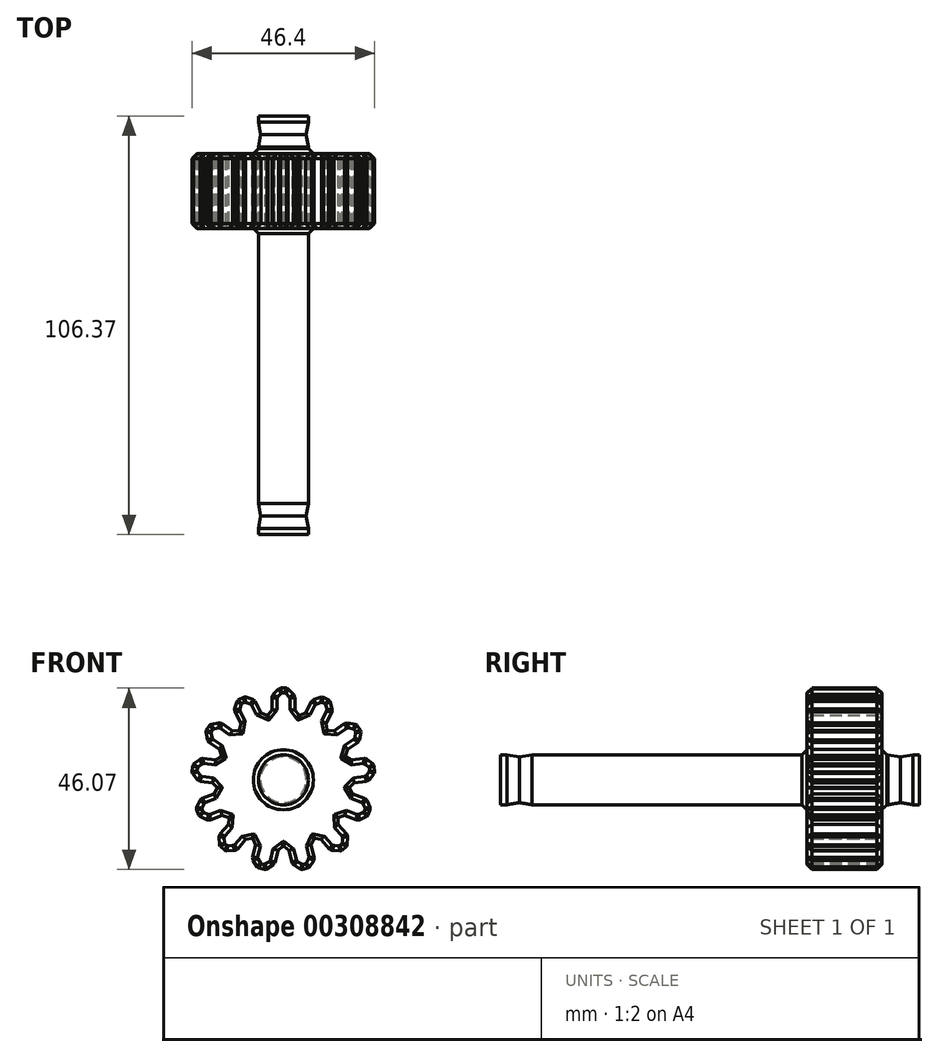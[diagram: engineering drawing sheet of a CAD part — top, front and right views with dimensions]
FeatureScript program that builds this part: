
annotation { "Feature Type Name" : "Feature", "Feature Type Description" : "" }
export const myFeature = defineFeature(function(context is Context, id is Id, definition is map)
    precondition{}
    {
        {
            var Q0;
            Q0=qCreatedBy(makeId("Front.planeOp"),FACE);
            var sketch = newSketch(context, id + "F0", { "sketchPlane" : qUnion([Q0])});
            skCircle(sketch, "E0", {"center": v(0, 0) * mm, "radius": 16.93 * mm});
            skCircle(sketch, "E1", {"center": v(0, 0) * mm, "radius": 6.35 * mm});
            skLineSegment(sketch, "E2.bottom", {"start": v(2.92, 23.28) * mm, "end": v(-2.92, 23.28) * mm});
            skLineSegment(sketch, "E2.top", {"start": v(2.92, 10.58) * mm, "end": v(-2.92, 10.58) * mm});
            skLineSegment(sketch, "E2.left", {"start": v(2.92, 23.28) * mm, "end": v(2.92, 10.58) * mm});
            skLineSegment(sketch, "E2.right", {"start": v(-2.92, 23.28) * mm, "end": v(-2.92, 10.58) * mm});
            skPoint(sketch, "E2.middle", {"position": v(0, 16.93) * mm});
            skLineSegment(sketch, "E3.1.0", {"start": v(7.5, 8.01) * mm, "end": v(2.33, 10.73) * mm});
            skLineSegment(sketch, "E3.1.1", {"start": v(13.4, 19.26) * mm, "end": v(7.5, 8.01) * mm});
            skLineSegment(sketch, "E3.1.2", {"start": v(13.4, 19.26) * mm, "end": v(8.23, 21.97) * mm});
            skLineSegment(sketch, "E3.1.3", {"start": v(8.23, 21.97) * mm, "end": v(2.33, 10.73) * mm});
            skLineSegment(sketch, "E3.2.0", {"start": v(10.37, 3.6) * mm, "end": v(7.05, 8.42) * mm});
            skLineSegment(sketch, "E3.2.1", {"start": v(20.82, 10.82) * mm, "end": v(10.37, 3.6) * mm});
            skLineSegment(sketch, "E3.2.2", {"start": v(20.82, 10.82) * mm, "end": v(17.5, 15.63) * mm});
            skLineSegment(sketch, "E3.2.3", {"start": v(17.5, 15.63) * mm, "end": v(7.05, 8.42) * mm});
            skLineSegment(sketch, "E3.3.0", {"start": v(10.86, -1.62) * mm, "end": v(10.15, 4.18) * mm});
            skLineSegment(sketch, "E3.3.1", {"start": v(23.47, -0.1) * mm, "end": v(10.86, -1.62) * mm});
            skLineSegment(sketch, "E3.3.2", {"start": v(23.47, -0.1) * mm, "end": v(22.76, 5.7) * mm});
            skLineSegment(sketch, "E3.3.3", {"start": v(22.76, 5.7) * mm, "end": v(10.15, 4.18) * mm});
            skLineSegment(sketch, "E3.4.0", {"start": v(8.86, -6.48) * mm, "end": v(10.93, -1.02) * mm});
            skLineSegment(sketch, "E3.4.1", {"start": v(20.73, -10.99) * mm, "end": v(8.86, -6.48) * mm});
            skLineSegment(sketch, "E3.4.2", {"start": v(20.73, -10.99) * mm, "end": v(22.8, -5.53) * mm});
            skLineSegment(sketch, "E3.4.3", {"start": v(22.8, -5.53) * mm, "end": v(10.93, -1.02) * mm});
            skLineSegment(sketch, "E3.5.0", {"start": v(4.83, -9.86) * mm, "end": v(9.2, -5.98) * mm});
            skLineSegment(sketch, "E3.5.1", {"start": v(13.25, -19.36) * mm, "end": v(4.83, -9.86) * mm});
            skLineSegment(sketch, "E3.5.2", {"start": v(13.25, -19.36) * mm, "end": v(17.63, -15.5) * mm});
            skLineSegment(sketch, "E3.5.3", {"start": v(17.63, -15.5) * mm, "end": v(9.2, -5.98) * mm});
            skLineSegment(sketch, "E3.6.0", {"start": v(-0.3, -10.97) * mm, "end": v(5.37, -9.58) * mm});
            skLineSegment(sketch, "E3.6.1", {"start": v(2.74, -23.3) * mm, "end": v(-0.3, -10.97) * mm});
            skLineSegment(sketch, "E3.6.2", {"start": v(2.74, -23.3) * mm, "end": v(8.4, -21.9) * mm});
            skLineSegment(sketch, "E3.6.3", {"start": v(8.4, -21.9) * mm, "end": v(5.37, -9.58) * mm});
            skLineSegment(sketch, "E3.7.0", {"start": v(-5.37, -9.58) * mm, "end": v(0.3, -10.97) * mm});
            skLineSegment(sketch, "E3.7.1", {"start": v(-8.4, -21.9) * mm, "end": v(-5.37, -9.58) * mm});
            skLineSegment(sketch, "E3.7.2", {"start": v(-8.4, -21.9) * mm, "end": v(-2.74, -23.3) * mm});
            skLineSegment(sketch, "E3.7.3", {"start": v(-2.74, -23.3) * mm, "end": v(0.3, -10.97) * mm});
            skLineSegment(sketch, "E3.8.0", {"start": v(-9.2, -5.98) * mm, "end": v(-4.83, -9.86) * mm});
            skLineSegment(sketch, "E3.8.1", {"start": v(-17.63, -15.5) * mm, "end": v(-9.2, -5.98) * mm});
            skLineSegment(sketch, "E3.8.2", {"start": v(-17.63, -15.5) * mm, "end": v(-13.25, -19.36) * mm});
            skLineSegment(sketch, "E3.8.3", {"start": v(-13.25, -19.36) * mm, "end": v(-4.83, -9.86) * mm});
            skLineSegment(sketch, "E3.9.0", {"start": v(-10.93, -1.02) * mm, "end": v(-8.86, -6.48) * mm});
            skLineSegment(sketch, "E3.9.1", {"start": v(-22.8, -5.53) * mm, "end": v(-10.93, -1.02) * mm});
            skLineSegment(sketch, "E3.9.2", {"start": v(-22.8, -5.53) * mm, "end": v(-20.73, -10.99) * mm});
            skLineSegment(sketch, "E3.9.3", {"start": v(-20.73, -10.99) * mm, "end": v(-8.86, -6.48) * mm});
            skLineSegment(sketch, "E3.10.0", {"start": v(-10.15, 4.18) * mm, "end": v(-10.86, -1.62) * mm});
            skLineSegment(sketch, "E3.10.1", {"start": v(-22.76, 5.7) * mm, "end": v(-10.15, 4.18) * mm});
            skLineSegment(sketch, "E3.10.2", {"start": v(-22.76, 5.7) * mm, "end": v(-23.47, -0.1) * mm});
            skLineSegment(sketch, "E3.10.3", {"start": v(-23.47, -0.1) * mm, "end": v(-10.86, -1.62) * mm});
            skLineSegment(sketch, "E3.11.0", {"start": v(-7.05, 8.42) * mm, "end": v(-10.37, 3.6) * mm});
            skLineSegment(sketch, "E3.11.1", {"start": v(-17.5, 15.63) * mm, "end": v(-7.05, 8.42) * mm});
            skLineSegment(sketch, "E3.11.2", {"start": v(-17.5, 15.63) * mm, "end": v(-20.82, 10.82) * mm});
            skLineSegment(sketch, "E3.11.3", {"start": v(-20.82, 10.82) * mm, "end": v(-10.37, 3.6) * mm});
            skLineSegment(sketch, "E3.12.0", {"start": v(-2.33, 10.73) * mm, "end": v(-7.5, 8.01) * mm});
            skLineSegment(sketch, "E3.12.1", {"start": v(-8.23, 21.97) * mm, "end": v(-2.33, 10.73) * mm});
            skLineSegment(sketch, "E3.12.2", {"start": v(-8.23, 21.97) * mm, "end": v(-13.4, 19.26) * mm});
            skLineSegment(sketch, "E3.12.3", {"start": v(-13.4, 19.26) * mm, "end": v(-7.5, 8.01) * mm});
            skLineSegment(sketch, "E3.anchor1", {"start": v(0, 0) * mm, "end": v(2.92, 10.58) * mm, "construction": true});
            skLineSegment(sketch, "E3.anchor2", {"start": v(0, 0) * mm, "end": v(-2.33, 10.73) * mm, "construction": true});
            skSolve(sketch);
        }
        {
            var Q0;
            {var subQ0=sQuery(id+"F0.wireOp",EDGE,"E2.left");var subQ1=sQuery(id+"F0.wireOp",EDGE,"E2.top");var subQ2=makeQuery(id+"F0.imprint","INTERSECT",VERTEX,{"derivedFrom":[subQ1,subQ0]});Q0=makeQuery(id+"F0.imprint","IMPRINT",FACE,{"disambiguationData":[TD([[makeQuery(id+"F0.imprint","IMPRINT",EDGE,{"disambiguationData":[TD([[subQ2,-1.0]])],"derivedFrom":subQ1}),-1.0]])]});}
            var Q1;
            {var subQ0=sQuery(id+"F0.wireOp",EDGE,"E2.right");var subQ1=sQuery(id+"F0.wireOp",EDGE,"E2.top");var subQ2=makeQuery(id+"F0.imprint","INTERSECT",VERTEX,{"derivedFrom":[subQ1,subQ0]});Q1=makeQuery(id+"F0.imprint","IMPRINT",FACE,{"disambiguationData":[TD([[makeQuery(id+"F0.imprint","IMPRINT",EDGE,{"disambiguationData":[TD([[subQ2,1.0]])],"derivedFrom":subQ1}),-1.0]])]});}
            var Q2;
            {var subQ0=sQuery(id+"F0.wireOp",EDGE,"E3.11.1");var subQ1=sQuery(id+"F0.wireOp",EDGE,"E3.11.0");var subQ2=makeQuery(id+"F0.imprint","INTERSECT",VERTEX,{"derivedFrom":[subQ1,subQ0]});Q2=makeQuery(id+"F0.imprint","IMPRINT",FACE,{"disambiguationData":[TD([[makeQuery(id+"F0.imprint","IMPRINT",EDGE,{"disambiguationData":[TD([[subQ2,-1.0]])],"derivedFrom":subQ1}),-1.0]])]});}
            var Q3;
            {var subQ0=sQuery(id+"F0.wireOp",EDGE,"E3.10.1");var subQ1=sQuery(id+"F0.wireOp",EDGE,"E3.10.0");var subQ2=makeQuery(id+"F0.imprint","INTERSECT",VERTEX,{"derivedFrom":[subQ1,subQ0]});Q3=makeQuery(id+"F0.imprint","IMPRINT",FACE,{"disambiguationData":[TD([[makeQuery(id+"F0.imprint","IMPRINT",EDGE,{"disambiguationData":[TD([[subQ2,-1.0]])],"derivedFrom":subQ1}),-1.0]])]});}
            var Q4;
            {var subQ0=sQuery(id+"F0.wireOp",EDGE,"E3.2.1");var subQ1=sQuery(id+"F0.wireOp",EDGE,"E0");var subQ2=makeQuery(id+"F0.imprint","INTERSECT",VERTEX,{"derivedFrom":[subQ1,subQ0]});Q4=makeQuery(id+"F0.imprint","IMPRINT",FACE,{"disambiguationData":[TD([[makeQuery(id+"F0.imprint","IMPRINT",EDGE,{"disambiguationData":[TD([[subQ2,1.0]])],"derivedFrom":subQ1}),1.0]])]});}
            var Q5;
            {var subQ11=sQuery(id+"F0.wireOp",EDGE,"E3.10.1");var subQ12=sQuery(id+"F0.wireOp",EDGE,"E0");var subQ13=makeQuery(id+"F0.imprint","INTERSECT",VERTEX,{"derivedFrom":[subQ12,subQ11]});Q5=makeQuery(id+"F0.imprint","IMPRINT",FACE,{"disambiguationData":[TD([[makeQuery(id+"F0.imprint","IMPRINT",EDGE,{"disambiguationData":[TD([[subQ13,-1.0]])],"derivedFrom":subQ12}),1.0]])]});}
            var Q6;
            {var subQ11=sQuery(id+"F0.wireOp",EDGE,"E3.5.1");var subQ12=sQuery(id+"F0.wireOp",EDGE,"E0");var subQ13=makeQuery(id+"F0.imprint","INTERSECT",VERTEX,{"derivedFrom":[subQ12,subQ11]});Q6=makeQuery(id+"F0.imprint","IMPRINT",FACE,{"disambiguationData":[TD([[makeQuery(id+"F0.imprint","IMPRINT",EDGE,{"disambiguationData":[TD([[subQ13,-1.0]])],"derivedFrom":subQ12}),1.0]])]});}
            var Q7;
            {var subQ5=sQuery(id+"F0.wireOp",EDGE,"E3.12.2");Q7=makeQuery(id+"F0.imprint","IMPRINT",FACE,{"disambiguationData":[TD([[makeQuery(id+"F0.imprint","IMPRINT",EDGE,{"derivedFrom":subQ5}),1.0]])]});}
            var Q8;
            {var subQ0=sQuery(id+"F0.wireOp",EDGE,"E3.4.3");var subQ1=sQuery(id+"F0.wireOp",EDGE,"E0");var subQ2=makeQuery(id+"F0.imprint","INTERSECT",VERTEX,{"derivedFrom":[subQ1,subQ0]});Q8=makeQuery(id+"F0.imprint","IMPRINT",FACE,{"disambiguationData":[TD([[makeQuery(id+"F0.imprint","IMPRINT",EDGE,{"disambiguationData":[TD([[subQ2,-1.0]])],"derivedFrom":subQ1}),1.0]])]});}
            var Q9;
            {var subQ0=sQuery(id+"F0.wireOp",EDGE,"E3.12.3");var subQ1=sQuery(id+"F0.wireOp",EDGE,"E0");var subQ2=makeQuery(id+"F0.imprint","INTERSECT",VERTEX,{"derivedFrom":[subQ1,subQ0]});Q9=makeQuery(id+"F0.imprint","IMPRINT",FACE,{"disambiguationData":[TD([[makeQuery(id+"F0.imprint","IMPRINT",EDGE,{"disambiguationData":[TD([[subQ2,-1.0]])],"derivedFrom":subQ1}),1.0]])]});}
            var Q10;
            {var subQ0=sQuery(id+"F0.wireOp",EDGE,"E3.6.3");var subQ1=sQuery(id+"F0.wireOp",EDGE,"E0");var subQ2=makeQuery(id+"F0.imprint","INTERSECT",VERTEX,{"derivedFrom":[subQ1,subQ0]});Q10=makeQuery(id+"F0.imprint","IMPRINT",FACE,{"disambiguationData":[TD([[makeQuery(id+"F0.imprint","IMPRINT",EDGE,{"disambiguationData":[TD([[subQ2,-1.0]])],"derivedFrom":subQ1}),1.0]])]});}
            var Q11;
            {var subQ5=sQuery(id+"F0.wireOp",EDGE,"E3.1.2");Q11=makeQuery(id+"F0.imprint","IMPRINT",FACE,{"disambiguationData":[TD([[makeQuery(id+"F0.imprint","IMPRINT",EDGE,{"derivedFrom":subQ5}),1.0]])]});}
            var Q12;
            {var subQ5=sQuery(id+"F0.wireOp",EDGE,"E3.9.2");Q12=makeQuery(id+"F0.imprint","IMPRINT",FACE,{"disambiguationData":[TD([[makeQuery(id+"F0.imprint","IMPRINT",EDGE,{"derivedFrom":subQ5}),1.0]])]});}
            var Q13;
            {var subQ5=sQuery(id+"F0.wireOp",EDGE,"E3.7.2");Q13=makeQuery(id+"F0.imprint","IMPRINT",FACE,{"disambiguationData":[TD([[makeQuery(id+"F0.imprint","IMPRINT",EDGE,{"derivedFrom":subQ5}),1.0]])]});}
            var Q14;
            {var subQ11=sQuery(id+"F0.wireOp",EDGE,"E3.7.1");var subQ12=sQuery(id+"F0.wireOp",EDGE,"E0");var subQ13=makeQuery(id+"F0.imprint","INTERSECT",VERTEX,{"derivedFrom":[subQ12,subQ11]});Q14=makeQuery(id+"F0.imprint","IMPRINT",FACE,{"disambiguationData":[TD([[makeQuery(id+"F0.imprint","IMPRINT",EDGE,{"disambiguationData":[TD([[subQ13,-1.0]])],"derivedFrom":subQ12}),1.0]])]});}
            var Q15;
            {var subQ5=sQuery(id+"F0.wireOp",EDGE,"E3.5.2");Q15=makeQuery(id+"F0.imprint","IMPRINT",FACE,{"disambiguationData":[TD([[makeQuery(id+"F0.imprint","IMPRINT",EDGE,{"derivedFrom":subQ5}),1.0]])]});}
            var Q16;
            {var subQ11=sQuery(id+"F0.wireOp",EDGE,"E3.6.1");var subQ12=sQuery(id+"F0.wireOp",EDGE,"E0");var subQ13=makeQuery(id+"F0.imprint","INTERSECT",VERTEX,{"derivedFrom":[subQ12,subQ11]});Q16=makeQuery(id+"F0.imprint","IMPRINT",FACE,{"disambiguationData":[TD([[makeQuery(id+"F0.imprint","IMPRINT",EDGE,{"disambiguationData":[TD([[subQ13,-1.0]])],"derivedFrom":subQ12}),1.0]])]});}
            var Q17;
            {var subQ5=sQuery(id+"F0.wireOp",EDGE,"E3.4.2");Q17=makeQuery(id+"F0.imprint","IMPRINT",FACE,{"disambiguationData":[TD([[makeQuery(id+"F0.imprint","IMPRINT",EDGE,{"derivedFrom":subQ5}),1.0]])]});}
            var Q18;
            {var subQ11=sQuery(id+"F0.wireOp",EDGE,"E3.11.1");var subQ12=sQuery(id+"F0.wireOp",EDGE,"E0");var subQ13=makeQuery(id+"F0.imprint","INTERSECT",VERTEX,{"derivedFrom":[subQ12,subQ11]});Q18=makeQuery(id+"F0.imprint","IMPRINT",FACE,{"disambiguationData":[TD([[makeQuery(id+"F0.imprint","IMPRINT",EDGE,{"disambiguationData":[TD([[subQ13,-1.0]])],"derivedFrom":subQ12}),1.0]])]});}
            var Q19;
            {var subQ0=sQuery(id+"F0.wireOp",EDGE,"E3.8.3");var subQ1=sQuery(id+"F0.wireOp",EDGE,"E0");var subQ2=makeQuery(id+"F0.imprint","INTERSECT",VERTEX,{"derivedFrom":[subQ1,subQ0]});Q19=makeQuery(id+"F0.imprint","IMPRINT",FACE,{"disambiguationData":[TD([[makeQuery(id+"F0.imprint","IMPRINT",EDGE,{"disambiguationData":[TD([[subQ2,-1.0]])],"derivedFrom":subQ1}),1.0]])]});}
            var Q20;
            {var subQ0=sQuery(id+"F0.wireOp",EDGE,"E3.1.3");var subQ1=sQuery(id+"F0.wireOp",EDGE,"E0");var subQ2=makeQuery(id+"F0.imprint","INTERSECT",VERTEX,{"derivedFrom":[subQ1,subQ0]});Q20=makeQuery(id+"F0.imprint","IMPRINT",FACE,{"disambiguationData":[TD([[makeQuery(id+"F0.imprint","IMPRINT",EDGE,{"disambiguationData":[TD([[subQ2,-1.0]])],"derivedFrom":subQ1}),1.0]])]});}
            var Q21;
            {var subQ5=sQuery(id+"F0.wireOp",EDGE,"E2.bottom");Q21=makeQuery(id+"F0.imprint","IMPRINT",FACE,{"disambiguationData":[TD([[makeQuery(id+"F0.imprint","IMPRINT",EDGE,{"derivedFrom":subQ5}),1.0]])]});}
            var Q22;
            {var subQ5=sQuery(id+"F0.wireOp",EDGE,"E3.3.2");Q22=makeQuery(id+"F0.imprint","IMPRINT",FACE,{"disambiguationData":[TD([[makeQuery(id+"F0.imprint","IMPRINT",EDGE,{"derivedFrom":subQ5}),1.0]])]});}
            var Q23;
            {var subQ0=sQuery(id+"F0.wireOp",EDGE,"E3.11.3");var subQ1=sQuery(id+"F0.wireOp",EDGE,"E0");var subQ2=makeQuery(id+"F0.imprint","INTERSECT",VERTEX,{"derivedFrom":[subQ1,subQ0]});Q23=makeQuery(id+"F0.imprint","IMPRINT",FACE,{"disambiguationData":[TD([[makeQuery(id+"F0.imprint","IMPRINT",EDGE,{"disambiguationData":[TD([[subQ2,-1.0]])],"derivedFrom":subQ1}),1.0]])]});}
            var Q24;
            {var subQ0=sQuery(id+"F0.wireOp",EDGE,"E3.7.3");var subQ1=sQuery(id+"F0.wireOp",EDGE,"E0");var subQ2=makeQuery(id+"F0.imprint","INTERSECT",VERTEX,{"derivedFrom":[subQ1,subQ0]});Q24=makeQuery(id+"F0.imprint","IMPRINT",FACE,{"disambiguationData":[TD([[makeQuery(id+"F0.imprint","IMPRINT",EDGE,{"disambiguationData":[TD([[subQ2,-1.0]])],"derivedFrom":subQ1}),1.0]])]});}
            var Q25;
            {var subQ5=sQuery(id+"F0.wireOp",EDGE,"E3.2.2");Q25=makeQuery(id+"F0.imprint","IMPRINT",FACE,{"disambiguationData":[TD([[makeQuery(id+"F0.imprint","IMPRINT",EDGE,{"derivedFrom":subQ5}),1.0]])]});}
            var Q26;
            {var subQ5=sQuery(id+"F0.wireOp",EDGE,"E3.6.2");Q26=makeQuery(id+"F0.imprint","IMPRINT",FACE,{"disambiguationData":[TD([[makeQuery(id+"F0.imprint","IMPRINT",EDGE,{"derivedFrom":subQ5}),1.0]])]});}
            var Q27;
            {var subQ5=sQuery(id+"F0.wireOp",EDGE,"E3.11.2");Q27=makeQuery(id+"F0.imprint","IMPRINT",FACE,{"disambiguationData":[TD([[makeQuery(id+"F0.imprint","IMPRINT",EDGE,{"derivedFrom":subQ5}),1.0]])]});}
            var Q28;
            {var subQ11=sQuery(id+"F0.wireOp",EDGE,"E3.8.1");var subQ12=sQuery(id+"F0.wireOp",EDGE,"E0");var subQ13=makeQuery(id+"F0.imprint","INTERSECT",VERTEX,{"derivedFrom":[subQ12,subQ11]});Q28=makeQuery(id+"F0.imprint","IMPRINT",FACE,{"disambiguationData":[TD([[makeQuery(id+"F0.imprint","IMPRINT",EDGE,{"disambiguationData":[TD([[subQ13,-1.0]])],"derivedFrom":subQ12}),1.0]])]});}
            var Q29;
            {var subQ5=sQuery(id+"F0.wireOp",EDGE,"E3.10.2");Q29=makeQuery(id+"F0.imprint","IMPRINT",FACE,{"disambiguationData":[TD([[makeQuery(id+"F0.imprint","IMPRINT",EDGE,{"derivedFrom":subQ5}),1.0]])]});}
            var Q30;
            {var subQ3=sQuery(id+"F0.wireOp",EDGE,"E3.12.1");var subQ7=sQuery(id+"F0.wireOp",EDGE,"E0");var subQ8=makeQuery(id+"F0.imprint","INTERSECT",VERTEX,{"derivedFrom":[subQ7,subQ3]});Q30=makeQuery(id+"F0.imprint","IMPRINT",FACE,{"disambiguationData":[TD([[makeQuery(id+"F0.imprint","IMPRINT",EDGE,{"disambiguationData":[TD([[subQ8,-1.0]])],"derivedFrom":subQ7}),1.0]])]});}
            var Q31;
            {var subQ7=sQuery(id+"F0.wireOp",EDGE,"E3.3.3");var subQ8=sQuery(id+"F0.wireOp",EDGE,"E0");var subQ9=makeQuery(id+"F0.imprint","INTERSECT",VERTEX,{"derivedFrom":[subQ8,subQ7]});Q31=makeQuery(id+"F0.imprint","IMPRINT",FACE,{"disambiguationData":[TD([[makeQuery(id+"F0.imprint","IMPRINT",EDGE,{"disambiguationData":[TD([[subQ9,1.0]])],"derivedFrom":subQ8}),1.0]])]});}
            var Q32;
            {var subQ0=sQuery(id+"F0.wireOp",EDGE,"E3.2.3");var subQ1=sQuery(id+"F0.wireOp",EDGE,"E0");var subQ2=makeQuery(id+"F0.imprint","INTERSECT",VERTEX,{"derivedFrom":[subQ1,subQ0]});Q32=makeQuery(id+"F0.imprint","IMPRINT",FACE,{"disambiguationData":[TD([[makeQuery(id+"F0.imprint","IMPRINT",EDGE,{"disambiguationData":[TD([[subQ2,-1.0]])],"derivedFrom":subQ1}),1.0]])]});}
            var Q33;
            {var subQ0=sQuery(id+"F0.wireOp",EDGE,"E3.5.3");var subQ1=sQuery(id+"F0.wireOp",EDGE,"E0");var subQ2=makeQuery(id+"F0.imprint","INTERSECT",VERTEX,{"derivedFrom":[subQ1,subQ0]});Q33=makeQuery(id+"F0.imprint","IMPRINT",FACE,{"disambiguationData":[TD([[makeQuery(id+"F0.imprint","IMPRINT",EDGE,{"disambiguationData":[TD([[subQ2,-1.0]])],"derivedFrom":subQ1}),1.0]])]});}
            var Q34;
            {var subQ0=sQuery(id+"F0.wireOp",EDGE,"E3.9.3");var subQ1=sQuery(id+"F0.wireOp",EDGE,"E0");var subQ2=makeQuery(id+"F0.imprint","INTERSECT",VERTEX,{"derivedFrom":[subQ1,subQ0]});Q34=makeQuery(id+"F0.imprint","IMPRINT",FACE,{"disambiguationData":[TD([[makeQuery(id+"F0.imprint","IMPRINT",EDGE,{"disambiguationData":[TD([[subQ2,-1.0]])],"derivedFrom":subQ1}),1.0]])]});}
            var Q35;
            {var subQ5=sQuery(id+"F0.wireOp",EDGE,"E3.8.2");Q35=makeQuery(id+"F0.imprint","IMPRINT",FACE,{"disambiguationData":[TD([[makeQuery(id+"F0.imprint","IMPRINT",EDGE,{"derivedFrom":subQ5}),1.0]])]});}
            var Q36;
            {var subQ0=sQuery(id+"F0.wireOp",EDGE,"E2.left");var subQ1=sQuery(id+"F0.wireOp",EDGE,"E0");var subQ2=makeQuery(id+"F0.imprint","INTERSECT",VERTEX,{"derivedFrom":[subQ1,subQ0]});Q36=makeQuery(id+"F0.imprint","IMPRINT",FACE,{"disambiguationData":[TD([[makeQuery(id+"F0.imprint","IMPRINT",EDGE,{"disambiguationData":[TD([[subQ2,-1.0]])],"derivedFrom":subQ1}),1.0]])]});}
            var Q37;
            {var subQ0=sQuery(id+"F0.wireOp",EDGE,"E2.right");var subQ1=sQuery(id+"F0.wireOp",EDGE,"E0");var subQ2=makeQuery(id+"F0.imprint","INTERSECT",VERTEX,{"derivedFrom":[subQ1,subQ0]});Q37=makeQuery(id+"F0.imprint","IMPRINT",FACE,{"disambiguationData":[TD([[makeQuery(id+"F0.imprint","IMPRINT",EDGE,{"disambiguationData":[TD([[subQ2,-1.0]])],"derivedFrom":subQ1}),1.0]])]});}
            var Q38;
            {var subQ0=sQuery(id+"F0.wireOp",EDGE,"E3.10.3");var subQ1=sQuery(id+"F0.wireOp",EDGE,"E0");var subQ2=makeQuery(id+"F0.imprint","INTERSECT",VERTEX,{"derivedFrom":[subQ1,subQ0]});Q38=makeQuery(id+"F0.imprint","IMPRINT",FACE,{"disambiguationData":[TD([[makeQuery(id+"F0.imprint","IMPRINT",EDGE,{"disambiguationData":[TD([[subQ2,-1.0]])],"derivedFrom":subQ1}),1.0]])]});}
            var Q39;
            Q39=makeQuery(id+"F0.imprint","IMPRINT",FACE,{"disambiguationData":[TD([[makeQuery(id+"F0.imprint","IMPRINT",EDGE,{"derivedFrom":sQuery(id+"F0.wireOp",EDGE,"E1")}),-1.0]])]});
            var Q40;
            {var subQ0=sQuery(id+"F0.wireOp",EDGE,"E3.9.1");var subQ1=sQuery(id+"F0.wireOp",EDGE,"E3.9.0");var subQ2=makeQuery(id+"F0.imprint","INTERSECT",VERTEX,{"derivedFrom":[subQ1,subQ0]});Q40=makeQuery(id+"F0.imprint","IMPRINT",FACE,{"disambiguationData":[TD([[makeQuery(id+"F0.imprint","IMPRINT",EDGE,{"disambiguationData":[TD([[subQ2,-1.0]])],"derivedFrom":subQ1}),-1.0]])]});}
            var Q41;
            {var subQ5=sQuery(id+"F0.wireOp",EDGE,"E3.9.1");var subQ6=sQuery(id+"F0.wireOp",EDGE,"E0");var subQ7=makeQuery(id+"F0.imprint","INTERSECT",VERTEX,{"derivedFrom":[subQ6,subQ5]});Q41=makeQuery(id+"F0.imprint","IMPRINT",FACE,{"disambiguationData":[TD([[makeQuery(id+"F0.imprint","IMPRINT",EDGE,{"disambiguationData":[TD([[subQ7,-1.0]])],"derivedFrom":subQ6}),1.0]])]});}
            var Q42;
            {var subQ0=sQuery(id+"F0.wireOp",EDGE,"E3.7.1");var subQ1=sQuery(id+"F0.wireOp",EDGE,"E3.7.0");var subQ2=makeQuery(id+"F0.imprint","INTERSECT",VERTEX,{"derivedFrom":[subQ1,subQ0]});Q42=makeQuery(id+"F0.imprint","IMPRINT",FACE,{"disambiguationData":[TD([[makeQuery(id+"F0.imprint","IMPRINT",EDGE,{"disambiguationData":[TD([[subQ2,-1.0]])],"derivedFrom":subQ1}),-1.0]])]});}
            var Q43;
            {var subQ0=sQuery(id+"F0.wireOp",EDGE,"E3.8.1");var subQ1=sQuery(id+"F0.wireOp",EDGE,"E3.8.0");var subQ2=makeQuery(id+"F0.imprint","INTERSECT",VERTEX,{"derivedFrom":[subQ1,subQ0]});Q43=makeQuery(id+"F0.imprint","IMPRINT",FACE,{"disambiguationData":[TD([[makeQuery(id+"F0.imprint","IMPRINT",EDGE,{"disambiguationData":[TD([[subQ2,-1.0]])],"derivedFrom":subQ1}),-1.0]])]});}
            var Q44;
            {var subQ0=sQuery(id+"F0.wireOp",EDGE,"E3.6.1");var subQ1=sQuery(id+"F0.wireOp",EDGE,"E3.6.0");var subQ2=makeQuery(id+"F0.imprint","INTERSECT",VERTEX,{"derivedFrom":[subQ1,subQ0]});Q44=makeQuery(id+"F0.imprint","IMPRINT",FACE,{"disambiguationData":[TD([[makeQuery(id+"F0.imprint","IMPRINT",EDGE,{"disambiguationData":[TD([[subQ2,-1.0]])],"derivedFrom":subQ1}),-1.0]])]});}
            var Q45;
            {var subQ0=sQuery(id+"F0.wireOp",EDGE,"E3.5.1");var subQ1=sQuery(id+"F0.wireOp",EDGE,"E3.5.0");var subQ2=makeQuery(id+"F0.imprint","INTERSECT",VERTEX,{"derivedFrom":[subQ1,subQ0]});Q45=makeQuery(id+"F0.imprint","IMPRINT",FACE,{"disambiguationData":[TD([[makeQuery(id+"F0.imprint","IMPRINT",EDGE,{"disambiguationData":[TD([[subQ2,-1.0]])],"derivedFrom":subQ1}),-1.0]])]});}
            var Q46;
            {var subQ11=sQuery(id+"F0.wireOp",EDGE,"E3.4.1");var subQ12=sQuery(id+"F0.wireOp",EDGE,"E0");var subQ13=makeQuery(id+"F0.imprint","INTERSECT",VERTEX,{"derivedFrom":[subQ12,subQ11]});Q46=makeQuery(id+"F0.imprint","IMPRINT",FACE,{"disambiguationData":[TD([[makeQuery(id+"F0.imprint","IMPRINT",EDGE,{"disambiguationData":[TD([[subQ13,-1.0]])],"derivedFrom":subQ12}),1.0]])]});}
            var Q47;
            {var subQ0=sQuery(id+"F0.wireOp",EDGE,"E3.3.1");var subQ1=sQuery(id+"F0.wireOp",EDGE,"E3.3.0");var subQ2=makeQuery(id+"F0.imprint","INTERSECT",VERTEX,{"derivedFrom":[subQ1,subQ0]});Q47=makeQuery(id+"F0.imprint","IMPRINT",FACE,{"disambiguationData":[TD([[makeQuery(id+"F0.imprint","IMPRINT",EDGE,{"disambiguationData":[TD([[subQ2,-1.0]])],"derivedFrom":subQ1}),-1.0]])]});}
            var Q48;
            {var subQ11=sQuery(id+"F0.wireOp",EDGE,"E3.2.1");var subQ12=sQuery(id+"F0.wireOp",EDGE,"E0");var subQ13=makeQuery(id+"F0.imprint","INTERSECT",VERTEX,{"derivedFrom":[subQ12,subQ11]});Q48=makeQuery(id+"F0.imprint","IMPRINT",FACE,{"disambiguationData":[TD([[makeQuery(id+"F0.imprint","IMPRINT",EDGE,{"disambiguationData":[TD([[subQ13,-1.0]])],"derivedFrom":subQ12}),1.0]])]});}
            var Q49;
            {var subQ0=sQuery(id+"F0.wireOp",EDGE,"E3.2.1");var subQ1=sQuery(id+"F0.wireOp",EDGE,"E3.2.0");var subQ2=makeQuery(id+"F0.imprint","INTERSECT",VERTEX,{"derivedFrom":[subQ1,subQ0]});Q49=makeQuery(id+"F0.imprint","IMPRINT",FACE,{"disambiguationData":[TD([[makeQuery(id+"F0.imprint","IMPRINT",EDGE,{"disambiguationData":[TD([[subQ2,-1.0]])],"derivedFrom":subQ1}),-1.0]])]});}
            var Q50;
            {var subQ11=sQuery(id+"F0.wireOp",EDGE,"E3.1.1");var subQ12=sQuery(id+"F0.wireOp",EDGE,"E0");var subQ13=makeQuery(id+"F0.imprint","INTERSECT",VERTEX,{"derivedFrom":[subQ12,subQ11]});Q50=makeQuery(id+"F0.imprint","IMPRINT",FACE,{"disambiguationData":[TD([[makeQuery(id+"F0.imprint","IMPRINT",EDGE,{"disambiguationData":[TD([[subQ13,-1.0]])],"derivedFrom":subQ12}),1.0]])]});}
            var Q51;
            {var subQ0=sQuery(id+"F0.wireOp",EDGE,"E3.1.1");var subQ1=sQuery(id+"F0.wireOp",EDGE,"E3.1.0");var subQ2=makeQuery(id+"F0.imprint","INTERSECT",VERTEX,{"derivedFrom":[subQ1,subQ0]});Q51=makeQuery(id+"F0.imprint","IMPRINT",FACE,{"disambiguationData":[TD([[makeQuery(id+"F0.imprint","IMPRINT",EDGE,{"disambiguationData":[TD([[subQ2,-1.0]])],"derivedFrom":subQ1}),-1.0]])]});}
            var Q52;
            {var subQ0=sQuery(id+"F0.wireOp",EDGE,"E3.4.1");var subQ1=sQuery(id+"F0.wireOp",EDGE,"E3.4.0");var subQ2=makeQuery(id+"F0.imprint","INTERSECT",VERTEX,{"derivedFrom":[subQ1,subQ0]});Q52=makeQuery(id+"F0.imprint","IMPRINT",FACE,{"disambiguationData":[TD([[makeQuery(id+"F0.imprint","IMPRINT",EDGE,{"disambiguationData":[TD([[subQ2,-1.0]])],"derivedFrom":subQ1}),-1.0]])]});}
            extrude(context, id + "F1", {"entities" : qUnion([Q0, Q1, Q2, Q3, Q4, Q5, Q6, Q7, Q8, Q9, Q10, Q11, Q12, Q13, Q14, Q15, Q16, Q17, Q18, Q19, Q20, Q21, Q22, Q23, Q24, Q25, Q26, Q27, Q28, Q29, Q30, Q31, Q32, Q33, Q34, Q35, Q36, Q37, Q38, Q39, Q40, Q41, Q42, Q43, Q44, Q45, Q46, Q47, Q48, Q49, Q50, Q51, Q52]), "depth" : 19.05 * mm});
        }
        {
            var Q0;
            Q0=makeQuery(id+"F0.imprint","IMPRINT",FACE,{"disambiguationData":[TD([[makeQuery(id+"F0.imprint","IMPRINT",EDGE,{"derivedFrom":sQuery(id+"F0.wireOp",EDGE,"E1")}),1.0]])]});
            extrude(context, id + "F2", {"entities" : qUnion([Q0]), "operationType" : NewBodyOperationType.ADD, "depth" : 88.9 * mm, "hasSecondDirection" : true, "secondDirectionOppositeDirection" : true, "secondDirectionDepth" : 1.59 * mm});
        }
        {
            var Q0;
            Q0=makeQuery(id+"F1.opExtrude","SWEPT_EDGE",EDGE,{"disambiguationData":[OSD([sQuery(id+"F0.wireOp",EDGE,"E3.1.1"),sQuery(id+"F0.wireOp",EDGE,"E3.1.2")])]});
            var Q1;
            Q1=makeQuery(id+"F1.opExtrude","SWEPT_EDGE",EDGE,{"disambiguationData":[OSD([sQuery(id+"F0.wireOp",EDGE,"E3.1.2"),sQuery(id+"F0.wireOp",EDGE,"E3.1.3")])]});
            var Q2;
            Q2=makeQuery(id+"F1.opExtrude","SWEPT_EDGE",EDGE,{"disambiguationData":[OSD([sQuery(id+"F0.wireOp",EDGE,"E2.bottom"),sQuery(id+"F0.wireOp",EDGE,"E2.left")])]});
            var Q3;
            Q3=makeQuery(id+"F1.opExtrude","SWEPT_EDGE",EDGE,{"disambiguationData":[OSD([sQuery(id+"F0.wireOp",EDGE,"E2.bottom"),sQuery(id+"F0.wireOp",EDGE,"E2.right")])]});
            var Q4;
            Q4=makeQuery(id+"F1.opExtrude","SWEPT_EDGE",EDGE,{"disambiguationData":[OSD([sQuery(id+"F0.wireOp",EDGE,"E3.2.2"),sQuery(id+"F0.wireOp",EDGE,"E3.2.3")])]});
            var Q5;
            Q5=makeQuery(id+"F1.opExtrude","SWEPT_EDGE",EDGE,{"disambiguationData":[OSD([sQuery(id+"F0.wireOp",EDGE,"E3.2.1"),sQuery(id+"F0.wireOp",EDGE,"E3.2.2")])]});
            var Q6;
            Q6=makeQuery(id+"F1.opExtrude","SWEPT_EDGE",EDGE,{"disambiguationData":[OSD([sQuery(id+"F0.wireOp",EDGE,"E3.3.2"),sQuery(id+"F0.wireOp",EDGE,"E3.3.3")])]});
            var Q7;
            Q7=makeQuery(id+"F1.opExtrude","SWEPT_EDGE",EDGE,{"disambiguationData":[OSD([sQuery(id+"F0.wireOp",EDGE,"E3.4.2"),sQuery(id+"F0.wireOp",EDGE,"E3.4.3")])]});
            var Q8;
            Q8=makeQuery(id+"F1.opExtrude","SWEPT_EDGE",EDGE,{"disambiguationData":[OSD([sQuery(id+"F0.wireOp",EDGE,"E3.3.1"),sQuery(id+"F0.wireOp",EDGE,"E3.3.2")])]});
            var Q9;
            Q9=makeQuery(id+"F1.opExtrude","SWEPT_EDGE",EDGE,{"disambiguationData":[OSD([sQuery(id+"F0.wireOp",EDGE,"E3.4.1"),sQuery(id+"F0.wireOp",EDGE,"E3.4.2")])]});
            var Q10;
            Q10=makeQuery(id+"F1.opExtrude","SWEPT_EDGE",EDGE,{"disambiguationData":[OSD([sQuery(id+"F0.wireOp",EDGE,"E3.5.2"),sQuery(id+"F0.wireOp",EDGE,"E3.5.3")])]});
            var Q11;
            Q11=makeQuery(id+"F1.opExtrude","SWEPT_EDGE",EDGE,{"disambiguationData":[OSD([sQuery(id+"F0.wireOp",EDGE,"E3.6.2"),sQuery(id+"F0.wireOp",EDGE,"E3.6.3")])]});
            var Q12;
            Q12=makeQuery(id+"F1.opExtrude","SWEPT_EDGE",EDGE,{"disambiguationData":[OSD([sQuery(id+"F0.wireOp",EDGE,"E3.5.1"),sQuery(id+"F0.wireOp",EDGE,"E3.5.2")])]});
            var Q13;
            Q13=makeQuery(id+"F1.opExtrude","SWEPT_EDGE",EDGE,{"disambiguationData":[OSD([sQuery(id+"F0.wireOp",EDGE,"E3.6.1"),sQuery(id+"F0.wireOp",EDGE,"E3.6.2")])]});
            var Q14;
            Q14=makeQuery(id+"F1.opExtrude","SWEPT_EDGE",EDGE,{"disambiguationData":[OSD([sQuery(id+"F0.wireOp",EDGE,"E3.7.2"),sQuery(id+"F0.wireOp",EDGE,"E3.7.3")])]});
            var Q15;
            Q15=makeQuery(id+"F1.opExtrude","SWEPT_EDGE",EDGE,{"disambiguationData":[OSD([sQuery(id+"F0.wireOp",EDGE,"E3.7.1"),sQuery(id+"F0.wireOp",EDGE,"E3.7.2")])]});
            var Q16;
            Q16=makeQuery(id+"F1.opExtrude","SWEPT_EDGE",EDGE,{"disambiguationData":[OSD([sQuery(id+"F0.wireOp",EDGE,"E3.8.2"),sQuery(id+"F0.wireOp",EDGE,"E3.8.3")])]});
            var Q17;
            Q17=makeQuery(id+"F1.opExtrude","SWEPT_EDGE",EDGE,{"disambiguationData":[OSD([sQuery(id+"F0.wireOp",EDGE,"E3.8.1"),sQuery(id+"F0.wireOp",EDGE,"E3.8.2")])]});
            var Q18;
            Q18=makeQuery(id+"F1.opExtrude","SWEPT_EDGE",EDGE,{"disambiguationData":[OSD([sQuery(id+"F0.wireOp",EDGE,"E3.9.1"),sQuery(id+"F0.wireOp",EDGE,"E3.9.2")])]});
            var Q19;
            Q19=makeQuery(id+"F1.opExtrude","SWEPT_EDGE",EDGE,{"disambiguationData":[OSD([sQuery(id+"F0.wireOp",EDGE,"E3.9.2"),sQuery(id+"F0.wireOp",EDGE,"E3.9.3")])]});
            var Q20;
            Q20=makeQuery(id+"F1.opExtrude","SWEPT_EDGE",EDGE,{"disambiguationData":[OSD([sQuery(id+"F0.wireOp",EDGE,"E3.12.2"),sQuery(id+"F0.wireOp",EDGE,"E3.12.3")])]});
            var Q21;
            Q21=makeQuery(id+"F1.opExtrude","SWEPT_EDGE",EDGE,{"disambiguationData":[OSD([sQuery(id+"F0.wireOp",EDGE,"E3.12.1"),sQuery(id+"F0.wireOp",EDGE,"E3.12.2")])]});
            var Q22;
            Q22=makeQuery(id+"F1.opExtrude","SWEPT_EDGE",EDGE,{"disambiguationData":[OSD([sQuery(id+"F0.wireOp",EDGE,"E3.11.1"),sQuery(id+"F0.wireOp",EDGE,"E3.11.2")])]});
            var Q23;
            Q23=makeQuery(id+"F1.opExtrude","SWEPT_EDGE",EDGE,{"disambiguationData":[OSD([sQuery(id+"F0.wireOp",EDGE,"E3.11.2"),sQuery(id+"F0.wireOp",EDGE,"E3.11.3")])]});
            var Q24;
            Q24=makeQuery(id+"F1.opExtrude","SWEPT_EDGE",EDGE,{"disambiguationData":[OSD([sQuery(id+"F0.wireOp",EDGE,"E3.10.1"),sQuery(id+"F0.wireOp",EDGE,"E3.10.2")])]});
            var Q25;
            Q25=makeQuery(id+"F1.opExtrude","SWEPT_EDGE",EDGE,{"disambiguationData":[OSD([sQuery(id+"F0.wireOp",EDGE,"E3.10.2"),sQuery(id+"F0.wireOp",EDGE,"E3.10.3")])]});
            chamfer(context, id + "F3", {"entities" : qUnion([Q0, Q1, Q2, Q3, Q4, Q5, Q6, Q7, Q8, Q9, Q10, Q11, Q12, Q13, Q14, Q15, Q16, Q17, Q18, Q19, Q20, Q21, Q22, Q23, Q24, Q25]), "width" : 1.9 * mm, "tangentPropagation" : true});
        }
        {
            var Q0;
            Q0=makeQuery(id+"F1.opExtrude","CAP_FACE",FACE,{"disambiguationData":[OSD([sQuery(id+"F0.wireOp",EDGE,"E0"),sQuery(id+"F0.wireOp",EDGE,"E1"),sQuery(id+"F0.wireOp",EDGE,"E2.bottom"),sQuery(id+"F0.wireOp",EDGE,"E2.left"),sQuery(id+"F0.wireOp",EDGE,"E2.right"),sQuery(id+"F0.wireOp",EDGE,"E3.1.1"),sQuery(id+"F0.wireOp",EDGE,"E3.1.2"),sQuery(id+"F0.wireOp",EDGE,"E3.1.3"),sQuery(id+"F0.wireOp",EDGE,"E3.2.1"),sQuery(id+"F0.wireOp",EDGE,"E3.2.2"),sQuery(id+"F0.wireOp",EDGE,"E3.2.3"),sQuery(id+"F0.wireOp",EDGE,"E3.3.1"),sQuery(id+"F0.wireOp",EDGE,"E3.3.2"),sQuery(id+"F0.wireOp",EDGE,"E3.3.3"),sQuery(id+"F0.wireOp",EDGE,"E3.4.1"),sQuery(id+"F0.wireOp",EDGE,"E3.4.2"),sQuery(id+"F0.wireOp",EDGE,"E3.4.3"),sQuery(id+"F0.wireOp",EDGE,"E3.5.1"),sQuery(id+"F0.wireOp",EDGE,"E3.5.2"),sQuery(id+"F0.wireOp",EDGE,"E3.5.3"),sQuery(id+"F0.wireOp",EDGE,"E3.6.1"),sQuery(id+"F0.wireOp",EDGE,"E3.6.2"),sQuery(id+"F0.wireOp",EDGE,"E3.6.3"),sQuery(id+"F0.wireOp",EDGE,"E3.7.1"),sQuery(id+"F0.wireOp",EDGE,"E3.7.2"),sQuery(id+"F0.wireOp",EDGE,"E3.7.3"),sQuery(id+"F0.wireOp",EDGE,"E3.8.1"),sQuery(id+"F0.wireOp",EDGE,"E3.8.2"),sQuery(id+"F0.wireOp",EDGE,"E3.8.3"),sQuery(id+"F0.wireOp",EDGE,"E3.9.1"),sQuery(id+"F0.wireOp",EDGE,"E3.9.2"),sQuery(id+"F0.wireOp",EDGE,"E3.9.3"),sQuery(id+"F0.wireOp",EDGE,"E3.10.1"),sQuery(id+"F0.wireOp",EDGE,"E3.10.2"),sQuery(id+"F0.wireOp",EDGE,"E3.10.3"),sQuery(id+"F0.wireOp",EDGE,"E3.11.1"),sQuery(id+"F0.wireOp",EDGE,"E3.11.2"),sQuery(id+"F0.wireOp",EDGE,"E3.11.3"),sQuery(id+"F0.wireOp",EDGE,"E3.12.1"),sQuery(id+"F0.wireOp",EDGE,"E3.12.2"),sQuery(id+"F0.wireOp",EDGE,"E3.12.3")])],"isStart":false});
            var Q1;
            Q1=makeQuery(id+"F1.opExtrude","CAP_FACE",FACE,{"disambiguationData":[OSD([sQuery(id+"F0.wireOp",EDGE,"E0"),sQuery(id+"F0.wireOp",EDGE,"E1"),sQuery(id+"F0.wireOp",EDGE,"E2.bottom"),sQuery(id+"F0.wireOp",EDGE,"E2.left"),sQuery(id+"F0.wireOp",EDGE,"E2.right"),sQuery(id+"F0.wireOp",EDGE,"E3.1.1"),sQuery(id+"F0.wireOp",EDGE,"E3.1.2"),sQuery(id+"F0.wireOp",EDGE,"E3.1.3"),sQuery(id+"F0.wireOp",EDGE,"E3.2.1"),sQuery(id+"F0.wireOp",EDGE,"E3.2.2"),sQuery(id+"F0.wireOp",EDGE,"E3.2.3"),sQuery(id+"F0.wireOp",EDGE,"E3.3.1"),sQuery(id+"F0.wireOp",EDGE,"E3.3.2"),sQuery(id+"F0.wireOp",EDGE,"E3.3.3"),sQuery(id+"F0.wireOp",EDGE,"E3.4.1"),sQuery(id+"F0.wireOp",EDGE,"E3.4.2"),sQuery(id+"F0.wireOp",EDGE,"E3.4.3"),sQuery(id+"F0.wireOp",EDGE,"E3.5.1"),sQuery(id+"F0.wireOp",EDGE,"E3.5.2"),sQuery(id+"F0.wireOp",EDGE,"E3.5.3"),sQuery(id+"F0.wireOp",EDGE,"E3.6.1"),sQuery(id+"F0.wireOp",EDGE,"E3.6.2"),sQuery(id+"F0.wireOp",EDGE,"E3.6.3"),sQuery(id+"F0.wireOp",EDGE,"E3.7.1"),sQuery(id+"F0.wireOp",EDGE,"E3.7.2"),sQuery(id+"F0.wireOp",EDGE,"E3.7.3"),sQuery(id+"F0.wireOp",EDGE,"E3.8.1"),sQuery(id+"F0.wireOp",EDGE,"E3.8.2"),sQuery(id+"F0.wireOp",EDGE,"E3.8.3"),sQuery(id+"F0.wireOp",EDGE,"E3.9.1"),sQuery(id+"F0.wireOp",EDGE,"E3.9.2"),sQuery(id+"F0.wireOp",EDGE,"E3.9.3"),sQuery(id+"F0.wireOp",EDGE,"E3.10.1"),sQuery(id+"F0.wireOp",EDGE,"E3.10.2"),sQuery(id+"F0.wireOp",EDGE,"E3.10.3"),sQuery(id+"F0.wireOp",EDGE,"E3.11.1"),sQuery(id+"F0.wireOp",EDGE,"E3.11.2"),sQuery(id+"F0.wireOp",EDGE,"E3.11.3"),sQuery(id+"F0.wireOp",EDGE,"E3.12.1"),sQuery(id+"F0.wireOp",EDGE,"E3.12.2"),sQuery(id+"F0.wireOp",EDGE,"E3.12.3")])],"isStart":true});
            var Q2;
            {var subQ0=sQuery(id+"F0.wireOp",EDGE,"E0");Q2=makeQuery(id+"F1.opExtrude","SWEPT_FACE",FACE,{"disambiguationData":[OSD([subQ0]),TDD([makeQuery(id+"F0.imprint","IMPRINT",EDGE,{"disambiguationData":[TD([[makeQuery(id+"F0.imprint","INTERSECT",VERTEX,{"derivedFrom":[subQ0,sQuery(id+"F0.wireOp",EDGE,"E3.12.3")]}),-1.0]])],"derivedFrom":subQ0})])]});}
            var Q3;
            {var subQ0=sQuery(id+"F0.wireOp",EDGE,"E0");Q3=makeQuery(id+"F1.opExtrude","SWEPT_FACE",FACE,{"disambiguationData":[OSD([subQ0]),TDD([makeQuery(id+"F0.imprint","IMPRINT",EDGE,{"disambiguationData":[TD([[makeQuery(id+"F0.imprint","INTERSECT",VERTEX,{"derivedFrom":[subQ0,sQuery(id+"F0.wireOp",EDGE,"E2.right")]}),-1.0]])],"derivedFrom":subQ0})])]});}
            var Q4;
            {var subQ0=sQuery(id+"F0.wireOp",EDGE,"E0");Q4=makeQuery(id+"F1.opExtrude","SWEPT_FACE",FACE,{"disambiguationData":[OSD([subQ0]),TDD([makeQuery(id+"F0.imprint","IMPRINT",EDGE,{"disambiguationData":[TD([[makeQuery(id+"F0.imprint","INTERSECT",VERTEX,{"derivedFrom":[subQ0,sQuery(id+"F0.wireOp",EDGE,"E3.11.3")]}),-1.0]])],"derivedFrom":subQ0})])]});}
            var Q5;
            {var subQ0=sQuery(id+"F0.wireOp",EDGE,"E0");Q5=makeQuery(id+"F1.opExtrude","SWEPT_FACE",FACE,{"disambiguationData":[OSD([subQ0]),TDD([makeQuery(id+"F0.imprint","IMPRINT",EDGE,{"disambiguationData":[TD([[makeQuery(id+"F0.imprint","INTERSECT",VERTEX,{"derivedFrom":[subQ0,sQuery(id+"F0.wireOp",EDGE,"E3.9.3")]}),-1.0]])],"derivedFrom":subQ0})])]});}
            var Q6;
            {var subQ0=sQuery(id+"F0.wireOp",EDGE,"E0");Q6=makeQuery(id+"F1.opExtrude","SWEPT_FACE",FACE,{"disambiguationData":[OSD([subQ0]),TDD([makeQuery(id+"F0.imprint","IMPRINT",EDGE,{"disambiguationData":[TD([[makeQuery(id+"F0.imprint","INTERSECT",VERTEX,{"derivedFrom":[subQ0,sQuery(id+"F0.wireOp",EDGE,"E3.8.3")]}),-1.0]])],"derivedFrom":subQ0})])]});}
            var Q7;
            {var subQ0=sQuery(id+"F0.wireOp",EDGE,"E0");Q7=makeQuery(id+"F1.opExtrude","SWEPT_FACE",FACE,{"disambiguationData":[OSD([subQ0]),TDD([makeQuery(id+"F0.imprint","IMPRINT",EDGE,{"disambiguationData":[TD([[makeQuery(id+"F0.imprint","INTERSECT",VERTEX,{"derivedFrom":[subQ0,sQuery(id+"F0.wireOp",EDGE,"E3.7.3")]}),-1.0]])],"derivedFrom":subQ0})])]});}
            var Q8;
            {var subQ0=sQuery(id+"F0.wireOp",EDGE,"E0");Q8=makeQuery(id+"F1.opExtrude","SWEPT_FACE",FACE,{"disambiguationData":[OSD([subQ0]),TDD([makeQuery(id+"F0.imprint","IMPRINT",EDGE,{"disambiguationData":[TD([[makeQuery(id+"F0.imprint","INTERSECT",VERTEX,{"derivedFrom":[subQ0,sQuery(id+"F0.wireOp",EDGE,"E3.6.3")]}),-1.0]])],"derivedFrom":subQ0})])]});}
            var Q9;
            {var subQ0=sQuery(id+"F0.wireOp",EDGE,"E0");Q9=makeQuery(id+"F1.opExtrude","SWEPT_FACE",FACE,{"disambiguationData":[OSD([subQ0]),TDD([makeQuery(id+"F0.imprint","IMPRINT",EDGE,{"disambiguationData":[TD([[makeQuery(id+"F0.imprint","INTERSECT",VERTEX,{"derivedFrom":[subQ0,sQuery(id+"F0.wireOp",EDGE,"E3.10.3")]}),-1.0]])],"derivedFrom":subQ0})])]});}
            var Q10;
            {var subQ0=sQuery(id+"F0.wireOp",EDGE,"E0");Q10=makeQuery(id+"F1.opExtrude","SWEPT_FACE",FACE,{"disambiguationData":[OSD([subQ0]),TDD([makeQuery(id+"F0.imprint","IMPRINT",EDGE,{"disambiguationData":[TD([[makeQuery(id+"F0.imprint","INTERSECT",VERTEX,{"derivedFrom":[subQ0,sQuery(id+"F0.wireOp",EDGE,"E3.5.3")]}),-1.0]])],"derivedFrom":subQ0})])]});}
            var Q11;
            {var subQ0=sQuery(id+"F0.wireOp",EDGE,"E0");Q11=makeQuery(id+"F1.opExtrude","SWEPT_FACE",FACE,{"disambiguationData":[OSD([subQ0]),TDD([makeQuery(id+"F0.imprint","IMPRINT",EDGE,{"disambiguationData":[TD([[makeQuery(id+"F0.imprint","INTERSECT",VERTEX,{"derivedFrom":[subQ0,sQuery(id+"F0.wireOp",EDGE,"E3.4.3")]}),-1.0]])],"derivedFrom":subQ0})])]});}
            var Q12;
            {var subQ0=sQuery(id+"F0.wireOp",EDGE,"E0");Q12=makeQuery(id+"F1.opExtrude","SWEPT_FACE",FACE,{"disambiguationData":[OSD([subQ0]),TDD([makeQuery(id+"F0.imprint","IMPRINT",EDGE,{"disambiguationData":[TD([[makeQuery(id+"F0.imprint","INTERSECT",VERTEX,{"derivedFrom":[subQ0,sQuery(id+"F0.wireOp",EDGE,"E3.2.1")]}),1.0]])],"derivedFrom":subQ0})])]});}
            var Q13;
            {var subQ0=sQuery(id+"F0.wireOp",EDGE,"E0");Q13=makeQuery(id+"F1.opExtrude","SWEPT_FACE",FACE,{"disambiguationData":[OSD([subQ0]),TDD([makeQuery(id+"F0.imprint","IMPRINT",EDGE,{"disambiguationData":[TD([[makeQuery(id+"F0.imprint","INTERSECT",VERTEX,{"derivedFrom":[subQ0,sQuery(id+"F0.wireOp",EDGE,"E3.2.3")]}),-1.0]])],"derivedFrom":subQ0})])]});}
            var Q14;
            {var subQ0=sQuery(id+"F0.wireOp",EDGE,"E0");Q14=makeQuery(id+"F1.opExtrude","SWEPT_FACE",FACE,{"disambiguationData":[OSD([subQ0]),TDD([makeQuery(id+"F0.imprint","IMPRINT",EDGE,{"disambiguationData":[TD([[makeQuery(id+"F0.imprint","INTERSECT",VERTEX,{"derivedFrom":[subQ0,sQuery(id+"F0.wireOp",EDGE,"E3.1.3")]}),-1.0]])],"derivedFrom":subQ0})])]});}
            chamfer(context, id + "F4", {"entities" : qUnion([Q0, Q1, Q2, Q3, Q4, Q5, Q6, Q7, Q8, Q9, Q10, Q11, Q12, Q13, Q14]), "width" : 1.27 * mm, "tangentPropagation" : true});
        }
        {
            var Q0;
            Q0=makeQuery(id+"F2.opExtrude","CAP_FACE",FACE,{"disambiguationData":[OSD([sQuery(id+"F0.wireOp",EDGE,"E1")])],"isStart":false});
            extrude(context, id + "F5", {"entities" : qUnion([Q0]), "operationType" : NewBodyOperationType.ADD, "depth" : 3.17 * mm, "hasDraft" : true, "draftAngle" : 10 * degree, "draftPullDirection" : true});
        }
        {
            var Q0;
            Q0=makeQuery(id+"F5.opExtrude","CAP_FACE",FACE,{"disambiguationData":[OSD([sQuery(id+"F0.wireOp",EDGE,"E1")])],"isStart":false});
            extrude(context, id + "F6", {"entities" : qUnion([Q0]), "operationType" : NewBodyOperationType.ADD, "depth" : 3.17 * mm, "hasDraft" : true, "draftAngle" : 10 * degree});
        }
        {
            var Q0;
            Q0=makeQuery(id+"F6.opExtrude","CAP_FACE",FACE,{"disambiguationData":[OSD([sQuery(id+"F0.wireOp",EDGE,"E1")])],"isStart":false});
            extrude(context, id + "F7", {"entities" : qUnion([Q0]), "operationType" : NewBodyOperationType.ADD, "depth" : 1.59 * mm});
        }
        {
            var Q0;
            Q0=makeQuery(id+"F2.opExtrude","CAP_FACE",FACE,{"disambiguationData":[OSD([sQuery(id+"F0.wireOp",EDGE,"E1")])],"isStart":true});
            extrude(context, id + "F8", {"entities" : qUnion([Q0]), "operationType" : NewBodyOperationType.ADD, "depth" : 3.17 * mm, "hasDraft" : true, "draftAngle" : 10 * degree, "draftPullDirection" : true});
        }
        {
            var Q0;
            Q0=makeQuery(id+"F8.opExtrude","CAP_FACE",FACE,{"disambiguationData":[OSD([sQuery(id+"F0.wireOp",EDGE,"E1")])],"isStart":false});
            extrude(context, id + "F9", {"entities" : qUnion([Q0]), "operationType" : NewBodyOperationType.ADD, "depth" : 3.17 * mm, "hasDraft" : true, "draftAngle" : 10 * degree});
        }
        {
            var Q0;
            Q0=makeQuery(id+"F9.opExtrude","CAP_FACE",FACE,{"disambiguationData":[OSD([sQuery(id+"F0.wireOp",EDGE,"E1")])],"isStart":false});
            extrude(context, id + "F10", {"entities" : qUnion([Q0]), "operationType" : NewBodyOperationType.ADD, "depth" : 1.59 * mm});
        }
        {
            var Q0;
            {var subQ0=sQuery(id+"F0.wireOp",EDGE,"E3.1.1");Q0=makeQuery(id+"F3.opChamfer","BLEND_EDGE",EDGE,{"blendedFrom":[makeQuery(id+"F1.opExtrude","SWEPT_EDGE",EDGE,{"disambiguationData":[OSD([subQ0,sQuery(id+"F0.wireOp",EDGE,"E3.1.2")])]}),makeQuery(id+"F1.opExtrude","SWEPT_FACE",FACE,{"disambiguationData":[OSD([subQ0])]})],"blendedInto":[makeQuery(id+"F1.opExtrude","SWEPT_FACE",FACE,{"disambiguationData":[OSD([subQ0])]})]});}
            var Q1;
            {var subQ0=sQuery(id+"F0.wireOp",EDGE,"E3.1.3");Q1=makeQuery(id+"F3.opChamfer","BLEND_EDGE",EDGE,{"blendedFrom":[makeQuery(id+"F1.opExtrude","SWEPT_EDGE",EDGE,{"disambiguationData":[OSD([sQuery(id+"F0.wireOp",EDGE,"E3.1.2"),subQ0])]}),makeQuery(id+"F1.opExtrude","SWEPT_FACE",FACE,{"disambiguationData":[OSD([subQ0])]})],"blendedInto":[makeQuery(id+"F1.opExtrude","SWEPT_FACE",FACE,{"disambiguationData":[OSD([subQ0])]})]});}
            var Q2;
            {var subQ0=sQuery(id+"F0.wireOp",EDGE,"E3.1.1");var subQ1=sQuery(id+"F0.wireOp",EDGE,"E3.1.2");Q2=makeQuery(id+"F4.opChamfer","BLEND_EDGE",EDGE,{"blendedFrom":[makeQuery(id+"F3.opChamfer","BLEND_EDGE",EDGE,{"blendedFrom":[makeQuery(id+"F1.opExtrude","SWEPT_EDGE",EDGE,{"disambiguationData":[OSD([subQ0,subQ1])]}),makeQuery(id+"F1.opExtrude","CAP_FACE",FACE,{"disambiguationData":[OSD([sQuery(id+"F0.wireOp",EDGE,"E0"),sQuery(id+"F0.wireOp",EDGE,"E1"),sQuery(id+"F0.wireOp",EDGE,"E2.bottom"),sQuery(id+"F0.wireOp",EDGE,"E2.left"),sQuery(id+"F0.wireOp",EDGE,"E2.right"),subQ0,subQ1,sQuery(id+"F0.wireOp",EDGE,"E3.1.3"),sQuery(id+"F0.wireOp",EDGE,"E3.2.1"),sQuery(id+"F0.wireOp",EDGE,"E3.2.2"),sQuery(id+"F0.wireOp",EDGE,"E3.2.3"),sQuery(id+"F0.wireOp",EDGE,"E3.3.1"),sQuery(id+"F0.wireOp",EDGE,"E3.3.2"),sQuery(id+"F0.wireOp",EDGE,"E3.3.3"),sQuery(id+"F0.wireOp",EDGE,"E3.4.1"),sQuery(id+"F0.wireOp",EDGE,"E3.4.2"),sQuery(id+"F0.wireOp",EDGE,"E3.4.3"),sQuery(id+"F0.wireOp",EDGE,"E3.5.1"),sQuery(id+"F0.wireOp",EDGE,"E3.5.2"),sQuery(id+"F0.wireOp",EDGE,"E3.5.3"),sQuery(id+"F0.wireOp",EDGE,"E3.6.1"),sQuery(id+"F0.wireOp",EDGE,"E3.6.2"),sQuery(id+"F0.wireOp",EDGE,"E3.6.3"),sQuery(id+"F0.wireOp",EDGE,"E3.7.1"),sQuery(id+"F0.wireOp",EDGE,"E3.7.2"),sQuery(id+"F0.wireOp",EDGE,"E3.7.3"),sQuery(id+"F0.wireOp",EDGE,"E3.8.1"),sQuery(id+"F0.wireOp",EDGE,"E3.8.2"),sQuery(id+"F0.wireOp",EDGE,"E3.8.3"),sQuery(id+"F0.wireOp",EDGE,"E3.9.1"),sQuery(id+"F0.wireOp",EDGE,"E3.9.2"),sQuery(id+"F0.wireOp",EDGE,"E3.9.3"),sQuery(id+"F0.wireOp",EDGE,"E3.10.1"),sQuery(id+"F0.wireOp",EDGE,"E3.10.2"),sQuery(id+"F0.wireOp",EDGE,"E3.10.3"),sQuery(id+"F0.wireOp",EDGE,"E3.11.1"),sQuery(id+"F0.wireOp",EDGE,"E3.11.2"),sQuery(id+"F0.wireOp",EDGE,"E3.11.3"),sQuery(id+"F0.wireOp",EDGE,"E3.12.1"),sQuery(id+"F0.wireOp",EDGE,"E3.12.2"),sQuery(id+"F0.wireOp",EDGE,"E3.12.3")])],"isStart":false})],"blendedInto":[makeQuery(id+"F1.opExtrude","CAP_FACE",FACE,{"disambiguationData":[OSD([sQuery(id+"F0.wireOp",EDGE,"E0"),sQuery(id+"F0.wireOp",EDGE,"E1"),sQuery(id+"F0.wireOp",EDGE,"E2.bottom"),sQuery(id+"F0.wireOp",EDGE,"E2.left"),sQuery(id+"F0.wireOp",EDGE,"E2.right"),subQ0,subQ1,sQuery(id+"F0.wireOp",EDGE,"E3.1.3"),sQuery(id+"F0.wireOp",EDGE,"E3.2.1"),sQuery(id+"F0.wireOp",EDGE,"E3.2.2"),sQuery(id+"F0.wireOp",EDGE,"E3.2.3"),sQuery(id+"F0.wireOp",EDGE,"E3.3.1"),sQuery(id+"F0.wireOp",EDGE,"E3.3.2"),sQuery(id+"F0.wireOp",EDGE,"E3.3.3"),sQuery(id+"F0.wireOp",EDGE,"E3.4.1"),sQuery(id+"F0.wireOp",EDGE,"E3.4.2"),sQuery(id+"F0.wireOp",EDGE,"E3.4.3"),sQuery(id+"F0.wireOp",EDGE,"E3.5.1"),sQuery(id+"F0.wireOp",EDGE,"E3.5.2"),sQuery(id+"F0.wireOp",EDGE,"E3.5.3"),sQuery(id+"F0.wireOp",EDGE,"E3.6.1"),sQuery(id+"F0.wireOp",EDGE,"E3.6.2"),sQuery(id+"F0.wireOp",EDGE,"E3.6.3"),sQuery(id+"F0.wireOp",EDGE,"E3.7.1"),sQuery(id+"F0.wireOp",EDGE,"E3.7.2"),sQuery(id+"F0.wireOp",EDGE,"E3.7.3"),sQuery(id+"F0.wireOp",EDGE,"E3.8.1"),sQuery(id+"F0.wireOp",EDGE,"E3.8.2"),sQuery(id+"F0.wireOp",EDGE,"E3.8.3"),sQuery(id+"F0.wireOp",EDGE,"E3.9.1"),sQuery(id+"F0.wireOp",EDGE,"E3.9.2"),sQuery(id+"F0.wireOp",EDGE,"E3.9.3"),sQuery(id+"F0.wireOp",EDGE,"E3.10.1"),sQuery(id+"F0.wireOp",EDGE,"E3.10.2"),sQuery(id+"F0.wireOp",EDGE,"E3.10.3"),sQuery(id+"F0.wireOp",EDGE,"E3.11.1"),sQuery(id+"F0.wireOp",EDGE,"E3.11.2"),sQuery(id+"F0.wireOp",EDGE,"E3.11.3"),sQuery(id+"F0.wireOp",EDGE,"E3.12.1"),sQuery(id+"F0.wireOp",EDGE,"E3.12.2"),sQuery(id+"F0.wireOp",EDGE,"E3.12.3")])],"isStart":false})]}),makeQuery(id+"F1.opExtrude","CAP_EDGE",EDGE,{"disambiguationData":[OSD([subQ0])],"isStart":false})],"blendedInto":[]});}
            var Q3;
            {var subQ0=sQuery(id+"F0.wireOp",EDGE,"E3.1.3");var subQ1=sQuery(id+"F0.wireOp",EDGE,"E3.1.2");Q3=makeQuery(id+"F4.opChamfer","BLEND_EDGE",EDGE,{"blendedFrom":[makeQuery(id+"F3.opChamfer","BLEND_EDGE",EDGE,{"blendedFrom":[makeQuery(id+"F1.opExtrude","SWEPT_EDGE",EDGE,{"disambiguationData":[OSD([subQ1,subQ0])]}),makeQuery(id+"F1.opExtrude","CAP_FACE",FACE,{"disambiguationData":[OSD([sQuery(id+"F0.wireOp",EDGE,"E0"),sQuery(id+"F0.wireOp",EDGE,"E1"),sQuery(id+"F0.wireOp",EDGE,"E2.bottom"),sQuery(id+"F0.wireOp",EDGE,"E2.left"),sQuery(id+"F0.wireOp",EDGE,"E2.right"),sQuery(id+"F0.wireOp",EDGE,"E3.1.1"),subQ1,subQ0,sQuery(id+"F0.wireOp",EDGE,"E3.2.1"),sQuery(id+"F0.wireOp",EDGE,"E3.2.2"),sQuery(id+"F0.wireOp",EDGE,"E3.2.3"),sQuery(id+"F0.wireOp",EDGE,"E3.3.1"),sQuery(id+"F0.wireOp",EDGE,"E3.3.2"),sQuery(id+"F0.wireOp",EDGE,"E3.3.3"),sQuery(id+"F0.wireOp",EDGE,"E3.4.1"),sQuery(id+"F0.wireOp",EDGE,"E3.4.2"),sQuery(id+"F0.wireOp",EDGE,"E3.4.3"),sQuery(id+"F0.wireOp",EDGE,"E3.5.1"),sQuery(id+"F0.wireOp",EDGE,"E3.5.2"),sQuery(id+"F0.wireOp",EDGE,"E3.5.3"),sQuery(id+"F0.wireOp",EDGE,"E3.6.1"),sQuery(id+"F0.wireOp",EDGE,"E3.6.2"),sQuery(id+"F0.wireOp",EDGE,"E3.6.3"),sQuery(id+"F0.wireOp",EDGE,"E3.7.1"),sQuery(id+"F0.wireOp",EDGE,"E3.7.2"),sQuery(id+"F0.wireOp",EDGE,"E3.7.3"),sQuery(id+"F0.wireOp",EDGE,"E3.8.1"),sQuery(id+"F0.wireOp",EDGE,"E3.8.2"),sQuery(id+"F0.wireOp",EDGE,"E3.8.3"),sQuery(id+"F0.wireOp",EDGE,"E3.9.1"),sQuery(id+"F0.wireOp",EDGE,"E3.9.2"),sQuery(id+"F0.wireOp",EDGE,"E3.9.3"),sQuery(id+"F0.wireOp",EDGE,"E3.10.1"),sQuery(id+"F0.wireOp",EDGE,"E3.10.2"),sQuery(id+"F0.wireOp",EDGE,"E3.10.3"),sQuery(id+"F0.wireOp",EDGE,"E3.11.1"),sQuery(id+"F0.wireOp",EDGE,"E3.11.2"),sQuery(id+"F0.wireOp",EDGE,"E3.11.3"),sQuery(id+"F0.wireOp",EDGE,"E3.12.1"),sQuery(id+"F0.wireOp",EDGE,"E3.12.2"),sQuery(id+"F0.wireOp",EDGE,"E3.12.3")])],"isStart":false})],"blendedInto":[makeQuery(id+"F1.opExtrude","CAP_FACE",FACE,{"disambiguationData":[OSD([sQuery(id+"F0.wireOp",EDGE,"E0"),sQuery(id+"F0.wireOp",EDGE,"E1"),sQuery(id+"F0.wireOp",EDGE,"E2.bottom"),sQuery(id+"F0.wireOp",EDGE,"E2.left"),sQuery(id+"F0.wireOp",EDGE,"E2.right"),sQuery(id+"F0.wireOp",EDGE,"E3.1.1"),subQ1,subQ0,sQuery(id+"F0.wireOp",EDGE,"E3.2.1"),sQuery(id+"F0.wireOp",EDGE,"E3.2.2"),sQuery(id+"F0.wireOp",EDGE,"E3.2.3"),sQuery(id+"F0.wireOp",EDGE,"E3.3.1"),sQuery(id+"F0.wireOp",EDGE,"E3.3.2"),sQuery(id+"F0.wireOp",EDGE,"E3.3.3"),sQuery(id+"F0.wireOp",EDGE,"E3.4.1"),sQuery(id+"F0.wireOp",EDGE,"E3.4.2"),sQuery(id+"F0.wireOp",EDGE,"E3.4.3"),sQuery(id+"F0.wireOp",EDGE,"E3.5.1"),sQuery(id+"F0.wireOp",EDGE,"E3.5.2"),sQuery(id+"F0.wireOp",EDGE,"E3.5.3"),sQuery(id+"F0.wireOp",EDGE,"E3.6.1"),sQuery(id+"F0.wireOp",EDGE,"E3.6.2"),sQuery(id+"F0.wireOp",EDGE,"E3.6.3"),sQuery(id+"F0.wireOp",EDGE,"E3.7.1"),sQuery(id+"F0.wireOp",EDGE,"E3.7.2"),sQuery(id+"F0.wireOp",EDGE,"E3.7.3"),sQuery(id+"F0.wireOp",EDGE,"E3.8.1"),sQuery(id+"F0.wireOp",EDGE,"E3.8.2"),sQuery(id+"F0.wireOp",EDGE,"E3.8.3"),sQuery(id+"F0.wireOp",EDGE,"E3.9.1"),sQuery(id+"F0.wireOp",EDGE,"E3.9.2"),sQuery(id+"F0.wireOp",EDGE,"E3.9.3"),sQuery(id+"F0.wireOp",EDGE,"E3.10.1"),sQuery(id+"F0.wireOp",EDGE,"E3.10.2"),sQuery(id+"F0.wireOp",EDGE,"E3.10.3"),sQuery(id+"F0.wireOp",EDGE,"E3.11.1"),sQuery(id+"F0.wireOp",EDGE,"E3.11.2"),sQuery(id+"F0.wireOp",EDGE,"E3.11.3"),sQuery(id+"F0.wireOp",EDGE,"E3.12.1"),sQuery(id+"F0.wireOp",EDGE,"E3.12.2"),sQuery(id+"F0.wireOp",EDGE,"E3.12.3")])],"isStart":false})]}),makeQuery(id+"F1.opExtrude","CAP_EDGE",EDGE,{"disambiguationData":[OSD([subQ0])],"isStart":false})],"blendedInto":[]});}
            var Q4;
            {var subQ0=sQuery(id+"F0.wireOp",EDGE,"E3.1.3");var subQ1=sQuery(id+"F0.wireOp",EDGE,"E3.1.2");Q4=makeQuery(id+"F4.opChamfer","BLEND_EDGE",EDGE,{"blendedFrom":[makeQuery(id+"F3.opChamfer","BLEND_EDGE",EDGE,{"blendedFrom":[makeQuery(id+"F1.opExtrude","SWEPT_EDGE",EDGE,{"disambiguationData":[OSD([subQ1,subQ0])]}),makeQuery(id+"F1.opExtrude","CAP_FACE",FACE,{"disambiguationData":[OSD([sQuery(id+"F0.wireOp",EDGE,"E0"),sQuery(id+"F0.wireOp",EDGE,"E1"),sQuery(id+"F0.wireOp",EDGE,"E2.bottom"),sQuery(id+"F0.wireOp",EDGE,"E2.left"),sQuery(id+"F0.wireOp",EDGE,"E2.right"),sQuery(id+"F0.wireOp",EDGE,"E3.1.1"),subQ1,subQ0,sQuery(id+"F0.wireOp",EDGE,"E3.2.1"),sQuery(id+"F0.wireOp",EDGE,"E3.2.2"),sQuery(id+"F0.wireOp",EDGE,"E3.2.3"),sQuery(id+"F0.wireOp",EDGE,"E3.3.1"),sQuery(id+"F0.wireOp",EDGE,"E3.3.2"),sQuery(id+"F0.wireOp",EDGE,"E3.3.3"),sQuery(id+"F0.wireOp",EDGE,"E3.4.1"),sQuery(id+"F0.wireOp",EDGE,"E3.4.2"),sQuery(id+"F0.wireOp",EDGE,"E3.4.3"),sQuery(id+"F0.wireOp",EDGE,"E3.5.1"),sQuery(id+"F0.wireOp",EDGE,"E3.5.2"),sQuery(id+"F0.wireOp",EDGE,"E3.5.3"),sQuery(id+"F0.wireOp",EDGE,"E3.6.1"),sQuery(id+"F0.wireOp",EDGE,"E3.6.2"),sQuery(id+"F0.wireOp",EDGE,"E3.6.3"),sQuery(id+"F0.wireOp",EDGE,"E3.7.1"),sQuery(id+"F0.wireOp",EDGE,"E3.7.2"),sQuery(id+"F0.wireOp",EDGE,"E3.7.3"),sQuery(id+"F0.wireOp",EDGE,"E3.8.1"),sQuery(id+"F0.wireOp",EDGE,"E3.8.2"),sQuery(id+"F0.wireOp",EDGE,"E3.8.3"),sQuery(id+"F0.wireOp",EDGE,"E3.9.1"),sQuery(id+"F0.wireOp",EDGE,"E3.9.2"),sQuery(id+"F0.wireOp",EDGE,"E3.9.3"),sQuery(id+"F0.wireOp",EDGE,"E3.10.1"),sQuery(id+"F0.wireOp",EDGE,"E3.10.2"),sQuery(id+"F0.wireOp",EDGE,"E3.10.3"),sQuery(id+"F0.wireOp",EDGE,"E3.11.1"),sQuery(id+"F0.wireOp",EDGE,"E3.11.2"),sQuery(id+"F0.wireOp",EDGE,"E3.11.3"),sQuery(id+"F0.wireOp",EDGE,"E3.12.1"),sQuery(id+"F0.wireOp",EDGE,"E3.12.2"),sQuery(id+"F0.wireOp",EDGE,"E3.12.3")])],"isStart":true})],"blendedInto":[makeQuery(id+"F1.opExtrude","CAP_FACE",FACE,{"disambiguationData":[OSD([sQuery(id+"F0.wireOp",EDGE,"E0"),sQuery(id+"F0.wireOp",EDGE,"E1"),sQuery(id+"F0.wireOp",EDGE,"E2.bottom"),sQuery(id+"F0.wireOp",EDGE,"E2.left"),sQuery(id+"F0.wireOp",EDGE,"E2.right"),sQuery(id+"F0.wireOp",EDGE,"E3.1.1"),subQ1,subQ0,sQuery(id+"F0.wireOp",EDGE,"E3.2.1"),sQuery(id+"F0.wireOp",EDGE,"E3.2.2"),sQuery(id+"F0.wireOp",EDGE,"E3.2.3"),sQuery(id+"F0.wireOp",EDGE,"E3.3.1"),sQuery(id+"F0.wireOp",EDGE,"E3.3.2"),sQuery(id+"F0.wireOp",EDGE,"E3.3.3"),sQuery(id+"F0.wireOp",EDGE,"E3.4.1"),sQuery(id+"F0.wireOp",EDGE,"E3.4.2"),sQuery(id+"F0.wireOp",EDGE,"E3.4.3"),sQuery(id+"F0.wireOp",EDGE,"E3.5.1"),sQuery(id+"F0.wireOp",EDGE,"E3.5.2"),sQuery(id+"F0.wireOp",EDGE,"E3.5.3"),sQuery(id+"F0.wireOp",EDGE,"E3.6.1"),sQuery(id+"F0.wireOp",EDGE,"E3.6.2"),sQuery(id+"F0.wireOp",EDGE,"E3.6.3"),sQuery(id+"F0.wireOp",EDGE,"E3.7.1"),sQuery(id+"F0.wireOp",EDGE,"E3.7.2"),sQuery(id+"F0.wireOp",EDGE,"E3.7.3"),sQuery(id+"F0.wireOp",EDGE,"E3.8.1"),sQuery(id+"F0.wireOp",EDGE,"E3.8.2"),sQuery(id+"F0.wireOp",EDGE,"E3.8.3"),sQuery(id+"F0.wireOp",EDGE,"E3.9.1"),sQuery(id+"F0.wireOp",EDGE,"E3.9.2"),sQuery(id+"F0.wireOp",EDGE,"E3.9.3"),sQuery(id+"F0.wireOp",EDGE,"E3.10.1"),sQuery(id+"F0.wireOp",EDGE,"E3.10.2"),sQuery(id+"F0.wireOp",EDGE,"E3.10.3"),sQuery(id+"F0.wireOp",EDGE,"E3.11.1"),sQuery(id+"F0.wireOp",EDGE,"E3.11.2"),sQuery(id+"F0.wireOp",EDGE,"E3.11.3"),sQuery(id+"F0.wireOp",EDGE,"E3.12.1"),sQuery(id+"F0.wireOp",EDGE,"E3.12.2"),sQuery(id+"F0.wireOp",EDGE,"E3.12.3")])],"isStart":true})]}),makeQuery(id+"F1.opExtrude","CAP_EDGE",EDGE,{"disambiguationData":[OSD([subQ0])],"isStart":true})],"blendedInto":[]});}
            var Q5;
            {var subQ0=sQuery(id+"F0.wireOp",EDGE,"E3.1.1");var subQ1=sQuery(id+"F0.wireOp",EDGE,"E3.1.2");Q5=makeQuery(id+"F4.opChamfer","BLEND_EDGE",EDGE,{"blendedFrom":[makeQuery(id+"F3.opChamfer","BLEND_EDGE",EDGE,{"blendedFrom":[makeQuery(id+"F1.opExtrude","SWEPT_EDGE",EDGE,{"disambiguationData":[OSD([subQ0,subQ1])]}),makeQuery(id+"F1.opExtrude","CAP_FACE",FACE,{"disambiguationData":[OSD([sQuery(id+"F0.wireOp",EDGE,"E0"),sQuery(id+"F0.wireOp",EDGE,"E1"),sQuery(id+"F0.wireOp",EDGE,"E2.bottom"),sQuery(id+"F0.wireOp",EDGE,"E2.left"),sQuery(id+"F0.wireOp",EDGE,"E2.right"),subQ0,subQ1,sQuery(id+"F0.wireOp",EDGE,"E3.1.3"),sQuery(id+"F0.wireOp",EDGE,"E3.2.1"),sQuery(id+"F0.wireOp",EDGE,"E3.2.2"),sQuery(id+"F0.wireOp",EDGE,"E3.2.3"),sQuery(id+"F0.wireOp",EDGE,"E3.3.1"),sQuery(id+"F0.wireOp",EDGE,"E3.3.2"),sQuery(id+"F0.wireOp",EDGE,"E3.3.3"),sQuery(id+"F0.wireOp",EDGE,"E3.4.1"),sQuery(id+"F0.wireOp",EDGE,"E3.4.2"),sQuery(id+"F0.wireOp",EDGE,"E3.4.3"),sQuery(id+"F0.wireOp",EDGE,"E3.5.1"),sQuery(id+"F0.wireOp",EDGE,"E3.5.2"),sQuery(id+"F0.wireOp",EDGE,"E3.5.3"),sQuery(id+"F0.wireOp",EDGE,"E3.6.1"),sQuery(id+"F0.wireOp",EDGE,"E3.6.2"),sQuery(id+"F0.wireOp",EDGE,"E3.6.3"),sQuery(id+"F0.wireOp",EDGE,"E3.7.1"),sQuery(id+"F0.wireOp",EDGE,"E3.7.2"),sQuery(id+"F0.wireOp",EDGE,"E3.7.3"),sQuery(id+"F0.wireOp",EDGE,"E3.8.1"),sQuery(id+"F0.wireOp",EDGE,"E3.8.2"),sQuery(id+"F0.wireOp",EDGE,"E3.8.3"),sQuery(id+"F0.wireOp",EDGE,"E3.9.1"),sQuery(id+"F0.wireOp",EDGE,"E3.9.2"),sQuery(id+"F0.wireOp",EDGE,"E3.9.3"),sQuery(id+"F0.wireOp",EDGE,"E3.10.1"),sQuery(id+"F0.wireOp",EDGE,"E3.10.2"),sQuery(id+"F0.wireOp",EDGE,"E3.10.3"),sQuery(id+"F0.wireOp",EDGE,"E3.11.1"),sQuery(id+"F0.wireOp",EDGE,"E3.11.2"),sQuery(id+"F0.wireOp",EDGE,"E3.11.3"),sQuery(id+"F0.wireOp",EDGE,"E3.12.1"),sQuery(id+"F0.wireOp",EDGE,"E3.12.2"),sQuery(id+"F0.wireOp",EDGE,"E3.12.3")])],"isStart":true})],"blendedInto":[makeQuery(id+"F1.opExtrude","CAP_FACE",FACE,{"disambiguationData":[OSD([sQuery(id+"F0.wireOp",EDGE,"E0"),sQuery(id+"F0.wireOp",EDGE,"E1"),sQuery(id+"F0.wireOp",EDGE,"E2.bottom"),sQuery(id+"F0.wireOp",EDGE,"E2.left"),sQuery(id+"F0.wireOp",EDGE,"E2.right"),subQ0,subQ1,sQuery(id+"F0.wireOp",EDGE,"E3.1.3"),sQuery(id+"F0.wireOp",EDGE,"E3.2.1"),sQuery(id+"F0.wireOp",EDGE,"E3.2.2"),sQuery(id+"F0.wireOp",EDGE,"E3.2.3"),sQuery(id+"F0.wireOp",EDGE,"E3.3.1"),sQuery(id+"F0.wireOp",EDGE,"E3.3.2"),sQuery(id+"F0.wireOp",EDGE,"E3.3.3"),sQuery(id+"F0.wireOp",EDGE,"E3.4.1"),sQuery(id+"F0.wireOp",EDGE,"E3.4.2"),sQuery(id+"F0.wireOp",EDGE,"E3.4.3"),sQuery(id+"F0.wireOp",EDGE,"E3.5.1"),sQuery(id+"F0.wireOp",EDGE,"E3.5.2"),sQuery(id+"F0.wireOp",EDGE,"E3.5.3"),sQuery(id+"F0.wireOp",EDGE,"E3.6.1"),sQuery(id+"F0.wireOp",EDGE,"E3.6.2"),sQuery(id+"F0.wireOp",EDGE,"E3.6.3"),sQuery(id+"F0.wireOp",EDGE,"E3.7.1"),sQuery(id+"F0.wireOp",EDGE,"E3.7.2"),sQuery(id+"F0.wireOp",EDGE,"E3.7.3"),sQuery(id+"F0.wireOp",EDGE,"E3.8.1"),sQuery(id+"F0.wireOp",EDGE,"E3.8.2"),sQuery(id+"F0.wireOp",EDGE,"E3.8.3"),sQuery(id+"F0.wireOp",EDGE,"E3.9.1"),sQuery(id+"F0.wireOp",EDGE,"E3.9.2"),sQuery(id+"F0.wireOp",EDGE,"E3.9.3"),sQuery(id+"F0.wireOp",EDGE,"E3.10.1"),sQuery(id+"F0.wireOp",EDGE,"E3.10.2"),sQuery(id+"F0.wireOp",EDGE,"E3.10.3"),sQuery(id+"F0.wireOp",EDGE,"E3.11.1"),sQuery(id+"F0.wireOp",EDGE,"E3.11.2"),sQuery(id+"F0.wireOp",EDGE,"E3.11.3"),sQuery(id+"F0.wireOp",EDGE,"E3.12.1"),sQuery(id+"F0.wireOp",EDGE,"E3.12.2"),sQuery(id+"F0.wireOp",EDGE,"E3.12.3")])],"isStart":true})]}),makeQuery(id+"F1.opExtrude","CAP_EDGE",EDGE,{"disambiguationData":[OSD([subQ0])],"isStart":true})],"blendedInto":[]});}
            var Q6;
            {var subQ0=sQuery(id+"F0.wireOp",EDGE,"E2.left");Q6=makeQuery(id+"F3.opChamfer","BLEND_EDGE",EDGE,{"blendedFrom":[makeQuery(id+"F1.opExtrude","SWEPT_EDGE",EDGE,{"disambiguationData":[OSD([sQuery(id+"F0.wireOp",EDGE,"E2.bottom"),subQ0])]}),makeQuery(id+"F1.opExtrude","SWEPT_FACE",FACE,{"disambiguationData":[OSD([subQ0])]})],"blendedInto":[makeQuery(id+"F1.opExtrude","SWEPT_FACE",FACE,{"disambiguationData":[OSD([subQ0])]})]});}
            var Q7;
            {var subQ0=sQuery(id+"F0.wireOp",EDGE,"E3.2.1");Q7=makeQuery(id+"F3.opChamfer","BLEND_EDGE",EDGE,{"blendedFrom":[makeQuery(id+"F1.opExtrude","SWEPT_EDGE",EDGE,{"disambiguationData":[OSD([subQ0,sQuery(id+"F0.wireOp",EDGE,"E3.2.2")])]}),makeQuery(id+"F1.opExtrude","SWEPT_FACE",FACE,{"disambiguationData":[OSD([subQ0])]})],"blendedInto":[makeQuery(id+"F1.opExtrude","SWEPT_FACE",FACE,{"disambiguationData":[OSD([subQ0])]})]});}
            var Q8;
            {var subQ0=sQuery(id+"F0.wireOp",EDGE,"E3.3.1");Q8=makeQuery(id+"F3.opChamfer","BLEND_EDGE",EDGE,{"blendedFrom":[makeQuery(id+"F1.opExtrude","SWEPT_EDGE",EDGE,{"disambiguationData":[OSD([subQ0,sQuery(id+"F0.wireOp",EDGE,"E3.3.2")])]}),makeQuery(id+"F1.opExtrude","SWEPT_FACE",FACE,{"disambiguationData":[OSD([subQ0])]})],"blendedInto":[makeQuery(id+"F1.opExtrude","SWEPT_FACE",FACE,{"disambiguationData":[OSD([subQ0])]})]});}
            var Q9;
            {var subQ0=sQuery(id+"F0.wireOp",EDGE,"E3.2.3");var subQ1=sQuery(id+"F0.wireOp",EDGE,"E3.2.2");Q9=makeQuery(id+"F4.opChamfer","BLEND_EDGE",EDGE,{"blendedFrom":[makeQuery(id+"F3.opChamfer","BLEND_EDGE",EDGE,{"blendedFrom":[makeQuery(id+"F1.opExtrude","SWEPT_EDGE",EDGE,{"disambiguationData":[OSD([subQ1,subQ0])]}),makeQuery(id+"F1.opExtrude","CAP_FACE",FACE,{"disambiguationData":[OSD([sQuery(id+"F0.wireOp",EDGE,"E0"),sQuery(id+"F0.wireOp",EDGE,"E1"),sQuery(id+"F0.wireOp",EDGE,"E2.bottom"),sQuery(id+"F0.wireOp",EDGE,"E2.left"),sQuery(id+"F0.wireOp",EDGE,"E2.right"),sQuery(id+"F0.wireOp",EDGE,"E3.1.1"),sQuery(id+"F0.wireOp",EDGE,"E3.1.2"),sQuery(id+"F0.wireOp",EDGE,"E3.1.3"),sQuery(id+"F0.wireOp",EDGE,"E3.2.1"),subQ1,subQ0,sQuery(id+"F0.wireOp",EDGE,"E3.3.1"),sQuery(id+"F0.wireOp",EDGE,"E3.3.2"),sQuery(id+"F0.wireOp",EDGE,"E3.3.3"),sQuery(id+"F0.wireOp",EDGE,"E3.4.1"),sQuery(id+"F0.wireOp",EDGE,"E3.4.2"),sQuery(id+"F0.wireOp",EDGE,"E3.4.3"),sQuery(id+"F0.wireOp",EDGE,"E3.5.1"),sQuery(id+"F0.wireOp",EDGE,"E3.5.2"),sQuery(id+"F0.wireOp",EDGE,"E3.5.3"),sQuery(id+"F0.wireOp",EDGE,"E3.6.1"),sQuery(id+"F0.wireOp",EDGE,"E3.6.2"),sQuery(id+"F0.wireOp",EDGE,"E3.6.3"),sQuery(id+"F0.wireOp",EDGE,"E3.7.1"),sQuery(id+"F0.wireOp",EDGE,"E3.7.2"),sQuery(id+"F0.wireOp",EDGE,"E3.7.3"),sQuery(id+"F0.wireOp",EDGE,"E3.8.1"),sQuery(id+"F0.wireOp",EDGE,"E3.8.2"),sQuery(id+"F0.wireOp",EDGE,"E3.8.3"),sQuery(id+"F0.wireOp",EDGE,"E3.9.1"),sQuery(id+"F0.wireOp",EDGE,"E3.9.2"),sQuery(id+"F0.wireOp",EDGE,"E3.9.3"),sQuery(id+"F0.wireOp",EDGE,"E3.10.1"),sQuery(id+"F0.wireOp",EDGE,"E3.10.2"),sQuery(id+"F0.wireOp",EDGE,"E3.10.3"),sQuery(id+"F0.wireOp",EDGE,"E3.11.1"),sQuery(id+"F0.wireOp",EDGE,"E3.11.2"),sQuery(id+"F0.wireOp",EDGE,"E3.11.3"),sQuery(id+"F0.wireOp",EDGE,"E3.12.1"),sQuery(id+"F0.wireOp",EDGE,"E3.12.2"),sQuery(id+"F0.wireOp",EDGE,"E3.12.3")])],"isStart":true})],"blendedInto":[makeQuery(id+"F1.opExtrude","CAP_FACE",FACE,{"disambiguationData":[OSD([sQuery(id+"F0.wireOp",EDGE,"E0"),sQuery(id+"F0.wireOp",EDGE,"E1"),sQuery(id+"F0.wireOp",EDGE,"E2.bottom"),sQuery(id+"F0.wireOp",EDGE,"E2.left"),sQuery(id+"F0.wireOp",EDGE,"E2.right"),sQuery(id+"F0.wireOp",EDGE,"E3.1.1"),sQuery(id+"F0.wireOp",EDGE,"E3.1.2"),sQuery(id+"F0.wireOp",EDGE,"E3.1.3"),sQuery(id+"F0.wireOp",EDGE,"E3.2.1"),subQ1,subQ0,sQuery(id+"F0.wireOp",EDGE,"E3.3.1"),sQuery(id+"F0.wireOp",EDGE,"E3.3.2"),sQuery(id+"F0.wireOp",EDGE,"E3.3.3"),sQuery(id+"F0.wireOp",EDGE,"E3.4.1"),sQuery(id+"F0.wireOp",EDGE,"E3.4.2"),sQuery(id+"F0.wireOp",EDGE,"E3.4.3"),sQuery(id+"F0.wireOp",EDGE,"E3.5.1"),sQuery(id+"F0.wireOp",EDGE,"E3.5.2"),sQuery(id+"F0.wireOp",EDGE,"E3.5.3"),sQuery(id+"F0.wireOp",EDGE,"E3.6.1"),sQuery(id+"F0.wireOp",EDGE,"E3.6.2"),sQuery(id+"F0.wireOp",EDGE,"E3.6.3"),sQuery(id+"F0.wireOp",EDGE,"E3.7.1"),sQuery(id+"F0.wireOp",EDGE,"E3.7.2"),sQuery(id+"F0.wireOp",EDGE,"E3.7.3"),sQuery(id+"F0.wireOp",EDGE,"E3.8.1"),sQuery(id+"F0.wireOp",EDGE,"E3.8.2"),sQuery(id+"F0.wireOp",EDGE,"E3.8.3"),sQuery(id+"F0.wireOp",EDGE,"E3.9.1"),sQuery(id+"F0.wireOp",EDGE,"E3.9.2"),sQuery(id+"F0.wireOp",EDGE,"E3.9.3"),sQuery(id+"F0.wireOp",EDGE,"E3.10.1"),sQuery(id+"F0.wireOp",EDGE,"E3.10.2"),sQuery(id+"F0.wireOp",EDGE,"E3.10.3"),sQuery(id+"F0.wireOp",EDGE,"E3.11.1"),sQuery(id+"F0.wireOp",EDGE,"E3.11.2"),sQuery(id+"F0.wireOp",EDGE,"E3.11.3"),sQuery(id+"F0.wireOp",EDGE,"E3.12.1"),sQuery(id+"F0.wireOp",EDGE,"E3.12.2"),sQuery(id+"F0.wireOp",EDGE,"E3.12.3")])],"isStart":true})]}),makeQuery(id+"F1.opExtrude","CAP_EDGE",EDGE,{"disambiguationData":[OSD([subQ0])],"isStart":true})],"blendedInto":[]});}
            var Q10;
            {var subQ0=sQuery(id+"F0.wireOp",EDGE,"E3.2.1");var subQ1=sQuery(id+"F0.wireOp",EDGE,"E3.2.2");Q10=makeQuery(id+"F4.opChamfer","BLEND_EDGE",EDGE,{"blendedFrom":[makeQuery(id+"F3.opChamfer","BLEND_EDGE",EDGE,{"blendedFrom":[makeQuery(id+"F1.opExtrude","SWEPT_EDGE",EDGE,{"disambiguationData":[OSD([subQ0,subQ1])]}),makeQuery(id+"F1.opExtrude","CAP_FACE",FACE,{"disambiguationData":[OSD([sQuery(id+"F0.wireOp",EDGE,"E0"),sQuery(id+"F0.wireOp",EDGE,"E1"),sQuery(id+"F0.wireOp",EDGE,"E2.bottom"),sQuery(id+"F0.wireOp",EDGE,"E2.left"),sQuery(id+"F0.wireOp",EDGE,"E2.right"),sQuery(id+"F0.wireOp",EDGE,"E3.1.1"),sQuery(id+"F0.wireOp",EDGE,"E3.1.2"),sQuery(id+"F0.wireOp",EDGE,"E3.1.3"),subQ0,subQ1,sQuery(id+"F0.wireOp",EDGE,"E3.2.3"),sQuery(id+"F0.wireOp",EDGE,"E3.3.1"),sQuery(id+"F0.wireOp",EDGE,"E3.3.2"),sQuery(id+"F0.wireOp",EDGE,"E3.3.3"),sQuery(id+"F0.wireOp",EDGE,"E3.4.1"),sQuery(id+"F0.wireOp",EDGE,"E3.4.2"),sQuery(id+"F0.wireOp",EDGE,"E3.4.3"),sQuery(id+"F0.wireOp",EDGE,"E3.5.1"),sQuery(id+"F0.wireOp",EDGE,"E3.5.2"),sQuery(id+"F0.wireOp",EDGE,"E3.5.3"),sQuery(id+"F0.wireOp",EDGE,"E3.6.1"),sQuery(id+"F0.wireOp",EDGE,"E3.6.2"),sQuery(id+"F0.wireOp",EDGE,"E3.6.3"),sQuery(id+"F0.wireOp",EDGE,"E3.7.1"),sQuery(id+"F0.wireOp",EDGE,"E3.7.2"),sQuery(id+"F0.wireOp",EDGE,"E3.7.3"),sQuery(id+"F0.wireOp",EDGE,"E3.8.1"),sQuery(id+"F0.wireOp",EDGE,"E3.8.2"),sQuery(id+"F0.wireOp",EDGE,"E3.8.3"),sQuery(id+"F0.wireOp",EDGE,"E3.9.1"),sQuery(id+"F0.wireOp",EDGE,"E3.9.2"),sQuery(id+"F0.wireOp",EDGE,"E3.9.3"),sQuery(id+"F0.wireOp",EDGE,"E3.10.1"),sQuery(id+"F0.wireOp",EDGE,"E3.10.2"),sQuery(id+"F0.wireOp",EDGE,"E3.10.3"),sQuery(id+"F0.wireOp",EDGE,"E3.11.1"),sQuery(id+"F0.wireOp",EDGE,"E3.11.2"),sQuery(id+"F0.wireOp",EDGE,"E3.11.3"),sQuery(id+"F0.wireOp",EDGE,"E3.12.1"),sQuery(id+"F0.wireOp",EDGE,"E3.12.2"),sQuery(id+"F0.wireOp",EDGE,"E3.12.3")])],"isStart":true})],"blendedInto":[makeQuery(id+"F1.opExtrude","CAP_FACE",FACE,{"disambiguationData":[OSD([sQuery(id+"F0.wireOp",EDGE,"E0"),sQuery(id+"F0.wireOp",EDGE,"E1"),sQuery(id+"F0.wireOp",EDGE,"E2.bottom"),sQuery(id+"F0.wireOp",EDGE,"E2.left"),sQuery(id+"F0.wireOp",EDGE,"E2.right"),sQuery(id+"F0.wireOp",EDGE,"E3.1.1"),sQuery(id+"F0.wireOp",EDGE,"E3.1.2"),sQuery(id+"F0.wireOp",EDGE,"E3.1.3"),subQ0,subQ1,sQuery(id+"F0.wireOp",EDGE,"E3.2.3"),sQuery(id+"F0.wireOp",EDGE,"E3.3.1"),sQuery(id+"F0.wireOp",EDGE,"E3.3.2"),sQuery(id+"F0.wireOp",EDGE,"E3.3.3"),sQuery(id+"F0.wireOp",EDGE,"E3.4.1"),sQuery(id+"F0.wireOp",EDGE,"E3.4.2"),sQuery(id+"F0.wireOp",EDGE,"E3.4.3"),sQuery(id+"F0.wireOp",EDGE,"E3.5.1"),sQuery(id+"F0.wireOp",EDGE,"E3.5.2"),sQuery(id+"F0.wireOp",EDGE,"E3.5.3"),sQuery(id+"F0.wireOp",EDGE,"E3.6.1"),sQuery(id+"F0.wireOp",EDGE,"E3.6.2"),sQuery(id+"F0.wireOp",EDGE,"E3.6.3"),sQuery(id+"F0.wireOp",EDGE,"E3.7.1"),sQuery(id+"F0.wireOp",EDGE,"E3.7.2"),sQuery(id+"F0.wireOp",EDGE,"E3.7.3"),sQuery(id+"F0.wireOp",EDGE,"E3.8.1"),sQuery(id+"F0.wireOp",EDGE,"E3.8.2"),sQuery(id+"F0.wireOp",EDGE,"E3.8.3"),sQuery(id+"F0.wireOp",EDGE,"E3.9.1"),sQuery(id+"F0.wireOp",EDGE,"E3.9.2"),sQuery(id+"F0.wireOp",EDGE,"E3.9.3"),sQuery(id+"F0.wireOp",EDGE,"E3.10.1"),sQuery(id+"F0.wireOp",EDGE,"E3.10.2"),sQuery(id+"F0.wireOp",EDGE,"E3.10.3"),sQuery(id+"F0.wireOp",EDGE,"E3.11.1"),sQuery(id+"F0.wireOp",EDGE,"E3.11.2"),sQuery(id+"F0.wireOp",EDGE,"E3.11.3"),sQuery(id+"F0.wireOp",EDGE,"E3.12.1"),sQuery(id+"F0.wireOp",EDGE,"E3.12.2"),sQuery(id+"F0.wireOp",EDGE,"E3.12.3")])],"isStart":true})]}),makeQuery(id+"F1.opExtrude","CAP_EDGE",EDGE,{"disambiguationData":[OSD([subQ0])],"isStart":true})],"blendedInto":[]});}
            var Q11;
            {var subQ0=sQuery(id+"F0.wireOp",EDGE,"E3.2.3");Q11=makeQuery(id+"F3.opChamfer","BLEND_EDGE",EDGE,{"blendedFrom":[makeQuery(id+"F1.opExtrude","SWEPT_EDGE",EDGE,{"disambiguationData":[OSD([sQuery(id+"F0.wireOp",EDGE,"E3.2.2"),subQ0])]}),makeQuery(id+"F1.opExtrude","SWEPT_FACE",FACE,{"disambiguationData":[OSD([subQ0])]})],"blendedInto":[makeQuery(id+"F1.opExtrude","SWEPT_FACE",FACE,{"disambiguationData":[OSD([subQ0])]})]});}
            var Q12;
            {var subQ0=sQuery(id+"F0.wireOp",EDGE,"E2.left");var subQ1=sQuery(id+"F0.wireOp",EDGE,"E2.bottom");Q12=makeQuery(id+"F4.opChamfer","BLEND_EDGE",EDGE,{"blendedFrom":[makeQuery(id+"F3.opChamfer","BLEND_EDGE",EDGE,{"blendedFrom":[makeQuery(id+"F1.opExtrude","SWEPT_EDGE",EDGE,{"disambiguationData":[OSD([subQ1,subQ0])]}),makeQuery(id+"F1.opExtrude","CAP_FACE",FACE,{"disambiguationData":[OSD([sQuery(id+"F0.wireOp",EDGE,"E0"),sQuery(id+"F0.wireOp",EDGE,"E1"),subQ1,subQ0,sQuery(id+"F0.wireOp",EDGE,"E2.right"),sQuery(id+"F0.wireOp",EDGE,"E3.1.1"),sQuery(id+"F0.wireOp",EDGE,"E3.1.2"),sQuery(id+"F0.wireOp",EDGE,"E3.1.3"),sQuery(id+"F0.wireOp",EDGE,"E3.2.1"),sQuery(id+"F0.wireOp",EDGE,"E3.2.2"),sQuery(id+"F0.wireOp",EDGE,"E3.2.3"),sQuery(id+"F0.wireOp",EDGE,"E3.3.1"),sQuery(id+"F0.wireOp",EDGE,"E3.3.2"),sQuery(id+"F0.wireOp",EDGE,"E3.3.3"),sQuery(id+"F0.wireOp",EDGE,"E3.4.1"),sQuery(id+"F0.wireOp",EDGE,"E3.4.2"),sQuery(id+"F0.wireOp",EDGE,"E3.4.3"),sQuery(id+"F0.wireOp",EDGE,"E3.5.1"),sQuery(id+"F0.wireOp",EDGE,"E3.5.2"),sQuery(id+"F0.wireOp",EDGE,"E3.5.3"),sQuery(id+"F0.wireOp",EDGE,"E3.6.1"),sQuery(id+"F0.wireOp",EDGE,"E3.6.2"),sQuery(id+"F0.wireOp",EDGE,"E3.6.3"),sQuery(id+"F0.wireOp",EDGE,"E3.7.1"),sQuery(id+"F0.wireOp",EDGE,"E3.7.2"),sQuery(id+"F0.wireOp",EDGE,"E3.7.3"),sQuery(id+"F0.wireOp",EDGE,"E3.8.1"),sQuery(id+"F0.wireOp",EDGE,"E3.8.2"),sQuery(id+"F0.wireOp",EDGE,"E3.8.3"),sQuery(id+"F0.wireOp",EDGE,"E3.9.1"),sQuery(id+"F0.wireOp",EDGE,"E3.9.2"),sQuery(id+"F0.wireOp",EDGE,"E3.9.3"),sQuery(id+"F0.wireOp",EDGE,"E3.10.1"),sQuery(id+"F0.wireOp",EDGE,"E3.10.2"),sQuery(id+"F0.wireOp",EDGE,"E3.10.3"),sQuery(id+"F0.wireOp",EDGE,"E3.11.1"),sQuery(id+"F0.wireOp",EDGE,"E3.11.2"),sQuery(id+"F0.wireOp",EDGE,"E3.11.3"),sQuery(id+"F0.wireOp",EDGE,"E3.12.1"),sQuery(id+"F0.wireOp",EDGE,"E3.12.2"),sQuery(id+"F0.wireOp",EDGE,"E3.12.3")])],"isStart":true})],"blendedInto":[makeQuery(id+"F1.opExtrude","CAP_FACE",FACE,{"disambiguationData":[OSD([sQuery(id+"F0.wireOp",EDGE,"E0"),sQuery(id+"F0.wireOp",EDGE,"E1"),subQ1,subQ0,sQuery(id+"F0.wireOp",EDGE,"E2.right"),sQuery(id+"F0.wireOp",EDGE,"E3.1.1"),sQuery(id+"F0.wireOp",EDGE,"E3.1.2"),sQuery(id+"F0.wireOp",EDGE,"E3.1.3"),sQuery(id+"F0.wireOp",EDGE,"E3.2.1"),sQuery(id+"F0.wireOp",EDGE,"E3.2.2"),sQuery(id+"F0.wireOp",EDGE,"E3.2.3"),sQuery(id+"F0.wireOp",EDGE,"E3.3.1"),sQuery(id+"F0.wireOp",EDGE,"E3.3.2"),sQuery(id+"F0.wireOp",EDGE,"E3.3.3"),sQuery(id+"F0.wireOp",EDGE,"E3.4.1"),sQuery(id+"F0.wireOp",EDGE,"E3.4.2"),sQuery(id+"F0.wireOp",EDGE,"E3.4.3"),sQuery(id+"F0.wireOp",EDGE,"E3.5.1"),sQuery(id+"F0.wireOp",EDGE,"E3.5.2"),sQuery(id+"F0.wireOp",EDGE,"E3.5.3"),sQuery(id+"F0.wireOp",EDGE,"E3.6.1"),sQuery(id+"F0.wireOp",EDGE,"E3.6.2"),sQuery(id+"F0.wireOp",EDGE,"E3.6.3"),sQuery(id+"F0.wireOp",EDGE,"E3.7.1"),sQuery(id+"F0.wireOp",EDGE,"E3.7.2"),sQuery(id+"F0.wireOp",EDGE,"E3.7.3"),sQuery(id+"F0.wireOp",EDGE,"E3.8.1"),sQuery(id+"F0.wireOp",EDGE,"E3.8.2"),sQuery(id+"F0.wireOp",EDGE,"E3.8.3"),sQuery(id+"F0.wireOp",EDGE,"E3.9.1"),sQuery(id+"F0.wireOp",EDGE,"E3.9.2"),sQuery(id+"F0.wireOp",EDGE,"E3.9.3"),sQuery(id+"F0.wireOp",EDGE,"E3.10.1"),sQuery(id+"F0.wireOp",EDGE,"E3.10.2"),sQuery(id+"F0.wireOp",EDGE,"E3.10.3"),sQuery(id+"F0.wireOp",EDGE,"E3.11.1"),sQuery(id+"F0.wireOp",EDGE,"E3.11.2"),sQuery(id+"F0.wireOp",EDGE,"E3.11.3"),sQuery(id+"F0.wireOp",EDGE,"E3.12.1"),sQuery(id+"F0.wireOp",EDGE,"E3.12.2"),sQuery(id+"F0.wireOp",EDGE,"E3.12.3")])],"isStart":true})]}),makeQuery(id+"F1.opExtrude","CAP_EDGE",EDGE,{"disambiguationData":[OSD([subQ0])],"isStart":true})],"blendedInto":[]});}
            var Q13;
            {var subQ0=sQuery(id+"F0.wireOp",EDGE,"E2.right");var subQ1=sQuery(id+"F0.wireOp",EDGE,"E2.bottom");Q13=makeQuery(id+"F4.opChamfer","BLEND_EDGE",EDGE,{"blendedFrom":[makeQuery(id+"F3.opChamfer","BLEND_EDGE",EDGE,{"blendedFrom":[makeQuery(id+"F1.opExtrude","SWEPT_EDGE",EDGE,{"disambiguationData":[OSD([subQ1,subQ0])]}),makeQuery(id+"F1.opExtrude","CAP_FACE",FACE,{"disambiguationData":[OSD([sQuery(id+"F0.wireOp",EDGE,"E0"),sQuery(id+"F0.wireOp",EDGE,"E1"),subQ1,sQuery(id+"F0.wireOp",EDGE,"E2.left"),subQ0,sQuery(id+"F0.wireOp",EDGE,"E3.1.1"),sQuery(id+"F0.wireOp",EDGE,"E3.1.2"),sQuery(id+"F0.wireOp",EDGE,"E3.1.3"),sQuery(id+"F0.wireOp",EDGE,"E3.2.1"),sQuery(id+"F0.wireOp",EDGE,"E3.2.2"),sQuery(id+"F0.wireOp",EDGE,"E3.2.3"),sQuery(id+"F0.wireOp",EDGE,"E3.3.1"),sQuery(id+"F0.wireOp",EDGE,"E3.3.2"),sQuery(id+"F0.wireOp",EDGE,"E3.3.3"),sQuery(id+"F0.wireOp",EDGE,"E3.4.1"),sQuery(id+"F0.wireOp",EDGE,"E3.4.2"),sQuery(id+"F0.wireOp",EDGE,"E3.4.3"),sQuery(id+"F0.wireOp",EDGE,"E3.5.1"),sQuery(id+"F0.wireOp",EDGE,"E3.5.2"),sQuery(id+"F0.wireOp",EDGE,"E3.5.3"),sQuery(id+"F0.wireOp",EDGE,"E3.6.1"),sQuery(id+"F0.wireOp",EDGE,"E3.6.2"),sQuery(id+"F0.wireOp",EDGE,"E3.6.3"),sQuery(id+"F0.wireOp",EDGE,"E3.7.1"),sQuery(id+"F0.wireOp",EDGE,"E3.7.2"),sQuery(id+"F0.wireOp",EDGE,"E3.7.3"),sQuery(id+"F0.wireOp",EDGE,"E3.8.1"),sQuery(id+"F0.wireOp",EDGE,"E3.8.2"),sQuery(id+"F0.wireOp",EDGE,"E3.8.3"),sQuery(id+"F0.wireOp",EDGE,"E3.9.1"),sQuery(id+"F0.wireOp",EDGE,"E3.9.2"),sQuery(id+"F0.wireOp",EDGE,"E3.9.3"),sQuery(id+"F0.wireOp",EDGE,"E3.10.1"),sQuery(id+"F0.wireOp",EDGE,"E3.10.2"),sQuery(id+"F0.wireOp",EDGE,"E3.10.3"),sQuery(id+"F0.wireOp",EDGE,"E3.11.1"),sQuery(id+"F0.wireOp",EDGE,"E3.11.2"),sQuery(id+"F0.wireOp",EDGE,"E3.11.3"),sQuery(id+"F0.wireOp",EDGE,"E3.12.1"),sQuery(id+"F0.wireOp",EDGE,"E3.12.2"),sQuery(id+"F0.wireOp",EDGE,"E3.12.3")])],"isStart":true})],"blendedInto":[makeQuery(id+"F1.opExtrude","CAP_FACE",FACE,{"disambiguationData":[OSD([sQuery(id+"F0.wireOp",EDGE,"E0"),sQuery(id+"F0.wireOp",EDGE,"E1"),subQ1,sQuery(id+"F0.wireOp",EDGE,"E2.left"),subQ0,sQuery(id+"F0.wireOp",EDGE,"E3.1.1"),sQuery(id+"F0.wireOp",EDGE,"E3.1.2"),sQuery(id+"F0.wireOp",EDGE,"E3.1.3"),sQuery(id+"F0.wireOp",EDGE,"E3.2.1"),sQuery(id+"F0.wireOp",EDGE,"E3.2.2"),sQuery(id+"F0.wireOp",EDGE,"E3.2.3"),sQuery(id+"F0.wireOp",EDGE,"E3.3.1"),sQuery(id+"F0.wireOp",EDGE,"E3.3.2"),sQuery(id+"F0.wireOp",EDGE,"E3.3.3"),sQuery(id+"F0.wireOp",EDGE,"E3.4.1"),sQuery(id+"F0.wireOp",EDGE,"E3.4.2"),sQuery(id+"F0.wireOp",EDGE,"E3.4.3"),sQuery(id+"F0.wireOp",EDGE,"E3.5.1"),sQuery(id+"F0.wireOp",EDGE,"E3.5.2"),sQuery(id+"F0.wireOp",EDGE,"E3.5.3"),sQuery(id+"F0.wireOp",EDGE,"E3.6.1"),sQuery(id+"F0.wireOp",EDGE,"E3.6.2"),sQuery(id+"F0.wireOp",EDGE,"E3.6.3"),sQuery(id+"F0.wireOp",EDGE,"E3.7.1"),sQuery(id+"F0.wireOp",EDGE,"E3.7.2"),sQuery(id+"F0.wireOp",EDGE,"E3.7.3"),sQuery(id+"F0.wireOp",EDGE,"E3.8.1"),sQuery(id+"F0.wireOp",EDGE,"E3.8.2"),sQuery(id+"F0.wireOp",EDGE,"E3.8.3"),sQuery(id+"F0.wireOp",EDGE,"E3.9.1"),sQuery(id+"F0.wireOp",EDGE,"E3.9.2"),sQuery(id+"F0.wireOp",EDGE,"E3.9.3"),sQuery(id+"F0.wireOp",EDGE,"E3.10.1"),sQuery(id+"F0.wireOp",EDGE,"E3.10.2"),sQuery(id+"F0.wireOp",EDGE,"E3.10.3"),sQuery(id+"F0.wireOp",EDGE,"E3.11.1"),sQuery(id+"F0.wireOp",EDGE,"E3.11.2"),sQuery(id+"F0.wireOp",EDGE,"E3.11.3"),sQuery(id+"F0.wireOp",EDGE,"E3.12.1"),sQuery(id+"F0.wireOp",EDGE,"E3.12.2"),sQuery(id+"F0.wireOp",EDGE,"E3.12.3")])],"isStart":true})]}),makeQuery(id+"F1.opExtrude","CAP_EDGE",EDGE,{"disambiguationData":[OSD([subQ0])],"isStart":true})],"blendedInto":[]});}
            var Q14;
            {var subQ0=sQuery(id+"F0.wireOp",EDGE,"E2.right");Q14=makeQuery(id+"F3.opChamfer","BLEND_EDGE",EDGE,{"blendedFrom":[makeQuery(id+"F1.opExtrude","SWEPT_EDGE",EDGE,{"disambiguationData":[OSD([sQuery(id+"F0.wireOp",EDGE,"E2.bottom"),subQ0])]}),makeQuery(id+"F1.opExtrude","SWEPT_FACE",FACE,{"disambiguationData":[OSD([subQ0])]})],"blendedInto":[makeQuery(id+"F1.opExtrude","SWEPT_FACE",FACE,{"disambiguationData":[OSD([subQ0])]})]});}
            var Q15;
            {var subQ0=sQuery(id+"F0.wireOp",EDGE,"E3.12.3");Q15=makeQuery(id+"F3.opChamfer","BLEND_EDGE",EDGE,{"blendedFrom":[makeQuery(id+"F1.opExtrude","SWEPT_EDGE",EDGE,{"disambiguationData":[OSD([sQuery(id+"F0.wireOp",EDGE,"E3.12.2"),subQ0])]}),makeQuery(id+"F1.opExtrude","SWEPT_FACE",FACE,{"disambiguationData":[OSD([subQ0])]})],"blendedInto":[makeQuery(id+"F1.opExtrude","SWEPT_FACE",FACE,{"disambiguationData":[OSD([subQ0])]})]});}
            var Q16;
            {var subQ0=sQuery(id+"F0.wireOp",EDGE,"E3.12.1");var subQ1=sQuery(id+"F0.wireOp",EDGE,"E3.12.2");Q16=makeQuery(id+"F4.opChamfer","BLEND_EDGE",EDGE,{"blendedFrom":[makeQuery(id+"F3.opChamfer","BLEND_EDGE",EDGE,{"blendedFrom":[makeQuery(id+"F1.opExtrude","SWEPT_EDGE",EDGE,{"disambiguationData":[OSD([subQ0,subQ1])]}),makeQuery(id+"F1.opExtrude","CAP_FACE",FACE,{"disambiguationData":[OSD([sQuery(id+"F0.wireOp",EDGE,"E0"),sQuery(id+"F0.wireOp",EDGE,"E1"),sQuery(id+"F0.wireOp",EDGE,"E2.bottom"),sQuery(id+"F0.wireOp",EDGE,"E2.left"),sQuery(id+"F0.wireOp",EDGE,"E2.right"),sQuery(id+"F0.wireOp",EDGE,"E3.1.1"),sQuery(id+"F0.wireOp",EDGE,"E3.1.2"),sQuery(id+"F0.wireOp",EDGE,"E3.1.3"),sQuery(id+"F0.wireOp",EDGE,"E3.2.1"),sQuery(id+"F0.wireOp",EDGE,"E3.2.2"),sQuery(id+"F0.wireOp",EDGE,"E3.2.3"),sQuery(id+"F0.wireOp",EDGE,"E3.3.1"),sQuery(id+"F0.wireOp",EDGE,"E3.3.2"),sQuery(id+"F0.wireOp",EDGE,"E3.3.3"),sQuery(id+"F0.wireOp",EDGE,"E3.4.1"),sQuery(id+"F0.wireOp",EDGE,"E3.4.2"),sQuery(id+"F0.wireOp",EDGE,"E3.4.3"),sQuery(id+"F0.wireOp",EDGE,"E3.5.1"),sQuery(id+"F0.wireOp",EDGE,"E3.5.2"),sQuery(id+"F0.wireOp",EDGE,"E3.5.3"),sQuery(id+"F0.wireOp",EDGE,"E3.6.1"),sQuery(id+"F0.wireOp",EDGE,"E3.6.2"),sQuery(id+"F0.wireOp",EDGE,"E3.6.3"),sQuery(id+"F0.wireOp",EDGE,"E3.7.1"),sQuery(id+"F0.wireOp",EDGE,"E3.7.2"),sQuery(id+"F0.wireOp",EDGE,"E3.7.3"),sQuery(id+"F0.wireOp",EDGE,"E3.8.1"),sQuery(id+"F0.wireOp",EDGE,"E3.8.2"),sQuery(id+"F0.wireOp",EDGE,"E3.8.3"),sQuery(id+"F0.wireOp",EDGE,"E3.9.1"),sQuery(id+"F0.wireOp",EDGE,"E3.9.2"),sQuery(id+"F0.wireOp",EDGE,"E3.9.3"),sQuery(id+"F0.wireOp",EDGE,"E3.10.1"),sQuery(id+"F0.wireOp",EDGE,"E3.10.2"),sQuery(id+"F0.wireOp",EDGE,"E3.10.3"),sQuery(id+"F0.wireOp",EDGE,"E3.11.1"),sQuery(id+"F0.wireOp",EDGE,"E3.11.2"),sQuery(id+"F0.wireOp",EDGE,"E3.11.3"),subQ0,subQ1,sQuery(id+"F0.wireOp",EDGE,"E3.12.3")])],"isStart":true})],"blendedInto":[makeQuery(id+"F1.opExtrude","CAP_FACE",FACE,{"disambiguationData":[OSD([sQuery(id+"F0.wireOp",EDGE,"E0"),sQuery(id+"F0.wireOp",EDGE,"E1"),sQuery(id+"F0.wireOp",EDGE,"E2.bottom"),sQuery(id+"F0.wireOp",EDGE,"E2.left"),sQuery(id+"F0.wireOp",EDGE,"E2.right"),sQuery(id+"F0.wireOp",EDGE,"E3.1.1"),sQuery(id+"F0.wireOp",EDGE,"E3.1.2"),sQuery(id+"F0.wireOp",EDGE,"E3.1.3"),sQuery(id+"F0.wireOp",EDGE,"E3.2.1"),sQuery(id+"F0.wireOp",EDGE,"E3.2.2"),sQuery(id+"F0.wireOp",EDGE,"E3.2.3"),sQuery(id+"F0.wireOp",EDGE,"E3.3.1"),sQuery(id+"F0.wireOp",EDGE,"E3.3.2"),sQuery(id+"F0.wireOp",EDGE,"E3.3.3"),sQuery(id+"F0.wireOp",EDGE,"E3.4.1"),sQuery(id+"F0.wireOp",EDGE,"E3.4.2"),sQuery(id+"F0.wireOp",EDGE,"E3.4.3"),sQuery(id+"F0.wireOp",EDGE,"E3.5.1"),sQuery(id+"F0.wireOp",EDGE,"E3.5.2"),sQuery(id+"F0.wireOp",EDGE,"E3.5.3"),sQuery(id+"F0.wireOp",EDGE,"E3.6.1"),sQuery(id+"F0.wireOp",EDGE,"E3.6.2"),sQuery(id+"F0.wireOp",EDGE,"E3.6.3"),sQuery(id+"F0.wireOp",EDGE,"E3.7.1"),sQuery(id+"F0.wireOp",EDGE,"E3.7.2"),sQuery(id+"F0.wireOp",EDGE,"E3.7.3"),sQuery(id+"F0.wireOp",EDGE,"E3.8.1"),sQuery(id+"F0.wireOp",EDGE,"E3.8.2"),sQuery(id+"F0.wireOp",EDGE,"E3.8.3"),sQuery(id+"F0.wireOp",EDGE,"E3.9.1"),sQuery(id+"F0.wireOp",EDGE,"E3.9.2"),sQuery(id+"F0.wireOp",EDGE,"E3.9.3"),sQuery(id+"F0.wireOp",EDGE,"E3.10.1"),sQuery(id+"F0.wireOp",EDGE,"E3.10.2"),sQuery(id+"F0.wireOp",EDGE,"E3.10.3"),sQuery(id+"F0.wireOp",EDGE,"E3.11.1"),sQuery(id+"F0.wireOp",EDGE,"E3.11.2"),sQuery(id+"F0.wireOp",EDGE,"E3.11.3"),subQ0,subQ1,sQuery(id+"F0.wireOp",EDGE,"E3.12.3")])],"isStart":true})]}),makeQuery(id+"F1.opExtrude","CAP_EDGE",EDGE,{"disambiguationData":[OSD([subQ0])],"isStart":true})],"blendedInto":[]});}
            var Q17;
            {var subQ0=sQuery(id+"F0.wireOp",EDGE,"E3.12.3");var subQ1=sQuery(id+"F0.wireOp",EDGE,"E3.12.2");Q17=makeQuery(id+"F4.opChamfer","BLEND_EDGE",EDGE,{"blendedFrom":[makeQuery(id+"F3.opChamfer","BLEND_EDGE",EDGE,{"blendedFrom":[makeQuery(id+"F1.opExtrude","SWEPT_EDGE",EDGE,{"disambiguationData":[OSD([subQ1,subQ0])]}),makeQuery(id+"F1.opExtrude","CAP_FACE",FACE,{"disambiguationData":[OSD([sQuery(id+"F0.wireOp",EDGE,"E0"),sQuery(id+"F0.wireOp",EDGE,"E1"),sQuery(id+"F0.wireOp",EDGE,"E2.bottom"),sQuery(id+"F0.wireOp",EDGE,"E2.left"),sQuery(id+"F0.wireOp",EDGE,"E2.right"),sQuery(id+"F0.wireOp",EDGE,"E3.1.1"),sQuery(id+"F0.wireOp",EDGE,"E3.1.2"),sQuery(id+"F0.wireOp",EDGE,"E3.1.3"),sQuery(id+"F0.wireOp",EDGE,"E3.2.1"),sQuery(id+"F0.wireOp",EDGE,"E3.2.2"),sQuery(id+"F0.wireOp",EDGE,"E3.2.3"),sQuery(id+"F0.wireOp",EDGE,"E3.3.1"),sQuery(id+"F0.wireOp",EDGE,"E3.3.2"),sQuery(id+"F0.wireOp",EDGE,"E3.3.3"),sQuery(id+"F0.wireOp",EDGE,"E3.4.1"),sQuery(id+"F0.wireOp",EDGE,"E3.4.2"),sQuery(id+"F0.wireOp",EDGE,"E3.4.3"),sQuery(id+"F0.wireOp",EDGE,"E3.5.1"),sQuery(id+"F0.wireOp",EDGE,"E3.5.2"),sQuery(id+"F0.wireOp",EDGE,"E3.5.3"),sQuery(id+"F0.wireOp",EDGE,"E3.6.1"),sQuery(id+"F0.wireOp",EDGE,"E3.6.2"),sQuery(id+"F0.wireOp",EDGE,"E3.6.3"),sQuery(id+"F0.wireOp",EDGE,"E3.7.1"),sQuery(id+"F0.wireOp",EDGE,"E3.7.2"),sQuery(id+"F0.wireOp",EDGE,"E3.7.3"),sQuery(id+"F0.wireOp",EDGE,"E3.8.1"),sQuery(id+"F0.wireOp",EDGE,"E3.8.2"),sQuery(id+"F0.wireOp",EDGE,"E3.8.3"),sQuery(id+"F0.wireOp",EDGE,"E3.9.1"),sQuery(id+"F0.wireOp",EDGE,"E3.9.2"),sQuery(id+"F0.wireOp",EDGE,"E3.9.3"),sQuery(id+"F0.wireOp",EDGE,"E3.10.1"),sQuery(id+"F0.wireOp",EDGE,"E3.10.2"),sQuery(id+"F0.wireOp",EDGE,"E3.10.3"),sQuery(id+"F0.wireOp",EDGE,"E3.11.1"),sQuery(id+"F0.wireOp",EDGE,"E3.11.2"),sQuery(id+"F0.wireOp",EDGE,"E3.11.3"),sQuery(id+"F0.wireOp",EDGE,"E3.12.1"),subQ1,subQ0])],"isStart":true})],"blendedInto":[makeQuery(id+"F1.opExtrude","CAP_FACE",FACE,{"disambiguationData":[OSD([sQuery(id+"F0.wireOp",EDGE,"E0"),sQuery(id+"F0.wireOp",EDGE,"E1"),sQuery(id+"F0.wireOp",EDGE,"E2.bottom"),sQuery(id+"F0.wireOp",EDGE,"E2.left"),sQuery(id+"F0.wireOp",EDGE,"E2.right"),sQuery(id+"F0.wireOp",EDGE,"E3.1.1"),sQuery(id+"F0.wireOp",EDGE,"E3.1.2"),sQuery(id+"F0.wireOp",EDGE,"E3.1.3"),sQuery(id+"F0.wireOp",EDGE,"E3.2.1"),sQuery(id+"F0.wireOp",EDGE,"E3.2.2"),sQuery(id+"F0.wireOp",EDGE,"E3.2.3"),sQuery(id+"F0.wireOp",EDGE,"E3.3.1"),sQuery(id+"F0.wireOp",EDGE,"E3.3.2"),sQuery(id+"F0.wireOp",EDGE,"E3.3.3"),sQuery(id+"F0.wireOp",EDGE,"E3.4.1"),sQuery(id+"F0.wireOp",EDGE,"E3.4.2"),sQuery(id+"F0.wireOp",EDGE,"E3.4.3"),sQuery(id+"F0.wireOp",EDGE,"E3.5.1"),sQuery(id+"F0.wireOp",EDGE,"E3.5.2"),sQuery(id+"F0.wireOp",EDGE,"E3.5.3"),sQuery(id+"F0.wireOp",EDGE,"E3.6.1"),sQuery(id+"F0.wireOp",EDGE,"E3.6.2"),sQuery(id+"F0.wireOp",EDGE,"E3.6.3"),sQuery(id+"F0.wireOp",EDGE,"E3.7.1"),sQuery(id+"F0.wireOp",EDGE,"E3.7.2"),sQuery(id+"F0.wireOp",EDGE,"E3.7.3"),sQuery(id+"F0.wireOp",EDGE,"E3.8.1"),sQuery(id+"F0.wireOp",EDGE,"E3.8.2"),sQuery(id+"F0.wireOp",EDGE,"E3.8.3"),sQuery(id+"F0.wireOp",EDGE,"E3.9.1"),sQuery(id+"F0.wireOp",EDGE,"E3.9.2"),sQuery(id+"F0.wireOp",EDGE,"E3.9.3"),sQuery(id+"F0.wireOp",EDGE,"E3.10.1"),sQuery(id+"F0.wireOp",EDGE,"E3.10.2"),sQuery(id+"F0.wireOp",EDGE,"E3.10.3"),sQuery(id+"F0.wireOp",EDGE,"E3.11.1"),sQuery(id+"F0.wireOp",EDGE,"E3.11.2"),sQuery(id+"F0.wireOp",EDGE,"E3.11.3"),sQuery(id+"F0.wireOp",EDGE,"E3.12.1"),subQ1,subQ0])],"isStart":true})]}),makeQuery(id+"F1.opExtrude","CAP_EDGE",EDGE,{"disambiguationData":[OSD([subQ0])],"isStart":true})],"blendedInto":[]});}
            var Q18;
            {var subQ0=sQuery(id+"F0.wireOp",EDGE,"E3.12.1");Q18=makeQuery(id+"F3.opChamfer","BLEND_EDGE",EDGE,{"blendedFrom":[makeQuery(id+"F1.opExtrude","SWEPT_EDGE",EDGE,{"disambiguationData":[OSD([subQ0,sQuery(id+"F0.wireOp",EDGE,"E3.12.2")])]}),makeQuery(id+"F1.opExtrude","SWEPT_FACE",FACE,{"disambiguationData":[OSD([subQ0])]})],"blendedInto":[makeQuery(id+"F1.opExtrude","SWEPT_FACE",FACE,{"disambiguationData":[OSD([subQ0])]})]});}
            var Q19;
            {var subQ0=sQuery(id+"F0.wireOp",EDGE,"E3.11.1");var subQ1=sQuery(id+"F0.wireOp",EDGE,"E3.11.2");Q19=makeQuery(id+"F4.opChamfer","BLEND_EDGE",EDGE,{"blendedFrom":[makeQuery(id+"F3.opChamfer","BLEND_EDGE",EDGE,{"blendedFrom":[makeQuery(id+"F1.opExtrude","SWEPT_EDGE",EDGE,{"disambiguationData":[OSD([subQ0,subQ1])]}),makeQuery(id+"F1.opExtrude","CAP_FACE",FACE,{"disambiguationData":[OSD([sQuery(id+"F0.wireOp",EDGE,"E0"),sQuery(id+"F0.wireOp",EDGE,"E1"),sQuery(id+"F0.wireOp",EDGE,"E2.bottom"),sQuery(id+"F0.wireOp",EDGE,"E2.left"),sQuery(id+"F0.wireOp",EDGE,"E2.right"),sQuery(id+"F0.wireOp",EDGE,"E3.1.1"),sQuery(id+"F0.wireOp",EDGE,"E3.1.2"),sQuery(id+"F0.wireOp",EDGE,"E3.1.3"),sQuery(id+"F0.wireOp",EDGE,"E3.2.1"),sQuery(id+"F0.wireOp",EDGE,"E3.2.2"),sQuery(id+"F0.wireOp",EDGE,"E3.2.3"),sQuery(id+"F0.wireOp",EDGE,"E3.3.1"),sQuery(id+"F0.wireOp",EDGE,"E3.3.2"),sQuery(id+"F0.wireOp",EDGE,"E3.3.3"),sQuery(id+"F0.wireOp",EDGE,"E3.4.1"),sQuery(id+"F0.wireOp",EDGE,"E3.4.2"),sQuery(id+"F0.wireOp",EDGE,"E3.4.3"),sQuery(id+"F0.wireOp",EDGE,"E3.5.1"),sQuery(id+"F0.wireOp",EDGE,"E3.5.2"),sQuery(id+"F0.wireOp",EDGE,"E3.5.3"),sQuery(id+"F0.wireOp",EDGE,"E3.6.1"),sQuery(id+"F0.wireOp",EDGE,"E3.6.2"),sQuery(id+"F0.wireOp",EDGE,"E3.6.3"),sQuery(id+"F0.wireOp",EDGE,"E3.7.1"),sQuery(id+"F0.wireOp",EDGE,"E3.7.2"),sQuery(id+"F0.wireOp",EDGE,"E3.7.3"),sQuery(id+"F0.wireOp",EDGE,"E3.8.1"),sQuery(id+"F0.wireOp",EDGE,"E3.8.2"),sQuery(id+"F0.wireOp",EDGE,"E3.8.3"),sQuery(id+"F0.wireOp",EDGE,"E3.9.1"),sQuery(id+"F0.wireOp",EDGE,"E3.9.2"),sQuery(id+"F0.wireOp",EDGE,"E3.9.3"),sQuery(id+"F0.wireOp",EDGE,"E3.10.1"),sQuery(id+"F0.wireOp",EDGE,"E3.10.2"),sQuery(id+"F0.wireOp",EDGE,"E3.10.3"),subQ0,subQ1,sQuery(id+"F0.wireOp",EDGE,"E3.11.3"),sQuery(id+"F0.wireOp",EDGE,"E3.12.1"),sQuery(id+"F0.wireOp",EDGE,"E3.12.2"),sQuery(id+"F0.wireOp",EDGE,"E3.12.3")])],"isStart":true})],"blendedInto":[makeQuery(id+"F1.opExtrude","CAP_FACE",FACE,{"disambiguationData":[OSD([sQuery(id+"F0.wireOp",EDGE,"E0"),sQuery(id+"F0.wireOp",EDGE,"E1"),sQuery(id+"F0.wireOp",EDGE,"E2.bottom"),sQuery(id+"F0.wireOp",EDGE,"E2.left"),sQuery(id+"F0.wireOp",EDGE,"E2.right"),sQuery(id+"F0.wireOp",EDGE,"E3.1.1"),sQuery(id+"F0.wireOp",EDGE,"E3.1.2"),sQuery(id+"F0.wireOp",EDGE,"E3.1.3"),sQuery(id+"F0.wireOp",EDGE,"E3.2.1"),sQuery(id+"F0.wireOp",EDGE,"E3.2.2"),sQuery(id+"F0.wireOp",EDGE,"E3.2.3"),sQuery(id+"F0.wireOp",EDGE,"E3.3.1"),sQuery(id+"F0.wireOp",EDGE,"E3.3.2"),sQuery(id+"F0.wireOp",EDGE,"E3.3.3"),sQuery(id+"F0.wireOp",EDGE,"E3.4.1"),sQuery(id+"F0.wireOp",EDGE,"E3.4.2"),sQuery(id+"F0.wireOp",EDGE,"E3.4.3"),sQuery(id+"F0.wireOp",EDGE,"E3.5.1"),sQuery(id+"F0.wireOp",EDGE,"E3.5.2"),sQuery(id+"F0.wireOp",EDGE,"E3.5.3"),sQuery(id+"F0.wireOp",EDGE,"E3.6.1"),sQuery(id+"F0.wireOp",EDGE,"E3.6.2"),sQuery(id+"F0.wireOp",EDGE,"E3.6.3"),sQuery(id+"F0.wireOp",EDGE,"E3.7.1"),sQuery(id+"F0.wireOp",EDGE,"E3.7.2"),sQuery(id+"F0.wireOp",EDGE,"E3.7.3"),sQuery(id+"F0.wireOp",EDGE,"E3.8.1"),sQuery(id+"F0.wireOp",EDGE,"E3.8.2"),sQuery(id+"F0.wireOp",EDGE,"E3.8.3"),sQuery(id+"F0.wireOp",EDGE,"E3.9.1"),sQuery(id+"F0.wireOp",EDGE,"E3.9.2"),sQuery(id+"F0.wireOp",EDGE,"E3.9.3"),sQuery(id+"F0.wireOp",EDGE,"E3.10.1"),sQuery(id+"F0.wireOp",EDGE,"E3.10.2"),sQuery(id+"F0.wireOp",EDGE,"E3.10.3"),subQ0,subQ1,sQuery(id+"F0.wireOp",EDGE,"E3.11.3"),sQuery(id+"F0.wireOp",EDGE,"E3.12.1"),sQuery(id+"F0.wireOp",EDGE,"E3.12.2"),sQuery(id+"F0.wireOp",EDGE,"E3.12.3")])],"isStart":true})]}),makeQuery(id+"F1.opExtrude","CAP_EDGE",EDGE,{"disambiguationData":[OSD([subQ0])],"isStart":true})],"blendedInto":[]});}
            var Q20;
            {var subQ0=sQuery(id+"F0.wireOp",EDGE,"E3.11.1");Q20=makeQuery(id+"F3.opChamfer","BLEND_EDGE",EDGE,{"blendedFrom":[makeQuery(id+"F1.opExtrude","SWEPT_EDGE",EDGE,{"disambiguationData":[OSD([subQ0,sQuery(id+"F0.wireOp",EDGE,"E3.11.2")])]}),makeQuery(id+"F1.opExtrude","SWEPT_FACE",FACE,{"disambiguationData":[OSD([subQ0])]})],"blendedInto":[makeQuery(id+"F1.opExtrude","SWEPT_FACE",FACE,{"disambiguationData":[OSD([subQ0])]})]});}
            var Q21;
            {var subQ0=sQuery(id+"F0.wireOp",EDGE,"E3.11.3");Q21=makeQuery(id+"F3.opChamfer","BLEND_EDGE",EDGE,{"blendedFrom":[makeQuery(id+"F1.opExtrude","SWEPT_EDGE",EDGE,{"disambiguationData":[OSD([sQuery(id+"F0.wireOp",EDGE,"E3.11.2"),subQ0])]}),makeQuery(id+"F1.opExtrude","SWEPT_FACE",FACE,{"disambiguationData":[OSD([subQ0])]})],"blendedInto":[makeQuery(id+"F1.opExtrude","SWEPT_FACE",FACE,{"disambiguationData":[OSD([subQ0])]})]});}
            var Q22;
            {var subQ0=sQuery(id+"F0.wireOp",EDGE,"E3.11.3");var subQ1=sQuery(id+"F0.wireOp",EDGE,"E3.11.2");Q22=makeQuery(id+"F4.opChamfer","BLEND_EDGE",EDGE,{"blendedFrom":[makeQuery(id+"F3.opChamfer","BLEND_EDGE",EDGE,{"blendedFrom":[makeQuery(id+"F1.opExtrude","SWEPT_EDGE",EDGE,{"disambiguationData":[OSD([subQ1,subQ0])]}),makeQuery(id+"F1.opExtrude","CAP_FACE",FACE,{"disambiguationData":[OSD([sQuery(id+"F0.wireOp",EDGE,"E0"),sQuery(id+"F0.wireOp",EDGE,"E1"),sQuery(id+"F0.wireOp",EDGE,"E2.bottom"),sQuery(id+"F0.wireOp",EDGE,"E2.left"),sQuery(id+"F0.wireOp",EDGE,"E2.right"),sQuery(id+"F0.wireOp",EDGE,"E3.1.1"),sQuery(id+"F0.wireOp",EDGE,"E3.1.2"),sQuery(id+"F0.wireOp",EDGE,"E3.1.3"),sQuery(id+"F0.wireOp",EDGE,"E3.2.1"),sQuery(id+"F0.wireOp",EDGE,"E3.2.2"),sQuery(id+"F0.wireOp",EDGE,"E3.2.3"),sQuery(id+"F0.wireOp",EDGE,"E3.3.1"),sQuery(id+"F0.wireOp",EDGE,"E3.3.2"),sQuery(id+"F0.wireOp",EDGE,"E3.3.3"),sQuery(id+"F0.wireOp",EDGE,"E3.4.1"),sQuery(id+"F0.wireOp",EDGE,"E3.4.2"),sQuery(id+"F0.wireOp",EDGE,"E3.4.3"),sQuery(id+"F0.wireOp",EDGE,"E3.5.1"),sQuery(id+"F0.wireOp",EDGE,"E3.5.2"),sQuery(id+"F0.wireOp",EDGE,"E3.5.3"),sQuery(id+"F0.wireOp",EDGE,"E3.6.1"),sQuery(id+"F0.wireOp",EDGE,"E3.6.2"),sQuery(id+"F0.wireOp",EDGE,"E3.6.3"),sQuery(id+"F0.wireOp",EDGE,"E3.7.1"),sQuery(id+"F0.wireOp",EDGE,"E3.7.2"),sQuery(id+"F0.wireOp",EDGE,"E3.7.3"),sQuery(id+"F0.wireOp",EDGE,"E3.8.1"),sQuery(id+"F0.wireOp",EDGE,"E3.8.2"),sQuery(id+"F0.wireOp",EDGE,"E3.8.3"),sQuery(id+"F0.wireOp",EDGE,"E3.9.1"),sQuery(id+"F0.wireOp",EDGE,"E3.9.2"),sQuery(id+"F0.wireOp",EDGE,"E3.9.3"),sQuery(id+"F0.wireOp",EDGE,"E3.10.1"),sQuery(id+"F0.wireOp",EDGE,"E3.10.2"),sQuery(id+"F0.wireOp",EDGE,"E3.10.3"),sQuery(id+"F0.wireOp",EDGE,"E3.11.1"),subQ1,subQ0,sQuery(id+"F0.wireOp",EDGE,"E3.12.1"),sQuery(id+"F0.wireOp",EDGE,"E3.12.2"),sQuery(id+"F0.wireOp",EDGE,"E3.12.3")])],"isStart":true})],"blendedInto":[makeQuery(id+"F1.opExtrude","CAP_FACE",FACE,{"disambiguationData":[OSD([sQuery(id+"F0.wireOp",EDGE,"E0"),sQuery(id+"F0.wireOp",EDGE,"E1"),sQuery(id+"F0.wireOp",EDGE,"E2.bottom"),sQuery(id+"F0.wireOp",EDGE,"E2.left"),sQuery(id+"F0.wireOp",EDGE,"E2.right"),sQuery(id+"F0.wireOp",EDGE,"E3.1.1"),sQuery(id+"F0.wireOp",EDGE,"E3.1.2"),sQuery(id+"F0.wireOp",EDGE,"E3.1.3"),sQuery(id+"F0.wireOp",EDGE,"E3.2.1"),sQuery(id+"F0.wireOp",EDGE,"E3.2.2"),sQuery(id+"F0.wireOp",EDGE,"E3.2.3"),sQuery(id+"F0.wireOp",EDGE,"E3.3.1"),sQuery(id+"F0.wireOp",EDGE,"E3.3.2"),sQuery(id+"F0.wireOp",EDGE,"E3.3.3"),sQuery(id+"F0.wireOp",EDGE,"E3.4.1"),sQuery(id+"F0.wireOp",EDGE,"E3.4.2"),sQuery(id+"F0.wireOp",EDGE,"E3.4.3"),sQuery(id+"F0.wireOp",EDGE,"E3.5.1"),sQuery(id+"F0.wireOp",EDGE,"E3.5.2"),sQuery(id+"F0.wireOp",EDGE,"E3.5.3"),sQuery(id+"F0.wireOp",EDGE,"E3.6.1"),sQuery(id+"F0.wireOp",EDGE,"E3.6.2"),sQuery(id+"F0.wireOp",EDGE,"E3.6.3"),sQuery(id+"F0.wireOp",EDGE,"E3.7.1"),sQuery(id+"F0.wireOp",EDGE,"E3.7.2"),sQuery(id+"F0.wireOp",EDGE,"E3.7.3"),sQuery(id+"F0.wireOp",EDGE,"E3.8.1"),sQuery(id+"F0.wireOp",EDGE,"E3.8.2"),sQuery(id+"F0.wireOp",EDGE,"E3.8.3"),sQuery(id+"F0.wireOp",EDGE,"E3.9.1"),sQuery(id+"F0.wireOp",EDGE,"E3.9.2"),sQuery(id+"F0.wireOp",EDGE,"E3.9.3"),sQuery(id+"F0.wireOp",EDGE,"E3.10.1"),sQuery(id+"F0.wireOp",EDGE,"E3.10.2"),sQuery(id+"F0.wireOp",EDGE,"E3.10.3"),sQuery(id+"F0.wireOp",EDGE,"E3.11.1"),subQ1,subQ0,sQuery(id+"F0.wireOp",EDGE,"E3.12.1"),sQuery(id+"F0.wireOp",EDGE,"E3.12.2"),sQuery(id+"F0.wireOp",EDGE,"E3.12.3")])],"isStart":true})]}),makeQuery(id+"F1.opExtrude","CAP_EDGE",EDGE,{"disambiguationData":[OSD([subQ0])],"isStart":true})],"blendedInto":[]});}
            var Q23;
            {var subQ0=sQuery(id+"F0.wireOp",EDGE,"E3.10.3");Q23=makeQuery(id+"F3.opChamfer","BLEND_EDGE",EDGE,{"blendedFrom":[makeQuery(id+"F1.opExtrude","SWEPT_EDGE",EDGE,{"disambiguationData":[OSD([sQuery(id+"F0.wireOp",EDGE,"E3.10.2"),subQ0])]}),makeQuery(id+"F1.opExtrude","SWEPT_FACE",FACE,{"disambiguationData":[OSD([subQ0])]})],"blendedInto":[makeQuery(id+"F1.opExtrude","SWEPT_FACE",FACE,{"disambiguationData":[OSD([subQ0])]})]});}
            var Q24;
            {var subQ0=sQuery(id+"F0.wireOp",EDGE,"E3.10.3");var subQ1=sQuery(id+"F0.wireOp",EDGE,"E3.10.2");Q24=makeQuery(id+"F4.opChamfer","BLEND_EDGE",EDGE,{"blendedFrom":[makeQuery(id+"F3.opChamfer","BLEND_EDGE",EDGE,{"blendedFrom":[makeQuery(id+"F1.opExtrude","SWEPT_EDGE",EDGE,{"disambiguationData":[OSD([subQ1,subQ0])]}),makeQuery(id+"F1.opExtrude","CAP_FACE",FACE,{"disambiguationData":[OSD([sQuery(id+"F0.wireOp",EDGE,"E0"),sQuery(id+"F0.wireOp",EDGE,"E1"),sQuery(id+"F0.wireOp",EDGE,"E2.bottom"),sQuery(id+"F0.wireOp",EDGE,"E2.left"),sQuery(id+"F0.wireOp",EDGE,"E2.right"),sQuery(id+"F0.wireOp",EDGE,"E3.1.1"),sQuery(id+"F0.wireOp",EDGE,"E3.1.2"),sQuery(id+"F0.wireOp",EDGE,"E3.1.3"),sQuery(id+"F0.wireOp",EDGE,"E3.2.1"),sQuery(id+"F0.wireOp",EDGE,"E3.2.2"),sQuery(id+"F0.wireOp",EDGE,"E3.2.3"),sQuery(id+"F0.wireOp",EDGE,"E3.3.1"),sQuery(id+"F0.wireOp",EDGE,"E3.3.2"),sQuery(id+"F0.wireOp",EDGE,"E3.3.3"),sQuery(id+"F0.wireOp",EDGE,"E3.4.1"),sQuery(id+"F0.wireOp",EDGE,"E3.4.2"),sQuery(id+"F0.wireOp",EDGE,"E3.4.3"),sQuery(id+"F0.wireOp",EDGE,"E3.5.1"),sQuery(id+"F0.wireOp",EDGE,"E3.5.2"),sQuery(id+"F0.wireOp",EDGE,"E3.5.3"),sQuery(id+"F0.wireOp",EDGE,"E3.6.1"),sQuery(id+"F0.wireOp",EDGE,"E3.6.2"),sQuery(id+"F0.wireOp",EDGE,"E3.6.3"),sQuery(id+"F0.wireOp",EDGE,"E3.7.1"),sQuery(id+"F0.wireOp",EDGE,"E3.7.2"),sQuery(id+"F0.wireOp",EDGE,"E3.7.3"),sQuery(id+"F0.wireOp",EDGE,"E3.8.1"),sQuery(id+"F0.wireOp",EDGE,"E3.8.2"),sQuery(id+"F0.wireOp",EDGE,"E3.8.3"),sQuery(id+"F0.wireOp",EDGE,"E3.9.1"),sQuery(id+"F0.wireOp",EDGE,"E3.9.2"),sQuery(id+"F0.wireOp",EDGE,"E3.9.3"),sQuery(id+"F0.wireOp",EDGE,"E3.10.1"),subQ1,subQ0,sQuery(id+"F0.wireOp",EDGE,"E3.11.1"),sQuery(id+"F0.wireOp",EDGE,"E3.11.2"),sQuery(id+"F0.wireOp",EDGE,"E3.11.3"),sQuery(id+"F0.wireOp",EDGE,"E3.12.1"),sQuery(id+"F0.wireOp",EDGE,"E3.12.2"),sQuery(id+"F0.wireOp",EDGE,"E3.12.3")])],"isStart":true})],"blendedInto":[makeQuery(id+"F1.opExtrude","CAP_FACE",FACE,{"disambiguationData":[OSD([sQuery(id+"F0.wireOp",EDGE,"E0"),sQuery(id+"F0.wireOp",EDGE,"E1"),sQuery(id+"F0.wireOp",EDGE,"E2.bottom"),sQuery(id+"F0.wireOp",EDGE,"E2.left"),sQuery(id+"F0.wireOp",EDGE,"E2.right"),sQuery(id+"F0.wireOp",EDGE,"E3.1.1"),sQuery(id+"F0.wireOp",EDGE,"E3.1.2"),sQuery(id+"F0.wireOp",EDGE,"E3.1.3"),sQuery(id+"F0.wireOp",EDGE,"E3.2.1"),sQuery(id+"F0.wireOp",EDGE,"E3.2.2"),sQuery(id+"F0.wireOp",EDGE,"E3.2.3"),sQuery(id+"F0.wireOp",EDGE,"E3.3.1"),sQuery(id+"F0.wireOp",EDGE,"E3.3.2"),sQuery(id+"F0.wireOp",EDGE,"E3.3.3"),sQuery(id+"F0.wireOp",EDGE,"E3.4.1"),sQuery(id+"F0.wireOp",EDGE,"E3.4.2"),sQuery(id+"F0.wireOp",EDGE,"E3.4.3"),sQuery(id+"F0.wireOp",EDGE,"E3.5.1"),sQuery(id+"F0.wireOp",EDGE,"E3.5.2"),sQuery(id+"F0.wireOp",EDGE,"E3.5.3"),sQuery(id+"F0.wireOp",EDGE,"E3.6.1"),sQuery(id+"F0.wireOp",EDGE,"E3.6.2"),sQuery(id+"F0.wireOp",EDGE,"E3.6.3"),sQuery(id+"F0.wireOp",EDGE,"E3.7.1"),sQuery(id+"F0.wireOp",EDGE,"E3.7.2"),sQuery(id+"F0.wireOp",EDGE,"E3.7.3"),sQuery(id+"F0.wireOp",EDGE,"E3.8.1"),sQuery(id+"F0.wireOp",EDGE,"E3.8.2"),sQuery(id+"F0.wireOp",EDGE,"E3.8.3"),sQuery(id+"F0.wireOp",EDGE,"E3.9.1"),sQuery(id+"F0.wireOp",EDGE,"E3.9.2"),sQuery(id+"F0.wireOp",EDGE,"E3.9.3"),sQuery(id+"F0.wireOp",EDGE,"E3.10.1"),subQ1,subQ0,sQuery(id+"F0.wireOp",EDGE,"E3.11.1"),sQuery(id+"F0.wireOp",EDGE,"E3.11.2"),sQuery(id+"F0.wireOp",EDGE,"E3.11.3"),sQuery(id+"F0.wireOp",EDGE,"E3.12.1"),sQuery(id+"F0.wireOp",EDGE,"E3.12.2"),sQuery(id+"F0.wireOp",EDGE,"E3.12.3")])],"isStart":true})]}),makeQuery(id+"F1.opExtrude","CAP_EDGE",EDGE,{"disambiguationData":[OSD([subQ0])],"isStart":true})],"blendedInto":[]});}
            var Q25;
            {var subQ0=sQuery(id+"F0.wireOp",EDGE,"E3.10.1");var subQ1=sQuery(id+"F0.wireOp",EDGE,"E3.10.2");Q25=makeQuery(id+"F4.opChamfer","BLEND_EDGE",EDGE,{"blendedFrom":[makeQuery(id+"F3.opChamfer","BLEND_EDGE",EDGE,{"blendedFrom":[makeQuery(id+"F1.opExtrude","SWEPT_EDGE",EDGE,{"disambiguationData":[OSD([subQ0,subQ1])]}),makeQuery(id+"F1.opExtrude","CAP_FACE",FACE,{"disambiguationData":[OSD([sQuery(id+"F0.wireOp",EDGE,"E0"),sQuery(id+"F0.wireOp",EDGE,"E1"),sQuery(id+"F0.wireOp",EDGE,"E2.bottom"),sQuery(id+"F0.wireOp",EDGE,"E2.left"),sQuery(id+"F0.wireOp",EDGE,"E2.right"),sQuery(id+"F0.wireOp",EDGE,"E3.1.1"),sQuery(id+"F0.wireOp",EDGE,"E3.1.2"),sQuery(id+"F0.wireOp",EDGE,"E3.1.3"),sQuery(id+"F0.wireOp",EDGE,"E3.2.1"),sQuery(id+"F0.wireOp",EDGE,"E3.2.2"),sQuery(id+"F0.wireOp",EDGE,"E3.2.3"),sQuery(id+"F0.wireOp",EDGE,"E3.3.1"),sQuery(id+"F0.wireOp",EDGE,"E3.3.2"),sQuery(id+"F0.wireOp",EDGE,"E3.3.3"),sQuery(id+"F0.wireOp",EDGE,"E3.4.1"),sQuery(id+"F0.wireOp",EDGE,"E3.4.2"),sQuery(id+"F0.wireOp",EDGE,"E3.4.3"),sQuery(id+"F0.wireOp",EDGE,"E3.5.1"),sQuery(id+"F0.wireOp",EDGE,"E3.5.2"),sQuery(id+"F0.wireOp",EDGE,"E3.5.3"),sQuery(id+"F0.wireOp",EDGE,"E3.6.1"),sQuery(id+"F0.wireOp",EDGE,"E3.6.2"),sQuery(id+"F0.wireOp",EDGE,"E3.6.3"),sQuery(id+"F0.wireOp",EDGE,"E3.7.1"),sQuery(id+"F0.wireOp",EDGE,"E3.7.2"),sQuery(id+"F0.wireOp",EDGE,"E3.7.3"),sQuery(id+"F0.wireOp",EDGE,"E3.8.1"),sQuery(id+"F0.wireOp",EDGE,"E3.8.2"),sQuery(id+"F0.wireOp",EDGE,"E3.8.3"),sQuery(id+"F0.wireOp",EDGE,"E3.9.1"),sQuery(id+"F0.wireOp",EDGE,"E3.9.2"),sQuery(id+"F0.wireOp",EDGE,"E3.9.3"),subQ0,subQ1,sQuery(id+"F0.wireOp",EDGE,"E3.10.3"),sQuery(id+"F0.wireOp",EDGE,"E3.11.1"),sQuery(id+"F0.wireOp",EDGE,"E3.11.2"),sQuery(id+"F0.wireOp",EDGE,"E3.11.3"),sQuery(id+"F0.wireOp",EDGE,"E3.12.1"),sQuery(id+"F0.wireOp",EDGE,"E3.12.2"),sQuery(id+"F0.wireOp",EDGE,"E3.12.3")])],"isStart":true})],"blendedInto":[makeQuery(id+"F1.opExtrude","CAP_FACE",FACE,{"disambiguationData":[OSD([sQuery(id+"F0.wireOp",EDGE,"E0"),sQuery(id+"F0.wireOp",EDGE,"E1"),sQuery(id+"F0.wireOp",EDGE,"E2.bottom"),sQuery(id+"F0.wireOp",EDGE,"E2.left"),sQuery(id+"F0.wireOp",EDGE,"E2.right"),sQuery(id+"F0.wireOp",EDGE,"E3.1.1"),sQuery(id+"F0.wireOp",EDGE,"E3.1.2"),sQuery(id+"F0.wireOp",EDGE,"E3.1.3"),sQuery(id+"F0.wireOp",EDGE,"E3.2.1"),sQuery(id+"F0.wireOp",EDGE,"E3.2.2"),sQuery(id+"F0.wireOp",EDGE,"E3.2.3"),sQuery(id+"F0.wireOp",EDGE,"E3.3.1"),sQuery(id+"F0.wireOp",EDGE,"E3.3.2"),sQuery(id+"F0.wireOp",EDGE,"E3.3.3"),sQuery(id+"F0.wireOp",EDGE,"E3.4.1"),sQuery(id+"F0.wireOp",EDGE,"E3.4.2"),sQuery(id+"F0.wireOp",EDGE,"E3.4.3"),sQuery(id+"F0.wireOp",EDGE,"E3.5.1"),sQuery(id+"F0.wireOp",EDGE,"E3.5.2"),sQuery(id+"F0.wireOp",EDGE,"E3.5.3"),sQuery(id+"F0.wireOp",EDGE,"E3.6.1"),sQuery(id+"F0.wireOp",EDGE,"E3.6.2"),sQuery(id+"F0.wireOp",EDGE,"E3.6.3"),sQuery(id+"F0.wireOp",EDGE,"E3.7.1"),sQuery(id+"F0.wireOp",EDGE,"E3.7.2"),sQuery(id+"F0.wireOp",EDGE,"E3.7.3"),sQuery(id+"F0.wireOp",EDGE,"E3.8.1"),sQuery(id+"F0.wireOp",EDGE,"E3.8.2"),sQuery(id+"F0.wireOp",EDGE,"E3.8.3"),sQuery(id+"F0.wireOp",EDGE,"E3.9.1"),sQuery(id+"F0.wireOp",EDGE,"E3.9.2"),sQuery(id+"F0.wireOp",EDGE,"E3.9.3"),subQ0,subQ1,sQuery(id+"F0.wireOp",EDGE,"E3.10.3"),sQuery(id+"F0.wireOp",EDGE,"E3.11.1"),sQuery(id+"F0.wireOp",EDGE,"E3.11.2"),sQuery(id+"F0.wireOp",EDGE,"E3.11.3"),sQuery(id+"F0.wireOp",EDGE,"E3.12.1"),sQuery(id+"F0.wireOp",EDGE,"E3.12.2"),sQuery(id+"F0.wireOp",EDGE,"E3.12.3")])],"isStart":true})]}),makeQuery(id+"F1.opExtrude","CAP_EDGE",EDGE,{"disambiguationData":[OSD([subQ0])],"isStart":true})],"blendedInto":[]});}
            var Q26;
            {var subQ0=sQuery(id+"F0.wireOp",EDGE,"E3.9.1");var subQ1=sQuery(id+"F0.wireOp",EDGE,"E3.9.2");Q26=makeQuery(id+"F4.opChamfer","BLEND_EDGE",EDGE,{"blendedFrom":[makeQuery(id+"F3.opChamfer","BLEND_EDGE",EDGE,{"blendedFrom":[makeQuery(id+"F1.opExtrude","SWEPT_EDGE",EDGE,{"disambiguationData":[OSD([subQ0,subQ1])]}),makeQuery(id+"F1.opExtrude","CAP_FACE",FACE,{"disambiguationData":[OSD([sQuery(id+"F0.wireOp",EDGE,"E0"),sQuery(id+"F0.wireOp",EDGE,"E1"),sQuery(id+"F0.wireOp",EDGE,"E2.bottom"),sQuery(id+"F0.wireOp",EDGE,"E2.left"),sQuery(id+"F0.wireOp",EDGE,"E2.right"),sQuery(id+"F0.wireOp",EDGE,"E3.1.1"),sQuery(id+"F0.wireOp",EDGE,"E3.1.2"),sQuery(id+"F0.wireOp",EDGE,"E3.1.3"),sQuery(id+"F0.wireOp",EDGE,"E3.2.1"),sQuery(id+"F0.wireOp",EDGE,"E3.2.2"),sQuery(id+"F0.wireOp",EDGE,"E3.2.3"),sQuery(id+"F0.wireOp",EDGE,"E3.3.1"),sQuery(id+"F0.wireOp",EDGE,"E3.3.2"),sQuery(id+"F0.wireOp",EDGE,"E3.3.3"),sQuery(id+"F0.wireOp",EDGE,"E3.4.1"),sQuery(id+"F0.wireOp",EDGE,"E3.4.2"),sQuery(id+"F0.wireOp",EDGE,"E3.4.3"),sQuery(id+"F0.wireOp",EDGE,"E3.5.1"),sQuery(id+"F0.wireOp",EDGE,"E3.5.2"),sQuery(id+"F0.wireOp",EDGE,"E3.5.3"),sQuery(id+"F0.wireOp",EDGE,"E3.6.1"),sQuery(id+"F0.wireOp",EDGE,"E3.6.2"),sQuery(id+"F0.wireOp",EDGE,"E3.6.3"),sQuery(id+"F0.wireOp",EDGE,"E3.7.1"),sQuery(id+"F0.wireOp",EDGE,"E3.7.2"),sQuery(id+"F0.wireOp",EDGE,"E3.7.3"),sQuery(id+"F0.wireOp",EDGE,"E3.8.1"),sQuery(id+"F0.wireOp",EDGE,"E3.8.2"),sQuery(id+"F0.wireOp",EDGE,"E3.8.3"),subQ0,subQ1,sQuery(id+"F0.wireOp",EDGE,"E3.9.3"),sQuery(id+"F0.wireOp",EDGE,"E3.10.1"),sQuery(id+"F0.wireOp",EDGE,"E3.10.2"),sQuery(id+"F0.wireOp",EDGE,"E3.10.3"),sQuery(id+"F0.wireOp",EDGE,"E3.11.1"),sQuery(id+"F0.wireOp",EDGE,"E3.11.2"),sQuery(id+"F0.wireOp",EDGE,"E3.11.3"),sQuery(id+"F0.wireOp",EDGE,"E3.12.1"),sQuery(id+"F0.wireOp",EDGE,"E3.12.2"),sQuery(id+"F0.wireOp",EDGE,"E3.12.3")])],"isStart":true})],"blendedInto":[makeQuery(id+"F1.opExtrude","CAP_FACE",FACE,{"disambiguationData":[OSD([sQuery(id+"F0.wireOp",EDGE,"E0"),sQuery(id+"F0.wireOp",EDGE,"E1"),sQuery(id+"F0.wireOp",EDGE,"E2.bottom"),sQuery(id+"F0.wireOp",EDGE,"E2.left"),sQuery(id+"F0.wireOp",EDGE,"E2.right"),sQuery(id+"F0.wireOp",EDGE,"E3.1.1"),sQuery(id+"F0.wireOp",EDGE,"E3.1.2"),sQuery(id+"F0.wireOp",EDGE,"E3.1.3"),sQuery(id+"F0.wireOp",EDGE,"E3.2.1"),sQuery(id+"F0.wireOp",EDGE,"E3.2.2"),sQuery(id+"F0.wireOp",EDGE,"E3.2.3"),sQuery(id+"F0.wireOp",EDGE,"E3.3.1"),sQuery(id+"F0.wireOp",EDGE,"E3.3.2"),sQuery(id+"F0.wireOp",EDGE,"E3.3.3"),sQuery(id+"F0.wireOp",EDGE,"E3.4.1"),sQuery(id+"F0.wireOp",EDGE,"E3.4.2"),sQuery(id+"F0.wireOp",EDGE,"E3.4.3"),sQuery(id+"F0.wireOp",EDGE,"E3.5.1"),sQuery(id+"F0.wireOp",EDGE,"E3.5.2"),sQuery(id+"F0.wireOp",EDGE,"E3.5.3"),sQuery(id+"F0.wireOp",EDGE,"E3.6.1"),sQuery(id+"F0.wireOp",EDGE,"E3.6.2"),sQuery(id+"F0.wireOp",EDGE,"E3.6.3"),sQuery(id+"F0.wireOp",EDGE,"E3.7.1"),sQuery(id+"F0.wireOp",EDGE,"E3.7.2"),sQuery(id+"F0.wireOp",EDGE,"E3.7.3"),sQuery(id+"F0.wireOp",EDGE,"E3.8.1"),sQuery(id+"F0.wireOp",EDGE,"E3.8.2"),sQuery(id+"F0.wireOp",EDGE,"E3.8.3"),subQ0,subQ1,sQuery(id+"F0.wireOp",EDGE,"E3.9.3"),sQuery(id+"F0.wireOp",EDGE,"E3.10.1"),sQuery(id+"F0.wireOp",EDGE,"E3.10.2"),sQuery(id+"F0.wireOp",EDGE,"E3.10.3"),sQuery(id+"F0.wireOp",EDGE,"E3.11.1"),sQuery(id+"F0.wireOp",EDGE,"E3.11.2"),sQuery(id+"F0.wireOp",EDGE,"E3.11.3"),sQuery(id+"F0.wireOp",EDGE,"E3.12.1"),sQuery(id+"F0.wireOp",EDGE,"E3.12.2"),sQuery(id+"F0.wireOp",EDGE,"E3.12.3")])],"isStart":true})]}),makeQuery(id+"F1.opExtrude","CAP_EDGE",EDGE,{"disambiguationData":[OSD([subQ0])],"isStart":true})],"blendedInto":[]});}
            var Q27;
            {var subQ0=sQuery(id+"F0.wireOp",EDGE,"E3.9.3");var subQ1=sQuery(id+"F0.wireOp",EDGE,"E3.9.2");Q27=makeQuery(id+"F4.opChamfer","BLEND_EDGE",EDGE,{"blendedFrom":[makeQuery(id+"F3.opChamfer","BLEND_EDGE",EDGE,{"blendedFrom":[makeQuery(id+"F1.opExtrude","SWEPT_EDGE",EDGE,{"disambiguationData":[OSD([subQ1,subQ0])]}),makeQuery(id+"F1.opExtrude","CAP_FACE",FACE,{"disambiguationData":[OSD([sQuery(id+"F0.wireOp",EDGE,"E0"),sQuery(id+"F0.wireOp",EDGE,"E1"),sQuery(id+"F0.wireOp",EDGE,"E2.bottom"),sQuery(id+"F0.wireOp",EDGE,"E2.left"),sQuery(id+"F0.wireOp",EDGE,"E2.right"),sQuery(id+"F0.wireOp",EDGE,"E3.1.1"),sQuery(id+"F0.wireOp",EDGE,"E3.1.2"),sQuery(id+"F0.wireOp",EDGE,"E3.1.3"),sQuery(id+"F0.wireOp",EDGE,"E3.2.1"),sQuery(id+"F0.wireOp",EDGE,"E3.2.2"),sQuery(id+"F0.wireOp",EDGE,"E3.2.3"),sQuery(id+"F0.wireOp",EDGE,"E3.3.1"),sQuery(id+"F0.wireOp",EDGE,"E3.3.2"),sQuery(id+"F0.wireOp",EDGE,"E3.3.3"),sQuery(id+"F0.wireOp",EDGE,"E3.4.1"),sQuery(id+"F0.wireOp",EDGE,"E3.4.2"),sQuery(id+"F0.wireOp",EDGE,"E3.4.3"),sQuery(id+"F0.wireOp",EDGE,"E3.5.1"),sQuery(id+"F0.wireOp",EDGE,"E3.5.2"),sQuery(id+"F0.wireOp",EDGE,"E3.5.3"),sQuery(id+"F0.wireOp",EDGE,"E3.6.1"),sQuery(id+"F0.wireOp",EDGE,"E3.6.2"),sQuery(id+"F0.wireOp",EDGE,"E3.6.3"),sQuery(id+"F0.wireOp",EDGE,"E3.7.1"),sQuery(id+"F0.wireOp",EDGE,"E3.7.2"),sQuery(id+"F0.wireOp",EDGE,"E3.7.3"),sQuery(id+"F0.wireOp",EDGE,"E3.8.1"),sQuery(id+"F0.wireOp",EDGE,"E3.8.2"),sQuery(id+"F0.wireOp",EDGE,"E3.8.3"),sQuery(id+"F0.wireOp",EDGE,"E3.9.1"),subQ1,subQ0,sQuery(id+"F0.wireOp",EDGE,"E3.10.1"),sQuery(id+"F0.wireOp",EDGE,"E3.10.2"),sQuery(id+"F0.wireOp",EDGE,"E3.10.3"),sQuery(id+"F0.wireOp",EDGE,"E3.11.1"),sQuery(id+"F0.wireOp",EDGE,"E3.11.2"),sQuery(id+"F0.wireOp",EDGE,"E3.11.3"),sQuery(id+"F0.wireOp",EDGE,"E3.12.1"),sQuery(id+"F0.wireOp",EDGE,"E3.12.2"),sQuery(id+"F0.wireOp",EDGE,"E3.12.3")])],"isStart":true})],"blendedInto":[makeQuery(id+"F1.opExtrude","CAP_FACE",FACE,{"disambiguationData":[OSD([sQuery(id+"F0.wireOp",EDGE,"E0"),sQuery(id+"F0.wireOp",EDGE,"E1"),sQuery(id+"F0.wireOp",EDGE,"E2.bottom"),sQuery(id+"F0.wireOp",EDGE,"E2.left"),sQuery(id+"F0.wireOp",EDGE,"E2.right"),sQuery(id+"F0.wireOp",EDGE,"E3.1.1"),sQuery(id+"F0.wireOp",EDGE,"E3.1.2"),sQuery(id+"F0.wireOp",EDGE,"E3.1.3"),sQuery(id+"F0.wireOp",EDGE,"E3.2.1"),sQuery(id+"F0.wireOp",EDGE,"E3.2.2"),sQuery(id+"F0.wireOp",EDGE,"E3.2.3"),sQuery(id+"F0.wireOp",EDGE,"E3.3.1"),sQuery(id+"F0.wireOp",EDGE,"E3.3.2"),sQuery(id+"F0.wireOp",EDGE,"E3.3.3"),sQuery(id+"F0.wireOp",EDGE,"E3.4.1"),sQuery(id+"F0.wireOp",EDGE,"E3.4.2"),sQuery(id+"F0.wireOp",EDGE,"E3.4.3"),sQuery(id+"F0.wireOp",EDGE,"E3.5.1"),sQuery(id+"F0.wireOp",EDGE,"E3.5.2"),sQuery(id+"F0.wireOp",EDGE,"E3.5.3"),sQuery(id+"F0.wireOp",EDGE,"E3.6.1"),sQuery(id+"F0.wireOp",EDGE,"E3.6.2"),sQuery(id+"F0.wireOp",EDGE,"E3.6.3"),sQuery(id+"F0.wireOp",EDGE,"E3.7.1"),sQuery(id+"F0.wireOp",EDGE,"E3.7.2"),sQuery(id+"F0.wireOp",EDGE,"E3.7.3"),sQuery(id+"F0.wireOp",EDGE,"E3.8.1"),sQuery(id+"F0.wireOp",EDGE,"E3.8.2"),sQuery(id+"F0.wireOp",EDGE,"E3.8.3"),sQuery(id+"F0.wireOp",EDGE,"E3.9.1"),subQ1,subQ0,sQuery(id+"F0.wireOp",EDGE,"E3.10.1"),sQuery(id+"F0.wireOp",EDGE,"E3.10.2"),sQuery(id+"F0.wireOp",EDGE,"E3.10.3"),sQuery(id+"F0.wireOp",EDGE,"E3.11.1"),sQuery(id+"F0.wireOp",EDGE,"E3.11.2"),sQuery(id+"F0.wireOp",EDGE,"E3.11.3"),sQuery(id+"F0.wireOp",EDGE,"E3.12.1"),sQuery(id+"F0.wireOp",EDGE,"E3.12.2"),sQuery(id+"F0.wireOp",EDGE,"E3.12.3")])],"isStart":true})]}),makeQuery(id+"F1.opExtrude","CAP_EDGE",EDGE,{"disambiguationData":[OSD([subQ0])],"isStart":true})],"blendedInto":[]});}
            var Q28;
            {var subQ0=sQuery(id+"F0.wireOp",EDGE,"E3.9.3");Q28=makeQuery(id+"F3.opChamfer","BLEND_EDGE",EDGE,{"blendedFrom":[makeQuery(id+"F1.opExtrude","SWEPT_EDGE",EDGE,{"disambiguationData":[OSD([sQuery(id+"F0.wireOp",EDGE,"E3.9.2"),subQ0])]}),makeQuery(id+"F1.opExtrude","SWEPT_FACE",FACE,{"disambiguationData":[OSD([subQ0])]})],"blendedInto":[makeQuery(id+"F1.opExtrude","SWEPT_FACE",FACE,{"disambiguationData":[OSD([subQ0])]})]});}
            var Q29;
            {var subQ0=sQuery(id+"F0.wireOp",EDGE,"E3.9.1");Q29=makeQuery(id+"F3.opChamfer","BLEND_EDGE",EDGE,{"blendedFrom":[makeQuery(id+"F1.opExtrude","SWEPT_EDGE",EDGE,{"disambiguationData":[OSD([subQ0,sQuery(id+"F0.wireOp",EDGE,"E3.9.2")])]}),makeQuery(id+"F1.opExtrude","SWEPT_FACE",FACE,{"disambiguationData":[OSD([subQ0])]})],"blendedInto":[makeQuery(id+"F1.opExtrude","SWEPT_FACE",FACE,{"disambiguationData":[OSD([subQ0])]})]});}
            var Q30;
            {var subQ0=sQuery(id+"F0.wireOp",EDGE,"E3.10.1");Q30=makeQuery(id+"F3.opChamfer","BLEND_EDGE",EDGE,{"blendedFrom":[makeQuery(id+"F1.opExtrude","SWEPT_EDGE",EDGE,{"disambiguationData":[OSD([subQ0,sQuery(id+"F0.wireOp",EDGE,"E3.10.2")])]}),makeQuery(id+"F1.opExtrude","SWEPT_FACE",FACE,{"disambiguationData":[OSD([subQ0])]})],"blendedInto":[makeQuery(id+"F1.opExtrude","SWEPT_FACE",FACE,{"disambiguationData":[OSD([subQ0])]})]});}
            var Q31;
            {var subQ0=sQuery(id+"F0.wireOp",EDGE,"E3.8.3");Q31=makeQuery(id+"F3.opChamfer","BLEND_EDGE",EDGE,{"blendedFrom":[makeQuery(id+"F1.opExtrude","SWEPT_EDGE",EDGE,{"disambiguationData":[OSD([sQuery(id+"F0.wireOp",EDGE,"E3.8.2"),subQ0])]}),makeQuery(id+"F1.opExtrude","SWEPT_FACE",FACE,{"disambiguationData":[OSD([subQ0])]})],"blendedInto":[makeQuery(id+"F1.opExtrude","SWEPT_FACE",FACE,{"disambiguationData":[OSD([subQ0])]})]});}
            var Q32;
            {var subQ0=sQuery(id+"F0.wireOp",EDGE,"E3.8.3");var subQ1=sQuery(id+"F0.wireOp",EDGE,"E3.8.2");Q32=makeQuery(id+"F4.opChamfer","BLEND_EDGE",EDGE,{"blendedFrom":[makeQuery(id+"F3.opChamfer","BLEND_EDGE",EDGE,{"blendedFrom":[makeQuery(id+"F1.opExtrude","SWEPT_EDGE",EDGE,{"disambiguationData":[OSD([subQ1,subQ0])]}),makeQuery(id+"F1.opExtrude","CAP_FACE",FACE,{"disambiguationData":[OSD([sQuery(id+"F0.wireOp",EDGE,"E0"),sQuery(id+"F0.wireOp",EDGE,"E1"),sQuery(id+"F0.wireOp",EDGE,"E2.bottom"),sQuery(id+"F0.wireOp",EDGE,"E2.left"),sQuery(id+"F0.wireOp",EDGE,"E2.right"),sQuery(id+"F0.wireOp",EDGE,"E3.1.1"),sQuery(id+"F0.wireOp",EDGE,"E3.1.2"),sQuery(id+"F0.wireOp",EDGE,"E3.1.3"),sQuery(id+"F0.wireOp",EDGE,"E3.2.1"),sQuery(id+"F0.wireOp",EDGE,"E3.2.2"),sQuery(id+"F0.wireOp",EDGE,"E3.2.3"),sQuery(id+"F0.wireOp",EDGE,"E3.3.1"),sQuery(id+"F0.wireOp",EDGE,"E3.3.2"),sQuery(id+"F0.wireOp",EDGE,"E3.3.3"),sQuery(id+"F0.wireOp",EDGE,"E3.4.1"),sQuery(id+"F0.wireOp",EDGE,"E3.4.2"),sQuery(id+"F0.wireOp",EDGE,"E3.4.3"),sQuery(id+"F0.wireOp",EDGE,"E3.5.1"),sQuery(id+"F0.wireOp",EDGE,"E3.5.2"),sQuery(id+"F0.wireOp",EDGE,"E3.5.3"),sQuery(id+"F0.wireOp",EDGE,"E3.6.1"),sQuery(id+"F0.wireOp",EDGE,"E3.6.2"),sQuery(id+"F0.wireOp",EDGE,"E3.6.3"),sQuery(id+"F0.wireOp",EDGE,"E3.7.1"),sQuery(id+"F0.wireOp",EDGE,"E3.7.2"),sQuery(id+"F0.wireOp",EDGE,"E3.7.3"),sQuery(id+"F0.wireOp",EDGE,"E3.8.1"),subQ1,subQ0,sQuery(id+"F0.wireOp",EDGE,"E3.9.1"),sQuery(id+"F0.wireOp",EDGE,"E3.9.2"),sQuery(id+"F0.wireOp",EDGE,"E3.9.3"),sQuery(id+"F0.wireOp",EDGE,"E3.10.1"),sQuery(id+"F0.wireOp",EDGE,"E3.10.2"),sQuery(id+"F0.wireOp",EDGE,"E3.10.3"),sQuery(id+"F0.wireOp",EDGE,"E3.11.1"),sQuery(id+"F0.wireOp",EDGE,"E3.11.2"),sQuery(id+"F0.wireOp",EDGE,"E3.11.3"),sQuery(id+"F0.wireOp",EDGE,"E3.12.1"),sQuery(id+"F0.wireOp",EDGE,"E3.12.2"),sQuery(id+"F0.wireOp",EDGE,"E3.12.3")])],"isStart":true})],"blendedInto":[makeQuery(id+"F1.opExtrude","CAP_FACE",FACE,{"disambiguationData":[OSD([sQuery(id+"F0.wireOp",EDGE,"E0"),sQuery(id+"F0.wireOp",EDGE,"E1"),sQuery(id+"F0.wireOp",EDGE,"E2.bottom"),sQuery(id+"F0.wireOp",EDGE,"E2.left"),sQuery(id+"F0.wireOp",EDGE,"E2.right"),sQuery(id+"F0.wireOp",EDGE,"E3.1.1"),sQuery(id+"F0.wireOp",EDGE,"E3.1.2"),sQuery(id+"F0.wireOp",EDGE,"E3.1.3"),sQuery(id+"F0.wireOp",EDGE,"E3.2.1"),sQuery(id+"F0.wireOp",EDGE,"E3.2.2"),sQuery(id+"F0.wireOp",EDGE,"E3.2.3"),sQuery(id+"F0.wireOp",EDGE,"E3.3.1"),sQuery(id+"F0.wireOp",EDGE,"E3.3.2"),sQuery(id+"F0.wireOp",EDGE,"E3.3.3"),sQuery(id+"F0.wireOp",EDGE,"E3.4.1"),sQuery(id+"F0.wireOp",EDGE,"E3.4.2"),sQuery(id+"F0.wireOp",EDGE,"E3.4.3"),sQuery(id+"F0.wireOp",EDGE,"E3.5.1"),sQuery(id+"F0.wireOp",EDGE,"E3.5.2"),sQuery(id+"F0.wireOp",EDGE,"E3.5.3"),sQuery(id+"F0.wireOp",EDGE,"E3.6.1"),sQuery(id+"F0.wireOp",EDGE,"E3.6.2"),sQuery(id+"F0.wireOp",EDGE,"E3.6.3"),sQuery(id+"F0.wireOp",EDGE,"E3.7.1"),sQuery(id+"F0.wireOp",EDGE,"E3.7.2"),sQuery(id+"F0.wireOp",EDGE,"E3.7.3"),sQuery(id+"F0.wireOp",EDGE,"E3.8.1"),subQ1,subQ0,sQuery(id+"F0.wireOp",EDGE,"E3.9.1"),sQuery(id+"F0.wireOp",EDGE,"E3.9.2"),sQuery(id+"F0.wireOp",EDGE,"E3.9.3"),sQuery(id+"F0.wireOp",EDGE,"E3.10.1"),sQuery(id+"F0.wireOp",EDGE,"E3.10.2"),sQuery(id+"F0.wireOp",EDGE,"E3.10.3"),sQuery(id+"F0.wireOp",EDGE,"E3.11.1"),sQuery(id+"F0.wireOp",EDGE,"E3.11.2"),sQuery(id+"F0.wireOp",EDGE,"E3.11.3"),sQuery(id+"F0.wireOp",EDGE,"E3.12.1"),sQuery(id+"F0.wireOp",EDGE,"E3.12.2"),sQuery(id+"F0.wireOp",EDGE,"E3.12.3")])],"isStart":true})]}),makeQuery(id+"F1.opExtrude","CAP_EDGE",EDGE,{"disambiguationData":[OSD([subQ0])],"isStart":true})],"blendedInto":[]});}
            var Q33;
            {var subQ0=sQuery(id+"F0.wireOp",EDGE,"E3.8.1");var subQ1=sQuery(id+"F0.wireOp",EDGE,"E3.8.2");Q33=makeQuery(id+"F4.opChamfer","BLEND_EDGE",EDGE,{"blendedFrom":[makeQuery(id+"F3.opChamfer","BLEND_EDGE",EDGE,{"blendedFrom":[makeQuery(id+"F1.opExtrude","SWEPT_EDGE",EDGE,{"disambiguationData":[OSD([subQ0,subQ1])]}),makeQuery(id+"F1.opExtrude","CAP_FACE",FACE,{"disambiguationData":[OSD([sQuery(id+"F0.wireOp",EDGE,"E0"),sQuery(id+"F0.wireOp",EDGE,"E1"),sQuery(id+"F0.wireOp",EDGE,"E2.bottom"),sQuery(id+"F0.wireOp",EDGE,"E2.left"),sQuery(id+"F0.wireOp",EDGE,"E2.right"),sQuery(id+"F0.wireOp",EDGE,"E3.1.1"),sQuery(id+"F0.wireOp",EDGE,"E3.1.2"),sQuery(id+"F0.wireOp",EDGE,"E3.1.3"),sQuery(id+"F0.wireOp",EDGE,"E3.2.1"),sQuery(id+"F0.wireOp",EDGE,"E3.2.2"),sQuery(id+"F0.wireOp",EDGE,"E3.2.3"),sQuery(id+"F0.wireOp",EDGE,"E3.3.1"),sQuery(id+"F0.wireOp",EDGE,"E3.3.2"),sQuery(id+"F0.wireOp",EDGE,"E3.3.3"),sQuery(id+"F0.wireOp",EDGE,"E3.4.1"),sQuery(id+"F0.wireOp",EDGE,"E3.4.2"),sQuery(id+"F0.wireOp",EDGE,"E3.4.3"),sQuery(id+"F0.wireOp",EDGE,"E3.5.1"),sQuery(id+"F0.wireOp",EDGE,"E3.5.2"),sQuery(id+"F0.wireOp",EDGE,"E3.5.3"),sQuery(id+"F0.wireOp",EDGE,"E3.6.1"),sQuery(id+"F0.wireOp",EDGE,"E3.6.2"),sQuery(id+"F0.wireOp",EDGE,"E3.6.3"),sQuery(id+"F0.wireOp",EDGE,"E3.7.1"),sQuery(id+"F0.wireOp",EDGE,"E3.7.2"),sQuery(id+"F0.wireOp",EDGE,"E3.7.3"),subQ0,subQ1,sQuery(id+"F0.wireOp",EDGE,"E3.8.3"),sQuery(id+"F0.wireOp",EDGE,"E3.9.1"),sQuery(id+"F0.wireOp",EDGE,"E3.9.2"),sQuery(id+"F0.wireOp",EDGE,"E3.9.3"),sQuery(id+"F0.wireOp",EDGE,"E3.10.1"),sQuery(id+"F0.wireOp",EDGE,"E3.10.2"),sQuery(id+"F0.wireOp",EDGE,"E3.10.3"),sQuery(id+"F0.wireOp",EDGE,"E3.11.1"),sQuery(id+"F0.wireOp",EDGE,"E3.11.2"),sQuery(id+"F0.wireOp",EDGE,"E3.11.3"),sQuery(id+"F0.wireOp",EDGE,"E3.12.1"),sQuery(id+"F0.wireOp",EDGE,"E3.12.2"),sQuery(id+"F0.wireOp",EDGE,"E3.12.3")])],"isStart":true})],"blendedInto":[makeQuery(id+"F1.opExtrude","CAP_FACE",FACE,{"disambiguationData":[OSD([sQuery(id+"F0.wireOp",EDGE,"E0"),sQuery(id+"F0.wireOp",EDGE,"E1"),sQuery(id+"F0.wireOp",EDGE,"E2.bottom"),sQuery(id+"F0.wireOp",EDGE,"E2.left"),sQuery(id+"F0.wireOp",EDGE,"E2.right"),sQuery(id+"F0.wireOp",EDGE,"E3.1.1"),sQuery(id+"F0.wireOp",EDGE,"E3.1.2"),sQuery(id+"F0.wireOp",EDGE,"E3.1.3"),sQuery(id+"F0.wireOp",EDGE,"E3.2.1"),sQuery(id+"F0.wireOp",EDGE,"E3.2.2"),sQuery(id+"F0.wireOp",EDGE,"E3.2.3"),sQuery(id+"F0.wireOp",EDGE,"E3.3.1"),sQuery(id+"F0.wireOp",EDGE,"E3.3.2"),sQuery(id+"F0.wireOp",EDGE,"E3.3.3"),sQuery(id+"F0.wireOp",EDGE,"E3.4.1"),sQuery(id+"F0.wireOp",EDGE,"E3.4.2"),sQuery(id+"F0.wireOp",EDGE,"E3.4.3"),sQuery(id+"F0.wireOp",EDGE,"E3.5.1"),sQuery(id+"F0.wireOp",EDGE,"E3.5.2"),sQuery(id+"F0.wireOp",EDGE,"E3.5.3"),sQuery(id+"F0.wireOp",EDGE,"E3.6.1"),sQuery(id+"F0.wireOp",EDGE,"E3.6.2"),sQuery(id+"F0.wireOp",EDGE,"E3.6.3"),sQuery(id+"F0.wireOp",EDGE,"E3.7.1"),sQuery(id+"F0.wireOp",EDGE,"E3.7.2"),sQuery(id+"F0.wireOp",EDGE,"E3.7.3"),subQ0,subQ1,sQuery(id+"F0.wireOp",EDGE,"E3.8.3"),sQuery(id+"F0.wireOp",EDGE,"E3.9.1"),sQuery(id+"F0.wireOp",EDGE,"E3.9.2"),sQuery(id+"F0.wireOp",EDGE,"E3.9.3"),sQuery(id+"F0.wireOp",EDGE,"E3.10.1"),sQuery(id+"F0.wireOp",EDGE,"E3.10.2"),sQuery(id+"F0.wireOp",EDGE,"E3.10.3"),sQuery(id+"F0.wireOp",EDGE,"E3.11.1"),sQuery(id+"F0.wireOp",EDGE,"E3.11.2"),sQuery(id+"F0.wireOp",EDGE,"E3.11.3"),sQuery(id+"F0.wireOp",EDGE,"E3.12.1"),sQuery(id+"F0.wireOp",EDGE,"E3.12.2"),sQuery(id+"F0.wireOp",EDGE,"E3.12.3")])],"isStart":true})]}),makeQuery(id+"F1.opExtrude","CAP_EDGE",EDGE,{"disambiguationData":[OSD([subQ0])],"isStart":true})],"blendedInto":[]});}
            var Q34;
            {var subQ0=sQuery(id+"F0.wireOp",EDGE,"E3.8.1");Q34=makeQuery(id+"F3.opChamfer","BLEND_EDGE",EDGE,{"blendedFrom":[makeQuery(id+"F1.opExtrude","SWEPT_EDGE",EDGE,{"disambiguationData":[OSD([subQ0,sQuery(id+"F0.wireOp",EDGE,"E3.8.2")])]}),makeQuery(id+"F1.opExtrude","SWEPT_FACE",FACE,{"disambiguationData":[OSD([subQ0])]})],"blendedInto":[makeQuery(id+"F1.opExtrude","SWEPT_FACE",FACE,{"disambiguationData":[OSD([subQ0])]})]});}
            var Q35;
            {var subQ0=sQuery(id+"F0.wireOp",EDGE,"E3.12.3");var subQ1=sQuery(id+"F0.wireOp",EDGE,"E3.12.2");Q35=makeQuery(id+"F4.opChamfer","BLEND_EDGE",EDGE,{"blendedFrom":[makeQuery(id+"F3.opChamfer","BLEND_EDGE",EDGE,{"blendedFrom":[makeQuery(id+"F1.opExtrude","SWEPT_EDGE",EDGE,{"disambiguationData":[OSD([subQ1,subQ0])]}),makeQuery(id+"F1.opExtrude","CAP_FACE",FACE,{"disambiguationData":[OSD([sQuery(id+"F0.wireOp",EDGE,"E0"),sQuery(id+"F0.wireOp",EDGE,"E1"),sQuery(id+"F0.wireOp",EDGE,"E2.bottom"),sQuery(id+"F0.wireOp",EDGE,"E2.left"),sQuery(id+"F0.wireOp",EDGE,"E2.right"),sQuery(id+"F0.wireOp",EDGE,"E3.1.1"),sQuery(id+"F0.wireOp",EDGE,"E3.1.2"),sQuery(id+"F0.wireOp",EDGE,"E3.1.3"),sQuery(id+"F0.wireOp",EDGE,"E3.2.1"),sQuery(id+"F0.wireOp",EDGE,"E3.2.2"),sQuery(id+"F0.wireOp",EDGE,"E3.2.3"),sQuery(id+"F0.wireOp",EDGE,"E3.3.1"),sQuery(id+"F0.wireOp",EDGE,"E3.3.2"),sQuery(id+"F0.wireOp",EDGE,"E3.3.3"),sQuery(id+"F0.wireOp",EDGE,"E3.4.1"),sQuery(id+"F0.wireOp",EDGE,"E3.4.2"),sQuery(id+"F0.wireOp",EDGE,"E3.4.3"),sQuery(id+"F0.wireOp",EDGE,"E3.5.1"),sQuery(id+"F0.wireOp",EDGE,"E3.5.2"),sQuery(id+"F0.wireOp",EDGE,"E3.5.3"),sQuery(id+"F0.wireOp",EDGE,"E3.6.1"),sQuery(id+"F0.wireOp",EDGE,"E3.6.2"),sQuery(id+"F0.wireOp",EDGE,"E3.6.3"),sQuery(id+"F0.wireOp",EDGE,"E3.7.1"),sQuery(id+"F0.wireOp",EDGE,"E3.7.2"),sQuery(id+"F0.wireOp",EDGE,"E3.7.3"),sQuery(id+"F0.wireOp",EDGE,"E3.8.1"),sQuery(id+"F0.wireOp",EDGE,"E3.8.2"),sQuery(id+"F0.wireOp",EDGE,"E3.8.3"),sQuery(id+"F0.wireOp",EDGE,"E3.9.1"),sQuery(id+"F0.wireOp",EDGE,"E3.9.2"),sQuery(id+"F0.wireOp",EDGE,"E3.9.3"),sQuery(id+"F0.wireOp",EDGE,"E3.10.1"),sQuery(id+"F0.wireOp",EDGE,"E3.10.2"),sQuery(id+"F0.wireOp",EDGE,"E3.10.3"),sQuery(id+"F0.wireOp",EDGE,"E3.11.1"),sQuery(id+"F0.wireOp",EDGE,"E3.11.2"),sQuery(id+"F0.wireOp",EDGE,"E3.11.3"),sQuery(id+"F0.wireOp",EDGE,"E3.12.1"),subQ1,subQ0])],"isStart":false})],"blendedInto":[makeQuery(id+"F1.opExtrude","CAP_FACE",FACE,{"disambiguationData":[OSD([sQuery(id+"F0.wireOp",EDGE,"E0"),sQuery(id+"F0.wireOp",EDGE,"E1"),sQuery(id+"F0.wireOp",EDGE,"E2.bottom"),sQuery(id+"F0.wireOp",EDGE,"E2.left"),sQuery(id+"F0.wireOp",EDGE,"E2.right"),sQuery(id+"F0.wireOp",EDGE,"E3.1.1"),sQuery(id+"F0.wireOp",EDGE,"E3.1.2"),sQuery(id+"F0.wireOp",EDGE,"E3.1.3"),sQuery(id+"F0.wireOp",EDGE,"E3.2.1"),sQuery(id+"F0.wireOp",EDGE,"E3.2.2"),sQuery(id+"F0.wireOp",EDGE,"E3.2.3"),sQuery(id+"F0.wireOp",EDGE,"E3.3.1"),sQuery(id+"F0.wireOp",EDGE,"E3.3.2"),sQuery(id+"F0.wireOp",EDGE,"E3.3.3"),sQuery(id+"F0.wireOp",EDGE,"E3.4.1"),sQuery(id+"F0.wireOp",EDGE,"E3.4.2"),sQuery(id+"F0.wireOp",EDGE,"E3.4.3"),sQuery(id+"F0.wireOp",EDGE,"E3.5.1"),sQuery(id+"F0.wireOp",EDGE,"E3.5.2"),sQuery(id+"F0.wireOp",EDGE,"E3.5.3"),sQuery(id+"F0.wireOp",EDGE,"E3.6.1"),sQuery(id+"F0.wireOp",EDGE,"E3.6.2"),sQuery(id+"F0.wireOp",EDGE,"E3.6.3"),sQuery(id+"F0.wireOp",EDGE,"E3.7.1"),sQuery(id+"F0.wireOp",EDGE,"E3.7.2"),sQuery(id+"F0.wireOp",EDGE,"E3.7.3"),sQuery(id+"F0.wireOp",EDGE,"E3.8.1"),sQuery(id+"F0.wireOp",EDGE,"E3.8.2"),sQuery(id+"F0.wireOp",EDGE,"E3.8.3"),sQuery(id+"F0.wireOp",EDGE,"E3.9.1"),sQuery(id+"F0.wireOp",EDGE,"E3.9.2"),sQuery(id+"F0.wireOp",EDGE,"E3.9.3"),sQuery(id+"F0.wireOp",EDGE,"E3.10.1"),sQuery(id+"F0.wireOp",EDGE,"E3.10.2"),sQuery(id+"F0.wireOp",EDGE,"E3.10.3"),sQuery(id+"F0.wireOp",EDGE,"E3.11.1"),sQuery(id+"F0.wireOp",EDGE,"E3.11.2"),sQuery(id+"F0.wireOp",EDGE,"E3.11.3"),sQuery(id+"F0.wireOp",EDGE,"E3.12.1"),subQ1,subQ0])],"isStart":false})]}),makeQuery(id+"F1.opExtrude","CAP_EDGE",EDGE,{"disambiguationData":[OSD([subQ0])],"isStart":false})],"blendedInto":[]});}
            var Q36;
            {var subQ0=sQuery(id+"F0.wireOp",EDGE,"E3.11.3");var subQ1=sQuery(id+"F0.wireOp",EDGE,"E3.11.2");Q36=makeQuery(id+"F4.opChamfer","BLEND_EDGE",EDGE,{"blendedFrom":[makeQuery(id+"F3.opChamfer","BLEND_EDGE",EDGE,{"blendedFrom":[makeQuery(id+"F1.opExtrude","SWEPT_EDGE",EDGE,{"disambiguationData":[OSD([subQ1,subQ0])]}),makeQuery(id+"F1.opExtrude","CAP_FACE",FACE,{"disambiguationData":[OSD([sQuery(id+"F0.wireOp",EDGE,"E0"),sQuery(id+"F0.wireOp",EDGE,"E1"),sQuery(id+"F0.wireOp",EDGE,"E2.bottom"),sQuery(id+"F0.wireOp",EDGE,"E2.left"),sQuery(id+"F0.wireOp",EDGE,"E2.right"),sQuery(id+"F0.wireOp",EDGE,"E3.1.1"),sQuery(id+"F0.wireOp",EDGE,"E3.1.2"),sQuery(id+"F0.wireOp",EDGE,"E3.1.3"),sQuery(id+"F0.wireOp",EDGE,"E3.2.1"),sQuery(id+"F0.wireOp",EDGE,"E3.2.2"),sQuery(id+"F0.wireOp",EDGE,"E3.2.3"),sQuery(id+"F0.wireOp",EDGE,"E3.3.1"),sQuery(id+"F0.wireOp",EDGE,"E3.3.2"),sQuery(id+"F0.wireOp",EDGE,"E3.3.3"),sQuery(id+"F0.wireOp",EDGE,"E3.4.1"),sQuery(id+"F0.wireOp",EDGE,"E3.4.2"),sQuery(id+"F0.wireOp",EDGE,"E3.4.3"),sQuery(id+"F0.wireOp",EDGE,"E3.5.1"),sQuery(id+"F0.wireOp",EDGE,"E3.5.2"),sQuery(id+"F0.wireOp",EDGE,"E3.5.3"),sQuery(id+"F0.wireOp",EDGE,"E3.6.1"),sQuery(id+"F0.wireOp",EDGE,"E3.6.2"),sQuery(id+"F0.wireOp",EDGE,"E3.6.3"),sQuery(id+"F0.wireOp",EDGE,"E3.7.1"),sQuery(id+"F0.wireOp",EDGE,"E3.7.2"),sQuery(id+"F0.wireOp",EDGE,"E3.7.3"),sQuery(id+"F0.wireOp",EDGE,"E3.8.1"),sQuery(id+"F0.wireOp",EDGE,"E3.8.2"),sQuery(id+"F0.wireOp",EDGE,"E3.8.3"),sQuery(id+"F0.wireOp",EDGE,"E3.9.1"),sQuery(id+"F0.wireOp",EDGE,"E3.9.2"),sQuery(id+"F0.wireOp",EDGE,"E3.9.3"),sQuery(id+"F0.wireOp",EDGE,"E3.10.1"),sQuery(id+"F0.wireOp",EDGE,"E3.10.2"),sQuery(id+"F0.wireOp",EDGE,"E3.10.3"),sQuery(id+"F0.wireOp",EDGE,"E3.11.1"),subQ1,subQ0,sQuery(id+"F0.wireOp",EDGE,"E3.12.1"),sQuery(id+"F0.wireOp",EDGE,"E3.12.2"),sQuery(id+"F0.wireOp",EDGE,"E3.12.3")])],"isStart":false})],"blendedInto":[makeQuery(id+"F1.opExtrude","CAP_FACE",FACE,{"disambiguationData":[OSD([sQuery(id+"F0.wireOp",EDGE,"E0"),sQuery(id+"F0.wireOp",EDGE,"E1"),sQuery(id+"F0.wireOp",EDGE,"E2.bottom"),sQuery(id+"F0.wireOp",EDGE,"E2.left"),sQuery(id+"F0.wireOp",EDGE,"E2.right"),sQuery(id+"F0.wireOp",EDGE,"E3.1.1"),sQuery(id+"F0.wireOp",EDGE,"E3.1.2"),sQuery(id+"F0.wireOp",EDGE,"E3.1.3"),sQuery(id+"F0.wireOp",EDGE,"E3.2.1"),sQuery(id+"F0.wireOp",EDGE,"E3.2.2"),sQuery(id+"F0.wireOp",EDGE,"E3.2.3"),sQuery(id+"F0.wireOp",EDGE,"E3.3.1"),sQuery(id+"F0.wireOp",EDGE,"E3.3.2"),sQuery(id+"F0.wireOp",EDGE,"E3.3.3"),sQuery(id+"F0.wireOp",EDGE,"E3.4.1"),sQuery(id+"F0.wireOp",EDGE,"E3.4.2"),sQuery(id+"F0.wireOp",EDGE,"E3.4.3"),sQuery(id+"F0.wireOp",EDGE,"E3.5.1"),sQuery(id+"F0.wireOp",EDGE,"E3.5.2"),sQuery(id+"F0.wireOp",EDGE,"E3.5.3"),sQuery(id+"F0.wireOp",EDGE,"E3.6.1"),sQuery(id+"F0.wireOp",EDGE,"E3.6.2"),sQuery(id+"F0.wireOp",EDGE,"E3.6.3"),sQuery(id+"F0.wireOp",EDGE,"E3.7.1"),sQuery(id+"F0.wireOp",EDGE,"E3.7.2"),sQuery(id+"F0.wireOp",EDGE,"E3.7.3"),sQuery(id+"F0.wireOp",EDGE,"E3.8.1"),sQuery(id+"F0.wireOp",EDGE,"E3.8.2"),sQuery(id+"F0.wireOp",EDGE,"E3.8.3"),sQuery(id+"F0.wireOp",EDGE,"E3.9.1"),sQuery(id+"F0.wireOp",EDGE,"E3.9.2"),sQuery(id+"F0.wireOp",EDGE,"E3.9.3"),sQuery(id+"F0.wireOp",EDGE,"E3.10.1"),sQuery(id+"F0.wireOp",EDGE,"E3.10.2"),sQuery(id+"F0.wireOp",EDGE,"E3.10.3"),sQuery(id+"F0.wireOp",EDGE,"E3.11.1"),subQ1,subQ0,sQuery(id+"F0.wireOp",EDGE,"E3.12.1"),sQuery(id+"F0.wireOp",EDGE,"E3.12.2"),sQuery(id+"F0.wireOp",EDGE,"E3.12.3")])],"isStart":false})]}),makeQuery(id+"F1.opExtrude","CAP_EDGE",EDGE,{"disambiguationData":[OSD([subQ0])],"isStart":false})],"blendedInto":[]});}
            var Q37;
            {var subQ0=sQuery(id+"F0.wireOp",EDGE,"E3.10.3");var subQ1=sQuery(id+"F0.wireOp",EDGE,"E3.10.2");Q37=makeQuery(id+"F4.opChamfer","BLEND_EDGE",EDGE,{"blendedFrom":[makeQuery(id+"F3.opChamfer","BLEND_EDGE",EDGE,{"blendedFrom":[makeQuery(id+"F1.opExtrude","SWEPT_EDGE",EDGE,{"disambiguationData":[OSD([subQ1,subQ0])]}),makeQuery(id+"F1.opExtrude","CAP_FACE",FACE,{"disambiguationData":[OSD([sQuery(id+"F0.wireOp",EDGE,"E0"),sQuery(id+"F0.wireOp",EDGE,"E1"),sQuery(id+"F0.wireOp",EDGE,"E2.bottom"),sQuery(id+"F0.wireOp",EDGE,"E2.left"),sQuery(id+"F0.wireOp",EDGE,"E2.right"),sQuery(id+"F0.wireOp",EDGE,"E3.1.1"),sQuery(id+"F0.wireOp",EDGE,"E3.1.2"),sQuery(id+"F0.wireOp",EDGE,"E3.1.3"),sQuery(id+"F0.wireOp",EDGE,"E3.2.1"),sQuery(id+"F0.wireOp",EDGE,"E3.2.2"),sQuery(id+"F0.wireOp",EDGE,"E3.2.3"),sQuery(id+"F0.wireOp",EDGE,"E3.3.1"),sQuery(id+"F0.wireOp",EDGE,"E3.3.2"),sQuery(id+"F0.wireOp",EDGE,"E3.3.3"),sQuery(id+"F0.wireOp",EDGE,"E3.4.1"),sQuery(id+"F0.wireOp",EDGE,"E3.4.2"),sQuery(id+"F0.wireOp",EDGE,"E3.4.3"),sQuery(id+"F0.wireOp",EDGE,"E3.5.1"),sQuery(id+"F0.wireOp",EDGE,"E3.5.2"),sQuery(id+"F0.wireOp",EDGE,"E3.5.3"),sQuery(id+"F0.wireOp",EDGE,"E3.6.1"),sQuery(id+"F0.wireOp",EDGE,"E3.6.2"),sQuery(id+"F0.wireOp",EDGE,"E3.6.3"),sQuery(id+"F0.wireOp",EDGE,"E3.7.1"),sQuery(id+"F0.wireOp",EDGE,"E3.7.2"),sQuery(id+"F0.wireOp",EDGE,"E3.7.3"),sQuery(id+"F0.wireOp",EDGE,"E3.8.1"),sQuery(id+"F0.wireOp",EDGE,"E3.8.2"),sQuery(id+"F0.wireOp",EDGE,"E3.8.3"),sQuery(id+"F0.wireOp",EDGE,"E3.9.1"),sQuery(id+"F0.wireOp",EDGE,"E3.9.2"),sQuery(id+"F0.wireOp",EDGE,"E3.9.3"),sQuery(id+"F0.wireOp",EDGE,"E3.10.1"),subQ1,subQ0,sQuery(id+"F0.wireOp",EDGE,"E3.11.1"),sQuery(id+"F0.wireOp",EDGE,"E3.11.2"),sQuery(id+"F0.wireOp",EDGE,"E3.11.3"),sQuery(id+"F0.wireOp",EDGE,"E3.12.1"),sQuery(id+"F0.wireOp",EDGE,"E3.12.2"),sQuery(id+"F0.wireOp",EDGE,"E3.12.3")])],"isStart":false})],"blendedInto":[makeQuery(id+"F1.opExtrude","CAP_FACE",FACE,{"disambiguationData":[OSD([sQuery(id+"F0.wireOp",EDGE,"E0"),sQuery(id+"F0.wireOp",EDGE,"E1"),sQuery(id+"F0.wireOp",EDGE,"E2.bottom"),sQuery(id+"F0.wireOp",EDGE,"E2.left"),sQuery(id+"F0.wireOp",EDGE,"E2.right"),sQuery(id+"F0.wireOp",EDGE,"E3.1.1"),sQuery(id+"F0.wireOp",EDGE,"E3.1.2"),sQuery(id+"F0.wireOp",EDGE,"E3.1.3"),sQuery(id+"F0.wireOp",EDGE,"E3.2.1"),sQuery(id+"F0.wireOp",EDGE,"E3.2.2"),sQuery(id+"F0.wireOp",EDGE,"E3.2.3"),sQuery(id+"F0.wireOp",EDGE,"E3.3.1"),sQuery(id+"F0.wireOp",EDGE,"E3.3.2"),sQuery(id+"F0.wireOp",EDGE,"E3.3.3"),sQuery(id+"F0.wireOp",EDGE,"E3.4.1"),sQuery(id+"F0.wireOp",EDGE,"E3.4.2"),sQuery(id+"F0.wireOp",EDGE,"E3.4.3"),sQuery(id+"F0.wireOp",EDGE,"E3.5.1"),sQuery(id+"F0.wireOp",EDGE,"E3.5.2"),sQuery(id+"F0.wireOp",EDGE,"E3.5.3"),sQuery(id+"F0.wireOp",EDGE,"E3.6.1"),sQuery(id+"F0.wireOp",EDGE,"E3.6.2"),sQuery(id+"F0.wireOp",EDGE,"E3.6.3"),sQuery(id+"F0.wireOp",EDGE,"E3.7.1"),sQuery(id+"F0.wireOp",EDGE,"E3.7.2"),sQuery(id+"F0.wireOp",EDGE,"E3.7.3"),sQuery(id+"F0.wireOp",EDGE,"E3.8.1"),sQuery(id+"F0.wireOp",EDGE,"E3.8.2"),sQuery(id+"F0.wireOp",EDGE,"E3.8.3"),sQuery(id+"F0.wireOp",EDGE,"E3.9.1"),sQuery(id+"F0.wireOp",EDGE,"E3.9.2"),sQuery(id+"F0.wireOp",EDGE,"E3.9.3"),sQuery(id+"F0.wireOp",EDGE,"E3.10.1"),subQ1,subQ0,sQuery(id+"F0.wireOp",EDGE,"E3.11.1"),sQuery(id+"F0.wireOp",EDGE,"E3.11.2"),sQuery(id+"F0.wireOp",EDGE,"E3.11.3"),sQuery(id+"F0.wireOp",EDGE,"E3.12.1"),sQuery(id+"F0.wireOp",EDGE,"E3.12.2"),sQuery(id+"F0.wireOp",EDGE,"E3.12.3")])],"isStart":false})]}),makeQuery(id+"F1.opExtrude","CAP_EDGE",EDGE,{"disambiguationData":[OSD([subQ0])],"isStart":false})],"blendedInto":[]});}
            var Q38;
            {var subQ0=sQuery(id+"F0.wireOp",EDGE,"E3.9.3");var subQ1=sQuery(id+"F0.wireOp",EDGE,"E3.9.2");Q38=makeQuery(id+"F4.opChamfer","BLEND_EDGE",EDGE,{"blendedFrom":[makeQuery(id+"F3.opChamfer","BLEND_EDGE",EDGE,{"blendedFrom":[makeQuery(id+"F1.opExtrude","SWEPT_EDGE",EDGE,{"disambiguationData":[OSD([subQ1,subQ0])]}),makeQuery(id+"F1.opExtrude","CAP_FACE",FACE,{"disambiguationData":[OSD([sQuery(id+"F0.wireOp",EDGE,"E0"),sQuery(id+"F0.wireOp",EDGE,"E1"),sQuery(id+"F0.wireOp",EDGE,"E2.bottom"),sQuery(id+"F0.wireOp",EDGE,"E2.left"),sQuery(id+"F0.wireOp",EDGE,"E2.right"),sQuery(id+"F0.wireOp",EDGE,"E3.1.1"),sQuery(id+"F0.wireOp",EDGE,"E3.1.2"),sQuery(id+"F0.wireOp",EDGE,"E3.1.3"),sQuery(id+"F0.wireOp",EDGE,"E3.2.1"),sQuery(id+"F0.wireOp",EDGE,"E3.2.2"),sQuery(id+"F0.wireOp",EDGE,"E3.2.3"),sQuery(id+"F0.wireOp",EDGE,"E3.3.1"),sQuery(id+"F0.wireOp",EDGE,"E3.3.2"),sQuery(id+"F0.wireOp",EDGE,"E3.3.3"),sQuery(id+"F0.wireOp",EDGE,"E3.4.1"),sQuery(id+"F0.wireOp",EDGE,"E3.4.2"),sQuery(id+"F0.wireOp",EDGE,"E3.4.3"),sQuery(id+"F0.wireOp",EDGE,"E3.5.1"),sQuery(id+"F0.wireOp",EDGE,"E3.5.2"),sQuery(id+"F0.wireOp",EDGE,"E3.5.3"),sQuery(id+"F0.wireOp",EDGE,"E3.6.1"),sQuery(id+"F0.wireOp",EDGE,"E3.6.2"),sQuery(id+"F0.wireOp",EDGE,"E3.6.3"),sQuery(id+"F0.wireOp",EDGE,"E3.7.1"),sQuery(id+"F0.wireOp",EDGE,"E3.7.2"),sQuery(id+"F0.wireOp",EDGE,"E3.7.3"),sQuery(id+"F0.wireOp",EDGE,"E3.8.1"),sQuery(id+"F0.wireOp",EDGE,"E3.8.2"),sQuery(id+"F0.wireOp",EDGE,"E3.8.3"),sQuery(id+"F0.wireOp",EDGE,"E3.9.1"),subQ1,subQ0,sQuery(id+"F0.wireOp",EDGE,"E3.10.1"),sQuery(id+"F0.wireOp",EDGE,"E3.10.2"),sQuery(id+"F0.wireOp",EDGE,"E3.10.3"),sQuery(id+"F0.wireOp",EDGE,"E3.11.1"),sQuery(id+"F0.wireOp",EDGE,"E3.11.2"),sQuery(id+"F0.wireOp",EDGE,"E3.11.3"),sQuery(id+"F0.wireOp",EDGE,"E3.12.1"),sQuery(id+"F0.wireOp",EDGE,"E3.12.2"),sQuery(id+"F0.wireOp",EDGE,"E3.12.3")])],"isStart":false})],"blendedInto":[makeQuery(id+"F1.opExtrude","CAP_FACE",FACE,{"disambiguationData":[OSD([sQuery(id+"F0.wireOp",EDGE,"E0"),sQuery(id+"F0.wireOp",EDGE,"E1"),sQuery(id+"F0.wireOp",EDGE,"E2.bottom"),sQuery(id+"F0.wireOp",EDGE,"E2.left"),sQuery(id+"F0.wireOp",EDGE,"E2.right"),sQuery(id+"F0.wireOp",EDGE,"E3.1.1"),sQuery(id+"F0.wireOp",EDGE,"E3.1.2"),sQuery(id+"F0.wireOp",EDGE,"E3.1.3"),sQuery(id+"F0.wireOp",EDGE,"E3.2.1"),sQuery(id+"F0.wireOp",EDGE,"E3.2.2"),sQuery(id+"F0.wireOp",EDGE,"E3.2.3"),sQuery(id+"F0.wireOp",EDGE,"E3.3.1"),sQuery(id+"F0.wireOp",EDGE,"E3.3.2"),sQuery(id+"F0.wireOp",EDGE,"E3.3.3"),sQuery(id+"F0.wireOp",EDGE,"E3.4.1"),sQuery(id+"F0.wireOp",EDGE,"E3.4.2"),sQuery(id+"F0.wireOp",EDGE,"E3.4.3"),sQuery(id+"F0.wireOp",EDGE,"E3.5.1"),sQuery(id+"F0.wireOp",EDGE,"E3.5.2"),sQuery(id+"F0.wireOp",EDGE,"E3.5.3"),sQuery(id+"F0.wireOp",EDGE,"E3.6.1"),sQuery(id+"F0.wireOp",EDGE,"E3.6.2"),sQuery(id+"F0.wireOp",EDGE,"E3.6.3"),sQuery(id+"F0.wireOp",EDGE,"E3.7.1"),sQuery(id+"F0.wireOp",EDGE,"E3.7.2"),sQuery(id+"F0.wireOp",EDGE,"E3.7.3"),sQuery(id+"F0.wireOp",EDGE,"E3.8.1"),sQuery(id+"F0.wireOp",EDGE,"E3.8.2"),sQuery(id+"F0.wireOp",EDGE,"E3.8.3"),sQuery(id+"F0.wireOp",EDGE,"E3.9.1"),subQ1,subQ0,sQuery(id+"F0.wireOp",EDGE,"E3.10.1"),sQuery(id+"F0.wireOp",EDGE,"E3.10.2"),sQuery(id+"F0.wireOp",EDGE,"E3.10.3"),sQuery(id+"F0.wireOp",EDGE,"E3.11.1"),sQuery(id+"F0.wireOp",EDGE,"E3.11.2"),sQuery(id+"F0.wireOp",EDGE,"E3.11.3"),sQuery(id+"F0.wireOp",EDGE,"E3.12.1"),sQuery(id+"F0.wireOp",EDGE,"E3.12.2"),sQuery(id+"F0.wireOp",EDGE,"E3.12.3")])],"isStart":false})]}),makeQuery(id+"F1.opExtrude","CAP_EDGE",EDGE,{"disambiguationData":[OSD([subQ0])],"isStart":false})],"blendedInto":[]});}
            var Q39;
            {var subQ0=sQuery(id+"F0.wireOp",EDGE,"E3.8.1");var subQ1=sQuery(id+"F0.wireOp",EDGE,"E3.8.2");Q39=makeQuery(id+"F4.opChamfer","BLEND_EDGE",EDGE,{"blendedFrom":[makeQuery(id+"F3.opChamfer","BLEND_EDGE",EDGE,{"blendedFrom":[makeQuery(id+"F1.opExtrude","SWEPT_EDGE",EDGE,{"disambiguationData":[OSD([subQ0,subQ1])]}),makeQuery(id+"F1.opExtrude","CAP_FACE",FACE,{"disambiguationData":[OSD([sQuery(id+"F0.wireOp",EDGE,"E0"),sQuery(id+"F0.wireOp",EDGE,"E1"),sQuery(id+"F0.wireOp",EDGE,"E2.bottom"),sQuery(id+"F0.wireOp",EDGE,"E2.left"),sQuery(id+"F0.wireOp",EDGE,"E2.right"),sQuery(id+"F0.wireOp",EDGE,"E3.1.1"),sQuery(id+"F0.wireOp",EDGE,"E3.1.2"),sQuery(id+"F0.wireOp",EDGE,"E3.1.3"),sQuery(id+"F0.wireOp",EDGE,"E3.2.1"),sQuery(id+"F0.wireOp",EDGE,"E3.2.2"),sQuery(id+"F0.wireOp",EDGE,"E3.2.3"),sQuery(id+"F0.wireOp",EDGE,"E3.3.1"),sQuery(id+"F0.wireOp",EDGE,"E3.3.2"),sQuery(id+"F0.wireOp",EDGE,"E3.3.3"),sQuery(id+"F0.wireOp",EDGE,"E3.4.1"),sQuery(id+"F0.wireOp",EDGE,"E3.4.2"),sQuery(id+"F0.wireOp",EDGE,"E3.4.3"),sQuery(id+"F0.wireOp",EDGE,"E3.5.1"),sQuery(id+"F0.wireOp",EDGE,"E3.5.2"),sQuery(id+"F0.wireOp",EDGE,"E3.5.3"),sQuery(id+"F0.wireOp",EDGE,"E3.6.1"),sQuery(id+"F0.wireOp",EDGE,"E3.6.2"),sQuery(id+"F0.wireOp",EDGE,"E3.6.3"),sQuery(id+"F0.wireOp",EDGE,"E3.7.1"),sQuery(id+"F0.wireOp",EDGE,"E3.7.2"),sQuery(id+"F0.wireOp",EDGE,"E3.7.3"),subQ0,subQ1,sQuery(id+"F0.wireOp",EDGE,"E3.8.3"),sQuery(id+"F0.wireOp",EDGE,"E3.9.1"),sQuery(id+"F0.wireOp",EDGE,"E3.9.2"),sQuery(id+"F0.wireOp",EDGE,"E3.9.3"),sQuery(id+"F0.wireOp",EDGE,"E3.10.1"),sQuery(id+"F0.wireOp",EDGE,"E3.10.2"),sQuery(id+"F0.wireOp",EDGE,"E3.10.3"),sQuery(id+"F0.wireOp",EDGE,"E3.11.1"),sQuery(id+"F0.wireOp",EDGE,"E3.11.2"),sQuery(id+"F0.wireOp",EDGE,"E3.11.3"),sQuery(id+"F0.wireOp",EDGE,"E3.12.1"),sQuery(id+"F0.wireOp",EDGE,"E3.12.2"),sQuery(id+"F0.wireOp",EDGE,"E3.12.3")])],"isStart":false})],"blendedInto":[makeQuery(id+"F1.opExtrude","CAP_FACE",FACE,{"disambiguationData":[OSD([sQuery(id+"F0.wireOp",EDGE,"E0"),sQuery(id+"F0.wireOp",EDGE,"E1"),sQuery(id+"F0.wireOp",EDGE,"E2.bottom"),sQuery(id+"F0.wireOp",EDGE,"E2.left"),sQuery(id+"F0.wireOp",EDGE,"E2.right"),sQuery(id+"F0.wireOp",EDGE,"E3.1.1"),sQuery(id+"F0.wireOp",EDGE,"E3.1.2"),sQuery(id+"F0.wireOp",EDGE,"E3.1.3"),sQuery(id+"F0.wireOp",EDGE,"E3.2.1"),sQuery(id+"F0.wireOp",EDGE,"E3.2.2"),sQuery(id+"F0.wireOp",EDGE,"E3.2.3"),sQuery(id+"F0.wireOp",EDGE,"E3.3.1"),sQuery(id+"F0.wireOp",EDGE,"E3.3.2"),sQuery(id+"F0.wireOp",EDGE,"E3.3.3"),sQuery(id+"F0.wireOp",EDGE,"E3.4.1"),sQuery(id+"F0.wireOp",EDGE,"E3.4.2"),sQuery(id+"F0.wireOp",EDGE,"E3.4.3"),sQuery(id+"F0.wireOp",EDGE,"E3.5.1"),sQuery(id+"F0.wireOp",EDGE,"E3.5.2"),sQuery(id+"F0.wireOp",EDGE,"E3.5.3"),sQuery(id+"F0.wireOp",EDGE,"E3.6.1"),sQuery(id+"F0.wireOp",EDGE,"E3.6.2"),sQuery(id+"F0.wireOp",EDGE,"E3.6.3"),sQuery(id+"F0.wireOp",EDGE,"E3.7.1"),sQuery(id+"F0.wireOp",EDGE,"E3.7.2"),sQuery(id+"F0.wireOp",EDGE,"E3.7.3"),subQ0,subQ1,sQuery(id+"F0.wireOp",EDGE,"E3.8.3"),sQuery(id+"F0.wireOp",EDGE,"E3.9.1"),sQuery(id+"F0.wireOp",EDGE,"E3.9.2"),sQuery(id+"F0.wireOp",EDGE,"E3.9.3"),sQuery(id+"F0.wireOp",EDGE,"E3.10.1"),sQuery(id+"F0.wireOp",EDGE,"E3.10.2"),sQuery(id+"F0.wireOp",EDGE,"E3.10.3"),sQuery(id+"F0.wireOp",EDGE,"E3.11.1"),sQuery(id+"F0.wireOp",EDGE,"E3.11.2"),sQuery(id+"F0.wireOp",EDGE,"E3.11.3"),sQuery(id+"F0.wireOp",EDGE,"E3.12.1"),sQuery(id+"F0.wireOp",EDGE,"E3.12.2"),sQuery(id+"F0.wireOp",EDGE,"E3.12.3")])],"isStart":false})]}),makeQuery(id+"F1.opExtrude","CAP_EDGE",EDGE,{"disambiguationData":[OSD([subQ0])],"isStart":false})],"blendedInto":[]});}
            var Q40;
            {var subQ0=sQuery(id+"F0.wireOp",EDGE,"E3.11.1");var subQ1=sQuery(id+"F0.wireOp",EDGE,"E3.11.2");Q40=makeQuery(id+"F4.opChamfer","BLEND_EDGE",EDGE,{"blendedFrom":[makeQuery(id+"F3.opChamfer","BLEND_EDGE",EDGE,{"blendedFrom":[makeQuery(id+"F1.opExtrude","SWEPT_EDGE",EDGE,{"disambiguationData":[OSD([subQ0,subQ1])]}),makeQuery(id+"F1.opExtrude","CAP_FACE",FACE,{"disambiguationData":[OSD([sQuery(id+"F0.wireOp",EDGE,"E0"),sQuery(id+"F0.wireOp",EDGE,"E1"),sQuery(id+"F0.wireOp",EDGE,"E2.bottom"),sQuery(id+"F0.wireOp",EDGE,"E2.left"),sQuery(id+"F0.wireOp",EDGE,"E2.right"),sQuery(id+"F0.wireOp",EDGE,"E3.1.1"),sQuery(id+"F0.wireOp",EDGE,"E3.1.2"),sQuery(id+"F0.wireOp",EDGE,"E3.1.3"),sQuery(id+"F0.wireOp",EDGE,"E3.2.1"),sQuery(id+"F0.wireOp",EDGE,"E3.2.2"),sQuery(id+"F0.wireOp",EDGE,"E3.2.3"),sQuery(id+"F0.wireOp",EDGE,"E3.3.1"),sQuery(id+"F0.wireOp",EDGE,"E3.3.2"),sQuery(id+"F0.wireOp",EDGE,"E3.3.3"),sQuery(id+"F0.wireOp",EDGE,"E3.4.1"),sQuery(id+"F0.wireOp",EDGE,"E3.4.2"),sQuery(id+"F0.wireOp",EDGE,"E3.4.3"),sQuery(id+"F0.wireOp",EDGE,"E3.5.1"),sQuery(id+"F0.wireOp",EDGE,"E3.5.2"),sQuery(id+"F0.wireOp",EDGE,"E3.5.3"),sQuery(id+"F0.wireOp",EDGE,"E3.6.1"),sQuery(id+"F0.wireOp",EDGE,"E3.6.2"),sQuery(id+"F0.wireOp",EDGE,"E3.6.3"),sQuery(id+"F0.wireOp",EDGE,"E3.7.1"),sQuery(id+"F0.wireOp",EDGE,"E3.7.2"),sQuery(id+"F0.wireOp",EDGE,"E3.7.3"),sQuery(id+"F0.wireOp",EDGE,"E3.8.1"),sQuery(id+"F0.wireOp",EDGE,"E3.8.2"),sQuery(id+"F0.wireOp",EDGE,"E3.8.3"),sQuery(id+"F0.wireOp",EDGE,"E3.9.1"),sQuery(id+"F0.wireOp",EDGE,"E3.9.2"),sQuery(id+"F0.wireOp",EDGE,"E3.9.3"),sQuery(id+"F0.wireOp",EDGE,"E3.10.1"),sQuery(id+"F0.wireOp",EDGE,"E3.10.2"),sQuery(id+"F0.wireOp",EDGE,"E3.10.3"),subQ0,subQ1,sQuery(id+"F0.wireOp",EDGE,"E3.11.3"),sQuery(id+"F0.wireOp",EDGE,"E3.12.1"),sQuery(id+"F0.wireOp",EDGE,"E3.12.2"),sQuery(id+"F0.wireOp",EDGE,"E3.12.3")])],"isStart":false})],"blendedInto":[makeQuery(id+"F1.opExtrude","CAP_FACE",FACE,{"disambiguationData":[OSD([sQuery(id+"F0.wireOp",EDGE,"E0"),sQuery(id+"F0.wireOp",EDGE,"E1"),sQuery(id+"F0.wireOp",EDGE,"E2.bottom"),sQuery(id+"F0.wireOp",EDGE,"E2.left"),sQuery(id+"F0.wireOp",EDGE,"E2.right"),sQuery(id+"F0.wireOp",EDGE,"E3.1.1"),sQuery(id+"F0.wireOp",EDGE,"E3.1.2"),sQuery(id+"F0.wireOp",EDGE,"E3.1.3"),sQuery(id+"F0.wireOp",EDGE,"E3.2.1"),sQuery(id+"F0.wireOp",EDGE,"E3.2.2"),sQuery(id+"F0.wireOp",EDGE,"E3.2.3"),sQuery(id+"F0.wireOp",EDGE,"E3.3.1"),sQuery(id+"F0.wireOp",EDGE,"E3.3.2"),sQuery(id+"F0.wireOp",EDGE,"E3.3.3"),sQuery(id+"F0.wireOp",EDGE,"E3.4.1"),sQuery(id+"F0.wireOp",EDGE,"E3.4.2"),sQuery(id+"F0.wireOp",EDGE,"E3.4.3"),sQuery(id+"F0.wireOp",EDGE,"E3.5.1"),sQuery(id+"F0.wireOp",EDGE,"E3.5.2"),sQuery(id+"F0.wireOp",EDGE,"E3.5.3"),sQuery(id+"F0.wireOp",EDGE,"E3.6.1"),sQuery(id+"F0.wireOp",EDGE,"E3.6.2"),sQuery(id+"F0.wireOp",EDGE,"E3.6.3"),sQuery(id+"F0.wireOp",EDGE,"E3.7.1"),sQuery(id+"F0.wireOp",EDGE,"E3.7.2"),sQuery(id+"F0.wireOp",EDGE,"E3.7.3"),sQuery(id+"F0.wireOp",EDGE,"E3.8.1"),sQuery(id+"F0.wireOp",EDGE,"E3.8.2"),sQuery(id+"F0.wireOp",EDGE,"E3.8.3"),sQuery(id+"F0.wireOp",EDGE,"E3.9.1"),sQuery(id+"F0.wireOp",EDGE,"E3.9.2"),sQuery(id+"F0.wireOp",EDGE,"E3.9.3"),sQuery(id+"F0.wireOp",EDGE,"E3.10.1"),sQuery(id+"F0.wireOp",EDGE,"E3.10.2"),sQuery(id+"F0.wireOp",EDGE,"E3.10.3"),subQ0,subQ1,sQuery(id+"F0.wireOp",EDGE,"E3.11.3"),sQuery(id+"F0.wireOp",EDGE,"E3.12.1"),sQuery(id+"F0.wireOp",EDGE,"E3.12.2"),sQuery(id+"F0.wireOp",EDGE,"E3.12.3")])],"isStart":false})]}),makeQuery(id+"F1.opExtrude","CAP_EDGE",EDGE,{"disambiguationData":[OSD([subQ0])],"isStart":false})],"blendedInto":[]});}
            var Q41;
            {var subQ0=sQuery(id+"F0.wireOp",EDGE,"E3.10.1");var subQ1=sQuery(id+"F0.wireOp",EDGE,"E3.10.2");Q41=makeQuery(id+"F4.opChamfer","BLEND_EDGE",EDGE,{"blendedFrom":[makeQuery(id+"F3.opChamfer","BLEND_EDGE",EDGE,{"blendedFrom":[makeQuery(id+"F1.opExtrude","SWEPT_EDGE",EDGE,{"disambiguationData":[OSD([subQ0,subQ1])]}),makeQuery(id+"F1.opExtrude","CAP_FACE",FACE,{"disambiguationData":[OSD([sQuery(id+"F0.wireOp",EDGE,"E0"),sQuery(id+"F0.wireOp",EDGE,"E1"),sQuery(id+"F0.wireOp",EDGE,"E2.bottom"),sQuery(id+"F0.wireOp",EDGE,"E2.left"),sQuery(id+"F0.wireOp",EDGE,"E2.right"),sQuery(id+"F0.wireOp",EDGE,"E3.1.1"),sQuery(id+"F0.wireOp",EDGE,"E3.1.2"),sQuery(id+"F0.wireOp",EDGE,"E3.1.3"),sQuery(id+"F0.wireOp",EDGE,"E3.2.1"),sQuery(id+"F0.wireOp",EDGE,"E3.2.2"),sQuery(id+"F0.wireOp",EDGE,"E3.2.3"),sQuery(id+"F0.wireOp",EDGE,"E3.3.1"),sQuery(id+"F0.wireOp",EDGE,"E3.3.2"),sQuery(id+"F0.wireOp",EDGE,"E3.3.3"),sQuery(id+"F0.wireOp",EDGE,"E3.4.1"),sQuery(id+"F0.wireOp",EDGE,"E3.4.2"),sQuery(id+"F0.wireOp",EDGE,"E3.4.3"),sQuery(id+"F0.wireOp",EDGE,"E3.5.1"),sQuery(id+"F0.wireOp",EDGE,"E3.5.2"),sQuery(id+"F0.wireOp",EDGE,"E3.5.3"),sQuery(id+"F0.wireOp",EDGE,"E3.6.1"),sQuery(id+"F0.wireOp",EDGE,"E3.6.2"),sQuery(id+"F0.wireOp",EDGE,"E3.6.3"),sQuery(id+"F0.wireOp",EDGE,"E3.7.1"),sQuery(id+"F0.wireOp",EDGE,"E3.7.2"),sQuery(id+"F0.wireOp",EDGE,"E3.7.3"),sQuery(id+"F0.wireOp",EDGE,"E3.8.1"),sQuery(id+"F0.wireOp",EDGE,"E3.8.2"),sQuery(id+"F0.wireOp",EDGE,"E3.8.3"),sQuery(id+"F0.wireOp",EDGE,"E3.9.1"),sQuery(id+"F0.wireOp",EDGE,"E3.9.2"),sQuery(id+"F0.wireOp",EDGE,"E3.9.3"),subQ0,subQ1,sQuery(id+"F0.wireOp",EDGE,"E3.10.3"),sQuery(id+"F0.wireOp",EDGE,"E3.11.1"),sQuery(id+"F0.wireOp",EDGE,"E3.11.2"),sQuery(id+"F0.wireOp",EDGE,"E3.11.3"),sQuery(id+"F0.wireOp",EDGE,"E3.12.1"),sQuery(id+"F0.wireOp",EDGE,"E3.12.2"),sQuery(id+"F0.wireOp",EDGE,"E3.12.3")])],"isStart":false})],"blendedInto":[makeQuery(id+"F1.opExtrude","CAP_FACE",FACE,{"disambiguationData":[OSD([sQuery(id+"F0.wireOp",EDGE,"E0"),sQuery(id+"F0.wireOp",EDGE,"E1"),sQuery(id+"F0.wireOp",EDGE,"E2.bottom"),sQuery(id+"F0.wireOp",EDGE,"E2.left"),sQuery(id+"F0.wireOp",EDGE,"E2.right"),sQuery(id+"F0.wireOp",EDGE,"E3.1.1"),sQuery(id+"F0.wireOp",EDGE,"E3.1.2"),sQuery(id+"F0.wireOp",EDGE,"E3.1.3"),sQuery(id+"F0.wireOp",EDGE,"E3.2.1"),sQuery(id+"F0.wireOp",EDGE,"E3.2.2"),sQuery(id+"F0.wireOp",EDGE,"E3.2.3"),sQuery(id+"F0.wireOp",EDGE,"E3.3.1"),sQuery(id+"F0.wireOp",EDGE,"E3.3.2"),sQuery(id+"F0.wireOp",EDGE,"E3.3.3"),sQuery(id+"F0.wireOp",EDGE,"E3.4.1"),sQuery(id+"F0.wireOp",EDGE,"E3.4.2"),sQuery(id+"F0.wireOp",EDGE,"E3.4.3"),sQuery(id+"F0.wireOp",EDGE,"E3.5.1"),sQuery(id+"F0.wireOp",EDGE,"E3.5.2"),sQuery(id+"F0.wireOp",EDGE,"E3.5.3"),sQuery(id+"F0.wireOp",EDGE,"E3.6.1"),sQuery(id+"F0.wireOp",EDGE,"E3.6.2"),sQuery(id+"F0.wireOp",EDGE,"E3.6.3"),sQuery(id+"F0.wireOp",EDGE,"E3.7.1"),sQuery(id+"F0.wireOp",EDGE,"E3.7.2"),sQuery(id+"F0.wireOp",EDGE,"E3.7.3"),sQuery(id+"F0.wireOp",EDGE,"E3.8.1"),sQuery(id+"F0.wireOp",EDGE,"E3.8.2"),sQuery(id+"F0.wireOp",EDGE,"E3.8.3"),sQuery(id+"F0.wireOp",EDGE,"E3.9.1"),sQuery(id+"F0.wireOp",EDGE,"E3.9.2"),sQuery(id+"F0.wireOp",EDGE,"E3.9.3"),subQ0,subQ1,sQuery(id+"F0.wireOp",EDGE,"E3.10.3"),sQuery(id+"F0.wireOp",EDGE,"E3.11.1"),sQuery(id+"F0.wireOp",EDGE,"E3.11.2"),sQuery(id+"F0.wireOp",EDGE,"E3.11.3"),sQuery(id+"F0.wireOp",EDGE,"E3.12.1"),sQuery(id+"F0.wireOp",EDGE,"E3.12.2"),sQuery(id+"F0.wireOp",EDGE,"E3.12.3")])],"isStart":false})]}),makeQuery(id+"F1.opExtrude","CAP_EDGE",EDGE,{"disambiguationData":[OSD([subQ0])],"isStart":false})],"blendedInto":[]});}
            var Q42;
            {var subQ0=sQuery(id+"F0.wireOp",EDGE,"E3.9.1");var subQ1=sQuery(id+"F0.wireOp",EDGE,"E3.9.2");Q42=makeQuery(id+"F4.opChamfer","BLEND_EDGE",EDGE,{"blendedFrom":[makeQuery(id+"F3.opChamfer","BLEND_EDGE",EDGE,{"blendedFrom":[makeQuery(id+"F1.opExtrude","SWEPT_EDGE",EDGE,{"disambiguationData":[OSD([subQ0,subQ1])]}),makeQuery(id+"F1.opExtrude","CAP_FACE",FACE,{"disambiguationData":[OSD([sQuery(id+"F0.wireOp",EDGE,"E0"),sQuery(id+"F0.wireOp",EDGE,"E1"),sQuery(id+"F0.wireOp",EDGE,"E2.bottom"),sQuery(id+"F0.wireOp",EDGE,"E2.left"),sQuery(id+"F0.wireOp",EDGE,"E2.right"),sQuery(id+"F0.wireOp",EDGE,"E3.1.1"),sQuery(id+"F0.wireOp",EDGE,"E3.1.2"),sQuery(id+"F0.wireOp",EDGE,"E3.1.3"),sQuery(id+"F0.wireOp",EDGE,"E3.2.1"),sQuery(id+"F0.wireOp",EDGE,"E3.2.2"),sQuery(id+"F0.wireOp",EDGE,"E3.2.3"),sQuery(id+"F0.wireOp",EDGE,"E3.3.1"),sQuery(id+"F0.wireOp",EDGE,"E3.3.2"),sQuery(id+"F0.wireOp",EDGE,"E3.3.3"),sQuery(id+"F0.wireOp",EDGE,"E3.4.1"),sQuery(id+"F0.wireOp",EDGE,"E3.4.2"),sQuery(id+"F0.wireOp",EDGE,"E3.4.3"),sQuery(id+"F0.wireOp",EDGE,"E3.5.1"),sQuery(id+"F0.wireOp",EDGE,"E3.5.2"),sQuery(id+"F0.wireOp",EDGE,"E3.5.3"),sQuery(id+"F0.wireOp",EDGE,"E3.6.1"),sQuery(id+"F0.wireOp",EDGE,"E3.6.2"),sQuery(id+"F0.wireOp",EDGE,"E3.6.3"),sQuery(id+"F0.wireOp",EDGE,"E3.7.1"),sQuery(id+"F0.wireOp",EDGE,"E3.7.2"),sQuery(id+"F0.wireOp",EDGE,"E3.7.3"),sQuery(id+"F0.wireOp",EDGE,"E3.8.1"),sQuery(id+"F0.wireOp",EDGE,"E3.8.2"),sQuery(id+"F0.wireOp",EDGE,"E3.8.3"),subQ0,subQ1,sQuery(id+"F0.wireOp",EDGE,"E3.9.3"),sQuery(id+"F0.wireOp",EDGE,"E3.10.1"),sQuery(id+"F0.wireOp",EDGE,"E3.10.2"),sQuery(id+"F0.wireOp",EDGE,"E3.10.3"),sQuery(id+"F0.wireOp",EDGE,"E3.11.1"),sQuery(id+"F0.wireOp",EDGE,"E3.11.2"),sQuery(id+"F0.wireOp",EDGE,"E3.11.3"),sQuery(id+"F0.wireOp",EDGE,"E3.12.1"),sQuery(id+"F0.wireOp",EDGE,"E3.12.2"),sQuery(id+"F0.wireOp",EDGE,"E3.12.3")])],"isStart":false})],"blendedInto":[makeQuery(id+"F1.opExtrude","CAP_FACE",FACE,{"disambiguationData":[OSD([sQuery(id+"F0.wireOp",EDGE,"E0"),sQuery(id+"F0.wireOp",EDGE,"E1"),sQuery(id+"F0.wireOp",EDGE,"E2.bottom"),sQuery(id+"F0.wireOp",EDGE,"E2.left"),sQuery(id+"F0.wireOp",EDGE,"E2.right"),sQuery(id+"F0.wireOp",EDGE,"E3.1.1"),sQuery(id+"F0.wireOp",EDGE,"E3.1.2"),sQuery(id+"F0.wireOp",EDGE,"E3.1.3"),sQuery(id+"F0.wireOp",EDGE,"E3.2.1"),sQuery(id+"F0.wireOp",EDGE,"E3.2.2"),sQuery(id+"F0.wireOp",EDGE,"E3.2.3"),sQuery(id+"F0.wireOp",EDGE,"E3.3.1"),sQuery(id+"F0.wireOp",EDGE,"E3.3.2"),sQuery(id+"F0.wireOp",EDGE,"E3.3.3"),sQuery(id+"F0.wireOp",EDGE,"E3.4.1"),sQuery(id+"F0.wireOp",EDGE,"E3.4.2"),sQuery(id+"F0.wireOp",EDGE,"E3.4.3"),sQuery(id+"F0.wireOp",EDGE,"E3.5.1"),sQuery(id+"F0.wireOp",EDGE,"E3.5.2"),sQuery(id+"F0.wireOp",EDGE,"E3.5.3"),sQuery(id+"F0.wireOp",EDGE,"E3.6.1"),sQuery(id+"F0.wireOp",EDGE,"E3.6.2"),sQuery(id+"F0.wireOp",EDGE,"E3.6.3"),sQuery(id+"F0.wireOp",EDGE,"E3.7.1"),sQuery(id+"F0.wireOp",EDGE,"E3.7.2"),sQuery(id+"F0.wireOp",EDGE,"E3.7.3"),sQuery(id+"F0.wireOp",EDGE,"E3.8.1"),sQuery(id+"F0.wireOp",EDGE,"E3.8.2"),sQuery(id+"F0.wireOp",EDGE,"E3.8.3"),subQ0,subQ1,sQuery(id+"F0.wireOp",EDGE,"E3.9.3"),sQuery(id+"F0.wireOp",EDGE,"E3.10.1"),sQuery(id+"F0.wireOp",EDGE,"E3.10.2"),sQuery(id+"F0.wireOp",EDGE,"E3.10.3"),sQuery(id+"F0.wireOp",EDGE,"E3.11.1"),sQuery(id+"F0.wireOp",EDGE,"E3.11.2"),sQuery(id+"F0.wireOp",EDGE,"E3.11.3"),sQuery(id+"F0.wireOp",EDGE,"E3.12.1"),sQuery(id+"F0.wireOp",EDGE,"E3.12.2"),sQuery(id+"F0.wireOp",EDGE,"E3.12.3")])],"isStart":false})]}),makeQuery(id+"F1.opExtrude","CAP_EDGE",EDGE,{"disambiguationData":[OSD([subQ0])],"isStart":false})],"blendedInto":[]});}
            var Q43;
            {var subQ0=sQuery(id+"F0.wireOp",EDGE,"E3.12.1");var subQ1=sQuery(id+"F0.wireOp",EDGE,"E3.12.2");Q43=makeQuery(id+"F4.opChamfer","BLEND_EDGE",EDGE,{"blendedFrom":[makeQuery(id+"F3.opChamfer","BLEND_EDGE",EDGE,{"blendedFrom":[makeQuery(id+"F1.opExtrude","SWEPT_EDGE",EDGE,{"disambiguationData":[OSD([subQ0,subQ1])]}),makeQuery(id+"F1.opExtrude","CAP_FACE",FACE,{"disambiguationData":[OSD([sQuery(id+"F0.wireOp",EDGE,"E0"),sQuery(id+"F0.wireOp",EDGE,"E1"),sQuery(id+"F0.wireOp",EDGE,"E2.bottom"),sQuery(id+"F0.wireOp",EDGE,"E2.left"),sQuery(id+"F0.wireOp",EDGE,"E2.right"),sQuery(id+"F0.wireOp",EDGE,"E3.1.1"),sQuery(id+"F0.wireOp",EDGE,"E3.1.2"),sQuery(id+"F0.wireOp",EDGE,"E3.1.3"),sQuery(id+"F0.wireOp",EDGE,"E3.2.1"),sQuery(id+"F0.wireOp",EDGE,"E3.2.2"),sQuery(id+"F0.wireOp",EDGE,"E3.2.3"),sQuery(id+"F0.wireOp",EDGE,"E3.3.1"),sQuery(id+"F0.wireOp",EDGE,"E3.3.2"),sQuery(id+"F0.wireOp",EDGE,"E3.3.3"),sQuery(id+"F0.wireOp",EDGE,"E3.4.1"),sQuery(id+"F0.wireOp",EDGE,"E3.4.2"),sQuery(id+"F0.wireOp",EDGE,"E3.4.3"),sQuery(id+"F0.wireOp",EDGE,"E3.5.1"),sQuery(id+"F0.wireOp",EDGE,"E3.5.2"),sQuery(id+"F0.wireOp",EDGE,"E3.5.3"),sQuery(id+"F0.wireOp",EDGE,"E3.6.1"),sQuery(id+"F0.wireOp",EDGE,"E3.6.2"),sQuery(id+"F0.wireOp",EDGE,"E3.6.3"),sQuery(id+"F0.wireOp",EDGE,"E3.7.1"),sQuery(id+"F0.wireOp",EDGE,"E3.7.2"),sQuery(id+"F0.wireOp",EDGE,"E3.7.3"),sQuery(id+"F0.wireOp",EDGE,"E3.8.1"),sQuery(id+"F0.wireOp",EDGE,"E3.8.2"),sQuery(id+"F0.wireOp",EDGE,"E3.8.3"),sQuery(id+"F0.wireOp",EDGE,"E3.9.1"),sQuery(id+"F0.wireOp",EDGE,"E3.9.2"),sQuery(id+"F0.wireOp",EDGE,"E3.9.3"),sQuery(id+"F0.wireOp",EDGE,"E3.10.1"),sQuery(id+"F0.wireOp",EDGE,"E3.10.2"),sQuery(id+"F0.wireOp",EDGE,"E3.10.3"),sQuery(id+"F0.wireOp",EDGE,"E3.11.1"),sQuery(id+"F0.wireOp",EDGE,"E3.11.2"),sQuery(id+"F0.wireOp",EDGE,"E3.11.3"),subQ0,subQ1,sQuery(id+"F0.wireOp",EDGE,"E3.12.3")])],"isStart":false})],"blendedInto":[makeQuery(id+"F1.opExtrude","CAP_FACE",FACE,{"disambiguationData":[OSD([sQuery(id+"F0.wireOp",EDGE,"E0"),sQuery(id+"F0.wireOp",EDGE,"E1"),sQuery(id+"F0.wireOp",EDGE,"E2.bottom"),sQuery(id+"F0.wireOp",EDGE,"E2.left"),sQuery(id+"F0.wireOp",EDGE,"E2.right"),sQuery(id+"F0.wireOp",EDGE,"E3.1.1"),sQuery(id+"F0.wireOp",EDGE,"E3.1.2"),sQuery(id+"F0.wireOp",EDGE,"E3.1.3"),sQuery(id+"F0.wireOp",EDGE,"E3.2.1"),sQuery(id+"F0.wireOp",EDGE,"E3.2.2"),sQuery(id+"F0.wireOp",EDGE,"E3.2.3"),sQuery(id+"F0.wireOp",EDGE,"E3.3.1"),sQuery(id+"F0.wireOp",EDGE,"E3.3.2"),sQuery(id+"F0.wireOp",EDGE,"E3.3.3"),sQuery(id+"F0.wireOp",EDGE,"E3.4.1"),sQuery(id+"F0.wireOp",EDGE,"E3.4.2"),sQuery(id+"F0.wireOp",EDGE,"E3.4.3"),sQuery(id+"F0.wireOp",EDGE,"E3.5.1"),sQuery(id+"F0.wireOp",EDGE,"E3.5.2"),sQuery(id+"F0.wireOp",EDGE,"E3.5.3"),sQuery(id+"F0.wireOp",EDGE,"E3.6.1"),sQuery(id+"F0.wireOp",EDGE,"E3.6.2"),sQuery(id+"F0.wireOp",EDGE,"E3.6.3"),sQuery(id+"F0.wireOp",EDGE,"E3.7.1"),sQuery(id+"F0.wireOp",EDGE,"E3.7.2"),sQuery(id+"F0.wireOp",EDGE,"E3.7.3"),sQuery(id+"F0.wireOp",EDGE,"E3.8.1"),sQuery(id+"F0.wireOp",EDGE,"E3.8.2"),sQuery(id+"F0.wireOp",EDGE,"E3.8.3"),sQuery(id+"F0.wireOp",EDGE,"E3.9.1"),sQuery(id+"F0.wireOp",EDGE,"E3.9.2"),sQuery(id+"F0.wireOp",EDGE,"E3.9.3"),sQuery(id+"F0.wireOp",EDGE,"E3.10.1"),sQuery(id+"F0.wireOp",EDGE,"E3.10.2"),sQuery(id+"F0.wireOp",EDGE,"E3.10.3"),sQuery(id+"F0.wireOp",EDGE,"E3.11.1"),sQuery(id+"F0.wireOp",EDGE,"E3.11.2"),sQuery(id+"F0.wireOp",EDGE,"E3.11.3"),subQ0,subQ1,sQuery(id+"F0.wireOp",EDGE,"E3.12.3")])],"isStart":false})]}),makeQuery(id+"F1.opExtrude","CAP_EDGE",EDGE,{"disambiguationData":[OSD([subQ0])],"isStart":false})],"blendedInto":[]});}
            var Q44;
            {var subQ0=sQuery(id+"F0.wireOp",EDGE,"E2.left");var subQ1=sQuery(id+"F0.wireOp",EDGE,"E2.bottom");Q44=makeQuery(id+"F4.opChamfer","BLEND_EDGE",EDGE,{"blendedFrom":[makeQuery(id+"F3.opChamfer","BLEND_EDGE",EDGE,{"blendedFrom":[makeQuery(id+"F1.opExtrude","SWEPT_EDGE",EDGE,{"disambiguationData":[OSD([subQ1,subQ0])]}),makeQuery(id+"F1.opExtrude","CAP_FACE",FACE,{"disambiguationData":[OSD([sQuery(id+"F0.wireOp",EDGE,"E0"),sQuery(id+"F0.wireOp",EDGE,"E1"),subQ1,subQ0,sQuery(id+"F0.wireOp",EDGE,"E2.right"),sQuery(id+"F0.wireOp",EDGE,"E3.1.1"),sQuery(id+"F0.wireOp",EDGE,"E3.1.2"),sQuery(id+"F0.wireOp",EDGE,"E3.1.3"),sQuery(id+"F0.wireOp",EDGE,"E3.2.1"),sQuery(id+"F0.wireOp",EDGE,"E3.2.2"),sQuery(id+"F0.wireOp",EDGE,"E3.2.3"),sQuery(id+"F0.wireOp",EDGE,"E3.3.1"),sQuery(id+"F0.wireOp",EDGE,"E3.3.2"),sQuery(id+"F0.wireOp",EDGE,"E3.3.3"),sQuery(id+"F0.wireOp",EDGE,"E3.4.1"),sQuery(id+"F0.wireOp",EDGE,"E3.4.2"),sQuery(id+"F0.wireOp",EDGE,"E3.4.3"),sQuery(id+"F0.wireOp",EDGE,"E3.5.1"),sQuery(id+"F0.wireOp",EDGE,"E3.5.2"),sQuery(id+"F0.wireOp",EDGE,"E3.5.3"),sQuery(id+"F0.wireOp",EDGE,"E3.6.1"),sQuery(id+"F0.wireOp",EDGE,"E3.6.2"),sQuery(id+"F0.wireOp",EDGE,"E3.6.3"),sQuery(id+"F0.wireOp",EDGE,"E3.7.1"),sQuery(id+"F0.wireOp",EDGE,"E3.7.2"),sQuery(id+"F0.wireOp",EDGE,"E3.7.3"),sQuery(id+"F0.wireOp",EDGE,"E3.8.1"),sQuery(id+"F0.wireOp",EDGE,"E3.8.2"),sQuery(id+"F0.wireOp",EDGE,"E3.8.3"),sQuery(id+"F0.wireOp",EDGE,"E3.9.1"),sQuery(id+"F0.wireOp",EDGE,"E3.9.2"),sQuery(id+"F0.wireOp",EDGE,"E3.9.3"),sQuery(id+"F0.wireOp",EDGE,"E3.10.1"),sQuery(id+"F0.wireOp",EDGE,"E3.10.2"),sQuery(id+"F0.wireOp",EDGE,"E3.10.3"),sQuery(id+"F0.wireOp",EDGE,"E3.11.1"),sQuery(id+"F0.wireOp",EDGE,"E3.11.2"),sQuery(id+"F0.wireOp",EDGE,"E3.11.3"),sQuery(id+"F0.wireOp",EDGE,"E3.12.1"),sQuery(id+"F0.wireOp",EDGE,"E3.12.2"),sQuery(id+"F0.wireOp",EDGE,"E3.12.3")])],"isStart":false})],"blendedInto":[makeQuery(id+"F1.opExtrude","CAP_FACE",FACE,{"disambiguationData":[OSD([sQuery(id+"F0.wireOp",EDGE,"E0"),sQuery(id+"F0.wireOp",EDGE,"E1"),subQ1,subQ0,sQuery(id+"F0.wireOp",EDGE,"E2.right"),sQuery(id+"F0.wireOp",EDGE,"E3.1.1"),sQuery(id+"F0.wireOp",EDGE,"E3.1.2"),sQuery(id+"F0.wireOp",EDGE,"E3.1.3"),sQuery(id+"F0.wireOp",EDGE,"E3.2.1"),sQuery(id+"F0.wireOp",EDGE,"E3.2.2"),sQuery(id+"F0.wireOp",EDGE,"E3.2.3"),sQuery(id+"F0.wireOp",EDGE,"E3.3.1"),sQuery(id+"F0.wireOp",EDGE,"E3.3.2"),sQuery(id+"F0.wireOp",EDGE,"E3.3.3"),sQuery(id+"F0.wireOp",EDGE,"E3.4.1"),sQuery(id+"F0.wireOp",EDGE,"E3.4.2"),sQuery(id+"F0.wireOp",EDGE,"E3.4.3"),sQuery(id+"F0.wireOp",EDGE,"E3.5.1"),sQuery(id+"F0.wireOp",EDGE,"E3.5.2"),sQuery(id+"F0.wireOp",EDGE,"E3.5.3"),sQuery(id+"F0.wireOp",EDGE,"E3.6.1"),sQuery(id+"F0.wireOp",EDGE,"E3.6.2"),sQuery(id+"F0.wireOp",EDGE,"E3.6.3"),sQuery(id+"F0.wireOp",EDGE,"E3.7.1"),sQuery(id+"F0.wireOp",EDGE,"E3.7.2"),sQuery(id+"F0.wireOp",EDGE,"E3.7.3"),sQuery(id+"F0.wireOp",EDGE,"E3.8.1"),sQuery(id+"F0.wireOp",EDGE,"E3.8.2"),sQuery(id+"F0.wireOp",EDGE,"E3.8.3"),sQuery(id+"F0.wireOp",EDGE,"E3.9.1"),sQuery(id+"F0.wireOp",EDGE,"E3.9.2"),sQuery(id+"F0.wireOp",EDGE,"E3.9.3"),sQuery(id+"F0.wireOp",EDGE,"E3.10.1"),sQuery(id+"F0.wireOp",EDGE,"E3.10.2"),sQuery(id+"F0.wireOp",EDGE,"E3.10.3"),sQuery(id+"F0.wireOp",EDGE,"E3.11.1"),sQuery(id+"F0.wireOp",EDGE,"E3.11.2"),sQuery(id+"F0.wireOp",EDGE,"E3.11.3"),sQuery(id+"F0.wireOp",EDGE,"E3.12.1"),sQuery(id+"F0.wireOp",EDGE,"E3.12.2"),sQuery(id+"F0.wireOp",EDGE,"E3.12.3")])],"isStart":false})]}),makeQuery(id+"F1.opExtrude","CAP_EDGE",EDGE,{"disambiguationData":[OSD([subQ0])],"isStart":false})],"blendedInto":[]});}
            var Q45;
            {var subQ0=sQuery(id+"F0.wireOp",EDGE,"E2.right");var subQ1=sQuery(id+"F0.wireOp",EDGE,"E2.bottom");Q45=makeQuery(id+"F4.opChamfer","BLEND_EDGE",EDGE,{"blendedFrom":[makeQuery(id+"F3.opChamfer","BLEND_EDGE",EDGE,{"blendedFrom":[makeQuery(id+"F1.opExtrude","SWEPT_EDGE",EDGE,{"disambiguationData":[OSD([subQ1,subQ0])]}),makeQuery(id+"F1.opExtrude","CAP_FACE",FACE,{"disambiguationData":[OSD([sQuery(id+"F0.wireOp",EDGE,"E0"),sQuery(id+"F0.wireOp",EDGE,"E1"),subQ1,sQuery(id+"F0.wireOp",EDGE,"E2.left"),subQ0,sQuery(id+"F0.wireOp",EDGE,"E3.1.1"),sQuery(id+"F0.wireOp",EDGE,"E3.1.2"),sQuery(id+"F0.wireOp",EDGE,"E3.1.3"),sQuery(id+"F0.wireOp",EDGE,"E3.2.1"),sQuery(id+"F0.wireOp",EDGE,"E3.2.2"),sQuery(id+"F0.wireOp",EDGE,"E3.2.3"),sQuery(id+"F0.wireOp",EDGE,"E3.3.1"),sQuery(id+"F0.wireOp",EDGE,"E3.3.2"),sQuery(id+"F0.wireOp",EDGE,"E3.3.3"),sQuery(id+"F0.wireOp",EDGE,"E3.4.1"),sQuery(id+"F0.wireOp",EDGE,"E3.4.2"),sQuery(id+"F0.wireOp",EDGE,"E3.4.3"),sQuery(id+"F0.wireOp",EDGE,"E3.5.1"),sQuery(id+"F0.wireOp",EDGE,"E3.5.2"),sQuery(id+"F0.wireOp",EDGE,"E3.5.3"),sQuery(id+"F0.wireOp",EDGE,"E3.6.1"),sQuery(id+"F0.wireOp",EDGE,"E3.6.2"),sQuery(id+"F0.wireOp",EDGE,"E3.6.3"),sQuery(id+"F0.wireOp",EDGE,"E3.7.1"),sQuery(id+"F0.wireOp",EDGE,"E3.7.2"),sQuery(id+"F0.wireOp",EDGE,"E3.7.3"),sQuery(id+"F0.wireOp",EDGE,"E3.8.1"),sQuery(id+"F0.wireOp",EDGE,"E3.8.2"),sQuery(id+"F0.wireOp",EDGE,"E3.8.3"),sQuery(id+"F0.wireOp",EDGE,"E3.9.1"),sQuery(id+"F0.wireOp",EDGE,"E3.9.2"),sQuery(id+"F0.wireOp",EDGE,"E3.9.3"),sQuery(id+"F0.wireOp",EDGE,"E3.10.1"),sQuery(id+"F0.wireOp",EDGE,"E3.10.2"),sQuery(id+"F0.wireOp",EDGE,"E3.10.3"),sQuery(id+"F0.wireOp",EDGE,"E3.11.1"),sQuery(id+"F0.wireOp",EDGE,"E3.11.2"),sQuery(id+"F0.wireOp",EDGE,"E3.11.3"),sQuery(id+"F0.wireOp",EDGE,"E3.12.1"),sQuery(id+"F0.wireOp",EDGE,"E3.12.2"),sQuery(id+"F0.wireOp",EDGE,"E3.12.3")])],"isStart":false})],"blendedInto":[makeQuery(id+"F1.opExtrude","CAP_FACE",FACE,{"disambiguationData":[OSD([sQuery(id+"F0.wireOp",EDGE,"E0"),sQuery(id+"F0.wireOp",EDGE,"E1"),subQ1,sQuery(id+"F0.wireOp",EDGE,"E2.left"),subQ0,sQuery(id+"F0.wireOp",EDGE,"E3.1.1"),sQuery(id+"F0.wireOp",EDGE,"E3.1.2"),sQuery(id+"F0.wireOp",EDGE,"E3.1.3"),sQuery(id+"F0.wireOp",EDGE,"E3.2.1"),sQuery(id+"F0.wireOp",EDGE,"E3.2.2"),sQuery(id+"F0.wireOp",EDGE,"E3.2.3"),sQuery(id+"F0.wireOp",EDGE,"E3.3.1"),sQuery(id+"F0.wireOp",EDGE,"E3.3.2"),sQuery(id+"F0.wireOp",EDGE,"E3.3.3"),sQuery(id+"F0.wireOp",EDGE,"E3.4.1"),sQuery(id+"F0.wireOp",EDGE,"E3.4.2"),sQuery(id+"F0.wireOp",EDGE,"E3.4.3"),sQuery(id+"F0.wireOp",EDGE,"E3.5.1"),sQuery(id+"F0.wireOp",EDGE,"E3.5.2"),sQuery(id+"F0.wireOp",EDGE,"E3.5.3"),sQuery(id+"F0.wireOp",EDGE,"E3.6.1"),sQuery(id+"F0.wireOp",EDGE,"E3.6.2"),sQuery(id+"F0.wireOp",EDGE,"E3.6.3"),sQuery(id+"F0.wireOp",EDGE,"E3.7.1"),sQuery(id+"F0.wireOp",EDGE,"E3.7.2"),sQuery(id+"F0.wireOp",EDGE,"E3.7.3"),sQuery(id+"F0.wireOp",EDGE,"E3.8.1"),sQuery(id+"F0.wireOp",EDGE,"E3.8.2"),sQuery(id+"F0.wireOp",EDGE,"E3.8.3"),sQuery(id+"F0.wireOp",EDGE,"E3.9.1"),sQuery(id+"F0.wireOp",EDGE,"E3.9.2"),sQuery(id+"F0.wireOp",EDGE,"E3.9.3"),sQuery(id+"F0.wireOp",EDGE,"E3.10.1"),sQuery(id+"F0.wireOp",EDGE,"E3.10.2"),sQuery(id+"F0.wireOp",EDGE,"E3.10.3"),sQuery(id+"F0.wireOp",EDGE,"E3.11.1"),sQuery(id+"F0.wireOp",EDGE,"E3.11.2"),sQuery(id+"F0.wireOp",EDGE,"E3.11.3"),sQuery(id+"F0.wireOp",EDGE,"E3.12.1"),sQuery(id+"F0.wireOp",EDGE,"E3.12.2"),sQuery(id+"F0.wireOp",EDGE,"E3.12.3")])],"isStart":false})]}),makeQuery(id+"F1.opExtrude","CAP_EDGE",EDGE,{"disambiguationData":[OSD([subQ0])],"isStart":false})],"blendedInto":[]});}
            var Q46;
            {var subQ0=sQuery(id+"F0.wireOp",EDGE,"E3.2.3");var subQ1=sQuery(id+"F0.wireOp",EDGE,"E3.2.2");Q46=makeQuery(id+"F4.opChamfer","BLEND_EDGE",EDGE,{"blendedFrom":[makeQuery(id+"F3.opChamfer","BLEND_EDGE",EDGE,{"blendedFrom":[makeQuery(id+"F1.opExtrude","SWEPT_EDGE",EDGE,{"disambiguationData":[OSD([subQ1,subQ0])]}),makeQuery(id+"F1.opExtrude","CAP_FACE",FACE,{"disambiguationData":[OSD([sQuery(id+"F0.wireOp",EDGE,"E0"),sQuery(id+"F0.wireOp",EDGE,"E1"),sQuery(id+"F0.wireOp",EDGE,"E2.bottom"),sQuery(id+"F0.wireOp",EDGE,"E2.left"),sQuery(id+"F0.wireOp",EDGE,"E2.right"),sQuery(id+"F0.wireOp",EDGE,"E3.1.1"),sQuery(id+"F0.wireOp",EDGE,"E3.1.2"),sQuery(id+"F0.wireOp",EDGE,"E3.1.3"),sQuery(id+"F0.wireOp",EDGE,"E3.2.1"),subQ1,subQ0,sQuery(id+"F0.wireOp",EDGE,"E3.3.1"),sQuery(id+"F0.wireOp",EDGE,"E3.3.2"),sQuery(id+"F0.wireOp",EDGE,"E3.3.3"),sQuery(id+"F0.wireOp",EDGE,"E3.4.1"),sQuery(id+"F0.wireOp",EDGE,"E3.4.2"),sQuery(id+"F0.wireOp",EDGE,"E3.4.3"),sQuery(id+"F0.wireOp",EDGE,"E3.5.1"),sQuery(id+"F0.wireOp",EDGE,"E3.5.2"),sQuery(id+"F0.wireOp",EDGE,"E3.5.3"),sQuery(id+"F0.wireOp",EDGE,"E3.6.1"),sQuery(id+"F0.wireOp",EDGE,"E3.6.2"),sQuery(id+"F0.wireOp",EDGE,"E3.6.3"),sQuery(id+"F0.wireOp",EDGE,"E3.7.1"),sQuery(id+"F0.wireOp",EDGE,"E3.7.2"),sQuery(id+"F0.wireOp",EDGE,"E3.7.3"),sQuery(id+"F0.wireOp",EDGE,"E3.8.1"),sQuery(id+"F0.wireOp",EDGE,"E3.8.2"),sQuery(id+"F0.wireOp",EDGE,"E3.8.3"),sQuery(id+"F0.wireOp",EDGE,"E3.9.1"),sQuery(id+"F0.wireOp",EDGE,"E3.9.2"),sQuery(id+"F0.wireOp",EDGE,"E3.9.3"),sQuery(id+"F0.wireOp",EDGE,"E3.10.1"),sQuery(id+"F0.wireOp",EDGE,"E3.10.2"),sQuery(id+"F0.wireOp",EDGE,"E3.10.3"),sQuery(id+"F0.wireOp",EDGE,"E3.11.1"),sQuery(id+"F0.wireOp",EDGE,"E3.11.2"),sQuery(id+"F0.wireOp",EDGE,"E3.11.3"),sQuery(id+"F0.wireOp",EDGE,"E3.12.1"),sQuery(id+"F0.wireOp",EDGE,"E3.12.2"),sQuery(id+"F0.wireOp",EDGE,"E3.12.3")])],"isStart":false})],"blendedInto":[makeQuery(id+"F1.opExtrude","CAP_FACE",FACE,{"disambiguationData":[OSD([sQuery(id+"F0.wireOp",EDGE,"E0"),sQuery(id+"F0.wireOp",EDGE,"E1"),sQuery(id+"F0.wireOp",EDGE,"E2.bottom"),sQuery(id+"F0.wireOp",EDGE,"E2.left"),sQuery(id+"F0.wireOp",EDGE,"E2.right"),sQuery(id+"F0.wireOp",EDGE,"E3.1.1"),sQuery(id+"F0.wireOp",EDGE,"E3.1.2"),sQuery(id+"F0.wireOp",EDGE,"E3.1.3"),sQuery(id+"F0.wireOp",EDGE,"E3.2.1"),subQ1,subQ0,sQuery(id+"F0.wireOp",EDGE,"E3.3.1"),sQuery(id+"F0.wireOp",EDGE,"E3.3.2"),sQuery(id+"F0.wireOp",EDGE,"E3.3.3"),sQuery(id+"F0.wireOp",EDGE,"E3.4.1"),sQuery(id+"F0.wireOp",EDGE,"E3.4.2"),sQuery(id+"F0.wireOp",EDGE,"E3.4.3"),sQuery(id+"F0.wireOp",EDGE,"E3.5.1"),sQuery(id+"F0.wireOp",EDGE,"E3.5.2"),sQuery(id+"F0.wireOp",EDGE,"E3.5.3"),sQuery(id+"F0.wireOp",EDGE,"E3.6.1"),sQuery(id+"F0.wireOp",EDGE,"E3.6.2"),sQuery(id+"F0.wireOp",EDGE,"E3.6.3"),sQuery(id+"F0.wireOp",EDGE,"E3.7.1"),sQuery(id+"F0.wireOp",EDGE,"E3.7.2"),sQuery(id+"F0.wireOp",EDGE,"E3.7.3"),sQuery(id+"F0.wireOp",EDGE,"E3.8.1"),sQuery(id+"F0.wireOp",EDGE,"E3.8.2"),sQuery(id+"F0.wireOp",EDGE,"E3.8.3"),sQuery(id+"F0.wireOp",EDGE,"E3.9.1"),sQuery(id+"F0.wireOp",EDGE,"E3.9.2"),sQuery(id+"F0.wireOp",EDGE,"E3.9.3"),sQuery(id+"F0.wireOp",EDGE,"E3.10.1"),sQuery(id+"F0.wireOp",EDGE,"E3.10.2"),sQuery(id+"F0.wireOp",EDGE,"E3.10.3"),sQuery(id+"F0.wireOp",EDGE,"E3.11.1"),sQuery(id+"F0.wireOp",EDGE,"E3.11.2"),sQuery(id+"F0.wireOp",EDGE,"E3.11.3"),sQuery(id+"F0.wireOp",EDGE,"E3.12.1"),sQuery(id+"F0.wireOp",EDGE,"E3.12.2"),sQuery(id+"F0.wireOp",EDGE,"E3.12.3")])],"isStart":false})]}),makeQuery(id+"F1.opExtrude","CAP_EDGE",EDGE,{"disambiguationData":[OSD([subQ0])],"isStart":false})],"blendedInto":[]});}
            var Q47;
            {var subQ0=sQuery(id+"F0.wireOp",EDGE,"E3.2.1");var subQ1=sQuery(id+"F0.wireOp",EDGE,"E3.2.2");Q47=makeQuery(id+"F4.opChamfer","BLEND_EDGE",EDGE,{"blendedFrom":[makeQuery(id+"F3.opChamfer","BLEND_EDGE",EDGE,{"blendedFrom":[makeQuery(id+"F1.opExtrude","SWEPT_EDGE",EDGE,{"disambiguationData":[OSD([subQ0,subQ1])]}),makeQuery(id+"F1.opExtrude","CAP_FACE",FACE,{"disambiguationData":[OSD([sQuery(id+"F0.wireOp",EDGE,"E0"),sQuery(id+"F0.wireOp",EDGE,"E1"),sQuery(id+"F0.wireOp",EDGE,"E2.bottom"),sQuery(id+"F0.wireOp",EDGE,"E2.left"),sQuery(id+"F0.wireOp",EDGE,"E2.right"),sQuery(id+"F0.wireOp",EDGE,"E3.1.1"),sQuery(id+"F0.wireOp",EDGE,"E3.1.2"),sQuery(id+"F0.wireOp",EDGE,"E3.1.3"),subQ0,subQ1,sQuery(id+"F0.wireOp",EDGE,"E3.2.3"),sQuery(id+"F0.wireOp",EDGE,"E3.3.1"),sQuery(id+"F0.wireOp",EDGE,"E3.3.2"),sQuery(id+"F0.wireOp",EDGE,"E3.3.3"),sQuery(id+"F0.wireOp",EDGE,"E3.4.1"),sQuery(id+"F0.wireOp",EDGE,"E3.4.2"),sQuery(id+"F0.wireOp",EDGE,"E3.4.3"),sQuery(id+"F0.wireOp",EDGE,"E3.5.1"),sQuery(id+"F0.wireOp",EDGE,"E3.5.2"),sQuery(id+"F0.wireOp",EDGE,"E3.5.3"),sQuery(id+"F0.wireOp",EDGE,"E3.6.1"),sQuery(id+"F0.wireOp",EDGE,"E3.6.2"),sQuery(id+"F0.wireOp",EDGE,"E3.6.3"),sQuery(id+"F0.wireOp",EDGE,"E3.7.1"),sQuery(id+"F0.wireOp",EDGE,"E3.7.2"),sQuery(id+"F0.wireOp",EDGE,"E3.7.3"),sQuery(id+"F0.wireOp",EDGE,"E3.8.1"),sQuery(id+"F0.wireOp",EDGE,"E3.8.2"),sQuery(id+"F0.wireOp",EDGE,"E3.8.3"),sQuery(id+"F0.wireOp",EDGE,"E3.9.1"),sQuery(id+"F0.wireOp",EDGE,"E3.9.2"),sQuery(id+"F0.wireOp",EDGE,"E3.9.3"),sQuery(id+"F0.wireOp",EDGE,"E3.10.1"),sQuery(id+"F0.wireOp",EDGE,"E3.10.2"),sQuery(id+"F0.wireOp",EDGE,"E3.10.3"),sQuery(id+"F0.wireOp",EDGE,"E3.11.1"),sQuery(id+"F0.wireOp",EDGE,"E3.11.2"),sQuery(id+"F0.wireOp",EDGE,"E3.11.3"),sQuery(id+"F0.wireOp",EDGE,"E3.12.1"),sQuery(id+"F0.wireOp",EDGE,"E3.12.2"),sQuery(id+"F0.wireOp",EDGE,"E3.12.3")])],"isStart":false})],"blendedInto":[makeQuery(id+"F1.opExtrude","CAP_FACE",FACE,{"disambiguationData":[OSD([sQuery(id+"F0.wireOp",EDGE,"E0"),sQuery(id+"F0.wireOp",EDGE,"E1"),sQuery(id+"F0.wireOp",EDGE,"E2.bottom"),sQuery(id+"F0.wireOp",EDGE,"E2.left"),sQuery(id+"F0.wireOp",EDGE,"E2.right"),sQuery(id+"F0.wireOp",EDGE,"E3.1.1"),sQuery(id+"F0.wireOp",EDGE,"E3.1.2"),sQuery(id+"F0.wireOp",EDGE,"E3.1.3"),subQ0,subQ1,sQuery(id+"F0.wireOp",EDGE,"E3.2.3"),sQuery(id+"F0.wireOp",EDGE,"E3.3.1"),sQuery(id+"F0.wireOp",EDGE,"E3.3.2"),sQuery(id+"F0.wireOp",EDGE,"E3.3.3"),sQuery(id+"F0.wireOp",EDGE,"E3.4.1"),sQuery(id+"F0.wireOp",EDGE,"E3.4.2"),sQuery(id+"F0.wireOp",EDGE,"E3.4.3"),sQuery(id+"F0.wireOp",EDGE,"E3.5.1"),sQuery(id+"F0.wireOp",EDGE,"E3.5.2"),sQuery(id+"F0.wireOp",EDGE,"E3.5.3"),sQuery(id+"F0.wireOp",EDGE,"E3.6.1"),sQuery(id+"F0.wireOp",EDGE,"E3.6.2"),sQuery(id+"F0.wireOp",EDGE,"E3.6.3"),sQuery(id+"F0.wireOp",EDGE,"E3.7.1"),sQuery(id+"F0.wireOp",EDGE,"E3.7.2"),sQuery(id+"F0.wireOp",EDGE,"E3.7.3"),sQuery(id+"F0.wireOp",EDGE,"E3.8.1"),sQuery(id+"F0.wireOp",EDGE,"E3.8.2"),sQuery(id+"F0.wireOp",EDGE,"E3.8.3"),sQuery(id+"F0.wireOp",EDGE,"E3.9.1"),sQuery(id+"F0.wireOp",EDGE,"E3.9.2"),sQuery(id+"F0.wireOp",EDGE,"E3.9.3"),sQuery(id+"F0.wireOp",EDGE,"E3.10.1"),sQuery(id+"F0.wireOp",EDGE,"E3.10.2"),sQuery(id+"F0.wireOp",EDGE,"E3.10.3"),sQuery(id+"F0.wireOp",EDGE,"E3.11.1"),sQuery(id+"F0.wireOp",EDGE,"E3.11.2"),sQuery(id+"F0.wireOp",EDGE,"E3.11.3"),sQuery(id+"F0.wireOp",EDGE,"E3.12.1"),sQuery(id+"F0.wireOp",EDGE,"E3.12.2"),sQuery(id+"F0.wireOp",EDGE,"E3.12.3")])],"isStart":false})]}),makeQuery(id+"F1.opExtrude","CAP_EDGE",EDGE,{"disambiguationData":[OSD([subQ0])],"isStart":false})],"blendedInto":[]});}
            var Q48;
            {var subQ0=sQuery(id+"F0.wireOp",EDGE,"E3.3.3");var subQ1=sQuery(id+"F0.wireOp",EDGE,"E3.3.2");Q48=makeQuery(id+"F4.opChamfer","BLEND_EDGE",EDGE,{"blendedFrom":[makeQuery(id+"F3.opChamfer","BLEND_EDGE",EDGE,{"blendedFrom":[makeQuery(id+"F1.opExtrude","SWEPT_EDGE",EDGE,{"disambiguationData":[OSD([subQ1,subQ0])]}),makeQuery(id+"F1.opExtrude","CAP_FACE",FACE,{"disambiguationData":[OSD([sQuery(id+"F0.wireOp",EDGE,"E0"),sQuery(id+"F0.wireOp",EDGE,"E1"),sQuery(id+"F0.wireOp",EDGE,"E2.bottom"),sQuery(id+"F0.wireOp",EDGE,"E2.left"),sQuery(id+"F0.wireOp",EDGE,"E2.right"),sQuery(id+"F0.wireOp",EDGE,"E3.1.1"),sQuery(id+"F0.wireOp",EDGE,"E3.1.2"),sQuery(id+"F0.wireOp",EDGE,"E3.1.3"),sQuery(id+"F0.wireOp",EDGE,"E3.2.1"),sQuery(id+"F0.wireOp",EDGE,"E3.2.2"),sQuery(id+"F0.wireOp",EDGE,"E3.2.3"),sQuery(id+"F0.wireOp",EDGE,"E3.3.1"),subQ1,subQ0,sQuery(id+"F0.wireOp",EDGE,"E3.4.1"),sQuery(id+"F0.wireOp",EDGE,"E3.4.2"),sQuery(id+"F0.wireOp",EDGE,"E3.4.3"),sQuery(id+"F0.wireOp",EDGE,"E3.5.1"),sQuery(id+"F0.wireOp",EDGE,"E3.5.2"),sQuery(id+"F0.wireOp",EDGE,"E3.5.3"),sQuery(id+"F0.wireOp",EDGE,"E3.6.1"),sQuery(id+"F0.wireOp",EDGE,"E3.6.2"),sQuery(id+"F0.wireOp",EDGE,"E3.6.3"),sQuery(id+"F0.wireOp",EDGE,"E3.7.1"),sQuery(id+"F0.wireOp",EDGE,"E3.7.2"),sQuery(id+"F0.wireOp",EDGE,"E3.7.3"),sQuery(id+"F0.wireOp",EDGE,"E3.8.1"),sQuery(id+"F0.wireOp",EDGE,"E3.8.2"),sQuery(id+"F0.wireOp",EDGE,"E3.8.3"),sQuery(id+"F0.wireOp",EDGE,"E3.9.1"),sQuery(id+"F0.wireOp",EDGE,"E3.9.2"),sQuery(id+"F0.wireOp",EDGE,"E3.9.3"),sQuery(id+"F0.wireOp",EDGE,"E3.10.1"),sQuery(id+"F0.wireOp",EDGE,"E3.10.2"),sQuery(id+"F0.wireOp",EDGE,"E3.10.3"),sQuery(id+"F0.wireOp",EDGE,"E3.11.1"),sQuery(id+"F0.wireOp",EDGE,"E3.11.2"),sQuery(id+"F0.wireOp",EDGE,"E3.11.3"),sQuery(id+"F0.wireOp",EDGE,"E3.12.1"),sQuery(id+"F0.wireOp",EDGE,"E3.12.2"),sQuery(id+"F0.wireOp",EDGE,"E3.12.3")])],"isStart":false})],"blendedInto":[makeQuery(id+"F1.opExtrude","CAP_FACE",FACE,{"disambiguationData":[OSD([sQuery(id+"F0.wireOp",EDGE,"E0"),sQuery(id+"F0.wireOp",EDGE,"E1"),sQuery(id+"F0.wireOp",EDGE,"E2.bottom"),sQuery(id+"F0.wireOp",EDGE,"E2.left"),sQuery(id+"F0.wireOp",EDGE,"E2.right"),sQuery(id+"F0.wireOp",EDGE,"E3.1.1"),sQuery(id+"F0.wireOp",EDGE,"E3.1.2"),sQuery(id+"F0.wireOp",EDGE,"E3.1.3"),sQuery(id+"F0.wireOp",EDGE,"E3.2.1"),sQuery(id+"F0.wireOp",EDGE,"E3.2.2"),sQuery(id+"F0.wireOp",EDGE,"E3.2.3"),sQuery(id+"F0.wireOp",EDGE,"E3.3.1"),subQ1,subQ0,sQuery(id+"F0.wireOp",EDGE,"E3.4.1"),sQuery(id+"F0.wireOp",EDGE,"E3.4.2"),sQuery(id+"F0.wireOp",EDGE,"E3.4.3"),sQuery(id+"F0.wireOp",EDGE,"E3.5.1"),sQuery(id+"F0.wireOp",EDGE,"E3.5.2"),sQuery(id+"F0.wireOp",EDGE,"E3.5.3"),sQuery(id+"F0.wireOp",EDGE,"E3.6.1"),sQuery(id+"F0.wireOp",EDGE,"E3.6.2"),sQuery(id+"F0.wireOp",EDGE,"E3.6.3"),sQuery(id+"F0.wireOp",EDGE,"E3.7.1"),sQuery(id+"F0.wireOp",EDGE,"E3.7.2"),sQuery(id+"F0.wireOp",EDGE,"E3.7.3"),sQuery(id+"F0.wireOp",EDGE,"E3.8.1"),sQuery(id+"F0.wireOp",EDGE,"E3.8.2"),sQuery(id+"F0.wireOp",EDGE,"E3.8.3"),sQuery(id+"F0.wireOp",EDGE,"E3.9.1"),sQuery(id+"F0.wireOp",EDGE,"E3.9.2"),sQuery(id+"F0.wireOp",EDGE,"E3.9.3"),sQuery(id+"F0.wireOp",EDGE,"E3.10.1"),sQuery(id+"F0.wireOp",EDGE,"E3.10.2"),sQuery(id+"F0.wireOp",EDGE,"E3.10.3"),sQuery(id+"F0.wireOp",EDGE,"E3.11.1"),sQuery(id+"F0.wireOp",EDGE,"E3.11.2"),sQuery(id+"F0.wireOp",EDGE,"E3.11.3"),sQuery(id+"F0.wireOp",EDGE,"E3.12.1"),sQuery(id+"F0.wireOp",EDGE,"E3.12.2"),sQuery(id+"F0.wireOp",EDGE,"E3.12.3")])],"isStart":false})]}),makeQuery(id+"F1.opExtrude","CAP_EDGE",EDGE,{"disambiguationData":[OSD([subQ0])],"isStart":false})],"blendedInto":[]});}
            var Q49;
            {var subQ0=sQuery(id+"F0.wireOp",EDGE,"E3.3.3");Q49=makeQuery(id+"F3.opChamfer","BLEND_EDGE",EDGE,{"blendedFrom":[makeQuery(id+"F1.opExtrude","SWEPT_EDGE",EDGE,{"disambiguationData":[OSD([sQuery(id+"F0.wireOp",EDGE,"E3.3.2"),subQ0])]}),makeQuery(id+"F1.opExtrude","SWEPT_FACE",FACE,{"disambiguationData":[OSD([subQ0])]})],"blendedInto":[makeQuery(id+"F1.opExtrude","SWEPT_FACE",FACE,{"disambiguationData":[OSD([subQ0])]})]});}
            var Q50;
            {var subQ0=sQuery(id+"F0.wireOp",EDGE,"E3.3.1");var subQ1=sQuery(id+"F0.wireOp",EDGE,"E3.3.2");Q50=makeQuery(id+"F4.opChamfer","BLEND_EDGE",EDGE,{"blendedFrom":[makeQuery(id+"F3.opChamfer","BLEND_EDGE",EDGE,{"blendedFrom":[makeQuery(id+"F1.opExtrude","SWEPT_EDGE",EDGE,{"disambiguationData":[OSD([subQ0,subQ1])]}),makeQuery(id+"F1.opExtrude","CAP_FACE",FACE,{"disambiguationData":[OSD([sQuery(id+"F0.wireOp",EDGE,"E0"),sQuery(id+"F0.wireOp",EDGE,"E1"),sQuery(id+"F0.wireOp",EDGE,"E2.bottom"),sQuery(id+"F0.wireOp",EDGE,"E2.left"),sQuery(id+"F0.wireOp",EDGE,"E2.right"),sQuery(id+"F0.wireOp",EDGE,"E3.1.1"),sQuery(id+"F0.wireOp",EDGE,"E3.1.2"),sQuery(id+"F0.wireOp",EDGE,"E3.1.3"),sQuery(id+"F0.wireOp",EDGE,"E3.2.1"),sQuery(id+"F0.wireOp",EDGE,"E3.2.2"),sQuery(id+"F0.wireOp",EDGE,"E3.2.3"),subQ0,subQ1,sQuery(id+"F0.wireOp",EDGE,"E3.3.3"),sQuery(id+"F0.wireOp",EDGE,"E3.4.1"),sQuery(id+"F0.wireOp",EDGE,"E3.4.2"),sQuery(id+"F0.wireOp",EDGE,"E3.4.3"),sQuery(id+"F0.wireOp",EDGE,"E3.5.1"),sQuery(id+"F0.wireOp",EDGE,"E3.5.2"),sQuery(id+"F0.wireOp",EDGE,"E3.5.3"),sQuery(id+"F0.wireOp",EDGE,"E3.6.1"),sQuery(id+"F0.wireOp",EDGE,"E3.6.2"),sQuery(id+"F0.wireOp",EDGE,"E3.6.3"),sQuery(id+"F0.wireOp",EDGE,"E3.7.1"),sQuery(id+"F0.wireOp",EDGE,"E3.7.2"),sQuery(id+"F0.wireOp",EDGE,"E3.7.3"),sQuery(id+"F0.wireOp",EDGE,"E3.8.1"),sQuery(id+"F0.wireOp",EDGE,"E3.8.2"),sQuery(id+"F0.wireOp",EDGE,"E3.8.3"),sQuery(id+"F0.wireOp",EDGE,"E3.9.1"),sQuery(id+"F0.wireOp",EDGE,"E3.9.2"),sQuery(id+"F0.wireOp",EDGE,"E3.9.3"),sQuery(id+"F0.wireOp",EDGE,"E3.10.1"),sQuery(id+"F0.wireOp",EDGE,"E3.10.2"),sQuery(id+"F0.wireOp",EDGE,"E3.10.3"),sQuery(id+"F0.wireOp",EDGE,"E3.11.1"),sQuery(id+"F0.wireOp",EDGE,"E3.11.2"),sQuery(id+"F0.wireOp",EDGE,"E3.11.3"),sQuery(id+"F0.wireOp",EDGE,"E3.12.1"),sQuery(id+"F0.wireOp",EDGE,"E3.12.2"),sQuery(id+"F0.wireOp",EDGE,"E3.12.3")])],"isStart":false})],"blendedInto":[makeQuery(id+"F1.opExtrude","CAP_FACE",FACE,{"disambiguationData":[OSD([sQuery(id+"F0.wireOp",EDGE,"E0"),sQuery(id+"F0.wireOp",EDGE,"E1"),sQuery(id+"F0.wireOp",EDGE,"E2.bottom"),sQuery(id+"F0.wireOp",EDGE,"E2.left"),sQuery(id+"F0.wireOp",EDGE,"E2.right"),sQuery(id+"F0.wireOp",EDGE,"E3.1.1"),sQuery(id+"F0.wireOp",EDGE,"E3.1.2"),sQuery(id+"F0.wireOp",EDGE,"E3.1.3"),sQuery(id+"F0.wireOp",EDGE,"E3.2.1"),sQuery(id+"F0.wireOp",EDGE,"E3.2.2"),sQuery(id+"F0.wireOp",EDGE,"E3.2.3"),subQ0,subQ1,sQuery(id+"F0.wireOp",EDGE,"E3.3.3"),sQuery(id+"F0.wireOp",EDGE,"E3.4.1"),sQuery(id+"F0.wireOp",EDGE,"E3.4.2"),sQuery(id+"F0.wireOp",EDGE,"E3.4.3"),sQuery(id+"F0.wireOp",EDGE,"E3.5.1"),sQuery(id+"F0.wireOp",EDGE,"E3.5.2"),sQuery(id+"F0.wireOp",EDGE,"E3.5.3"),sQuery(id+"F0.wireOp",EDGE,"E3.6.1"),sQuery(id+"F0.wireOp",EDGE,"E3.6.2"),sQuery(id+"F0.wireOp",EDGE,"E3.6.3"),sQuery(id+"F0.wireOp",EDGE,"E3.7.1"),sQuery(id+"F0.wireOp",EDGE,"E3.7.2"),sQuery(id+"F0.wireOp",EDGE,"E3.7.3"),sQuery(id+"F0.wireOp",EDGE,"E3.8.1"),sQuery(id+"F0.wireOp",EDGE,"E3.8.2"),sQuery(id+"F0.wireOp",EDGE,"E3.8.3"),sQuery(id+"F0.wireOp",EDGE,"E3.9.1"),sQuery(id+"F0.wireOp",EDGE,"E3.9.2"),sQuery(id+"F0.wireOp",EDGE,"E3.9.3"),sQuery(id+"F0.wireOp",EDGE,"E3.10.1"),sQuery(id+"F0.wireOp",EDGE,"E3.10.2"),sQuery(id+"F0.wireOp",EDGE,"E3.10.3"),sQuery(id+"F0.wireOp",EDGE,"E3.11.1"),sQuery(id+"F0.wireOp",EDGE,"E3.11.2"),sQuery(id+"F0.wireOp",EDGE,"E3.11.3"),sQuery(id+"F0.wireOp",EDGE,"E3.12.1"),sQuery(id+"F0.wireOp",EDGE,"E3.12.2"),sQuery(id+"F0.wireOp",EDGE,"E3.12.3")])],"isStart":false})]}),makeQuery(id+"F1.opExtrude","CAP_EDGE",EDGE,{"disambiguationData":[OSD([subQ0])],"isStart":false})],"blendedInto":[]});}
            var Q51;
            {var subQ0=sQuery(id+"F0.wireOp",EDGE,"E3.8.3");var subQ1=sQuery(id+"F0.wireOp",EDGE,"E3.8.2");Q51=makeQuery(id+"F4.opChamfer","BLEND_EDGE",EDGE,{"blendedFrom":[makeQuery(id+"F3.opChamfer","BLEND_EDGE",EDGE,{"blendedFrom":[makeQuery(id+"F1.opExtrude","SWEPT_EDGE",EDGE,{"disambiguationData":[OSD([subQ1,subQ0])]}),makeQuery(id+"F1.opExtrude","CAP_FACE",FACE,{"disambiguationData":[OSD([sQuery(id+"F0.wireOp",EDGE,"E0"),sQuery(id+"F0.wireOp",EDGE,"E1"),sQuery(id+"F0.wireOp",EDGE,"E2.bottom"),sQuery(id+"F0.wireOp",EDGE,"E2.left"),sQuery(id+"F0.wireOp",EDGE,"E2.right"),sQuery(id+"F0.wireOp",EDGE,"E3.1.1"),sQuery(id+"F0.wireOp",EDGE,"E3.1.2"),sQuery(id+"F0.wireOp",EDGE,"E3.1.3"),sQuery(id+"F0.wireOp",EDGE,"E3.2.1"),sQuery(id+"F0.wireOp",EDGE,"E3.2.2"),sQuery(id+"F0.wireOp",EDGE,"E3.2.3"),sQuery(id+"F0.wireOp",EDGE,"E3.3.1"),sQuery(id+"F0.wireOp",EDGE,"E3.3.2"),sQuery(id+"F0.wireOp",EDGE,"E3.3.3"),sQuery(id+"F0.wireOp",EDGE,"E3.4.1"),sQuery(id+"F0.wireOp",EDGE,"E3.4.2"),sQuery(id+"F0.wireOp",EDGE,"E3.4.3"),sQuery(id+"F0.wireOp",EDGE,"E3.5.1"),sQuery(id+"F0.wireOp",EDGE,"E3.5.2"),sQuery(id+"F0.wireOp",EDGE,"E3.5.3"),sQuery(id+"F0.wireOp",EDGE,"E3.6.1"),sQuery(id+"F0.wireOp",EDGE,"E3.6.2"),sQuery(id+"F0.wireOp",EDGE,"E3.6.3"),sQuery(id+"F0.wireOp",EDGE,"E3.7.1"),sQuery(id+"F0.wireOp",EDGE,"E3.7.2"),sQuery(id+"F0.wireOp",EDGE,"E3.7.3"),sQuery(id+"F0.wireOp",EDGE,"E3.8.1"),subQ1,subQ0,sQuery(id+"F0.wireOp",EDGE,"E3.9.1"),sQuery(id+"F0.wireOp",EDGE,"E3.9.2"),sQuery(id+"F0.wireOp",EDGE,"E3.9.3"),sQuery(id+"F0.wireOp",EDGE,"E3.10.1"),sQuery(id+"F0.wireOp",EDGE,"E3.10.2"),sQuery(id+"F0.wireOp",EDGE,"E3.10.3"),sQuery(id+"F0.wireOp",EDGE,"E3.11.1"),sQuery(id+"F0.wireOp",EDGE,"E3.11.2"),sQuery(id+"F0.wireOp",EDGE,"E3.11.3"),sQuery(id+"F0.wireOp",EDGE,"E3.12.1"),sQuery(id+"F0.wireOp",EDGE,"E3.12.2"),sQuery(id+"F0.wireOp",EDGE,"E3.12.3")])],"isStart":false})],"blendedInto":[makeQuery(id+"F1.opExtrude","CAP_FACE",FACE,{"disambiguationData":[OSD([sQuery(id+"F0.wireOp",EDGE,"E0"),sQuery(id+"F0.wireOp",EDGE,"E1"),sQuery(id+"F0.wireOp",EDGE,"E2.bottom"),sQuery(id+"F0.wireOp",EDGE,"E2.left"),sQuery(id+"F0.wireOp",EDGE,"E2.right"),sQuery(id+"F0.wireOp",EDGE,"E3.1.1"),sQuery(id+"F0.wireOp",EDGE,"E3.1.2"),sQuery(id+"F0.wireOp",EDGE,"E3.1.3"),sQuery(id+"F0.wireOp",EDGE,"E3.2.1"),sQuery(id+"F0.wireOp",EDGE,"E3.2.2"),sQuery(id+"F0.wireOp",EDGE,"E3.2.3"),sQuery(id+"F0.wireOp",EDGE,"E3.3.1"),sQuery(id+"F0.wireOp",EDGE,"E3.3.2"),sQuery(id+"F0.wireOp",EDGE,"E3.3.3"),sQuery(id+"F0.wireOp",EDGE,"E3.4.1"),sQuery(id+"F0.wireOp",EDGE,"E3.4.2"),sQuery(id+"F0.wireOp",EDGE,"E3.4.3"),sQuery(id+"F0.wireOp",EDGE,"E3.5.1"),sQuery(id+"F0.wireOp",EDGE,"E3.5.2"),sQuery(id+"F0.wireOp",EDGE,"E3.5.3"),sQuery(id+"F0.wireOp",EDGE,"E3.6.1"),sQuery(id+"F0.wireOp",EDGE,"E3.6.2"),sQuery(id+"F0.wireOp",EDGE,"E3.6.3"),sQuery(id+"F0.wireOp",EDGE,"E3.7.1"),sQuery(id+"F0.wireOp",EDGE,"E3.7.2"),sQuery(id+"F0.wireOp",EDGE,"E3.7.3"),sQuery(id+"F0.wireOp",EDGE,"E3.8.1"),subQ1,subQ0,sQuery(id+"F0.wireOp",EDGE,"E3.9.1"),sQuery(id+"F0.wireOp",EDGE,"E3.9.2"),sQuery(id+"F0.wireOp",EDGE,"E3.9.3"),sQuery(id+"F0.wireOp",EDGE,"E3.10.1"),sQuery(id+"F0.wireOp",EDGE,"E3.10.2"),sQuery(id+"F0.wireOp",EDGE,"E3.10.3"),sQuery(id+"F0.wireOp",EDGE,"E3.11.1"),sQuery(id+"F0.wireOp",EDGE,"E3.11.2"),sQuery(id+"F0.wireOp",EDGE,"E3.11.3"),sQuery(id+"F0.wireOp",EDGE,"E3.12.1"),sQuery(id+"F0.wireOp",EDGE,"E3.12.2"),sQuery(id+"F0.wireOp",EDGE,"E3.12.3")])],"isStart":false})]}),makeQuery(id+"F1.opExtrude","CAP_EDGE",EDGE,{"disambiguationData":[OSD([subQ0])],"isStart":false})],"blendedInto":[]});}
            var Q52;
            {var subQ0=sQuery(id+"F0.wireOp",EDGE,"E3.7.3");var subQ1=sQuery(id+"F0.wireOp",EDGE,"E3.7.2");Q52=makeQuery(id+"F4.opChamfer","BLEND_EDGE",EDGE,{"blendedFrom":[makeQuery(id+"F3.opChamfer","BLEND_EDGE",EDGE,{"blendedFrom":[makeQuery(id+"F1.opExtrude","SWEPT_EDGE",EDGE,{"disambiguationData":[OSD([subQ1,subQ0])]}),makeQuery(id+"F1.opExtrude","CAP_FACE",FACE,{"disambiguationData":[OSD([sQuery(id+"F0.wireOp",EDGE,"E0"),sQuery(id+"F0.wireOp",EDGE,"E1"),sQuery(id+"F0.wireOp",EDGE,"E2.bottom"),sQuery(id+"F0.wireOp",EDGE,"E2.left"),sQuery(id+"F0.wireOp",EDGE,"E2.right"),sQuery(id+"F0.wireOp",EDGE,"E3.1.1"),sQuery(id+"F0.wireOp",EDGE,"E3.1.2"),sQuery(id+"F0.wireOp",EDGE,"E3.1.3"),sQuery(id+"F0.wireOp",EDGE,"E3.2.1"),sQuery(id+"F0.wireOp",EDGE,"E3.2.2"),sQuery(id+"F0.wireOp",EDGE,"E3.2.3"),sQuery(id+"F0.wireOp",EDGE,"E3.3.1"),sQuery(id+"F0.wireOp",EDGE,"E3.3.2"),sQuery(id+"F0.wireOp",EDGE,"E3.3.3"),sQuery(id+"F0.wireOp",EDGE,"E3.4.1"),sQuery(id+"F0.wireOp",EDGE,"E3.4.2"),sQuery(id+"F0.wireOp",EDGE,"E3.4.3"),sQuery(id+"F0.wireOp",EDGE,"E3.5.1"),sQuery(id+"F0.wireOp",EDGE,"E3.5.2"),sQuery(id+"F0.wireOp",EDGE,"E3.5.3"),sQuery(id+"F0.wireOp",EDGE,"E3.6.1"),sQuery(id+"F0.wireOp",EDGE,"E3.6.2"),sQuery(id+"F0.wireOp",EDGE,"E3.6.3"),sQuery(id+"F0.wireOp",EDGE,"E3.7.1"),subQ1,subQ0,sQuery(id+"F0.wireOp",EDGE,"E3.8.1"),sQuery(id+"F0.wireOp",EDGE,"E3.8.2"),sQuery(id+"F0.wireOp",EDGE,"E3.8.3"),sQuery(id+"F0.wireOp",EDGE,"E3.9.1"),sQuery(id+"F0.wireOp",EDGE,"E3.9.2"),sQuery(id+"F0.wireOp",EDGE,"E3.9.3"),sQuery(id+"F0.wireOp",EDGE,"E3.10.1"),sQuery(id+"F0.wireOp",EDGE,"E3.10.2"),sQuery(id+"F0.wireOp",EDGE,"E3.10.3"),sQuery(id+"F0.wireOp",EDGE,"E3.11.1"),sQuery(id+"F0.wireOp",EDGE,"E3.11.2"),sQuery(id+"F0.wireOp",EDGE,"E3.11.3"),sQuery(id+"F0.wireOp",EDGE,"E3.12.1"),sQuery(id+"F0.wireOp",EDGE,"E3.12.2"),sQuery(id+"F0.wireOp",EDGE,"E3.12.3")])],"isStart":false})],"blendedInto":[makeQuery(id+"F1.opExtrude","CAP_FACE",FACE,{"disambiguationData":[OSD([sQuery(id+"F0.wireOp",EDGE,"E0"),sQuery(id+"F0.wireOp",EDGE,"E1"),sQuery(id+"F0.wireOp",EDGE,"E2.bottom"),sQuery(id+"F0.wireOp",EDGE,"E2.left"),sQuery(id+"F0.wireOp",EDGE,"E2.right"),sQuery(id+"F0.wireOp",EDGE,"E3.1.1"),sQuery(id+"F0.wireOp",EDGE,"E3.1.2"),sQuery(id+"F0.wireOp",EDGE,"E3.1.3"),sQuery(id+"F0.wireOp",EDGE,"E3.2.1"),sQuery(id+"F0.wireOp",EDGE,"E3.2.2"),sQuery(id+"F0.wireOp",EDGE,"E3.2.3"),sQuery(id+"F0.wireOp",EDGE,"E3.3.1"),sQuery(id+"F0.wireOp",EDGE,"E3.3.2"),sQuery(id+"F0.wireOp",EDGE,"E3.3.3"),sQuery(id+"F0.wireOp",EDGE,"E3.4.1"),sQuery(id+"F0.wireOp",EDGE,"E3.4.2"),sQuery(id+"F0.wireOp",EDGE,"E3.4.3"),sQuery(id+"F0.wireOp",EDGE,"E3.5.1"),sQuery(id+"F0.wireOp",EDGE,"E3.5.2"),sQuery(id+"F0.wireOp",EDGE,"E3.5.3"),sQuery(id+"F0.wireOp",EDGE,"E3.6.1"),sQuery(id+"F0.wireOp",EDGE,"E3.6.2"),sQuery(id+"F0.wireOp",EDGE,"E3.6.3"),sQuery(id+"F0.wireOp",EDGE,"E3.7.1"),subQ1,subQ0,sQuery(id+"F0.wireOp",EDGE,"E3.8.1"),sQuery(id+"F0.wireOp",EDGE,"E3.8.2"),sQuery(id+"F0.wireOp",EDGE,"E3.8.3"),sQuery(id+"F0.wireOp",EDGE,"E3.9.1"),sQuery(id+"F0.wireOp",EDGE,"E3.9.2"),sQuery(id+"F0.wireOp",EDGE,"E3.9.3"),sQuery(id+"F0.wireOp",EDGE,"E3.10.1"),sQuery(id+"F0.wireOp",EDGE,"E3.10.2"),sQuery(id+"F0.wireOp",EDGE,"E3.10.3"),sQuery(id+"F0.wireOp",EDGE,"E3.11.1"),sQuery(id+"F0.wireOp",EDGE,"E3.11.2"),sQuery(id+"F0.wireOp",EDGE,"E3.11.3"),sQuery(id+"F0.wireOp",EDGE,"E3.12.1"),sQuery(id+"F0.wireOp",EDGE,"E3.12.2"),sQuery(id+"F0.wireOp",EDGE,"E3.12.3")])],"isStart":false})]}),makeQuery(id+"F1.opExtrude","CAP_EDGE",EDGE,{"disambiguationData":[OSD([subQ0])],"isStart":false})],"blendedInto":[]});}
            var Q53;
            {var subQ0=sQuery(id+"F0.wireOp",EDGE,"E3.7.1");var subQ1=sQuery(id+"F0.wireOp",EDGE,"E3.7.2");Q53=makeQuery(id+"F4.opChamfer","BLEND_EDGE",EDGE,{"blendedFrom":[makeQuery(id+"F3.opChamfer","BLEND_EDGE",EDGE,{"blendedFrom":[makeQuery(id+"F1.opExtrude","SWEPT_EDGE",EDGE,{"disambiguationData":[OSD([subQ0,subQ1])]}),makeQuery(id+"F1.opExtrude","CAP_FACE",FACE,{"disambiguationData":[OSD([sQuery(id+"F0.wireOp",EDGE,"E0"),sQuery(id+"F0.wireOp",EDGE,"E1"),sQuery(id+"F0.wireOp",EDGE,"E2.bottom"),sQuery(id+"F0.wireOp",EDGE,"E2.left"),sQuery(id+"F0.wireOp",EDGE,"E2.right"),sQuery(id+"F0.wireOp",EDGE,"E3.1.1"),sQuery(id+"F0.wireOp",EDGE,"E3.1.2"),sQuery(id+"F0.wireOp",EDGE,"E3.1.3"),sQuery(id+"F0.wireOp",EDGE,"E3.2.1"),sQuery(id+"F0.wireOp",EDGE,"E3.2.2"),sQuery(id+"F0.wireOp",EDGE,"E3.2.3"),sQuery(id+"F0.wireOp",EDGE,"E3.3.1"),sQuery(id+"F0.wireOp",EDGE,"E3.3.2"),sQuery(id+"F0.wireOp",EDGE,"E3.3.3"),sQuery(id+"F0.wireOp",EDGE,"E3.4.1"),sQuery(id+"F0.wireOp",EDGE,"E3.4.2"),sQuery(id+"F0.wireOp",EDGE,"E3.4.3"),sQuery(id+"F0.wireOp",EDGE,"E3.5.1"),sQuery(id+"F0.wireOp",EDGE,"E3.5.2"),sQuery(id+"F0.wireOp",EDGE,"E3.5.3"),sQuery(id+"F0.wireOp",EDGE,"E3.6.1"),sQuery(id+"F0.wireOp",EDGE,"E3.6.2"),sQuery(id+"F0.wireOp",EDGE,"E3.6.3"),subQ0,subQ1,sQuery(id+"F0.wireOp",EDGE,"E3.7.3"),sQuery(id+"F0.wireOp",EDGE,"E3.8.1"),sQuery(id+"F0.wireOp",EDGE,"E3.8.2"),sQuery(id+"F0.wireOp",EDGE,"E3.8.3"),sQuery(id+"F0.wireOp",EDGE,"E3.9.1"),sQuery(id+"F0.wireOp",EDGE,"E3.9.2"),sQuery(id+"F0.wireOp",EDGE,"E3.9.3"),sQuery(id+"F0.wireOp",EDGE,"E3.10.1"),sQuery(id+"F0.wireOp",EDGE,"E3.10.2"),sQuery(id+"F0.wireOp",EDGE,"E3.10.3"),sQuery(id+"F0.wireOp",EDGE,"E3.11.1"),sQuery(id+"F0.wireOp",EDGE,"E3.11.2"),sQuery(id+"F0.wireOp",EDGE,"E3.11.3"),sQuery(id+"F0.wireOp",EDGE,"E3.12.1"),sQuery(id+"F0.wireOp",EDGE,"E3.12.2"),sQuery(id+"F0.wireOp",EDGE,"E3.12.3")])],"isStart":false})],"blendedInto":[makeQuery(id+"F1.opExtrude","CAP_FACE",FACE,{"disambiguationData":[OSD([sQuery(id+"F0.wireOp",EDGE,"E0"),sQuery(id+"F0.wireOp",EDGE,"E1"),sQuery(id+"F0.wireOp",EDGE,"E2.bottom"),sQuery(id+"F0.wireOp",EDGE,"E2.left"),sQuery(id+"F0.wireOp",EDGE,"E2.right"),sQuery(id+"F0.wireOp",EDGE,"E3.1.1"),sQuery(id+"F0.wireOp",EDGE,"E3.1.2"),sQuery(id+"F0.wireOp",EDGE,"E3.1.3"),sQuery(id+"F0.wireOp",EDGE,"E3.2.1"),sQuery(id+"F0.wireOp",EDGE,"E3.2.2"),sQuery(id+"F0.wireOp",EDGE,"E3.2.3"),sQuery(id+"F0.wireOp",EDGE,"E3.3.1"),sQuery(id+"F0.wireOp",EDGE,"E3.3.2"),sQuery(id+"F0.wireOp",EDGE,"E3.3.3"),sQuery(id+"F0.wireOp",EDGE,"E3.4.1"),sQuery(id+"F0.wireOp",EDGE,"E3.4.2"),sQuery(id+"F0.wireOp",EDGE,"E3.4.3"),sQuery(id+"F0.wireOp",EDGE,"E3.5.1"),sQuery(id+"F0.wireOp",EDGE,"E3.5.2"),sQuery(id+"F0.wireOp",EDGE,"E3.5.3"),sQuery(id+"F0.wireOp",EDGE,"E3.6.1"),sQuery(id+"F0.wireOp",EDGE,"E3.6.2"),sQuery(id+"F0.wireOp",EDGE,"E3.6.3"),subQ0,subQ1,sQuery(id+"F0.wireOp",EDGE,"E3.7.3"),sQuery(id+"F0.wireOp",EDGE,"E3.8.1"),sQuery(id+"F0.wireOp",EDGE,"E3.8.2"),sQuery(id+"F0.wireOp",EDGE,"E3.8.3"),sQuery(id+"F0.wireOp",EDGE,"E3.9.1"),sQuery(id+"F0.wireOp",EDGE,"E3.9.2"),sQuery(id+"F0.wireOp",EDGE,"E3.9.3"),sQuery(id+"F0.wireOp",EDGE,"E3.10.1"),sQuery(id+"F0.wireOp",EDGE,"E3.10.2"),sQuery(id+"F0.wireOp",EDGE,"E3.10.3"),sQuery(id+"F0.wireOp",EDGE,"E3.11.1"),sQuery(id+"F0.wireOp",EDGE,"E3.11.2"),sQuery(id+"F0.wireOp",EDGE,"E3.11.3"),sQuery(id+"F0.wireOp",EDGE,"E3.12.1"),sQuery(id+"F0.wireOp",EDGE,"E3.12.2"),sQuery(id+"F0.wireOp",EDGE,"E3.12.3")])],"isStart":false})]}),makeQuery(id+"F1.opExtrude","CAP_EDGE",EDGE,{"disambiguationData":[OSD([subQ0])],"isStart":false})],"blendedInto":[]});}
            var Q54;
            {var subQ0=sQuery(id+"F0.wireOp",EDGE,"E3.7.1");Q54=makeQuery(id+"F3.opChamfer","BLEND_EDGE",EDGE,{"blendedFrom":[makeQuery(id+"F1.opExtrude","SWEPT_EDGE",EDGE,{"disambiguationData":[OSD([subQ0,sQuery(id+"F0.wireOp",EDGE,"E3.7.2")])]}),makeQuery(id+"F1.opExtrude","SWEPT_FACE",FACE,{"disambiguationData":[OSD([subQ0])]})],"blendedInto":[makeQuery(id+"F1.opExtrude","SWEPT_FACE",FACE,{"disambiguationData":[OSD([subQ0])]})]});}
            var Q55;
            {var subQ0=sQuery(id+"F0.wireOp",EDGE,"E3.7.3");Q55=makeQuery(id+"F3.opChamfer","BLEND_EDGE",EDGE,{"blendedFrom":[makeQuery(id+"F1.opExtrude","SWEPT_EDGE",EDGE,{"disambiguationData":[OSD([sQuery(id+"F0.wireOp",EDGE,"E3.7.2"),subQ0])]}),makeQuery(id+"F1.opExtrude","SWEPT_FACE",FACE,{"disambiguationData":[OSD([subQ0])]})],"blendedInto":[makeQuery(id+"F1.opExtrude","SWEPT_FACE",FACE,{"disambiguationData":[OSD([subQ0])]})]});}
            var Q56;
            {var subQ0=sQuery(id+"F0.wireOp",EDGE,"E3.7.3");var subQ1=sQuery(id+"F0.wireOp",EDGE,"E3.7.2");Q56=makeQuery(id+"F4.opChamfer","BLEND_EDGE",EDGE,{"blendedFrom":[makeQuery(id+"F3.opChamfer","BLEND_EDGE",EDGE,{"blendedFrom":[makeQuery(id+"F1.opExtrude","SWEPT_EDGE",EDGE,{"disambiguationData":[OSD([subQ1,subQ0])]}),makeQuery(id+"F1.opExtrude","CAP_FACE",FACE,{"disambiguationData":[OSD([sQuery(id+"F0.wireOp",EDGE,"E0"),sQuery(id+"F0.wireOp",EDGE,"E1"),sQuery(id+"F0.wireOp",EDGE,"E2.bottom"),sQuery(id+"F0.wireOp",EDGE,"E2.left"),sQuery(id+"F0.wireOp",EDGE,"E2.right"),sQuery(id+"F0.wireOp",EDGE,"E3.1.1"),sQuery(id+"F0.wireOp",EDGE,"E3.1.2"),sQuery(id+"F0.wireOp",EDGE,"E3.1.3"),sQuery(id+"F0.wireOp",EDGE,"E3.2.1"),sQuery(id+"F0.wireOp",EDGE,"E3.2.2"),sQuery(id+"F0.wireOp",EDGE,"E3.2.3"),sQuery(id+"F0.wireOp",EDGE,"E3.3.1"),sQuery(id+"F0.wireOp",EDGE,"E3.3.2"),sQuery(id+"F0.wireOp",EDGE,"E3.3.3"),sQuery(id+"F0.wireOp",EDGE,"E3.4.1"),sQuery(id+"F0.wireOp",EDGE,"E3.4.2"),sQuery(id+"F0.wireOp",EDGE,"E3.4.3"),sQuery(id+"F0.wireOp",EDGE,"E3.5.1"),sQuery(id+"F0.wireOp",EDGE,"E3.5.2"),sQuery(id+"F0.wireOp",EDGE,"E3.5.3"),sQuery(id+"F0.wireOp",EDGE,"E3.6.1"),sQuery(id+"F0.wireOp",EDGE,"E3.6.2"),sQuery(id+"F0.wireOp",EDGE,"E3.6.3"),sQuery(id+"F0.wireOp",EDGE,"E3.7.1"),subQ1,subQ0,sQuery(id+"F0.wireOp",EDGE,"E3.8.1"),sQuery(id+"F0.wireOp",EDGE,"E3.8.2"),sQuery(id+"F0.wireOp",EDGE,"E3.8.3"),sQuery(id+"F0.wireOp",EDGE,"E3.9.1"),sQuery(id+"F0.wireOp",EDGE,"E3.9.2"),sQuery(id+"F0.wireOp",EDGE,"E3.9.3"),sQuery(id+"F0.wireOp",EDGE,"E3.10.1"),sQuery(id+"F0.wireOp",EDGE,"E3.10.2"),sQuery(id+"F0.wireOp",EDGE,"E3.10.3"),sQuery(id+"F0.wireOp",EDGE,"E3.11.1"),sQuery(id+"F0.wireOp",EDGE,"E3.11.2"),sQuery(id+"F0.wireOp",EDGE,"E3.11.3"),sQuery(id+"F0.wireOp",EDGE,"E3.12.1"),sQuery(id+"F0.wireOp",EDGE,"E3.12.2"),sQuery(id+"F0.wireOp",EDGE,"E3.12.3")])],"isStart":true})],"blendedInto":[makeQuery(id+"F1.opExtrude","CAP_FACE",FACE,{"disambiguationData":[OSD([sQuery(id+"F0.wireOp",EDGE,"E0"),sQuery(id+"F0.wireOp",EDGE,"E1"),sQuery(id+"F0.wireOp",EDGE,"E2.bottom"),sQuery(id+"F0.wireOp",EDGE,"E2.left"),sQuery(id+"F0.wireOp",EDGE,"E2.right"),sQuery(id+"F0.wireOp",EDGE,"E3.1.1"),sQuery(id+"F0.wireOp",EDGE,"E3.1.2"),sQuery(id+"F0.wireOp",EDGE,"E3.1.3"),sQuery(id+"F0.wireOp",EDGE,"E3.2.1"),sQuery(id+"F0.wireOp",EDGE,"E3.2.2"),sQuery(id+"F0.wireOp",EDGE,"E3.2.3"),sQuery(id+"F0.wireOp",EDGE,"E3.3.1"),sQuery(id+"F0.wireOp",EDGE,"E3.3.2"),sQuery(id+"F0.wireOp",EDGE,"E3.3.3"),sQuery(id+"F0.wireOp",EDGE,"E3.4.1"),sQuery(id+"F0.wireOp",EDGE,"E3.4.2"),sQuery(id+"F0.wireOp",EDGE,"E3.4.3"),sQuery(id+"F0.wireOp",EDGE,"E3.5.1"),sQuery(id+"F0.wireOp",EDGE,"E3.5.2"),sQuery(id+"F0.wireOp",EDGE,"E3.5.3"),sQuery(id+"F0.wireOp",EDGE,"E3.6.1"),sQuery(id+"F0.wireOp",EDGE,"E3.6.2"),sQuery(id+"F0.wireOp",EDGE,"E3.6.3"),sQuery(id+"F0.wireOp",EDGE,"E3.7.1"),subQ1,subQ0,sQuery(id+"F0.wireOp",EDGE,"E3.8.1"),sQuery(id+"F0.wireOp",EDGE,"E3.8.2"),sQuery(id+"F0.wireOp",EDGE,"E3.8.3"),sQuery(id+"F0.wireOp",EDGE,"E3.9.1"),sQuery(id+"F0.wireOp",EDGE,"E3.9.2"),sQuery(id+"F0.wireOp",EDGE,"E3.9.3"),sQuery(id+"F0.wireOp",EDGE,"E3.10.1"),sQuery(id+"F0.wireOp",EDGE,"E3.10.2"),sQuery(id+"F0.wireOp",EDGE,"E3.10.3"),sQuery(id+"F0.wireOp",EDGE,"E3.11.1"),sQuery(id+"F0.wireOp",EDGE,"E3.11.2"),sQuery(id+"F0.wireOp",EDGE,"E3.11.3"),sQuery(id+"F0.wireOp",EDGE,"E3.12.1"),sQuery(id+"F0.wireOp",EDGE,"E3.12.2"),sQuery(id+"F0.wireOp",EDGE,"E3.12.3")])],"isStart":true})]}),makeQuery(id+"F1.opExtrude","CAP_EDGE",EDGE,{"disambiguationData":[OSD([subQ0])],"isStart":true})],"blendedInto":[]});}
            var Q57;
            {var subQ0=sQuery(id+"F0.wireOp",EDGE,"E3.7.1");var subQ1=sQuery(id+"F0.wireOp",EDGE,"E3.7.2");Q57=makeQuery(id+"F4.opChamfer","BLEND_EDGE",EDGE,{"blendedFrom":[makeQuery(id+"F3.opChamfer","BLEND_EDGE",EDGE,{"blendedFrom":[makeQuery(id+"F1.opExtrude","SWEPT_EDGE",EDGE,{"disambiguationData":[OSD([subQ0,subQ1])]}),makeQuery(id+"F1.opExtrude","CAP_FACE",FACE,{"disambiguationData":[OSD([sQuery(id+"F0.wireOp",EDGE,"E0"),sQuery(id+"F0.wireOp",EDGE,"E1"),sQuery(id+"F0.wireOp",EDGE,"E2.bottom"),sQuery(id+"F0.wireOp",EDGE,"E2.left"),sQuery(id+"F0.wireOp",EDGE,"E2.right"),sQuery(id+"F0.wireOp",EDGE,"E3.1.1"),sQuery(id+"F0.wireOp",EDGE,"E3.1.2"),sQuery(id+"F0.wireOp",EDGE,"E3.1.3"),sQuery(id+"F0.wireOp",EDGE,"E3.2.1"),sQuery(id+"F0.wireOp",EDGE,"E3.2.2"),sQuery(id+"F0.wireOp",EDGE,"E3.2.3"),sQuery(id+"F0.wireOp",EDGE,"E3.3.1"),sQuery(id+"F0.wireOp",EDGE,"E3.3.2"),sQuery(id+"F0.wireOp",EDGE,"E3.3.3"),sQuery(id+"F0.wireOp",EDGE,"E3.4.1"),sQuery(id+"F0.wireOp",EDGE,"E3.4.2"),sQuery(id+"F0.wireOp",EDGE,"E3.4.3"),sQuery(id+"F0.wireOp",EDGE,"E3.5.1"),sQuery(id+"F0.wireOp",EDGE,"E3.5.2"),sQuery(id+"F0.wireOp",EDGE,"E3.5.3"),sQuery(id+"F0.wireOp",EDGE,"E3.6.1"),sQuery(id+"F0.wireOp",EDGE,"E3.6.2"),sQuery(id+"F0.wireOp",EDGE,"E3.6.3"),subQ0,subQ1,sQuery(id+"F0.wireOp",EDGE,"E3.7.3"),sQuery(id+"F0.wireOp",EDGE,"E3.8.1"),sQuery(id+"F0.wireOp",EDGE,"E3.8.2"),sQuery(id+"F0.wireOp",EDGE,"E3.8.3"),sQuery(id+"F0.wireOp",EDGE,"E3.9.1"),sQuery(id+"F0.wireOp",EDGE,"E3.9.2"),sQuery(id+"F0.wireOp",EDGE,"E3.9.3"),sQuery(id+"F0.wireOp",EDGE,"E3.10.1"),sQuery(id+"F0.wireOp",EDGE,"E3.10.2"),sQuery(id+"F0.wireOp",EDGE,"E3.10.3"),sQuery(id+"F0.wireOp",EDGE,"E3.11.1"),sQuery(id+"F0.wireOp",EDGE,"E3.11.2"),sQuery(id+"F0.wireOp",EDGE,"E3.11.3"),sQuery(id+"F0.wireOp",EDGE,"E3.12.1"),sQuery(id+"F0.wireOp",EDGE,"E3.12.2"),sQuery(id+"F0.wireOp",EDGE,"E3.12.3")])],"isStart":true})],"blendedInto":[makeQuery(id+"F1.opExtrude","CAP_FACE",FACE,{"disambiguationData":[OSD([sQuery(id+"F0.wireOp",EDGE,"E0"),sQuery(id+"F0.wireOp",EDGE,"E1"),sQuery(id+"F0.wireOp",EDGE,"E2.bottom"),sQuery(id+"F0.wireOp",EDGE,"E2.left"),sQuery(id+"F0.wireOp",EDGE,"E2.right"),sQuery(id+"F0.wireOp",EDGE,"E3.1.1"),sQuery(id+"F0.wireOp",EDGE,"E3.1.2"),sQuery(id+"F0.wireOp",EDGE,"E3.1.3"),sQuery(id+"F0.wireOp",EDGE,"E3.2.1"),sQuery(id+"F0.wireOp",EDGE,"E3.2.2"),sQuery(id+"F0.wireOp",EDGE,"E3.2.3"),sQuery(id+"F0.wireOp",EDGE,"E3.3.1"),sQuery(id+"F0.wireOp",EDGE,"E3.3.2"),sQuery(id+"F0.wireOp",EDGE,"E3.3.3"),sQuery(id+"F0.wireOp",EDGE,"E3.4.1"),sQuery(id+"F0.wireOp",EDGE,"E3.4.2"),sQuery(id+"F0.wireOp",EDGE,"E3.4.3"),sQuery(id+"F0.wireOp",EDGE,"E3.5.1"),sQuery(id+"F0.wireOp",EDGE,"E3.5.2"),sQuery(id+"F0.wireOp",EDGE,"E3.5.3"),sQuery(id+"F0.wireOp",EDGE,"E3.6.1"),sQuery(id+"F0.wireOp",EDGE,"E3.6.2"),sQuery(id+"F0.wireOp",EDGE,"E3.6.3"),subQ0,subQ1,sQuery(id+"F0.wireOp",EDGE,"E3.7.3"),sQuery(id+"F0.wireOp",EDGE,"E3.8.1"),sQuery(id+"F0.wireOp",EDGE,"E3.8.2"),sQuery(id+"F0.wireOp",EDGE,"E3.8.3"),sQuery(id+"F0.wireOp",EDGE,"E3.9.1"),sQuery(id+"F0.wireOp",EDGE,"E3.9.2"),sQuery(id+"F0.wireOp",EDGE,"E3.9.3"),sQuery(id+"F0.wireOp",EDGE,"E3.10.1"),sQuery(id+"F0.wireOp",EDGE,"E3.10.2"),sQuery(id+"F0.wireOp",EDGE,"E3.10.3"),sQuery(id+"F0.wireOp",EDGE,"E3.11.1"),sQuery(id+"F0.wireOp",EDGE,"E3.11.2"),sQuery(id+"F0.wireOp",EDGE,"E3.11.3"),sQuery(id+"F0.wireOp",EDGE,"E3.12.1"),sQuery(id+"F0.wireOp",EDGE,"E3.12.2"),sQuery(id+"F0.wireOp",EDGE,"E3.12.3")])],"isStart":true})]}),makeQuery(id+"F1.opExtrude","CAP_EDGE",EDGE,{"disambiguationData":[OSD([subQ0])],"isStart":true})],"blendedInto":[]});}
            var Q58;
            {var subQ0=sQuery(id+"F0.wireOp",EDGE,"E3.6.1");var subQ1=sQuery(id+"F0.wireOp",EDGE,"E3.6.2");Q58=makeQuery(id+"F4.opChamfer","BLEND_EDGE",EDGE,{"blendedFrom":[makeQuery(id+"F3.opChamfer","BLEND_EDGE",EDGE,{"blendedFrom":[makeQuery(id+"F1.opExtrude","SWEPT_EDGE",EDGE,{"disambiguationData":[OSD([subQ0,subQ1])]}),makeQuery(id+"F1.opExtrude","CAP_FACE",FACE,{"disambiguationData":[OSD([sQuery(id+"F0.wireOp",EDGE,"E0"),sQuery(id+"F0.wireOp",EDGE,"E1"),sQuery(id+"F0.wireOp",EDGE,"E2.bottom"),sQuery(id+"F0.wireOp",EDGE,"E2.left"),sQuery(id+"F0.wireOp",EDGE,"E2.right"),sQuery(id+"F0.wireOp",EDGE,"E3.1.1"),sQuery(id+"F0.wireOp",EDGE,"E3.1.2"),sQuery(id+"F0.wireOp",EDGE,"E3.1.3"),sQuery(id+"F0.wireOp",EDGE,"E3.2.1"),sQuery(id+"F0.wireOp",EDGE,"E3.2.2"),sQuery(id+"F0.wireOp",EDGE,"E3.2.3"),sQuery(id+"F0.wireOp",EDGE,"E3.3.1"),sQuery(id+"F0.wireOp",EDGE,"E3.3.2"),sQuery(id+"F0.wireOp",EDGE,"E3.3.3"),sQuery(id+"F0.wireOp",EDGE,"E3.4.1"),sQuery(id+"F0.wireOp",EDGE,"E3.4.2"),sQuery(id+"F0.wireOp",EDGE,"E3.4.3"),sQuery(id+"F0.wireOp",EDGE,"E3.5.1"),sQuery(id+"F0.wireOp",EDGE,"E3.5.2"),sQuery(id+"F0.wireOp",EDGE,"E3.5.3"),subQ0,subQ1,sQuery(id+"F0.wireOp",EDGE,"E3.6.3"),sQuery(id+"F0.wireOp",EDGE,"E3.7.1"),sQuery(id+"F0.wireOp",EDGE,"E3.7.2"),sQuery(id+"F0.wireOp",EDGE,"E3.7.3"),sQuery(id+"F0.wireOp",EDGE,"E3.8.1"),sQuery(id+"F0.wireOp",EDGE,"E3.8.2"),sQuery(id+"F0.wireOp",EDGE,"E3.8.3"),sQuery(id+"F0.wireOp",EDGE,"E3.9.1"),sQuery(id+"F0.wireOp",EDGE,"E3.9.2"),sQuery(id+"F0.wireOp",EDGE,"E3.9.3"),sQuery(id+"F0.wireOp",EDGE,"E3.10.1"),sQuery(id+"F0.wireOp",EDGE,"E3.10.2"),sQuery(id+"F0.wireOp",EDGE,"E3.10.3"),sQuery(id+"F0.wireOp",EDGE,"E3.11.1"),sQuery(id+"F0.wireOp",EDGE,"E3.11.2"),sQuery(id+"F0.wireOp",EDGE,"E3.11.3"),sQuery(id+"F0.wireOp",EDGE,"E3.12.1"),sQuery(id+"F0.wireOp",EDGE,"E3.12.2"),sQuery(id+"F0.wireOp",EDGE,"E3.12.3")])],"isStart":false})],"blendedInto":[makeQuery(id+"F1.opExtrude","CAP_FACE",FACE,{"disambiguationData":[OSD([sQuery(id+"F0.wireOp",EDGE,"E0"),sQuery(id+"F0.wireOp",EDGE,"E1"),sQuery(id+"F0.wireOp",EDGE,"E2.bottom"),sQuery(id+"F0.wireOp",EDGE,"E2.left"),sQuery(id+"F0.wireOp",EDGE,"E2.right"),sQuery(id+"F0.wireOp",EDGE,"E3.1.1"),sQuery(id+"F0.wireOp",EDGE,"E3.1.2"),sQuery(id+"F0.wireOp",EDGE,"E3.1.3"),sQuery(id+"F0.wireOp",EDGE,"E3.2.1"),sQuery(id+"F0.wireOp",EDGE,"E3.2.2"),sQuery(id+"F0.wireOp",EDGE,"E3.2.3"),sQuery(id+"F0.wireOp",EDGE,"E3.3.1"),sQuery(id+"F0.wireOp",EDGE,"E3.3.2"),sQuery(id+"F0.wireOp",EDGE,"E3.3.3"),sQuery(id+"F0.wireOp",EDGE,"E3.4.1"),sQuery(id+"F0.wireOp",EDGE,"E3.4.2"),sQuery(id+"F0.wireOp",EDGE,"E3.4.3"),sQuery(id+"F0.wireOp",EDGE,"E3.5.1"),sQuery(id+"F0.wireOp",EDGE,"E3.5.2"),sQuery(id+"F0.wireOp",EDGE,"E3.5.3"),subQ0,subQ1,sQuery(id+"F0.wireOp",EDGE,"E3.6.3"),sQuery(id+"F0.wireOp",EDGE,"E3.7.1"),sQuery(id+"F0.wireOp",EDGE,"E3.7.2"),sQuery(id+"F0.wireOp",EDGE,"E3.7.3"),sQuery(id+"F0.wireOp",EDGE,"E3.8.1"),sQuery(id+"F0.wireOp",EDGE,"E3.8.2"),sQuery(id+"F0.wireOp",EDGE,"E3.8.3"),sQuery(id+"F0.wireOp",EDGE,"E3.9.1"),sQuery(id+"F0.wireOp",EDGE,"E3.9.2"),sQuery(id+"F0.wireOp",EDGE,"E3.9.3"),sQuery(id+"F0.wireOp",EDGE,"E3.10.1"),sQuery(id+"F0.wireOp",EDGE,"E3.10.2"),sQuery(id+"F0.wireOp",EDGE,"E3.10.3"),sQuery(id+"F0.wireOp",EDGE,"E3.11.1"),sQuery(id+"F0.wireOp",EDGE,"E3.11.2"),sQuery(id+"F0.wireOp",EDGE,"E3.11.3"),sQuery(id+"F0.wireOp",EDGE,"E3.12.1"),sQuery(id+"F0.wireOp",EDGE,"E3.12.2"),sQuery(id+"F0.wireOp",EDGE,"E3.12.3")])],"isStart":false})]}),makeQuery(id+"F1.opExtrude","CAP_EDGE",EDGE,{"disambiguationData":[OSD([subQ0])],"isStart":false})],"blendedInto":[]});}
            var Q59;
            {var subQ0=sQuery(id+"F0.wireOp",EDGE,"E3.6.3");Q59=makeQuery(id+"F3.opChamfer","BLEND_EDGE",EDGE,{"blendedFrom":[makeQuery(id+"F1.opExtrude","SWEPT_EDGE",EDGE,{"disambiguationData":[OSD([sQuery(id+"F0.wireOp",EDGE,"E3.6.2"),subQ0])]}),makeQuery(id+"F1.opExtrude","SWEPT_FACE",FACE,{"disambiguationData":[OSD([subQ0])]})],"blendedInto":[makeQuery(id+"F1.opExtrude","SWEPT_FACE",FACE,{"disambiguationData":[OSD([subQ0])]})]});}
            var Q60;
            {var subQ0=sQuery(id+"F0.wireOp",EDGE,"E3.6.1");Q60=makeQuery(id+"F3.opChamfer","BLEND_EDGE",EDGE,{"blendedFrom":[makeQuery(id+"F1.opExtrude","SWEPT_EDGE",EDGE,{"disambiguationData":[OSD([subQ0,sQuery(id+"F0.wireOp",EDGE,"E3.6.2")])]}),makeQuery(id+"F1.opExtrude","SWEPT_FACE",FACE,{"disambiguationData":[OSD([subQ0])]})],"blendedInto":[makeQuery(id+"F1.opExtrude","SWEPT_FACE",FACE,{"disambiguationData":[OSD([subQ0])]})]});}
            var Q61;
            {var subQ0=sQuery(id+"F0.wireOp",EDGE,"E3.6.1");var subQ1=sQuery(id+"F0.wireOp",EDGE,"E3.6.2");Q61=makeQuery(id+"F4.opChamfer","BLEND_EDGE",EDGE,{"blendedFrom":[makeQuery(id+"F3.opChamfer","BLEND_EDGE",EDGE,{"blendedFrom":[makeQuery(id+"F1.opExtrude","SWEPT_EDGE",EDGE,{"disambiguationData":[OSD([subQ0,subQ1])]}),makeQuery(id+"F1.opExtrude","CAP_FACE",FACE,{"disambiguationData":[OSD([sQuery(id+"F0.wireOp",EDGE,"E0"),sQuery(id+"F0.wireOp",EDGE,"E1"),sQuery(id+"F0.wireOp",EDGE,"E2.bottom"),sQuery(id+"F0.wireOp",EDGE,"E2.left"),sQuery(id+"F0.wireOp",EDGE,"E2.right"),sQuery(id+"F0.wireOp",EDGE,"E3.1.1"),sQuery(id+"F0.wireOp",EDGE,"E3.1.2"),sQuery(id+"F0.wireOp",EDGE,"E3.1.3"),sQuery(id+"F0.wireOp",EDGE,"E3.2.1"),sQuery(id+"F0.wireOp",EDGE,"E3.2.2"),sQuery(id+"F0.wireOp",EDGE,"E3.2.3"),sQuery(id+"F0.wireOp",EDGE,"E3.3.1"),sQuery(id+"F0.wireOp",EDGE,"E3.3.2"),sQuery(id+"F0.wireOp",EDGE,"E3.3.3"),sQuery(id+"F0.wireOp",EDGE,"E3.4.1"),sQuery(id+"F0.wireOp",EDGE,"E3.4.2"),sQuery(id+"F0.wireOp",EDGE,"E3.4.3"),sQuery(id+"F0.wireOp",EDGE,"E3.5.1"),sQuery(id+"F0.wireOp",EDGE,"E3.5.2"),sQuery(id+"F0.wireOp",EDGE,"E3.5.3"),subQ0,subQ1,sQuery(id+"F0.wireOp",EDGE,"E3.6.3"),sQuery(id+"F0.wireOp",EDGE,"E3.7.1"),sQuery(id+"F0.wireOp",EDGE,"E3.7.2"),sQuery(id+"F0.wireOp",EDGE,"E3.7.3"),sQuery(id+"F0.wireOp",EDGE,"E3.8.1"),sQuery(id+"F0.wireOp",EDGE,"E3.8.2"),sQuery(id+"F0.wireOp",EDGE,"E3.8.3"),sQuery(id+"F0.wireOp",EDGE,"E3.9.1"),sQuery(id+"F0.wireOp",EDGE,"E3.9.2"),sQuery(id+"F0.wireOp",EDGE,"E3.9.3"),sQuery(id+"F0.wireOp",EDGE,"E3.10.1"),sQuery(id+"F0.wireOp",EDGE,"E3.10.2"),sQuery(id+"F0.wireOp",EDGE,"E3.10.3"),sQuery(id+"F0.wireOp",EDGE,"E3.11.1"),sQuery(id+"F0.wireOp",EDGE,"E3.11.2"),sQuery(id+"F0.wireOp",EDGE,"E3.11.3"),sQuery(id+"F0.wireOp",EDGE,"E3.12.1"),sQuery(id+"F0.wireOp",EDGE,"E3.12.2"),sQuery(id+"F0.wireOp",EDGE,"E3.12.3")])],"isStart":true})],"blendedInto":[makeQuery(id+"F1.opExtrude","CAP_FACE",FACE,{"disambiguationData":[OSD([sQuery(id+"F0.wireOp",EDGE,"E0"),sQuery(id+"F0.wireOp",EDGE,"E1"),sQuery(id+"F0.wireOp",EDGE,"E2.bottom"),sQuery(id+"F0.wireOp",EDGE,"E2.left"),sQuery(id+"F0.wireOp",EDGE,"E2.right"),sQuery(id+"F0.wireOp",EDGE,"E3.1.1"),sQuery(id+"F0.wireOp",EDGE,"E3.1.2"),sQuery(id+"F0.wireOp",EDGE,"E3.1.3"),sQuery(id+"F0.wireOp",EDGE,"E3.2.1"),sQuery(id+"F0.wireOp",EDGE,"E3.2.2"),sQuery(id+"F0.wireOp",EDGE,"E3.2.3"),sQuery(id+"F0.wireOp",EDGE,"E3.3.1"),sQuery(id+"F0.wireOp",EDGE,"E3.3.2"),sQuery(id+"F0.wireOp",EDGE,"E3.3.3"),sQuery(id+"F0.wireOp",EDGE,"E3.4.1"),sQuery(id+"F0.wireOp",EDGE,"E3.4.2"),sQuery(id+"F0.wireOp",EDGE,"E3.4.3"),sQuery(id+"F0.wireOp",EDGE,"E3.5.1"),sQuery(id+"F0.wireOp",EDGE,"E3.5.2"),sQuery(id+"F0.wireOp",EDGE,"E3.5.3"),subQ0,subQ1,sQuery(id+"F0.wireOp",EDGE,"E3.6.3"),sQuery(id+"F0.wireOp",EDGE,"E3.7.1"),sQuery(id+"F0.wireOp",EDGE,"E3.7.2"),sQuery(id+"F0.wireOp",EDGE,"E3.7.3"),sQuery(id+"F0.wireOp",EDGE,"E3.8.1"),sQuery(id+"F0.wireOp",EDGE,"E3.8.2"),sQuery(id+"F0.wireOp",EDGE,"E3.8.3"),sQuery(id+"F0.wireOp",EDGE,"E3.9.1"),sQuery(id+"F0.wireOp",EDGE,"E3.9.2"),sQuery(id+"F0.wireOp",EDGE,"E3.9.3"),sQuery(id+"F0.wireOp",EDGE,"E3.10.1"),sQuery(id+"F0.wireOp",EDGE,"E3.10.2"),sQuery(id+"F0.wireOp",EDGE,"E3.10.3"),sQuery(id+"F0.wireOp",EDGE,"E3.11.1"),sQuery(id+"F0.wireOp",EDGE,"E3.11.2"),sQuery(id+"F0.wireOp",EDGE,"E3.11.3"),sQuery(id+"F0.wireOp",EDGE,"E3.12.1"),sQuery(id+"F0.wireOp",EDGE,"E3.12.2"),sQuery(id+"F0.wireOp",EDGE,"E3.12.3")])],"isStart":true})]}),makeQuery(id+"F1.opExtrude","CAP_EDGE",EDGE,{"disambiguationData":[OSD([subQ0])],"isStart":true})],"blendedInto":[]});}
            var Q62;
            {var subQ0=sQuery(id+"F0.wireOp",EDGE,"E3.6.3");var subQ1=sQuery(id+"F0.wireOp",EDGE,"E3.6.2");Q62=makeQuery(id+"F4.opChamfer","BLEND_EDGE",EDGE,{"blendedFrom":[makeQuery(id+"F3.opChamfer","BLEND_EDGE",EDGE,{"blendedFrom":[makeQuery(id+"F1.opExtrude","SWEPT_EDGE",EDGE,{"disambiguationData":[OSD([subQ1,subQ0])]}),makeQuery(id+"F1.opExtrude","CAP_FACE",FACE,{"disambiguationData":[OSD([sQuery(id+"F0.wireOp",EDGE,"E0"),sQuery(id+"F0.wireOp",EDGE,"E1"),sQuery(id+"F0.wireOp",EDGE,"E2.bottom"),sQuery(id+"F0.wireOp",EDGE,"E2.left"),sQuery(id+"F0.wireOp",EDGE,"E2.right"),sQuery(id+"F0.wireOp",EDGE,"E3.1.1"),sQuery(id+"F0.wireOp",EDGE,"E3.1.2"),sQuery(id+"F0.wireOp",EDGE,"E3.1.3"),sQuery(id+"F0.wireOp",EDGE,"E3.2.1"),sQuery(id+"F0.wireOp",EDGE,"E3.2.2"),sQuery(id+"F0.wireOp",EDGE,"E3.2.3"),sQuery(id+"F0.wireOp",EDGE,"E3.3.1"),sQuery(id+"F0.wireOp",EDGE,"E3.3.2"),sQuery(id+"F0.wireOp",EDGE,"E3.3.3"),sQuery(id+"F0.wireOp",EDGE,"E3.4.1"),sQuery(id+"F0.wireOp",EDGE,"E3.4.2"),sQuery(id+"F0.wireOp",EDGE,"E3.4.3"),sQuery(id+"F0.wireOp",EDGE,"E3.5.1"),sQuery(id+"F0.wireOp",EDGE,"E3.5.2"),sQuery(id+"F0.wireOp",EDGE,"E3.5.3"),sQuery(id+"F0.wireOp",EDGE,"E3.6.1"),subQ1,subQ0,sQuery(id+"F0.wireOp",EDGE,"E3.7.1"),sQuery(id+"F0.wireOp",EDGE,"E3.7.2"),sQuery(id+"F0.wireOp",EDGE,"E3.7.3"),sQuery(id+"F0.wireOp",EDGE,"E3.8.1"),sQuery(id+"F0.wireOp",EDGE,"E3.8.2"),sQuery(id+"F0.wireOp",EDGE,"E3.8.3"),sQuery(id+"F0.wireOp",EDGE,"E3.9.1"),sQuery(id+"F0.wireOp",EDGE,"E3.9.2"),sQuery(id+"F0.wireOp",EDGE,"E3.9.3"),sQuery(id+"F0.wireOp",EDGE,"E3.10.1"),sQuery(id+"F0.wireOp",EDGE,"E3.10.2"),sQuery(id+"F0.wireOp",EDGE,"E3.10.3"),sQuery(id+"F0.wireOp",EDGE,"E3.11.1"),sQuery(id+"F0.wireOp",EDGE,"E3.11.2"),sQuery(id+"F0.wireOp",EDGE,"E3.11.3"),sQuery(id+"F0.wireOp",EDGE,"E3.12.1"),sQuery(id+"F0.wireOp",EDGE,"E3.12.2"),sQuery(id+"F0.wireOp",EDGE,"E3.12.3")])],"isStart":true})],"blendedInto":[makeQuery(id+"F1.opExtrude","CAP_FACE",FACE,{"disambiguationData":[OSD([sQuery(id+"F0.wireOp",EDGE,"E0"),sQuery(id+"F0.wireOp",EDGE,"E1"),sQuery(id+"F0.wireOp",EDGE,"E2.bottom"),sQuery(id+"F0.wireOp",EDGE,"E2.left"),sQuery(id+"F0.wireOp",EDGE,"E2.right"),sQuery(id+"F0.wireOp",EDGE,"E3.1.1"),sQuery(id+"F0.wireOp",EDGE,"E3.1.2"),sQuery(id+"F0.wireOp",EDGE,"E3.1.3"),sQuery(id+"F0.wireOp",EDGE,"E3.2.1"),sQuery(id+"F0.wireOp",EDGE,"E3.2.2"),sQuery(id+"F0.wireOp",EDGE,"E3.2.3"),sQuery(id+"F0.wireOp",EDGE,"E3.3.1"),sQuery(id+"F0.wireOp",EDGE,"E3.3.2"),sQuery(id+"F0.wireOp",EDGE,"E3.3.3"),sQuery(id+"F0.wireOp",EDGE,"E3.4.1"),sQuery(id+"F0.wireOp",EDGE,"E3.4.2"),sQuery(id+"F0.wireOp",EDGE,"E3.4.3"),sQuery(id+"F0.wireOp",EDGE,"E3.5.1"),sQuery(id+"F0.wireOp",EDGE,"E3.5.2"),sQuery(id+"F0.wireOp",EDGE,"E3.5.3"),sQuery(id+"F0.wireOp",EDGE,"E3.6.1"),subQ1,subQ0,sQuery(id+"F0.wireOp",EDGE,"E3.7.1"),sQuery(id+"F0.wireOp",EDGE,"E3.7.2"),sQuery(id+"F0.wireOp",EDGE,"E3.7.3"),sQuery(id+"F0.wireOp",EDGE,"E3.8.1"),sQuery(id+"F0.wireOp",EDGE,"E3.8.2"),sQuery(id+"F0.wireOp",EDGE,"E3.8.3"),sQuery(id+"F0.wireOp",EDGE,"E3.9.1"),sQuery(id+"F0.wireOp",EDGE,"E3.9.2"),sQuery(id+"F0.wireOp",EDGE,"E3.9.3"),sQuery(id+"F0.wireOp",EDGE,"E3.10.1"),sQuery(id+"F0.wireOp",EDGE,"E3.10.2"),sQuery(id+"F0.wireOp",EDGE,"E3.10.3"),sQuery(id+"F0.wireOp",EDGE,"E3.11.1"),sQuery(id+"F0.wireOp",EDGE,"E3.11.2"),sQuery(id+"F0.wireOp",EDGE,"E3.11.3"),sQuery(id+"F0.wireOp",EDGE,"E3.12.1"),sQuery(id+"F0.wireOp",EDGE,"E3.12.2"),sQuery(id+"F0.wireOp",EDGE,"E3.12.3")])],"isStart":true})]}),makeQuery(id+"F1.opExtrude","CAP_EDGE",EDGE,{"disambiguationData":[OSD([subQ0])],"isStart":true})],"blendedInto":[]});}
            var Q63;
            {var subQ0=sQuery(id+"F0.wireOp",EDGE,"E3.3.1");var subQ1=sQuery(id+"F0.wireOp",EDGE,"E3.3.2");Q63=makeQuery(id+"F4.opChamfer","BLEND_EDGE",EDGE,{"blendedFrom":[makeQuery(id+"F3.opChamfer","BLEND_EDGE",EDGE,{"blendedFrom":[makeQuery(id+"F1.opExtrude","SWEPT_EDGE",EDGE,{"disambiguationData":[OSD([subQ0,subQ1])]}),makeQuery(id+"F1.opExtrude","CAP_FACE",FACE,{"disambiguationData":[OSD([sQuery(id+"F0.wireOp",EDGE,"E0"),sQuery(id+"F0.wireOp",EDGE,"E1"),sQuery(id+"F0.wireOp",EDGE,"E2.bottom"),sQuery(id+"F0.wireOp",EDGE,"E2.left"),sQuery(id+"F0.wireOp",EDGE,"E2.right"),sQuery(id+"F0.wireOp",EDGE,"E3.1.1"),sQuery(id+"F0.wireOp",EDGE,"E3.1.2"),sQuery(id+"F0.wireOp",EDGE,"E3.1.3"),sQuery(id+"F0.wireOp",EDGE,"E3.2.1"),sQuery(id+"F0.wireOp",EDGE,"E3.2.2"),sQuery(id+"F0.wireOp",EDGE,"E3.2.3"),subQ0,subQ1,sQuery(id+"F0.wireOp",EDGE,"E3.3.3"),sQuery(id+"F0.wireOp",EDGE,"E3.4.1"),sQuery(id+"F0.wireOp",EDGE,"E3.4.2"),sQuery(id+"F0.wireOp",EDGE,"E3.4.3"),sQuery(id+"F0.wireOp",EDGE,"E3.5.1"),sQuery(id+"F0.wireOp",EDGE,"E3.5.2"),sQuery(id+"F0.wireOp",EDGE,"E3.5.3"),sQuery(id+"F0.wireOp",EDGE,"E3.6.1"),sQuery(id+"F0.wireOp",EDGE,"E3.6.2"),sQuery(id+"F0.wireOp",EDGE,"E3.6.3"),sQuery(id+"F0.wireOp",EDGE,"E3.7.1"),sQuery(id+"F0.wireOp",EDGE,"E3.7.2"),sQuery(id+"F0.wireOp",EDGE,"E3.7.3"),sQuery(id+"F0.wireOp",EDGE,"E3.8.1"),sQuery(id+"F0.wireOp",EDGE,"E3.8.2"),sQuery(id+"F0.wireOp",EDGE,"E3.8.3"),sQuery(id+"F0.wireOp",EDGE,"E3.9.1"),sQuery(id+"F0.wireOp",EDGE,"E3.9.2"),sQuery(id+"F0.wireOp",EDGE,"E3.9.3"),sQuery(id+"F0.wireOp",EDGE,"E3.10.1"),sQuery(id+"F0.wireOp",EDGE,"E3.10.2"),sQuery(id+"F0.wireOp",EDGE,"E3.10.3"),sQuery(id+"F0.wireOp",EDGE,"E3.11.1"),sQuery(id+"F0.wireOp",EDGE,"E3.11.2"),sQuery(id+"F0.wireOp",EDGE,"E3.11.3"),sQuery(id+"F0.wireOp",EDGE,"E3.12.1"),sQuery(id+"F0.wireOp",EDGE,"E3.12.2"),sQuery(id+"F0.wireOp",EDGE,"E3.12.3")])],"isStart":true})],"blendedInto":[makeQuery(id+"F1.opExtrude","CAP_FACE",FACE,{"disambiguationData":[OSD([sQuery(id+"F0.wireOp",EDGE,"E0"),sQuery(id+"F0.wireOp",EDGE,"E1"),sQuery(id+"F0.wireOp",EDGE,"E2.bottom"),sQuery(id+"F0.wireOp",EDGE,"E2.left"),sQuery(id+"F0.wireOp",EDGE,"E2.right"),sQuery(id+"F0.wireOp",EDGE,"E3.1.1"),sQuery(id+"F0.wireOp",EDGE,"E3.1.2"),sQuery(id+"F0.wireOp",EDGE,"E3.1.3"),sQuery(id+"F0.wireOp",EDGE,"E3.2.1"),sQuery(id+"F0.wireOp",EDGE,"E3.2.2"),sQuery(id+"F0.wireOp",EDGE,"E3.2.3"),subQ0,subQ1,sQuery(id+"F0.wireOp",EDGE,"E3.3.3"),sQuery(id+"F0.wireOp",EDGE,"E3.4.1"),sQuery(id+"F0.wireOp",EDGE,"E3.4.2"),sQuery(id+"F0.wireOp",EDGE,"E3.4.3"),sQuery(id+"F0.wireOp",EDGE,"E3.5.1"),sQuery(id+"F0.wireOp",EDGE,"E3.5.2"),sQuery(id+"F0.wireOp",EDGE,"E3.5.3"),sQuery(id+"F0.wireOp",EDGE,"E3.6.1"),sQuery(id+"F0.wireOp",EDGE,"E3.6.2"),sQuery(id+"F0.wireOp",EDGE,"E3.6.3"),sQuery(id+"F0.wireOp",EDGE,"E3.7.1"),sQuery(id+"F0.wireOp",EDGE,"E3.7.2"),sQuery(id+"F0.wireOp",EDGE,"E3.7.3"),sQuery(id+"F0.wireOp",EDGE,"E3.8.1"),sQuery(id+"F0.wireOp",EDGE,"E3.8.2"),sQuery(id+"F0.wireOp",EDGE,"E3.8.3"),sQuery(id+"F0.wireOp",EDGE,"E3.9.1"),sQuery(id+"F0.wireOp",EDGE,"E3.9.2"),sQuery(id+"F0.wireOp",EDGE,"E3.9.3"),sQuery(id+"F0.wireOp",EDGE,"E3.10.1"),sQuery(id+"F0.wireOp",EDGE,"E3.10.2"),sQuery(id+"F0.wireOp",EDGE,"E3.10.3"),sQuery(id+"F0.wireOp",EDGE,"E3.11.1"),sQuery(id+"F0.wireOp",EDGE,"E3.11.2"),sQuery(id+"F0.wireOp",EDGE,"E3.11.3"),sQuery(id+"F0.wireOp",EDGE,"E3.12.1"),sQuery(id+"F0.wireOp",EDGE,"E3.12.2"),sQuery(id+"F0.wireOp",EDGE,"E3.12.3")])],"isStart":true})]}),makeQuery(id+"F1.opExtrude","CAP_EDGE",EDGE,{"disambiguationData":[OSD([subQ0])],"isStart":true})],"blendedInto":[]});}
            var Q64;
            {var subQ0=sQuery(id+"F0.wireOp",EDGE,"E3.3.3");var subQ1=sQuery(id+"F0.wireOp",EDGE,"E3.3.2");Q64=makeQuery(id+"F4.opChamfer","BLEND_EDGE",EDGE,{"blendedFrom":[makeQuery(id+"F3.opChamfer","BLEND_EDGE",EDGE,{"blendedFrom":[makeQuery(id+"F1.opExtrude","SWEPT_EDGE",EDGE,{"disambiguationData":[OSD([subQ1,subQ0])]}),makeQuery(id+"F1.opExtrude","CAP_FACE",FACE,{"disambiguationData":[OSD([sQuery(id+"F0.wireOp",EDGE,"E0"),sQuery(id+"F0.wireOp",EDGE,"E1"),sQuery(id+"F0.wireOp",EDGE,"E2.bottom"),sQuery(id+"F0.wireOp",EDGE,"E2.left"),sQuery(id+"F0.wireOp",EDGE,"E2.right"),sQuery(id+"F0.wireOp",EDGE,"E3.1.1"),sQuery(id+"F0.wireOp",EDGE,"E3.1.2"),sQuery(id+"F0.wireOp",EDGE,"E3.1.3"),sQuery(id+"F0.wireOp",EDGE,"E3.2.1"),sQuery(id+"F0.wireOp",EDGE,"E3.2.2"),sQuery(id+"F0.wireOp",EDGE,"E3.2.3"),sQuery(id+"F0.wireOp",EDGE,"E3.3.1"),subQ1,subQ0,sQuery(id+"F0.wireOp",EDGE,"E3.4.1"),sQuery(id+"F0.wireOp",EDGE,"E3.4.2"),sQuery(id+"F0.wireOp",EDGE,"E3.4.3"),sQuery(id+"F0.wireOp",EDGE,"E3.5.1"),sQuery(id+"F0.wireOp",EDGE,"E3.5.2"),sQuery(id+"F0.wireOp",EDGE,"E3.5.3"),sQuery(id+"F0.wireOp",EDGE,"E3.6.1"),sQuery(id+"F0.wireOp",EDGE,"E3.6.2"),sQuery(id+"F0.wireOp",EDGE,"E3.6.3"),sQuery(id+"F0.wireOp",EDGE,"E3.7.1"),sQuery(id+"F0.wireOp",EDGE,"E3.7.2"),sQuery(id+"F0.wireOp",EDGE,"E3.7.3"),sQuery(id+"F0.wireOp",EDGE,"E3.8.1"),sQuery(id+"F0.wireOp",EDGE,"E3.8.2"),sQuery(id+"F0.wireOp",EDGE,"E3.8.3"),sQuery(id+"F0.wireOp",EDGE,"E3.9.1"),sQuery(id+"F0.wireOp",EDGE,"E3.9.2"),sQuery(id+"F0.wireOp",EDGE,"E3.9.3"),sQuery(id+"F0.wireOp",EDGE,"E3.10.1"),sQuery(id+"F0.wireOp",EDGE,"E3.10.2"),sQuery(id+"F0.wireOp",EDGE,"E3.10.3"),sQuery(id+"F0.wireOp",EDGE,"E3.11.1"),sQuery(id+"F0.wireOp",EDGE,"E3.11.2"),sQuery(id+"F0.wireOp",EDGE,"E3.11.3"),sQuery(id+"F0.wireOp",EDGE,"E3.12.1"),sQuery(id+"F0.wireOp",EDGE,"E3.12.2"),sQuery(id+"F0.wireOp",EDGE,"E3.12.3")])],"isStart":true})],"blendedInto":[makeQuery(id+"F1.opExtrude","CAP_FACE",FACE,{"disambiguationData":[OSD([sQuery(id+"F0.wireOp",EDGE,"E0"),sQuery(id+"F0.wireOp",EDGE,"E1"),sQuery(id+"F0.wireOp",EDGE,"E2.bottom"),sQuery(id+"F0.wireOp",EDGE,"E2.left"),sQuery(id+"F0.wireOp",EDGE,"E2.right"),sQuery(id+"F0.wireOp",EDGE,"E3.1.1"),sQuery(id+"F0.wireOp",EDGE,"E3.1.2"),sQuery(id+"F0.wireOp",EDGE,"E3.1.3"),sQuery(id+"F0.wireOp",EDGE,"E3.2.1"),sQuery(id+"F0.wireOp",EDGE,"E3.2.2"),sQuery(id+"F0.wireOp",EDGE,"E3.2.3"),sQuery(id+"F0.wireOp",EDGE,"E3.3.1"),subQ1,subQ0,sQuery(id+"F0.wireOp",EDGE,"E3.4.1"),sQuery(id+"F0.wireOp",EDGE,"E3.4.2"),sQuery(id+"F0.wireOp",EDGE,"E3.4.3"),sQuery(id+"F0.wireOp",EDGE,"E3.5.1"),sQuery(id+"F0.wireOp",EDGE,"E3.5.2"),sQuery(id+"F0.wireOp",EDGE,"E3.5.3"),sQuery(id+"F0.wireOp",EDGE,"E3.6.1"),sQuery(id+"F0.wireOp",EDGE,"E3.6.2"),sQuery(id+"F0.wireOp",EDGE,"E3.6.3"),sQuery(id+"F0.wireOp",EDGE,"E3.7.1"),sQuery(id+"F0.wireOp",EDGE,"E3.7.2"),sQuery(id+"F0.wireOp",EDGE,"E3.7.3"),sQuery(id+"F0.wireOp",EDGE,"E3.8.1"),sQuery(id+"F0.wireOp",EDGE,"E3.8.2"),sQuery(id+"F0.wireOp",EDGE,"E3.8.3"),sQuery(id+"F0.wireOp",EDGE,"E3.9.1"),sQuery(id+"F0.wireOp",EDGE,"E3.9.2"),sQuery(id+"F0.wireOp",EDGE,"E3.9.3"),sQuery(id+"F0.wireOp",EDGE,"E3.10.1"),sQuery(id+"F0.wireOp",EDGE,"E3.10.2"),sQuery(id+"F0.wireOp",EDGE,"E3.10.3"),sQuery(id+"F0.wireOp",EDGE,"E3.11.1"),sQuery(id+"F0.wireOp",EDGE,"E3.11.2"),sQuery(id+"F0.wireOp",EDGE,"E3.11.3"),sQuery(id+"F0.wireOp",EDGE,"E3.12.1"),sQuery(id+"F0.wireOp",EDGE,"E3.12.2"),sQuery(id+"F0.wireOp",EDGE,"E3.12.3")])],"isStart":true})]}),makeQuery(id+"F1.opExtrude","CAP_EDGE",EDGE,{"disambiguationData":[OSD([subQ0])],"isStart":true})],"blendedInto":[]});}
            var Q65;
            {var subQ0=sQuery(id+"F0.wireOp",EDGE,"E3.4.3");Q65=makeQuery(id+"F3.opChamfer","BLEND_EDGE",EDGE,{"blendedFrom":[makeQuery(id+"F1.opExtrude","SWEPT_EDGE",EDGE,{"disambiguationData":[OSD([sQuery(id+"F0.wireOp",EDGE,"E3.4.2"),subQ0])]}),makeQuery(id+"F1.opExtrude","SWEPT_FACE",FACE,{"disambiguationData":[OSD([subQ0])]})],"blendedInto":[makeQuery(id+"F1.opExtrude","SWEPT_FACE",FACE,{"disambiguationData":[OSD([subQ0])]})]});}
            var Q66;
            {var subQ0=sQuery(id+"F0.wireOp",EDGE,"E3.5.3");Q66=makeQuery(id+"F3.opChamfer","BLEND_EDGE",EDGE,{"blendedFrom":[makeQuery(id+"F1.opExtrude","SWEPT_EDGE",EDGE,{"disambiguationData":[OSD([sQuery(id+"F0.wireOp",EDGE,"E3.5.2"),subQ0])]}),makeQuery(id+"F1.opExtrude","SWEPT_FACE",FACE,{"disambiguationData":[OSD([subQ0])]})],"blendedInto":[makeQuery(id+"F1.opExtrude","SWEPT_FACE",FACE,{"disambiguationData":[OSD([subQ0])]})]});}
            var Q67;
            {var subQ0=sQuery(id+"F0.wireOp",EDGE,"E3.4.1");var subQ1=sQuery(id+"F0.wireOp",EDGE,"E3.4.2");Q67=makeQuery(id+"F4.opChamfer","BLEND_EDGE",EDGE,{"blendedFrom":[makeQuery(id+"F3.opChamfer","BLEND_EDGE",EDGE,{"blendedFrom":[makeQuery(id+"F1.opExtrude","SWEPT_EDGE",EDGE,{"disambiguationData":[OSD([subQ0,subQ1])]}),makeQuery(id+"F1.opExtrude","CAP_FACE",FACE,{"disambiguationData":[OSD([sQuery(id+"F0.wireOp",EDGE,"E0"),sQuery(id+"F0.wireOp",EDGE,"E1"),sQuery(id+"F0.wireOp",EDGE,"E2.bottom"),sQuery(id+"F0.wireOp",EDGE,"E2.left"),sQuery(id+"F0.wireOp",EDGE,"E2.right"),sQuery(id+"F0.wireOp",EDGE,"E3.1.1"),sQuery(id+"F0.wireOp",EDGE,"E3.1.2"),sQuery(id+"F0.wireOp",EDGE,"E3.1.3"),sQuery(id+"F0.wireOp",EDGE,"E3.2.1"),sQuery(id+"F0.wireOp",EDGE,"E3.2.2"),sQuery(id+"F0.wireOp",EDGE,"E3.2.3"),sQuery(id+"F0.wireOp",EDGE,"E3.3.1"),sQuery(id+"F0.wireOp",EDGE,"E3.3.2"),sQuery(id+"F0.wireOp",EDGE,"E3.3.3"),subQ0,subQ1,sQuery(id+"F0.wireOp",EDGE,"E3.4.3"),sQuery(id+"F0.wireOp",EDGE,"E3.5.1"),sQuery(id+"F0.wireOp",EDGE,"E3.5.2"),sQuery(id+"F0.wireOp",EDGE,"E3.5.3"),sQuery(id+"F0.wireOp",EDGE,"E3.6.1"),sQuery(id+"F0.wireOp",EDGE,"E3.6.2"),sQuery(id+"F0.wireOp",EDGE,"E3.6.3"),sQuery(id+"F0.wireOp",EDGE,"E3.7.1"),sQuery(id+"F0.wireOp",EDGE,"E3.7.2"),sQuery(id+"F0.wireOp",EDGE,"E3.7.3"),sQuery(id+"F0.wireOp",EDGE,"E3.8.1"),sQuery(id+"F0.wireOp",EDGE,"E3.8.2"),sQuery(id+"F0.wireOp",EDGE,"E3.8.3"),sQuery(id+"F0.wireOp",EDGE,"E3.9.1"),sQuery(id+"F0.wireOp",EDGE,"E3.9.2"),sQuery(id+"F0.wireOp",EDGE,"E3.9.3"),sQuery(id+"F0.wireOp",EDGE,"E3.10.1"),sQuery(id+"F0.wireOp",EDGE,"E3.10.2"),sQuery(id+"F0.wireOp",EDGE,"E3.10.3"),sQuery(id+"F0.wireOp",EDGE,"E3.11.1"),sQuery(id+"F0.wireOp",EDGE,"E3.11.2"),sQuery(id+"F0.wireOp",EDGE,"E3.11.3"),sQuery(id+"F0.wireOp",EDGE,"E3.12.1"),sQuery(id+"F0.wireOp",EDGE,"E3.12.2"),sQuery(id+"F0.wireOp",EDGE,"E3.12.3")])],"isStart":true})],"blendedInto":[makeQuery(id+"F1.opExtrude","CAP_FACE",FACE,{"disambiguationData":[OSD([sQuery(id+"F0.wireOp",EDGE,"E0"),sQuery(id+"F0.wireOp",EDGE,"E1"),sQuery(id+"F0.wireOp",EDGE,"E2.bottom"),sQuery(id+"F0.wireOp",EDGE,"E2.left"),sQuery(id+"F0.wireOp",EDGE,"E2.right"),sQuery(id+"F0.wireOp",EDGE,"E3.1.1"),sQuery(id+"F0.wireOp",EDGE,"E3.1.2"),sQuery(id+"F0.wireOp",EDGE,"E3.1.3"),sQuery(id+"F0.wireOp",EDGE,"E3.2.1"),sQuery(id+"F0.wireOp",EDGE,"E3.2.2"),sQuery(id+"F0.wireOp",EDGE,"E3.2.3"),sQuery(id+"F0.wireOp",EDGE,"E3.3.1"),sQuery(id+"F0.wireOp",EDGE,"E3.3.2"),sQuery(id+"F0.wireOp",EDGE,"E3.3.3"),subQ0,subQ1,sQuery(id+"F0.wireOp",EDGE,"E3.4.3"),sQuery(id+"F0.wireOp",EDGE,"E3.5.1"),sQuery(id+"F0.wireOp",EDGE,"E3.5.2"),sQuery(id+"F0.wireOp",EDGE,"E3.5.3"),sQuery(id+"F0.wireOp",EDGE,"E3.6.1"),sQuery(id+"F0.wireOp",EDGE,"E3.6.2"),sQuery(id+"F0.wireOp",EDGE,"E3.6.3"),sQuery(id+"F0.wireOp",EDGE,"E3.7.1"),sQuery(id+"F0.wireOp",EDGE,"E3.7.2"),sQuery(id+"F0.wireOp",EDGE,"E3.7.3"),sQuery(id+"F0.wireOp",EDGE,"E3.8.1"),sQuery(id+"F0.wireOp",EDGE,"E3.8.2"),sQuery(id+"F0.wireOp",EDGE,"E3.8.3"),sQuery(id+"F0.wireOp",EDGE,"E3.9.1"),sQuery(id+"F0.wireOp",EDGE,"E3.9.2"),sQuery(id+"F0.wireOp",EDGE,"E3.9.3"),sQuery(id+"F0.wireOp",EDGE,"E3.10.1"),sQuery(id+"F0.wireOp",EDGE,"E3.10.2"),sQuery(id+"F0.wireOp",EDGE,"E3.10.3"),sQuery(id+"F0.wireOp",EDGE,"E3.11.1"),sQuery(id+"F0.wireOp",EDGE,"E3.11.2"),sQuery(id+"F0.wireOp",EDGE,"E3.11.3"),sQuery(id+"F0.wireOp",EDGE,"E3.12.1"),sQuery(id+"F0.wireOp",EDGE,"E3.12.2"),sQuery(id+"F0.wireOp",EDGE,"E3.12.3")])],"isStart":true})]}),makeQuery(id+"F1.opExtrude","CAP_EDGE",EDGE,{"disambiguationData":[OSD([subQ0])],"isStart":true})],"blendedInto":[]});}
            var Q68;
            {var subQ0=sQuery(id+"F0.wireOp",EDGE,"E3.4.3");var subQ1=sQuery(id+"F0.wireOp",EDGE,"E3.4.2");Q68=makeQuery(id+"F4.opChamfer","BLEND_EDGE",EDGE,{"blendedFrom":[makeQuery(id+"F3.opChamfer","BLEND_EDGE",EDGE,{"blendedFrom":[makeQuery(id+"F1.opExtrude","SWEPT_EDGE",EDGE,{"disambiguationData":[OSD([subQ1,subQ0])]}),makeQuery(id+"F1.opExtrude","CAP_FACE",FACE,{"disambiguationData":[OSD([sQuery(id+"F0.wireOp",EDGE,"E0"),sQuery(id+"F0.wireOp",EDGE,"E1"),sQuery(id+"F0.wireOp",EDGE,"E2.bottom"),sQuery(id+"F0.wireOp",EDGE,"E2.left"),sQuery(id+"F0.wireOp",EDGE,"E2.right"),sQuery(id+"F0.wireOp",EDGE,"E3.1.1"),sQuery(id+"F0.wireOp",EDGE,"E3.1.2"),sQuery(id+"F0.wireOp",EDGE,"E3.1.3"),sQuery(id+"F0.wireOp",EDGE,"E3.2.1"),sQuery(id+"F0.wireOp",EDGE,"E3.2.2"),sQuery(id+"F0.wireOp",EDGE,"E3.2.3"),sQuery(id+"F0.wireOp",EDGE,"E3.3.1"),sQuery(id+"F0.wireOp",EDGE,"E3.3.2"),sQuery(id+"F0.wireOp",EDGE,"E3.3.3"),sQuery(id+"F0.wireOp",EDGE,"E3.4.1"),subQ1,subQ0,sQuery(id+"F0.wireOp",EDGE,"E3.5.1"),sQuery(id+"F0.wireOp",EDGE,"E3.5.2"),sQuery(id+"F0.wireOp",EDGE,"E3.5.3"),sQuery(id+"F0.wireOp",EDGE,"E3.6.1"),sQuery(id+"F0.wireOp",EDGE,"E3.6.2"),sQuery(id+"F0.wireOp",EDGE,"E3.6.3"),sQuery(id+"F0.wireOp",EDGE,"E3.7.1"),sQuery(id+"F0.wireOp",EDGE,"E3.7.2"),sQuery(id+"F0.wireOp",EDGE,"E3.7.3"),sQuery(id+"F0.wireOp",EDGE,"E3.8.1"),sQuery(id+"F0.wireOp",EDGE,"E3.8.2"),sQuery(id+"F0.wireOp",EDGE,"E3.8.3"),sQuery(id+"F0.wireOp",EDGE,"E3.9.1"),sQuery(id+"F0.wireOp",EDGE,"E3.9.2"),sQuery(id+"F0.wireOp",EDGE,"E3.9.3"),sQuery(id+"F0.wireOp",EDGE,"E3.10.1"),sQuery(id+"F0.wireOp",EDGE,"E3.10.2"),sQuery(id+"F0.wireOp",EDGE,"E3.10.3"),sQuery(id+"F0.wireOp",EDGE,"E3.11.1"),sQuery(id+"F0.wireOp",EDGE,"E3.11.2"),sQuery(id+"F0.wireOp",EDGE,"E3.11.3"),sQuery(id+"F0.wireOp",EDGE,"E3.12.1"),sQuery(id+"F0.wireOp",EDGE,"E3.12.2"),sQuery(id+"F0.wireOp",EDGE,"E3.12.3")])],"isStart":true})],"blendedInto":[makeQuery(id+"F1.opExtrude","CAP_FACE",FACE,{"disambiguationData":[OSD([sQuery(id+"F0.wireOp",EDGE,"E0"),sQuery(id+"F0.wireOp",EDGE,"E1"),sQuery(id+"F0.wireOp",EDGE,"E2.bottom"),sQuery(id+"F0.wireOp",EDGE,"E2.left"),sQuery(id+"F0.wireOp",EDGE,"E2.right"),sQuery(id+"F0.wireOp",EDGE,"E3.1.1"),sQuery(id+"F0.wireOp",EDGE,"E3.1.2"),sQuery(id+"F0.wireOp",EDGE,"E3.1.3"),sQuery(id+"F0.wireOp",EDGE,"E3.2.1"),sQuery(id+"F0.wireOp",EDGE,"E3.2.2"),sQuery(id+"F0.wireOp",EDGE,"E3.2.3"),sQuery(id+"F0.wireOp",EDGE,"E3.3.1"),sQuery(id+"F0.wireOp",EDGE,"E3.3.2"),sQuery(id+"F0.wireOp",EDGE,"E3.3.3"),sQuery(id+"F0.wireOp",EDGE,"E3.4.1"),subQ1,subQ0,sQuery(id+"F0.wireOp",EDGE,"E3.5.1"),sQuery(id+"F0.wireOp",EDGE,"E3.5.2"),sQuery(id+"F0.wireOp",EDGE,"E3.5.3"),sQuery(id+"F0.wireOp",EDGE,"E3.6.1"),sQuery(id+"F0.wireOp",EDGE,"E3.6.2"),sQuery(id+"F0.wireOp",EDGE,"E3.6.3"),sQuery(id+"F0.wireOp",EDGE,"E3.7.1"),sQuery(id+"F0.wireOp",EDGE,"E3.7.2"),sQuery(id+"F0.wireOp",EDGE,"E3.7.3"),sQuery(id+"F0.wireOp",EDGE,"E3.8.1"),sQuery(id+"F0.wireOp",EDGE,"E3.8.2"),sQuery(id+"F0.wireOp",EDGE,"E3.8.3"),sQuery(id+"F0.wireOp",EDGE,"E3.9.1"),sQuery(id+"F0.wireOp",EDGE,"E3.9.2"),sQuery(id+"F0.wireOp",EDGE,"E3.9.3"),sQuery(id+"F0.wireOp",EDGE,"E3.10.1"),sQuery(id+"F0.wireOp",EDGE,"E3.10.2"),sQuery(id+"F0.wireOp",EDGE,"E3.10.3"),sQuery(id+"F0.wireOp",EDGE,"E3.11.1"),sQuery(id+"F0.wireOp",EDGE,"E3.11.2"),sQuery(id+"F0.wireOp",EDGE,"E3.11.3"),sQuery(id+"F0.wireOp",EDGE,"E3.12.1"),sQuery(id+"F0.wireOp",EDGE,"E3.12.2"),sQuery(id+"F0.wireOp",EDGE,"E3.12.3")])],"isStart":true})]}),makeQuery(id+"F1.opExtrude","CAP_EDGE",EDGE,{"disambiguationData":[OSD([subQ0])],"isStart":true})],"blendedInto":[]});}
            var Q69;
            {var subQ0=sQuery(id+"F0.wireOp",EDGE,"E3.4.1");Q69=makeQuery(id+"F3.opChamfer","BLEND_EDGE",EDGE,{"blendedFrom":[makeQuery(id+"F1.opExtrude","SWEPT_EDGE",EDGE,{"disambiguationData":[OSD([subQ0,sQuery(id+"F0.wireOp",EDGE,"E3.4.2")])]}),makeQuery(id+"F1.opExtrude","SWEPT_FACE",FACE,{"disambiguationData":[OSD([subQ0])]})],"blendedInto":[makeQuery(id+"F1.opExtrude","SWEPT_FACE",FACE,{"disambiguationData":[OSD([subQ0])]})]});}
            var Q70;
            {var subQ0=sQuery(id+"F0.wireOp",EDGE,"E3.5.1");var subQ1=sQuery(id+"F0.wireOp",EDGE,"E3.5.2");Q70=makeQuery(id+"F4.opChamfer","BLEND_EDGE",EDGE,{"blendedFrom":[makeQuery(id+"F3.opChamfer","BLEND_EDGE",EDGE,{"blendedFrom":[makeQuery(id+"F1.opExtrude","SWEPT_EDGE",EDGE,{"disambiguationData":[OSD([subQ0,subQ1])]}),makeQuery(id+"F1.opExtrude","CAP_FACE",FACE,{"disambiguationData":[OSD([sQuery(id+"F0.wireOp",EDGE,"E0"),sQuery(id+"F0.wireOp",EDGE,"E1"),sQuery(id+"F0.wireOp",EDGE,"E2.bottom"),sQuery(id+"F0.wireOp",EDGE,"E2.left"),sQuery(id+"F0.wireOp",EDGE,"E2.right"),sQuery(id+"F0.wireOp",EDGE,"E3.1.1"),sQuery(id+"F0.wireOp",EDGE,"E3.1.2"),sQuery(id+"F0.wireOp",EDGE,"E3.1.3"),sQuery(id+"F0.wireOp",EDGE,"E3.2.1"),sQuery(id+"F0.wireOp",EDGE,"E3.2.2"),sQuery(id+"F0.wireOp",EDGE,"E3.2.3"),sQuery(id+"F0.wireOp",EDGE,"E3.3.1"),sQuery(id+"F0.wireOp",EDGE,"E3.3.2"),sQuery(id+"F0.wireOp",EDGE,"E3.3.3"),sQuery(id+"F0.wireOp",EDGE,"E3.4.1"),sQuery(id+"F0.wireOp",EDGE,"E3.4.2"),sQuery(id+"F0.wireOp",EDGE,"E3.4.3"),subQ0,subQ1,sQuery(id+"F0.wireOp",EDGE,"E3.5.3"),sQuery(id+"F0.wireOp",EDGE,"E3.6.1"),sQuery(id+"F0.wireOp",EDGE,"E3.6.2"),sQuery(id+"F0.wireOp",EDGE,"E3.6.3"),sQuery(id+"F0.wireOp",EDGE,"E3.7.1"),sQuery(id+"F0.wireOp",EDGE,"E3.7.2"),sQuery(id+"F0.wireOp",EDGE,"E3.7.3"),sQuery(id+"F0.wireOp",EDGE,"E3.8.1"),sQuery(id+"F0.wireOp",EDGE,"E3.8.2"),sQuery(id+"F0.wireOp",EDGE,"E3.8.3"),sQuery(id+"F0.wireOp",EDGE,"E3.9.1"),sQuery(id+"F0.wireOp",EDGE,"E3.9.2"),sQuery(id+"F0.wireOp",EDGE,"E3.9.3"),sQuery(id+"F0.wireOp",EDGE,"E3.10.1"),sQuery(id+"F0.wireOp",EDGE,"E3.10.2"),sQuery(id+"F0.wireOp",EDGE,"E3.10.3"),sQuery(id+"F0.wireOp",EDGE,"E3.11.1"),sQuery(id+"F0.wireOp",EDGE,"E3.11.2"),sQuery(id+"F0.wireOp",EDGE,"E3.11.3"),sQuery(id+"F0.wireOp",EDGE,"E3.12.1"),sQuery(id+"F0.wireOp",EDGE,"E3.12.2"),sQuery(id+"F0.wireOp",EDGE,"E3.12.3")])],"isStart":true})],"blendedInto":[makeQuery(id+"F1.opExtrude","CAP_FACE",FACE,{"disambiguationData":[OSD([sQuery(id+"F0.wireOp",EDGE,"E0"),sQuery(id+"F0.wireOp",EDGE,"E1"),sQuery(id+"F0.wireOp",EDGE,"E2.bottom"),sQuery(id+"F0.wireOp",EDGE,"E2.left"),sQuery(id+"F0.wireOp",EDGE,"E2.right"),sQuery(id+"F0.wireOp",EDGE,"E3.1.1"),sQuery(id+"F0.wireOp",EDGE,"E3.1.2"),sQuery(id+"F0.wireOp",EDGE,"E3.1.3"),sQuery(id+"F0.wireOp",EDGE,"E3.2.1"),sQuery(id+"F0.wireOp",EDGE,"E3.2.2"),sQuery(id+"F0.wireOp",EDGE,"E3.2.3"),sQuery(id+"F0.wireOp",EDGE,"E3.3.1"),sQuery(id+"F0.wireOp",EDGE,"E3.3.2"),sQuery(id+"F0.wireOp",EDGE,"E3.3.3"),sQuery(id+"F0.wireOp",EDGE,"E3.4.1"),sQuery(id+"F0.wireOp",EDGE,"E3.4.2"),sQuery(id+"F0.wireOp",EDGE,"E3.4.3"),subQ0,subQ1,sQuery(id+"F0.wireOp",EDGE,"E3.5.3"),sQuery(id+"F0.wireOp",EDGE,"E3.6.1"),sQuery(id+"F0.wireOp",EDGE,"E3.6.2"),sQuery(id+"F0.wireOp",EDGE,"E3.6.3"),sQuery(id+"F0.wireOp",EDGE,"E3.7.1"),sQuery(id+"F0.wireOp",EDGE,"E3.7.2"),sQuery(id+"F0.wireOp",EDGE,"E3.7.3"),sQuery(id+"F0.wireOp",EDGE,"E3.8.1"),sQuery(id+"F0.wireOp",EDGE,"E3.8.2"),sQuery(id+"F0.wireOp",EDGE,"E3.8.3"),sQuery(id+"F0.wireOp",EDGE,"E3.9.1"),sQuery(id+"F0.wireOp",EDGE,"E3.9.2"),sQuery(id+"F0.wireOp",EDGE,"E3.9.3"),sQuery(id+"F0.wireOp",EDGE,"E3.10.1"),sQuery(id+"F0.wireOp",EDGE,"E3.10.2"),sQuery(id+"F0.wireOp",EDGE,"E3.10.3"),sQuery(id+"F0.wireOp",EDGE,"E3.11.1"),sQuery(id+"F0.wireOp",EDGE,"E3.11.2"),sQuery(id+"F0.wireOp",EDGE,"E3.11.3"),sQuery(id+"F0.wireOp",EDGE,"E3.12.1"),sQuery(id+"F0.wireOp",EDGE,"E3.12.2"),sQuery(id+"F0.wireOp",EDGE,"E3.12.3")])],"isStart":true})]}),makeQuery(id+"F1.opExtrude","CAP_EDGE",EDGE,{"disambiguationData":[OSD([subQ0])],"isStart":true})],"blendedInto":[]});}
            var Q71;
            {var subQ0=sQuery(id+"F0.wireOp",EDGE,"E3.5.3");var subQ1=sQuery(id+"F0.wireOp",EDGE,"E3.5.2");Q71=makeQuery(id+"F4.opChamfer","BLEND_EDGE",EDGE,{"blendedFrom":[makeQuery(id+"F3.opChamfer","BLEND_EDGE",EDGE,{"blendedFrom":[makeQuery(id+"F1.opExtrude","SWEPT_EDGE",EDGE,{"disambiguationData":[OSD([subQ1,subQ0])]}),makeQuery(id+"F1.opExtrude","CAP_FACE",FACE,{"disambiguationData":[OSD([sQuery(id+"F0.wireOp",EDGE,"E0"),sQuery(id+"F0.wireOp",EDGE,"E1"),sQuery(id+"F0.wireOp",EDGE,"E2.bottom"),sQuery(id+"F0.wireOp",EDGE,"E2.left"),sQuery(id+"F0.wireOp",EDGE,"E2.right"),sQuery(id+"F0.wireOp",EDGE,"E3.1.1"),sQuery(id+"F0.wireOp",EDGE,"E3.1.2"),sQuery(id+"F0.wireOp",EDGE,"E3.1.3"),sQuery(id+"F0.wireOp",EDGE,"E3.2.1"),sQuery(id+"F0.wireOp",EDGE,"E3.2.2"),sQuery(id+"F0.wireOp",EDGE,"E3.2.3"),sQuery(id+"F0.wireOp",EDGE,"E3.3.1"),sQuery(id+"F0.wireOp",EDGE,"E3.3.2"),sQuery(id+"F0.wireOp",EDGE,"E3.3.3"),sQuery(id+"F0.wireOp",EDGE,"E3.4.1"),sQuery(id+"F0.wireOp",EDGE,"E3.4.2"),sQuery(id+"F0.wireOp",EDGE,"E3.4.3"),sQuery(id+"F0.wireOp",EDGE,"E3.5.1"),subQ1,subQ0,sQuery(id+"F0.wireOp",EDGE,"E3.6.1"),sQuery(id+"F0.wireOp",EDGE,"E3.6.2"),sQuery(id+"F0.wireOp",EDGE,"E3.6.3"),sQuery(id+"F0.wireOp",EDGE,"E3.7.1"),sQuery(id+"F0.wireOp",EDGE,"E3.7.2"),sQuery(id+"F0.wireOp",EDGE,"E3.7.3"),sQuery(id+"F0.wireOp",EDGE,"E3.8.1"),sQuery(id+"F0.wireOp",EDGE,"E3.8.2"),sQuery(id+"F0.wireOp",EDGE,"E3.8.3"),sQuery(id+"F0.wireOp",EDGE,"E3.9.1"),sQuery(id+"F0.wireOp",EDGE,"E3.9.2"),sQuery(id+"F0.wireOp",EDGE,"E3.9.3"),sQuery(id+"F0.wireOp",EDGE,"E3.10.1"),sQuery(id+"F0.wireOp",EDGE,"E3.10.2"),sQuery(id+"F0.wireOp",EDGE,"E3.10.3"),sQuery(id+"F0.wireOp",EDGE,"E3.11.1"),sQuery(id+"F0.wireOp",EDGE,"E3.11.2"),sQuery(id+"F0.wireOp",EDGE,"E3.11.3"),sQuery(id+"F0.wireOp",EDGE,"E3.12.1"),sQuery(id+"F0.wireOp",EDGE,"E3.12.2"),sQuery(id+"F0.wireOp",EDGE,"E3.12.3")])],"isStart":true})],"blendedInto":[makeQuery(id+"F1.opExtrude","CAP_FACE",FACE,{"disambiguationData":[OSD([sQuery(id+"F0.wireOp",EDGE,"E0"),sQuery(id+"F0.wireOp",EDGE,"E1"),sQuery(id+"F0.wireOp",EDGE,"E2.bottom"),sQuery(id+"F0.wireOp",EDGE,"E2.left"),sQuery(id+"F0.wireOp",EDGE,"E2.right"),sQuery(id+"F0.wireOp",EDGE,"E3.1.1"),sQuery(id+"F0.wireOp",EDGE,"E3.1.2"),sQuery(id+"F0.wireOp",EDGE,"E3.1.3"),sQuery(id+"F0.wireOp",EDGE,"E3.2.1"),sQuery(id+"F0.wireOp",EDGE,"E3.2.2"),sQuery(id+"F0.wireOp",EDGE,"E3.2.3"),sQuery(id+"F0.wireOp",EDGE,"E3.3.1"),sQuery(id+"F0.wireOp",EDGE,"E3.3.2"),sQuery(id+"F0.wireOp",EDGE,"E3.3.3"),sQuery(id+"F0.wireOp",EDGE,"E3.4.1"),sQuery(id+"F0.wireOp",EDGE,"E3.4.2"),sQuery(id+"F0.wireOp",EDGE,"E3.4.3"),sQuery(id+"F0.wireOp",EDGE,"E3.5.1"),subQ1,subQ0,sQuery(id+"F0.wireOp",EDGE,"E3.6.1"),sQuery(id+"F0.wireOp",EDGE,"E3.6.2"),sQuery(id+"F0.wireOp",EDGE,"E3.6.3"),sQuery(id+"F0.wireOp",EDGE,"E3.7.1"),sQuery(id+"F0.wireOp",EDGE,"E3.7.2"),sQuery(id+"F0.wireOp",EDGE,"E3.7.3"),sQuery(id+"F0.wireOp",EDGE,"E3.8.1"),sQuery(id+"F0.wireOp",EDGE,"E3.8.2"),sQuery(id+"F0.wireOp",EDGE,"E3.8.3"),sQuery(id+"F0.wireOp",EDGE,"E3.9.1"),sQuery(id+"F0.wireOp",EDGE,"E3.9.2"),sQuery(id+"F0.wireOp",EDGE,"E3.9.3"),sQuery(id+"F0.wireOp",EDGE,"E3.10.1"),sQuery(id+"F0.wireOp",EDGE,"E3.10.2"),sQuery(id+"F0.wireOp",EDGE,"E3.10.3"),sQuery(id+"F0.wireOp",EDGE,"E3.11.1"),sQuery(id+"F0.wireOp",EDGE,"E3.11.2"),sQuery(id+"F0.wireOp",EDGE,"E3.11.3"),sQuery(id+"F0.wireOp",EDGE,"E3.12.1"),sQuery(id+"F0.wireOp",EDGE,"E3.12.2"),sQuery(id+"F0.wireOp",EDGE,"E3.12.3")])],"isStart":true})]}),makeQuery(id+"F1.opExtrude","CAP_EDGE",EDGE,{"disambiguationData":[OSD([subQ0])],"isStart":true})],"blendedInto":[]});}
            var Q72;
            {var subQ0=sQuery(id+"F0.wireOp",EDGE,"E3.5.1");Q72=makeQuery(id+"F3.opChamfer","BLEND_EDGE",EDGE,{"blendedFrom":[makeQuery(id+"F1.opExtrude","SWEPT_EDGE",EDGE,{"disambiguationData":[OSD([subQ0,sQuery(id+"F0.wireOp",EDGE,"E3.5.2")])]}),makeQuery(id+"F1.opExtrude","SWEPT_FACE",FACE,{"disambiguationData":[OSD([subQ0])]})],"blendedInto":[makeQuery(id+"F1.opExtrude","SWEPT_FACE",FACE,{"disambiguationData":[OSD([subQ0])]})]});}
            var Q73;
            {var subQ0=sQuery(id+"F0.wireOp",EDGE,"E3.5.1");var subQ1=sQuery(id+"F0.wireOp",EDGE,"E3.5.2");Q73=makeQuery(id+"F4.opChamfer","BLEND_EDGE",EDGE,{"blendedFrom":[makeQuery(id+"F3.opChamfer","BLEND_EDGE",EDGE,{"blendedFrom":[makeQuery(id+"F1.opExtrude","SWEPT_EDGE",EDGE,{"disambiguationData":[OSD([subQ0,subQ1])]}),makeQuery(id+"F1.opExtrude","CAP_FACE",FACE,{"disambiguationData":[OSD([sQuery(id+"F0.wireOp",EDGE,"E0"),sQuery(id+"F0.wireOp",EDGE,"E1"),sQuery(id+"F0.wireOp",EDGE,"E2.bottom"),sQuery(id+"F0.wireOp",EDGE,"E2.left"),sQuery(id+"F0.wireOp",EDGE,"E2.right"),sQuery(id+"F0.wireOp",EDGE,"E3.1.1"),sQuery(id+"F0.wireOp",EDGE,"E3.1.2"),sQuery(id+"F0.wireOp",EDGE,"E3.1.3"),sQuery(id+"F0.wireOp",EDGE,"E3.2.1"),sQuery(id+"F0.wireOp",EDGE,"E3.2.2"),sQuery(id+"F0.wireOp",EDGE,"E3.2.3"),sQuery(id+"F0.wireOp",EDGE,"E3.3.1"),sQuery(id+"F0.wireOp",EDGE,"E3.3.2"),sQuery(id+"F0.wireOp",EDGE,"E3.3.3"),sQuery(id+"F0.wireOp",EDGE,"E3.4.1"),sQuery(id+"F0.wireOp",EDGE,"E3.4.2"),sQuery(id+"F0.wireOp",EDGE,"E3.4.3"),subQ0,subQ1,sQuery(id+"F0.wireOp",EDGE,"E3.5.3"),sQuery(id+"F0.wireOp",EDGE,"E3.6.1"),sQuery(id+"F0.wireOp",EDGE,"E3.6.2"),sQuery(id+"F0.wireOp",EDGE,"E3.6.3"),sQuery(id+"F0.wireOp",EDGE,"E3.7.1"),sQuery(id+"F0.wireOp",EDGE,"E3.7.2"),sQuery(id+"F0.wireOp",EDGE,"E3.7.3"),sQuery(id+"F0.wireOp",EDGE,"E3.8.1"),sQuery(id+"F0.wireOp",EDGE,"E3.8.2"),sQuery(id+"F0.wireOp",EDGE,"E3.8.3"),sQuery(id+"F0.wireOp",EDGE,"E3.9.1"),sQuery(id+"F0.wireOp",EDGE,"E3.9.2"),sQuery(id+"F0.wireOp",EDGE,"E3.9.3"),sQuery(id+"F0.wireOp",EDGE,"E3.10.1"),sQuery(id+"F0.wireOp",EDGE,"E3.10.2"),sQuery(id+"F0.wireOp",EDGE,"E3.10.3"),sQuery(id+"F0.wireOp",EDGE,"E3.11.1"),sQuery(id+"F0.wireOp",EDGE,"E3.11.2"),sQuery(id+"F0.wireOp",EDGE,"E3.11.3"),sQuery(id+"F0.wireOp",EDGE,"E3.12.1"),sQuery(id+"F0.wireOp",EDGE,"E3.12.2"),sQuery(id+"F0.wireOp",EDGE,"E3.12.3")])],"isStart":false})],"blendedInto":[makeQuery(id+"F1.opExtrude","CAP_FACE",FACE,{"disambiguationData":[OSD([sQuery(id+"F0.wireOp",EDGE,"E0"),sQuery(id+"F0.wireOp",EDGE,"E1"),sQuery(id+"F0.wireOp",EDGE,"E2.bottom"),sQuery(id+"F0.wireOp",EDGE,"E2.left"),sQuery(id+"F0.wireOp",EDGE,"E2.right"),sQuery(id+"F0.wireOp",EDGE,"E3.1.1"),sQuery(id+"F0.wireOp",EDGE,"E3.1.2"),sQuery(id+"F0.wireOp",EDGE,"E3.1.3"),sQuery(id+"F0.wireOp",EDGE,"E3.2.1"),sQuery(id+"F0.wireOp",EDGE,"E3.2.2"),sQuery(id+"F0.wireOp",EDGE,"E3.2.3"),sQuery(id+"F0.wireOp",EDGE,"E3.3.1"),sQuery(id+"F0.wireOp",EDGE,"E3.3.2"),sQuery(id+"F0.wireOp",EDGE,"E3.3.3"),sQuery(id+"F0.wireOp",EDGE,"E3.4.1"),sQuery(id+"F0.wireOp",EDGE,"E3.4.2"),sQuery(id+"F0.wireOp",EDGE,"E3.4.3"),subQ0,subQ1,sQuery(id+"F0.wireOp",EDGE,"E3.5.3"),sQuery(id+"F0.wireOp",EDGE,"E3.6.1"),sQuery(id+"F0.wireOp",EDGE,"E3.6.2"),sQuery(id+"F0.wireOp",EDGE,"E3.6.3"),sQuery(id+"F0.wireOp",EDGE,"E3.7.1"),sQuery(id+"F0.wireOp",EDGE,"E3.7.2"),sQuery(id+"F0.wireOp",EDGE,"E3.7.3"),sQuery(id+"F0.wireOp",EDGE,"E3.8.1"),sQuery(id+"F0.wireOp",EDGE,"E3.8.2"),sQuery(id+"F0.wireOp",EDGE,"E3.8.3"),sQuery(id+"F0.wireOp",EDGE,"E3.9.1"),sQuery(id+"F0.wireOp",EDGE,"E3.9.2"),sQuery(id+"F0.wireOp",EDGE,"E3.9.3"),sQuery(id+"F0.wireOp",EDGE,"E3.10.1"),sQuery(id+"F0.wireOp",EDGE,"E3.10.2"),sQuery(id+"F0.wireOp",EDGE,"E3.10.3"),sQuery(id+"F0.wireOp",EDGE,"E3.11.1"),sQuery(id+"F0.wireOp",EDGE,"E3.11.2"),sQuery(id+"F0.wireOp",EDGE,"E3.11.3"),sQuery(id+"F0.wireOp",EDGE,"E3.12.1"),sQuery(id+"F0.wireOp",EDGE,"E3.12.2"),sQuery(id+"F0.wireOp",EDGE,"E3.12.3")])],"isStart":false})]}),makeQuery(id+"F1.opExtrude","CAP_EDGE",EDGE,{"disambiguationData":[OSD([subQ0])],"isStart":false})],"blendedInto":[]});}
            var Q74;
            {var subQ0=sQuery(id+"F0.wireOp",EDGE,"E3.5.3");var subQ1=sQuery(id+"F0.wireOp",EDGE,"E3.5.2");Q74=makeQuery(id+"F4.opChamfer","BLEND_EDGE",EDGE,{"blendedFrom":[makeQuery(id+"F3.opChamfer","BLEND_EDGE",EDGE,{"blendedFrom":[makeQuery(id+"F1.opExtrude","SWEPT_EDGE",EDGE,{"disambiguationData":[OSD([subQ1,subQ0])]}),makeQuery(id+"F1.opExtrude","CAP_FACE",FACE,{"disambiguationData":[OSD([sQuery(id+"F0.wireOp",EDGE,"E0"),sQuery(id+"F0.wireOp",EDGE,"E1"),sQuery(id+"F0.wireOp",EDGE,"E2.bottom"),sQuery(id+"F0.wireOp",EDGE,"E2.left"),sQuery(id+"F0.wireOp",EDGE,"E2.right"),sQuery(id+"F0.wireOp",EDGE,"E3.1.1"),sQuery(id+"F0.wireOp",EDGE,"E3.1.2"),sQuery(id+"F0.wireOp",EDGE,"E3.1.3"),sQuery(id+"F0.wireOp",EDGE,"E3.2.1"),sQuery(id+"F0.wireOp",EDGE,"E3.2.2"),sQuery(id+"F0.wireOp",EDGE,"E3.2.3"),sQuery(id+"F0.wireOp",EDGE,"E3.3.1"),sQuery(id+"F0.wireOp",EDGE,"E3.3.2"),sQuery(id+"F0.wireOp",EDGE,"E3.3.3"),sQuery(id+"F0.wireOp",EDGE,"E3.4.1"),sQuery(id+"F0.wireOp",EDGE,"E3.4.2"),sQuery(id+"F0.wireOp",EDGE,"E3.4.3"),sQuery(id+"F0.wireOp",EDGE,"E3.5.1"),subQ1,subQ0,sQuery(id+"F0.wireOp",EDGE,"E3.6.1"),sQuery(id+"F0.wireOp",EDGE,"E3.6.2"),sQuery(id+"F0.wireOp",EDGE,"E3.6.3"),sQuery(id+"F0.wireOp",EDGE,"E3.7.1"),sQuery(id+"F0.wireOp",EDGE,"E3.7.2"),sQuery(id+"F0.wireOp",EDGE,"E3.7.3"),sQuery(id+"F0.wireOp",EDGE,"E3.8.1"),sQuery(id+"F0.wireOp",EDGE,"E3.8.2"),sQuery(id+"F0.wireOp",EDGE,"E3.8.3"),sQuery(id+"F0.wireOp",EDGE,"E3.9.1"),sQuery(id+"F0.wireOp",EDGE,"E3.9.2"),sQuery(id+"F0.wireOp",EDGE,"E3.9.3"),sQuery(id+"F0.wireOp",EDGE,"E3.10.1"),sQuery(id+"F0.wireOp",EDGE,"E3.10.2"),sQuery(id+"F0.wireOp",EDGE,"E3.10.3"),sQuery(id+"F0.wireOp",EDGE,"E3.11.1"),sQuery(id+"F0.wireOp",EDGE,"E3.11.2"),sQuery(id+"F0.wireOp",EDGE,"E3.11.3"),sQuery(id+"F0.wireOp",EDGE,"E3.12.1"),sQuery(id+"F0.wireOp",EDGE,"E3.12.2"),sQuery(id+"F0.wireOp",EDGE,"E3.12.3")])],"isStart":false})],"blendedInto":[makeQuery(id+"F1.opExtrude","CAP_FACE",FACE,{"disambiguationData":[OSD([sQuery(id+"F0.wireOp",EDGE,"E0"),sQuery(id+"F0.wireOp",EDGE,"E1"),sQuery(id+"F0.wireOp",EDGE,"E2.bottom"),sQuery(id+"F0.wireOp",EDGE,"E2.left"),sQuery(id+"F0.wireOp",EDGE,"E2.right"),sQuery(id+"F0.wireOp",EDGE,"E3.1.1"),sQuery(id+"F0.wireOp",EDGE,"E3.1.2"),sQuery(id+"F0.wireOp",EDGE,"E3.1.3"),sQuery(id+"F0.wireOp",EDGE,"E3.2.1"),sQuery(id+"F0.wireOp",EDGE,"E3.2.2"),sQuery(id+"F0.wireOp",EDGE,"E3.2.3"),sQuery(id+"F0.wireOp",EDGE,"E3.3.1"),sQuery(id+"F0.wireOp",EDGE,"E3.3.2"),sQuery(id+"F0.wireOp",EDGE,"E3.3.3"),sQuery(id+"F0.wireOp",EDGE,"E3.4.1"),sQuery(id+"F0.wireOp",EDGE,"E3.4.2"),sQuery(id+"F0.wireOp",EDGE,"E3.4.3"),sQuery(id+"F0.wireOp",EDGE,"E3.5.1"),subQ1,subQ0,sQuery(id+"F0.wireOp",EDGE,"E3.6.1"),sQuery(id+"F0.wireOp",EDGE,"E3.6.2"),sQuery(id+"F0.wireOp",EDGE,"E3.6.3"),sQuery(id+"F0.wireOp",EDGE,"E3.7.1"),sQuery(id+"F0.wireOp",EDGE,"E3.7.2"),sQuery(id+"F0.wireOp",EDGE,"E3.7.3"),sQuery(id+"F0.wireOp",EDGE,"E3.8.1"),sQuery(id+"F0.wireOp",EDGE,"E3.8.2"),sQuery(id+"F0.wireOp",EDGE,"E3.8.3"),sQuery(id+"F0.wireOp",EDGE,"E3.9.1"),sQuery(id+"F0.wireOp",EDGE,"E3.9.2"),sQuery(id+"F0.wireOp",EDGE,"E3.9.3"),sQuery(id+"F0.wireOp",EDGE,"E3.10.1"),sQuery(id+"F0.wireOp",EDGE,"E3.10.2"),sQuery(id+"F0.wireOp",EDGE,"E3.10.3"),sQuery(id+"F0.wireOp",EDGE,"E3.11.1"),sQuery(id+"F0.wireOp",EDGE,"E3.11.2"),sQuery(id+"F0.wireOp",EDGE,"E3.11.3"),sQuery(id+"F0.wireOp",EDGE,"E3.12.1"),sQuery(id+"F0.wireOp",EDGE,"E3.12.2"),sQuery(id+"F0.wireOp",EDGE,"E3.12.3")])],"isStart":false})]}),makeQuery(id+"F1.opExtrude","CAP_EDGE",EDGE,{"disambiguationData":[OSD([subQ0])],"isStart":false})],"blendedInto":[]});}
            var Q75;
            {var subQ0=sQuery(id+"F0.wireOp",EDGE,"E3.4.1");var subQ1=sQuery(id+"F0.wireOp",EDGE,"E3.4.2");Q75=makeQuery(id+"F4.opChamfer","BLEND_EDGE",EDGE,{"blendedFrom":[makeQuery(id+"F3.opChamfer","BLEND_EDGE",EDGE,{"blendedFrom":[makeQuery(id+"F1.opExtrude","SWEPT_EDGE",EDGE,{"disambiguationData":[OSD([subQ0,subQ1])]}),makeQuery(id+"F1.opExtrude","CAP_FACE",FACE,{"disambiguationData":[OSD([sQuery(id+"F0.wireOp",EDGE,"E0"),sQuery(id+"F0.wireOp",EDGE,"E1"),sQuery(id+"F0.wireOp",EDGE,"E2.bottom"),sQuery(id+"F0.wireOp",EDGE,"E2.left"),sQuery(id+"F0.wireOp",EDGE,"E2.right"),sQuery(id+"F0.wireOp",EDGE,"E3.1.1"),sQuery(id+"F0.wireOp",EDGE,"E3.1.2"),sQuery(id+"F0.wireOp",EDGE,"E3.1.3"),sQuery(id+"F0.wireOp",EDGE,"E3.2.1"),sQuery(id+"F0.wireOp",EDGE,"E3.2.2"),sQuery(id+"F0.wireOp",EDGE,"E3.2.3"),sQuery(id+"F0.wireOp",EDGE,"E3.3.1"),sQuery(id+"F0.wireOp",EDGE,"E3.3.2"),sQuery(id+"F0.wireOp",EDGE,"E3.3.3"),subQ0,subQ1,sQuery(id+"F0.wireOp",EDGE,"E3.4.3"),sQuery(id+"F0.wireOp",EDGE,"E3.5.1"),sQuery(id+"F0.wireOp",EDGE,"E3.5.2"),sQuery(id+"F0.wireOp",EDGE,"E3.5.3"),sQuery(id+"F0.wireOp",EDGE,"E3.6.1"),sQuery(id+"F0.wireOp",EDGE,"E3.6.2"),sQuery(id+"F0.wireOp",EDGE,"E3.6.3"),sQuery(id+"F0.wireOp",EDGE,"E3.7.1"),sQuery(id+"F0.wireOp",EDGE,"E3.7.2"),sQuery(id+"F0.wireOp",EDGE,"E3.7.3"),sQuery(id+"F0.wireOp",EDGE,"E3.8.1"),sQuery(id+"F0.wireOp",EDGE,"E3.8.2"),sQuery(id+"F0.wireOp",EDGE,"E3.8.3"),sQuery(id+"F0.wireOp",EDGE,"E3.9.1"),sQuery(id+"F0.wireOp",EDGE,"E3.9.2"),sQuery(id+"F0.wireOp",EDGE,"E3.9.3"),sQuery(id+"F0.wireOp",EDGE,"E3.10.1"),sQuery(id+"F0.wireOp",EDGE,"E3.10.2"),sQuery(id+"F0.wireOp",EDGE,"E3.10.3"),sQuery(id+"F0.wireOp",EDGE,"E3.11.1"),sQuery(id+"F0.wireOp",EDGE,"E3.11.2"),sQuery(id+"F0.wireOp",EDGE,"E3.11.3"),sQuery(id+"F0.wireOp",EDGE,"E3.12.1"),sQuery(id+"F0.wireOp",EDGE,"E3.12.2"),sQuery(id+"F0.wireOp",EDGE,"E3.12.3")])],"isStart":false})],"blendedInto":[makeQuery(id+"F1.opExtrude","CAP_FACE",FACE,{"disambiguationData":[OSD([sQuery(id+"F0.wireOp",EDGE,"E0"),sQuery(id+"F0.wireOp",EDGE,"E1"),sQuery(id+"F0.wireOp",EDGE,"E2.bottom"),sQuery(id+"F0.wireOp",EDGE,"E2.left"),sQuery(id+"F0.wireOp",EDGE,"E2.right"),sQuery(id+"F0.wireOp",EDGE,"E3.1.1"),sQuery(id+"F0.wireOp",EDGE,"E3.1.2"),sQuery(id+"F0.wireOp",EDGE,"E3.1.3"),sQuery(id+"F0.wireOp",EDGE,"E3.2.1"),sQuery(id+"F0.wireOp",EDGE,"E3.2.2"),sQuery(id+"F0.wireOp",EDGE,"E3.2.3"),sQuery(id+"F0.wireOp",EDGE,"E3.3.1"),sQuery(id+"F0.wireOp",EDGE,"E3.3.2"),sQuery(id+"F0.wireOp",EDGE,"E3.3.3"),subQ0,subQ1,sQuery(id+"F0.wireOp",EDGE,"E3.4.3"),sQuery(id+"F0.wireOp",EDGE,"E3.5.1"),sQuery(id+"F0.wireOp",EDGE,"E3.5.2"),sQuery(id+"F0.wireOp",EDGE,"E3.5.3"),sQuery(id+"F0.wireOp",EDGE,"E3.6.1"),sQuery(id+"F0.wireOp",EDGE,"E3.6.2"),sQuery(id+"F0.wireOp",EDGE,"E3.6.3"),sQuery(id+"F0.wireOp",EDGE,"E3.7.1"),sQuery(id+"F0.wireOp",EDGE,"E3.7.2"),sQuery(id+"F0.wireOp",EDGE,"E3.7.3"),sQuery(id+"F0.wireOp",EDGE,"E3.8.1"),sQuery(id+"F0.wireOp",EDGE,"E3.8.2"),sQuery(id+"F0.wireOp",EDGE,"E3.8.3"),sQuery(id+"F0.wireOp",EDGE,"E3.9.1"),sQuery(id+"F0.wireOp",EDGE,"E3.9.2"),sQuery(id+"F0.wireOp",EDGE,"E3.9.3"),sQuery(id+"F0.wireOp",EDGE,"E3.10.1"),sQuery(id+"F0.wireOp",EDGE,"E3.10.2"),sQuery(id+"F0.wireOp",EDGE,"E3.10.3"),sQuery(id+"F0.wireOp",EDGE,"E3.11.1"),sQuery(id+"F0.wireOp",EDGE,"E3.11.2"),sQuery(id+"F0.wireOp",EDGE,"E3.11.3"),sQuery(id+"F0.wireOp",EDGE,"E3.12.1"),sQuery(id+"F0.wireOp",EDGE,"E3.12.2"),sQuery(id+"F0.wireOp",EDGE,"E3.12.3")])],"isStart":false})]}),makeQuery(id+"F1.opExtrude","CAP_EDGE",EDGE,{"disambiguationData":[OSD([subQ0])],"isStart":false})],"blendedInto":[]});}
            var Q76;
            {var subQ0=sQuery(id+"F0.wireOp",EDGE,"E3.6.3");var subQ1=sQuery(id+"F0.wireOp",EDGE,"E3.6.2");Q76=makeQuery(id+"F4.opChamfer","BLEND_EDGE",EDGE,{"blendedFrom":[makeQuery(id+"F3.opChamfer","BLEND_EDGE",EDGE,{"blendedFrom":[makeQuery(id+"F1.opExtrude","SWEPT_EDGE",EDGE,{"disambiguationData":[OSD([subQ1,subQ0])]}),makeQuery(id+"F1.opExtrude","CAP_FACE",FACE,{"disambiguationData":[OSD([sQuery(id+"F0.wireOp",EDGE,"E0"),sQuery(id+"F0.wireOp",EDGE,"E1"),sQuery(id+"F0.wireOp",EDGE,"E2.bottom"),sQuery(id+"F0.wireOp",EDGE,"E2.left"),sQuery(id+"F0.wireOp",EDGE,"E2.right"),sQuery(id+"F0.wireOp",EDGE,"E3.1.1"),sQuery(id+"F0.wireOp",EDGE,"E3.1.2"),sQuery(id+"F0.wireOp",EDGE,"E3.1.3"),sQuery(id+"F0.wireOp",EDGE,"E3.2.1"),sQuery(id+"F0.wireOp",EDGE,"E3.2.2"),sQuery(id+"F0.wireOp",EDGE,"E3.2.3"),sQuery(id+"F0.wireOp",EDGE,"E3.3.1"),sQuery(id+"F0.wireOp",EDGE,"E3.3.2"),sQuery(id+"F0.wireOp",EDGE,"E3.3.3"),sQuery(id+"F0.wireOp",EDGE,"E3.4.1"),sQuery(id+"F0.wireOp",EDGE,"E3.4.2"),sQuery(id+"F0.wireOp",EDGE,"E3.4.3"),sQuery(id+"F0.wireOp",EDGE,"E3.5.1"),sQuery(id+"F0.wireOp",EDGE,"E3.5.2"),sQuery(id+"F0.wireOp",EDGE,"E3.5.3"),sQuery(id+"F0.wireOp",EDGE,"E3.6.1"),subQ1,subQ0,sQuery(id+"F0.wireOp",EDGE,"E3.7.1"),sQuery(id+"F0.wireOp",EDGE,"E3.7.2"),sQuery(id+"F0.wireOp",EDGE,"E3.7.3"),sQuery(id+"F0.wireOp",EDGE,"E3.8.1"),sQuery(id+"F0.wireOp",EDGE,"E3.8.2"),sQuery(id+"F0.wireOp",EDGE,"E3.8.3"),sQuery(id+"F0.wireOp",EDGE,"E3.9.1"),sQuery(id+"F0.wireOp",EDGE,"E3.9.2"),sQuery(id+"F0.wireOp",EDGE,"E3.9.3"),sQuery(id+"F0.wireOp",EDGE,"E3.10.1"),sQuery(id+"F0.wireOp",EDGE,"E3.10.2"),sQuery(id+"F0.wireOp",EDGE,"E3.10.3"),sQuery(id+"F0.wireOp",EDGE,"E3.11.1"),sQuery(id+"F0.wireOp",EDGE,"E3.11.2"),sQuery(id+"F0.wireOp",EDGE,"E3.11.3"),sQuery(id+"F0.wireOp",EDGE,"E3.12.1"),sQuery(id+"F0.wireOp",EDGE,"E3.12.2"),sQuery(id+"F0.wireOp",EDGE,"E3.12.3")])],"isStart":false})],"blendedInto":[makeQuery(id+"F1.opExtrude","CAP_FACE",FACE,{"disambiguationData":[OSD([sQuery(id+"F0.wireOp",EDGE,"E0"),sQuery(id+"F0.wireOp",EDGE,"E1"),sQuery(id+"F0.wireOp",EDGE,"E2.bottom"),sQuery(id+"F0.wireOp",EDGE,"E2.left"),sQuery(id+"F0.wireOp",EDGE,"E2.right"),sQuery(id+"F0.wireOp",EDGE,"E3.1.1"),sQuery(id+"F0.wireOp",EDGE,"E3.1.2"),sQuery(id+"F0.wireOp",EDGE,"E3.1.3"),sQuery(id+"F0.wireOp",EDGE,"E3.2.1"),sQuery(id+"F0.wireOp",EDGE,"E3.2.2"),sQuery(id+"F0.wireOp",EDGE,"E3.2.3"),sQuery(id+"F0.wireOp",EDGE,"E3.3.1"),sQuery(id+"F0.wireOp",EDGE,"E3.3.2"),sQuery(id+"F0.wireOp",EDGE,"E3.3.3"),sQuery(id+"F0.wireOp",EDGE,"E3.4.1"),sQuery(id+"F0.wireOp",EDGE,"E3.4.2"),sQuery(id+"F0.wireOp",EDGE,"E3.4.3"),sQuery(id+"F0.wireOp",EDGE,"E3.5.1"),sQuery(id+"F0.wireOp",EDGE,"E3.5.2"),sQuery(id+"F0.wireOp",EDGE,"E3.5.3"),sQuery(id+"F0.wireOp",EDGE,"E3.6.1"),subQ1,subQ0,sQuery(id+"F0.wireOp",EDGE,"E3.7.1"),sQuery(id+"F0.wireOp",EDGE,"E3.7.2"),sQuery(id+"F0.wireOp",EDGE,"E3.7.3"),sQuery(id+"F0.wireOp",EDGE,"E3.8.1"),sQuery(id+"F0.wireOp",EDGE,"E3.8.2"),sQuery(id+"F0.wireOp",EDGE,"E3.8.3"),sQuery(id+"F0.wireOp",EDGE,"E3.9.1"),sQuery(id+"F0.wireOp",EDGE,"E3.9.2"),sQuery(id+"F0.wireOp",EDGE,"E3.9.3"),sQuery(id+"F0.wireOp",EDGE,"E3.10.1"),sQuery(id+"F0.wireOp",EDGE,"E3.10.2"),sQuery(id+"F0.wireOp",EDGE,"E3.10.3"),sQuery(id+"F0.wireOp",EDGE,"E3.11.1"),sQuery(id+"F0.wireOp",EDGE,"E3.11.2"),sQuery(id+"F0.wireOp",EDGE,"E3.11.3"),sQuery(id+"F0.wireOp",EDGE,"E3.12.1"),sQuery(id+"F0.wireOp",EDGE,"E3.12.2"),sQuery(id+"F0.wireOp",EDGE,"E3.12.3")])],"isStart":false})]}),makeQuery(id+"F1.opExtrude","CAP_EDGE",EDGE,{"disambiguationData":[OSD([subQ0])],"isStart":false})],"blendedInto":[]});}
            var Q77;
            {var subQ0=sQuery(id+"F0.wireOp",EDGE,"E3.4.3");var subQ1=sQuery(id+"F0.wireOp",EDGE,"E3.4.2");Q77=makeQuery(id+"F4.opChamfer","BLEND_EDGE",EDGE,{"blendedFrom":[makeQuery(id+"F3.opChamfer","BLEND_EDGE",EDGE,{"blendedFrom":[makeQuery(id+"F1.opExtrude","SWEPT_EDGE",EDGE,{"disambiguationData":[OSD([subQ1,subQ0])]}),makeQuery(id+"F1.opExtrude","CAP_FACE",FACE,{"disambiguationData":[OSD([sQuery(id+"F0.wireOp",EDGE,"E0"),sQuery(id+"F0.wireOp",EDGE,"E1"),sQuery(id+"F0.wireOp",EDGE,"E2.bottom"),sQuery(id+"F0.wireOp",EDGE,"E2.left"),sQuery(id+"F0.wireOp",EDGE,"E2.right"),sQuery(id+"F0.wireOp",EDGE,"E3.1.1"),sQuery(id+"F0.wireOp",EDGE,"E3.1.2"),sQuery(id+"F0.wireOp",EDGE,"E3.1.3"),sQuery(id+"F0.wireOp",EDGE,"E3.2.1"),sQuery(id+"F0.wireOp",EDGE,"E3.2.2"),sQuery(id+"F0.wireOp",EDGE,"E3.2.3"),sQuery(id+"F0.wireOp",EDGE,"E3.3.1"),sQuery(id+"F0.wireOp",EDGE,"E3.3.2"),sQuery(id+"F0.wireOp",EDGE,"E3.3.3"),sQuery(id+"F0.wireOp",EDGE,"E3.4.1"),subQ1,subQ0,sQuery(id+"F0.wireOp",EDGE,"E3.5.1"),sQuery(id+"F0.wireOp",EDGE,"E3.5.2"),sQuery(id+"F0.wireOp",EDGE,"E3.5.3"),sQuery(id+"F0.wireOp",EDGE,"E3.6.1"),sQuery(id+"F0.wireOp",EDGE,"E3.6.2"),sQuery(id+"F0.wireOp",EDGE,"E3.6.3"),sQuery(id+"F0.wireOp",EDGE,"E3.7.1"),sQuery(id+"F0.wireOp",EDGE,"E3.7.2"),sQuery(id+"F0.wireOp",EDGE,"E3.7.3"),sQuery(id+"F0.wireOp",EDGE,"E3.8.1"),sQuery(id+"F0.wireOp",EDGE,"E3.8.2"),sQuery(id+"F0.wireOp",EDGE,"E3.8.3"),sQuery(id+"F0.wireOp",EDGE,"E3.9.1"),sQuery(id+"F0.wireOp",EDGE,"E3.9.2"),sQuery(id+"F0.wireOp",EDGE,"E3.9.3"),sQuery(id+"F0.wireOp",EDGE,"E3.10.1"),sQuery(id+"F0.wireOp",EDGE,"E3.10.2"),sQuery(id+"F0.wireOp",EDGE,"E3.10.3"),sQuery(id+"F0.wireOp",EDGE,"E3.11.1"),sQuery(id+"F0.wireOp",EDGE,"E3.11.2"),sQuery(id+"F0.wireOp",EDGE,"E3.11.3"),sQuery(id+"F0.wireOp",EDGE,"E3.12.1"),sQuery(id+"F0.wireOp",EDGE,"E3.12.2"),sQuery(id+"F0.wireOp",EDGE,"E3.12.3")])],"isStart":false})],"blendedInto":[makeQuery(id+"F1.opExtrude","CAP_FACE",FACE,{"disambiguationData":[OSD([sQuery(id+"F0.wireOp",EDGE,"E0"),sQuery(id+"F0.wireOp",EDGE,"E1"),sQuery(id+"F0.wireOp",EDGE,"E2.bottom"),sQuery(id+"F0.wireOp",EDGE,"E2.left"),sQuery(id+"F0.wireOp",EDGE,"E2.right"),sQuery(id+"F0.wireOp",EDGE,"E3.1.1"),sQuery(id+"F0.wireOp",EDGE,"E3.1.2"),sQuery(id+"F0.wireOp",EDGE,"E3.1.3"),sQuery(id+"F0.wireOp",EDGE,"E3.2.1"),sQuery(id+"F0.wireOp",EDGE,"E3.2.2"),sQuery(id+"F0.wireOp",EDGE,"E3.2.3"),sQuery(id+"F0.wireOp",EDGE,"E3.3.1"),sQuery(id+"F0.wireOp",EDGE,"E3.3.2"),sQuery(id+"F0.wireOp",EDGE,"E3.3.3"),sQuery(id+"F0.wireOp",EDGE,"E3.4.1"),subQ1,subQ0,sQuery(id+"F0.wireOp",EDGE,"E3.5.1"),sQuery(id+"F0.wireOp",EDGE,"E3.5.2"),sQuery(id+"F0.wireOp",EDGE,"E3.5.3"),sQuery(id+"F0.wireOp",EDGE,"E3.6.1"),sQuery(id+"F0.wireOp",EDGE,"E3.6.2"),sQuery(id+"F0.wireOp",EDGE,"E3.6.3"),sQuery(id+"F0.wireOp",EDGE,"E3.7.1"),sQuery(id+"F0.wireOp",EDGE,"E3.7.2"),sQuery(id+"F0.wireOp",EDGE,"E3.7.3"),sQuery(id+"F0.wireOp",EDGE,"E3.8.1"),sQuery(id+"F0.wireOp",EDGE,"E3.8.2"),sQuery(id+"F0.wireOp",EDGE,"E3.8.3"),sQuery(id+"F0.wireOp",EDGE,"E3.9.1"),sQuery(id+"F0.wireOp",EDGE,"E3.9.2"),sQuery(id+"F0.wireOp",EDGE,"E3.9.3"),sQuery(id+"F0.wireOp",EDGE,"E3.10.1"),sQuery(id+"F0.wireOp",EDGE,"E3.10.2"),sQuery(id+"F0.wireOp",EDGE,"E3.10.3"),sQuery(id+"F0.wireOp",EDGE,"E3.11.1"),sQuery(id+"F0.wireOp",EDGE,"E3.11.2"),sQuery(id+"F0.wireOp",EDGE,"E3.11.3"),sQuery(id+"F0.wireOp",EDGE,"E3.12.1"),sQuery(id+"F0.wireOp",EDGE,"E3.12.2"),sQuery(id+"F0.wireOp",EDGE,"E3.12.3")])],"isStart":false})]}),makeQuery(id+"F1.opExtrude","CAP_EDGE",EDGE,{"disambiguationData":[OSD([subQ0])],"isStart":false})],"blendedInto":[]});}
            chamfer(context, id + "F11", {"entities" : qUnion([Q0, Q1, Q2, Q3, Q4, Q5, Q6, Q7, Q8, Q9, Q10, Q11, Q12, Q13, Q14, Q15, Q16, Q17, Q18, Q19, Q20, Q21, Q22, Q23, Q24, Q25, Q26, Q27, Q28, Q29, Q30, Q31, Q32, Q33, Q34, Q35, Q36, Q37, Q38, Q39, Q40, Q41, Q42, Q43, Q44, Q45, Q46, Q47, Q48, Q49, Q50, Q51, Q52, Q53, Q54, Q55, Q56, Q57, Q58, Q59, Q60, Q61, Q62, Q63, Q64, Q65, Q66, Q67, Q68, Q69, Q70, Q71, Q72, Q73, Q74, Q75, Q76, Q77]), "width" : 1.02 * mm, "tangentPropagation" : true});
        }
        {
            var Q0;
            {var subQ0=sQuery(id+"F0.wireOp",EDGE,"E3.1.2");var subQ1=sQuery(id+"F0.wireOp",EDGE,"E3.1.3");Q0=makeQuery(id+"F4.opChamfer","BLEND_EDGE",EDGE,{"blendedFrom":[makeQuery(id+"F3.opChamfer","BLEND_EDGE",EDGE,{"blendedFrom":[makeQuery(id+"F1.opExtrude","SWEPT_EDGE",EDGE,{"disambiguationData":[OSD([subQ0,subQ1])]}),makeQuery(id+"F1.opExtrude","CAP_FACE",FACE,{"disambiguationData":[OSD([sQuery(id+"F0.wireOp",EDGE,"E0"),sQuery(id+"F0.wireOp",EDGE,"E1"),sQuery(id+"F0.wireOp",EDGE,"E2.bottom"),sQuery(id+"F0.wireOp",EDGE,"E2.left"),sQuery(id+"F0.wireOp",EDGE,"E2.right"),sQuery(id+"F0.wireOp",EDGE,"E3.1.1"),subQ0,subQ1,sQuery(id+"F0.wireOp",EDGE,"E3.2.1"),sQuery(id+"F0.wireOp",EDGE,"E3.2.2"),sQuery(id+"F0.wireOp",EDGE,"E3.2.3"),sQuery(id+"F0.wireOp",EDGE,"E3.3.1"),sQuery(id+"F0.wireOp",EDGE,"E3.3.2"),sQuery(id+"F0.wireOp",EDGE,"E3.3.3"),sQuery(id+"F0.wireOp",EDGE,"E3.4.1"),sQuery(id+"F0.wireOp",EDGE,"E3.4.2"),sQuery(id+"F0.wireOp",EDGE,"E3.4.3"),sQuery(id+"F0.wireOp",EDGE,"E3.5.1"),sQuery(id+"F0.wireOp",EDGE,"E3.5.2"),sQuery(id+"F0.wireOp",EDGE,"E3.5.3"),sQuery(id+"F0.wireOp",EDGE,"E3.6.1"),sQuery(id+"F0.wireOp",EDGE,"E3.6.2"),sQuery(id+"F0.wireOp",EDGE,"E3.6.3"),sQuery(id+"F0.wireOp",EDGE,"E3.7.1"),sQuery(id+"F0.wireOp",EDGE,"E3.7.2"),sQuery(id+"F0.wireOp",EDGE,"E3.7.3"),sQuery(id+"F0.wireOp",EDGE,"E3.8.1"),sQuery(id+"F0.wireOp",EDGE,"E3.8.2"),sQuery(id+"F0.wireOp",EDGE,"E3.8.3"),sQuery(id+"F0.wireOp",EDGE,"E3.9.1"),sQuery(id+"F0.wireOp",EDGE,"E3.9.2"),sQuery(id+"F0.wireOp",EDGE,"E3.9.3"),sQuery(id+"F0.wireOp",EDGE,"E3.10.1"),sQuery(id+"F0.wireOp",EDGE,"E3.10.2"),sQuery(id+"F0.wireOp",EDGE,"E3.10.3"),sQuery(id+"F0.wireOp",EDGE,"E3.11.1"),sQuery(id+"F0.wireOp",EDGE,"E3.11.2"),sQuery(id+"F0.wireOp",EDGE,"E3.11.3"),sQuery(id+"F0.wireOp",EDGE,"E3.12.1"),sQuery(id+"F0.wireOp",EDGE,"E3.12.2"),sQuery(id+"F0.wireOp",EDGE,"E3.12.3")])],"isStart":false})],"blendedInto":[makeQuery(id+"F1.opExtrude","CAP_FACE",FACE,{"disambiguationData":[OSD([sQuery(id+"F0.wireOp",EDGE,"E0"),sQuery(id+"F0.wireOp",EDGE,"E1"),sQuery(id+"F0.wireOp",EDGE,"E2.bottom"),sQuery(id+"F0.wireOp",EDGE,"E2.left"),sQuery(id+"F0.wireOp",EDGE,"E2.right"),sQuery(id+"F0.wireOp",EDGE,"E3.1.1"),subQ0,subQ1,sQuery(id+"F0.wireOp",EDGE,"E3.2.1"),sQuery(id+"F0.wireOp",EDGE,"E3.2.2"),sQuery(id+"F0.wireOp",EDGE,"E3.2.3"),sQuery(id+"F0.wireOp",EDGE,"E3.3.1"),sQuery(id+"F0.wireOp",EDGE,"E3.3.2"),sQuery(id+"F0.wireOp",EDGE,"E3.3.3"),sQuery(id+"F0.wireOp",EDGE,"E3.4.1"),sQuery(id+"F0.wireOp",EDGE,"E3.4.2"),sQuery(id+"F0.wireOp",EDGE,"E3.4.3"),sQuery(id+"F0.wireOp",EDGE,"E3.5.1"),sQuery(id+"F0.wireOp",EDGE,"E3.5.2"),sQuery(id+"F0.wireOp",EDGE,"E3.5.3"),sQuery(id+"F0.wireOp",EDGE,"E3.6.1"),sQuery(id+"F0.wireOp",EDGE,"E3.6.2"),sQuery(id+"F0.wireOp",EDGE,"E3.6.3"),sQuery(id+"F0.wireOp",EDGE,"E3.7.1"),sQuery(id+"F0.wireOp",EDGE,"E3.7.2"),sQuery(id+"F0.wireOp",EDGE,"E3.7.3"),sQuery(id+"F0.wireOp",EDGE,"E3.8.1"),sQuery(id+"F0.wireOp",EDGE,"E3.8.2"),sQuery(id+"F0.wireOp",EDGE,"E3.8.3"),sQuery(id+"F0.wireOp",EDGE,"E3.9.1"),sQuery(id+"F0.wireOp",EDGE,"E3.9.2"),sQuery(id+"F0.wireOp",EDGE,"E3.9.3"),sQuery(id+"F0.wireOp",EDGE,"E3.10.1"),sQuery(id+"F0.wireOp",EDGE,"E3.10.2"),sQuery(id+"F0.wireOp",EDGE,"E3.10.3"),sQuery(id+"F0.wireOp",EDGE,"E3.11.1"),sQuery(id+"F0.wireOp",EDGE,"E3.11.2"),sQuery(id+"F0.wireOp",EDGE,"E3.11.3"),sQuery(id+"F0.wireOp",EDGE,"E3.12.1"),sQuery(id+"F0.wireOp",EDGE,"E3.12.2"),sQuery(id+"F0.wireOp",EDGE,"E3.12.3")])],"isStart":false})]}),makeQuery(id+"F1.opExtrude","CAP_EDGE",EDGE,{"disambiguationData":[OSD([subQ0])],"isStart":false})],"blendedInto":[]});}
            var Q1;
            {var subQ0=sQuery(id+"F0.wireOp",EDGE,"E3.1.2");var subQ1=sQuery(id+"F0.wireOp",EDGE,"E3.1.1");Q1=makeQuery(id+"F4.opChamfer","BLEND_EDGE",EDGE,{"blendedFrom":[makeQuery(id+"F3.opChamfer","BLEND_EDGE",EDGE,{"blendedFrom":[makeQuery(id+"F1.opExtrude","SWEPT_EDGE",EDGE,{"disambiguationData":[OSD([subQ1,subQ0])]}),makeQuery(id+"F1.opExtrude","CAP_FACE",FACE,{"disambiguationData":[OSD([sQuery(id+"F0.wireOp",EDGE,"E0"),sQuery(id+"F0.wireOp",EDGE,"E1"),sQuery(id+"F0.wireOp",EDGE,"E2.bottom"),sQuery(id+"F0.wireOp",EDGE,"E2.left"),sQuery(id+"F0.wireOp",EDGE,"E2.right"),subQ1,subQ0,sQuery(id+"F0.wireOp",EDGE,"E3.1.3"),sQuery(id+"F0.wireOp",EDGE,"E3.2.1"),sQuery(id+"F0.wireOp",EDGE,"E3.2.2"),sQuery(id+"F0.wireOp",EDGE,"E3.2.3"),sQuery(id+"F0.wireOp",EDGE,"E3.3.1"),sQuery(id+"F0.wireOp",EDGE,"E3.3.2"),sQuery(id+"F0.wireOp",EDGE,"E3.3.3"),sQuery(id+"F0.wireOp",EDGE,"E3.4.1"),sQuery(id+"F0.wireOp",EDGE,"E3.4.2"),sQuery(id+"F0.wireOp",EDGE,"E3.4.3"),sQuery(id+"F0.wireOp",EDGE,"E3.5.1"),sQuery(id+"F0.wireOp",EDGE,"E3.5.2"),sQuery(id+"F0.wireOp",EDGE,"E3.5.3"),sQuery(id+"F0.wireOp",EDGE,"E3.6.1"),sQuery(id+"F0.wireOp",EDGE,"E3.6.2"),sQuery(id+"F0.wireOp",EDGE,"E3.6.3"),sQuery(id+"F0.wireOp",EDGE,"E3.7.1"),sQuery(id+"F0.wireOp",EDGE,"E3.7.2"),sQuery(id+"F0.wireOp",EDGE,"E3.7.3"),sQuery(id+"F0.wireOp",EDGE,"E3.8.1"),sQuery(id+"F0.wireOp",EDGE,"E3.8.2"),sQuery(id+"F0.wireOp",EDGE,"E3.8.3"),sQuery(id+"F0.wireOp",EDGE,"E3.9.1"),sQuery(id+"F0.wireOp",EDGE,"E3.9.2"),sQuery(id+"F0.wireOp",EDGE,"E3.9.3"),sQuery(id+"F0.wireOp",EDGE,"E3.10.1"),sQuery(id+"F0.wireOp",EDGE,"E3.10.2"),sQuery(id+"F0.wireOp",EDGE,"E3.10.3"),sQuery(id+"F0.wireOp",EDGE,"E3.11.1"),sQuery(id+"F0.wireOp",EDGE,"E3.11.2"),sQuery(id+"F0.wireOp",EDGE,"E3.11.3"),sQuery(id+"F0.wireOp",EDGE,"E3.12.1"),sQuery(id+"F0.wireOp",EDGE,"E3.12.2"),sQuery(id+"F0.wireOp",EDGE,"E3.12.3")])],"isStart":false})],"blendedInto":[makeQuery(id+"F1.opExtrude","CAP_FACE",FACE,{"disambiguationData":[OSD([sQuery(id+"F0.wireOp",EDGE,"E0"),sQuery(id+"F0.wireOp",EDGE,"E1"),sQuery(id+"F0.wireOp",EDGE,"E2.bottom"),sQuery(id+"F0.wireOp",EDGE,"E2.left"),sQuery(id+"F0.wireOp",EDGE,"E2.right"),subQ1,subQ0,sQuery(id+"F0.wireOp",EDGE,"E3.1.3"),sQuery(id+"F0.wireOp",EDGE,"E3.2.1"),sQuery(id+"F0.wireOp",EDGE,"E3.2.2"),sQuery(id+"F0.wireOp",EDGE,"E3.2.3"),sQuery(id+"F0.wireOp",EDGE,"E3.3.1"),sQuery(id+"F0.wireOp",EDGE,"E3.3.2"),sQuery(id+"F0.wireOp",EDGE,"E3.3.3"),sQuery(id+"F0.wireOp",EDGE,"E3.4.1"),sQuery(id+"F0.wireOp",EDGE,"E3.4.2"),sQuery(id+"F0.wireOp",EDGE,"E3.4.3"),sQuery(id+"F0.wireOp",EDGE,"E3.5.1"),sQuery(id+"F0.wireOp",EDGE,"E3.5.2"),sQuery(id+"F0.wireOp",EDGE,"E3.5.3"),sQuery(id+"F0.wireOp",EDGE,"E3.6.1"),sQuery(id+"F0.wireOp",EDGE,"E3.6.2"),sQuery(id+"F0.wireOp",EDGE,"E3.6.3"),sQuery(id+"F0.wireOp",EDGE,"E3.7.1"),sQuery(id+"F0.wireOp",EDGE,"E3.7.2"),sQuery(id+"F0.wireOp",EDGE,"E3.7.3"),sQuery(id+"F0.wireOp",EDGE,"E3.8.1"),sQuery(id+"F0.wireOp",EDGE,"E3.8.2"),sQuery(id+"F0.wireOp",EDGE,"E3.8.3"),sQuery(id+"F0.wireOp",EDGE,"E3.9.1"),sQuery(id+"F0.wireOp",EDGE,"E3.9.2"),sQuery(id+"F0.wireOp",EDGE,"E3.9.3"),sQuery(id+"F0.wireOp",EDGE,"E3.10.1"),sQuery(id+"F0.wireOp",EDGE,"E3.10.2"),sQuery(id+"F0.wireOp",EDGE,"E3.10.3"),sQuery(id+"F0.wireOp",EDGE,"E3.11.1"),sQuery(id+"F0.wireOp",EDGE,"E3.11.2"),sQuery(id+"F0.wireOp",EDGE,"E3.11.3"),sQuery(id+"F0.wireOp",EDGE,"E3.12.1"),sQuery(id+"F0.wireOp",EDGE,"E3.12.2"),sQuery(id+"F0.wireOp",EDGE,"E3.12.3")])],"isStart":false})]}),makeQuery(id+"F1.opExtrude","CAP_EDGE",EDGE,{"disambiguationData":[OSD([subQ0])],"isStart":false})],"blendedInto":[]});}
            var Q2;
            {var subQ0=sQuery(id+"F0.wireOp",EDGE,"E3.2.2");Q2=makeQuery(id+"F3.opChamfer","BLEND_EDGE",EDGE,{"blendedFrom":[makeQuery(id+"F1.opExtrude","SWEPT_EDGE",EDGE,{"disambiguationData":[OSD([subQ0,sQuery(id+"F0.wireOp",EDGE,"E3.2.3")])]}),makeQuery(id+"F1.opExtrude","SWEPT_FACE",FACE,{"disambiguationData":[OSD([subQ0])]})],"blendedInto":[makeQuery(id+"F1.opExtrude","SWEPT_FACE",FACE,{"disambiguationData":[OSD([subQ0])]})]});}
            var Q3;
            {var subQ0=sQuery(id+"F0.wireOp",EDGE,"E3.2.2");Q3=makeQuery(id+"F3.opChamfer","BLEND_EDGE",EDGE,{"blendedFrom":[makeQuery(id+"F1.opExtrude","SWEPT_EDGE",EDGE,{"disambiguationData":[OSD([sQuery(id+"F0.wireOp",EDGE,"E3.2.1"),subQ0])]}),makeQuery(id+"F1.opExtrude","SWEPT_FACE",FACE,{"disambiguationData":[OSD([subQ0])]})],"blendedInto":[makeQuery(id+"F1.opExtrude","SWEPT_FACE",FACE,{"disambiguationData":[OSD([subQ0])]})]});}
            var Q4;
            {var subQ0=sQuery(id+"F0.wireOp",EDGE,"E3.1.2");Q4=makeQuery(id+"F3.opChamfer","BLEND_EDGE",EDGE,{"blendedFrom":[makeQuery(id+"F1.opExtrude","SWEPT_EDGE",EDGE,{"disambiguationData":[OSD([subQ0,sQuery(id+"F0.wireOp",EDGE,"E3.1.3")])]}),makeQuery(id+"F1.opExtrude","SWEPT_FACE",FACE,{"disambiguationData":[OSD([subQ0])]})],"blendedInto":[makeQuery(id+"F1.opExtrude","SWEPT_FACE",FACE,{"disambiguationData":[OSD([subQ0])]})]});}
            var Q5;
            {var subQ0=sQuery(id+"F0.wireOp",EDGE,"E3.1.2");Q5=makeQuery(id+"F3.opChamfer","BLEND_EDGE",EDGE,{"blendedFrom":[makeQuery(id+"F1.opExtrude","SWEPT_EDGE",EDGE,{"disambiguationData":[OSD([sQuery(id+"F0.wireOp",EDGE,"E3.1.1"),subQ0])]}),makeQuery(id+"F1.opExtrude","SWEPT_FACE",FACE,{"disambiguationData":[OSD([subQ0])]})],"blendedInto":[makeQuery(id+"F1.opExtrude","SWEPT_FACE",FACE,{"disambiguationData":[OSD([subQ0])]})]});}
            var Q6;
            {var subQ0=sQuery(id+"F0.wireOp",EDGE,"E3.2.2");var subQ1=sQuery(id+"F0.wireOp",EDGE,"E3.2.3");Q6=makeQuery(id+"F4.opChamfer","BLEND_EDGE",EDGE,{"blendedFrom":[makeQuery(id+"F3.opChamfer","BLEND_EDGE",EDGE,{"blendedFrom":[makeQuery(id+"F1.opExtrude","SWEPT_EDGE",EDGE,{"disambiguationData":[OSD([subQ0,subQ1])]}),makeQuery(id+"F1.opExtrude","CAP_FACE",FACE,{"disambiguationData":[OSD([sQuery(id+"F0.wireOp",EDGE,"E0"),sQuery(id+"F0.wireOp",EDGE,"E1"),sQuery(id+"F0.wireOp",EDGE,"E2.bottom"),sQuery(id+"F0.wireOp",EDGE,"E2.left"),sQuery(id+"F0.wireOp",EDGE,"E2.right"),sQuery(id+"F0.wireOp",EDGE,"E3.1.1"),sQuery(id+"F0.wireOp",EDGE,"E3.1.2"),sQuery(id+"F0.wireOp",EDGE,"E3.1.3"),sQuery(id+"F0.wireOp",EDGE,"E3.2.1"),subQ0,subQ1,sQuery(id+"F0.wireOp",EDGE,"E3.3.1"),sQuery(id+"F0.wireOp",EDGE,"E3.3.2"),sQuery(id+"F0.wireOp",EDGE,"E3.3.3"),sQuery(id+"F0.wireOp",EDGE,"E3.4.1"),sQuery(id+"F0.wireOp",EDGE,"E3.4.2"),sQuery(id+"F0.wireOp",EDGE,"E3.4.3"),sQuery(id+"F0.wireOp",EDGE,"E3.5.1"),sQuery(id+"F0.wireOp",EDGE,"E3.5.2"),sQuery(id+"F0.wireOp",EDGE,"E3.5.3"),sQuery(id+"F0.wireOp",EDGE,"E3.6.1"),sQuery(id+"F0.wireOp",EDGE,"E3.6.2"),sQuery(id+"F0.wireOp",EDGE,"E3.6.3"),sQuery(id+"F0.wireOp",EDGE,"E3.7.1"),sQuery(id+"F0.wireOp",EDGE,"E3.7.2"),sQuery(id+"F0.wireOp",EDGE,"E3.7.3"),sQuery(id+"F0.wireOp",EDGE,"E3.8.1"),sQuery(id+"F0.wireOp",EDGE,"E3.8.2"),sQuery(id+"F0.wireOp",EDGE,"E3.8.3"),sQuery(id+"F0.wireOp",EDGE,"E3.9.1"),sQuery(id+"F0.wireOp",EDGE,"E3.9.2"),sQuery(id+"F0.wireOp",EDGE,"E3.9.3"),sQuery(id+"F0.wireOp",EDGE,"E3.10.1"),sQuery(id+"F0.wireOp",EDGE,"E3.10.2"),sQuery(id+"F0.wireOp",EDGE,"E3.10.3"),sQuery(id+"F0.wireOp",EDGE,"E3.11.1"),sQuery(id+"F0.wireOp",EDGE,"E3.11.2"),sQuery(id+"F0.wireOp",EDGE,"E3.11.3"),sQuery(id+"F0.wireOp",EDGE,"E3.12.1"),sQuery(id+"F0.wireOp",EDGE,"E3.12.2"),sQuery(id+"F0.wireOp",EDGE,"E3.12.3")])],"isStart":false})],"blendedInto":[makeQuery(id+"F1.opExtrude","CAP_FACE",FACE,{"disambiguationData":[OSD([sQuery(id+"F0.wireOp",EDGE,"E0"),sQuery(id+"F0.wireOp",EDGE,"E1"),sQuery(id+"F0.wireOp",EDGE,"E2.bottom"),sQuery(id+"F0.wireOp",EDGE,"E2.left"),sQuery(id+"F0.wireOp",EDGE,"E2.right"),sQuery(id+"F0.wireOp",EDGE,"E3.1.1"),sQuery(id+"F0.wireOp",EDGE,"E3.1.2"),sQuery(id+"F0.wireOp",EDGE,"E3.1.3"),sQuery(id+"F0.wireOp",EDGE,"E3.2.1"),subQ0,subQ1,sQuery(id+"F0.wireOp",EDGE,"E3.3.1"),sQuery(id+"F0.wireOp",EDGE,"E3.3.2"),sQuery(id+"F0.wireOp",EDGE,"E3.3.3"),sQuery(id+"F0.wireOp",EDGE,"E3.4.1"),sQuery(id+"F0.wireOp",EDGE,"E3.4.2"),sQuery(id+"F0.wireOp",EDGE,"E3.4.3"),sQuery(id+"F0.wireOp",EDGE,"E3.5.1"),sQuery(id+"F0.wireOp",EDGE,"E3.5.2"),sQuery(id+"F0.wireOp",EDGE,"E3.5.3"),sQuery(id+"F0.wireOp",EDGE,"E3.6.1"),sQuery(id+"F0.wireOp",EDGE,"E3.6.2"),sQuery(id+"F0.wireOp",EDGE,"E3.6.3"),sQuery(id+"F0.wireOp",EDGE,"E3.7.1"),sQuery(id+"F0.wireOp",EDGE,"E3.7.2"),sQuery(id+"F0.wireOp",EDGE,"E3.7.3"),sQuery(id+"F0.wireOp",EDGE,"E3.8.1"),sQuery(id+"F0.wireOp",EDGE,"E3.8.2"),sQuery(id+"F0.wireOp",EDGE,"E3.8.3"),sQuery(id+"F0.wireOp",EDGE,"E3.9.1"),sQuery(id+"F0.wireOp",EDGE,"E3.9.2"),sQuery(id+"F0.wireOp",EDGE,"E3.9.3"),sQuery(id+"F0.wireOp",EDGE,"E3.10.1"),sQuery(id+"F0.wireOp",EDGE,"E3.10.2"),sQuery(id+"F0.wireOp",EDGE,"E3.10.3"),sQuery(id+"F0.wireOp",EDGE,"E3.11.1"),sQuery(id+"F0.wireOp",EDGE,"E3.11.2"),sQuery(id+"F0.wireOp",EDGE,"E3.11.3"),sQuery(id+"F0.wireOp",EDGE,"E3.12.1"),sQuery(id+"F0.wireOp",EDGE,"E3.12.2"),sQuery(id+"F0.wireOp",EDGE,"E3.12.3")])],"isStart":false})]}),makeQuery(id+"F1.opExtrude","CAP_EDGE",EDGE,{"disambiguationData":[OSD([subQ0])],"isStart":false})],"blendedInto":[]});}
            var Q7;
            {var subQ0=sQuery(id+"F0.wireOp",EDGE,"E3.2.2");var subQ1=sQuery(id+"F0.wireOp",EDGE,"E3.2.1");Q7=makeQuery(id+"F4.opChamfer","BLEND_EDGE",EDGE,{"blendedFrom":[makeQuery(id+"F3.opChamfer","BLEND_EDGE",EDGE,{"blendedFrom":[makeQuery(id+"F1.opExtrude","SWEPT_EDGE",EDGE,{"disambiguationData":[OSD([subQ1,subQ0])]}),makeQuery(id+"F1.opExtrude","CAP_FACE",FACE,{"disambiguationData":[OSD([sQuery(id+"F0.wireOp",EDGE,"E0"),sQuery(id+"F0.wireOp",EDGE,"E1"),sQuery(id+"F0.wireOp",EDGE,"E2.bottom"),sQuery(id+"F0.wireOp",EDGE,"E2.left"),sQuery(id+"F0.wireOp",EDGE,"E2.right"),sQuery(id+"F0.wireOp",EDGE,"E3.1.1"),sQuery(id+"F0.wireOp",EDGE,"E3.1.2"),sQuery(id+"F0.wireOp",EDGE,"E3.1.3"),subQ1,subQ0,sQuery(id+"F0.wireOp",EDGE,"E3.2.3"),sQuery(id+"F0.wireOp",EDGE,"E3.3.1"),sQuery(id+"F0.wireOp",EDGE,"E3.3.2"),sQuery(id+"F0.wireOp",EDGE,"E3.3.3"),sQuery(id+"F0.wireOp",EDGE,"E3.4.1"),sQuery(id+"F0.wireOp",EDGE,"E3.4.2"),sQuery(id+"F0.wireOp",EDGE,"E3.4.3"),sQuery(id+"F0.wireOp",EDGE,"E3.5.1"),sQuery(id+"F0.wireOp",EDGE,"E3.5.2"),sQuery(id+"F0.wireOp",EDGE,"E3.5.3"),sQuery(id+"F0.wireOp",EDGE,"E3.6.1"),sQuery(id+"F0.wireOp",EDGE,"E3.6.2"),sQuery(id+"F0.wireOp",EDGE,"E3.6.3"),sQuery(id+"F0.wireOp",EDGE,"E3.7.1"),sQuery(id+"F0.wireOp",EDGE,"E3.7.2"),sQuery(id+"F0.wireOp",EDGE,"E3.7.3"),sQuery(id+"F0.wireOp",EDGE,"E3.8.1"),sQuery(id+"F0.wireOp",EDGE,"E3.8.2"),sQuery(id+"F0.wireOp",EDGE,"E3.8.3"),sQuery(id+"F0.wireOp",EDGE,"E3.9.1"),sQuery(id+"F0.wireOp",EDGE,"E3.9.2"),sQuery(id+"F0.wireOp",EDGE,"E3.9.3"),sQuery(id+"F0.wireOp",EDGE,"E3.10.1"),sQuery(id+"F0.wireOp",EDGE,"E3.10.2"),sQuery(id+"F0.wireOp",EDGE,"E3.10.3"),sQuery(id+"F0.wireOp",EDGE,"E3.11.1"),sQuery(id+"F0.wireOp",EDGE,"E3.11.2"),sQuery(id+"F0.wireOp",EDGE,"E3.11.3"),sQuery(id+"F0.wireOp",EDGE,"E3.12.1"),sQuery(id+"F0.wireOp",EDGE,"E3.12.2"),sQuery(id+"F0.wireOp",EDGE,"E3.12.3")])],"isStart":false})],"blendedInto":[makeQuery(id+"F1.opExtrude","CAP_FACE",FACE,{"disambiguationData":[OSD([sQuery(id+"F0.wireOp",EDGE,"E0"),sQuery(id+"F0.wireOp",EDGE,"E1"),sQuery(id+"F0.wireOp",EDGE,"E2.bottom"),sQuery(id+"F0.wireOp",EDGE,"E2.left"),sQuery(id+"F0.wireOp",EDGE,"E2.right"),sQuery(id+"F0.wireOp",EDGE,"E3.1.1"),sQuery(id+"F0.wireOp",EDGE,"E3.1.2"),sQuery(id+"F0.wireOp",EDGE,"E3.1.3"),subQ1,subQ0,sQuery(id+"F0.wireOp",EDGE,"E3.2.3"),sQuery(id+"F0.wireOp",EDGE,"E3.3.1"),sQuery(id+"F0.wireOp",EDGE,"E3.3.2"),sQuery(id+"F0.wireOp",EDGE,"E3.3.3"),sQuery(id+"F0.wireOp",EDGE,"E3.4.1"),sQuery(id+"F0.wireOp",EDGE,"E3.4.2"),sQuery(id+"F0.wireOp",EDGE,"E3.4.3"),sQuery(id+"F0.wireOp",EDGE,"E3.5.1"),sQuery(id+"F0.wireOp",EDGE,"E3.5.2"),sQuery(id+"F0.wireOp",EDGE,"E3.5.3"),sQuery(id+"F0.wireOp",EDGE,"E3.6.1"),sQuery(id+"F0.wireOp",EDGE,"E3.6.2"),sQuery(id+"F0.wireOp",EDGE,"E3.6.3"),sQuery(id+"F0.wireOp",EDGE,"E3.7.1"),sQuery(id+"F0.wireOp",EDGE,"E3.7.2"),sQuery(id+"F0.wireOp",EDGE,"E3.7.3"),sQuery(id+"F0.wireOp",EDGE,"E3.8.1"),sQuery(id+"F0.wireOp",EDGE,"E3.8.2"),sQuery(id+"F0.wireOp",EDGE,"E3.8.3"),sQuery(id+"F0.wireOp",EDGE,"E3.9.1"),sQuery(id+"F0.wireOp",EDGE,"E3.9.2"),sQuery(id+"F0.wireOp",EDGE,"E3.9.3"),sQuery(id+"F0.wireOp",EDGE,"E3.10.1"),sQuery(id+"F0.wireOp",EDGE,"E3.10.2"),sQuery(id+"F0.wireOp",EDGE,"E3.10.3"),sQuery(id+"F0.wireOp",EDGE,"E3.11.1"),sQuery(id+"F0.wireOp",EDGE,"E3.11.2"),sQuery(id+"F0.wireOp",EDGE,"E3.11.3"),sQuery(id+"F0.wireOp",EDGE,"E3.12.1"),sQuery(id+"F0.wireOp",EDGE,"E3.12.2"),sQuery(id+"F0.wireOp",EDGE,"E3.12.3")])],"isStart":false})]}),makeQuery(id+"F1.opExtrude","CAP_EDGE",EDGE,{"disambiguationData":[OSD([subQ0])],"isStart":false})],"blendedInto":[]});}
            var Q8;
            {var subQ0=sQuery(id+"F0.wireOp",EDGE,"E2.bottom");Q8=makeQuery(id+"F3.opChamfer","BLEND_EDGE",EDGE,{"blendedFrom":[makeQuery(id+"F1.opExtrude","SWEPT_EDGE",EDGE,{"disambiguationData":[OSD([subQ0,sQuery(id+"F0.wireOp",EDGE,"E2.right")])]}),makeQuery(id+"F1.opExtrude","SWEPT_FACE",FACE,{"disambiguationData":[OSD([subQ0])]})],"blendedInto":[makeQuery(id+"F1.opExtrude","SWEPT_FACE",FACE,{"disambiguationData":[OSD([subQ0])]})]});}
            var Q9;
            {var subQ0=sQuery(id+"F0.wireOp",EDGE,"E2.bottom");Q9=makeQuery(id+"F3.opChamfer","BLEND_EDGE",EDGE,{"blendedFrom":[makeQuery(id+"F1.opExtrude","SWEPT_EDGE",EDGE,{"disambiguationData":[OSD([subQ0,sQuery(id+"F0.wireOp",EDGE,"E2.left")])]}),makeQuery(id+"F1.opExtrude","SWEPT_FACE",FACE,{"disambiguationData":[OSD([subQ0])]})],"blendedInto":[makeQuery(id+"F1.opExtrude","SWEPT_FACE",FACE,{"disambiguationData":[OSD([subQ0])]})]});}
            var Q10;
            {var subQ0=sQuery(id+"F0.wireOp",EDGE,"E2.bottom");var subQ1=sQuery(id+"F0.wireOp",EDGE,"E2.right");Q10=makeQuery(id+"F4.opChamfer","BLEND_EDGE",EDGE,{"blendedFrom":[makeQuery(id+"F3.opChamfer","BLEND_EDGE",EDGE,{"blendedFrom":[makeQuery(id+"F1.opExtrude","SWEPT_EDGE",EDGE,{"disambiguationData":[OSD([subQ0,subQ1])]}),makeQuery(id+"F1.opExtrude","CAP_FACE",FACE,{"disambiguationData":[OSD([sQuery(id+"F0.wireOp",EDGE,"E0"),sQuery(id+"F0.wireOp",EDGE,"E1"),subQ0,sQuery(id+"F0.wireOp",EDGE,"E2.left"),subQ1,sQuery(id+"F0.wireOp",EDGE,"E3.1.1"),sQuery(id+"F0.wireOp",EDGE,"E3.1.2"),sQuery(id+"F0.wireOp",EDGE,"E3.1.3"),sQuery(id+"F0.wireOp",EDGE,"E3.2.1"),sQuery(id+"F0.wireOp",EDGE,"E3.2.2"),sQuery(id+"F0.wireOp",EDGE,"E3.2.3"),sQuery(id+"F0.wireOp",EDGE,"E3.3.1"),sQuery(id+"F0.wireOp",EDGE,"E3.3.2"),sQuery(id+"F0.wireOp",EDGE,"E3.3.3"),sQuery(id+"F0.wireOp",EDGE,"E3.4.1"),sQuery(id+"F0.wireOp",EDGE,"E3.4.2"),sQuery(id+"F0.wireOp",EDGE,"E3.4.3"),sQuery(id+"F0.wireOp",EDGE,"E3.5.1"),sQuery(id+"F0.wireOp",EDGE,"E3.5.2"),sQuery(id+"F0.wireOp",EDGE,"E3.5.3"),sQuery(id+"F0.wireOp",EDGE,"E3.6.1"),sQuery(id+"F0.wireOp",EDGE,"E3.6.2"),sQuery(id+"F0.wireOp",EDGE,"E3.6.3"),sQuery(id+"F0.wireOp",EDGE,"E3.7.1"),sQuery(id+"F0.wireOp",EDGE,"E3.7.2"),sQuery(id+"F0.wireOp",EDGE,"E3.7.3"),sQuery(id+"F0.wireOp",EDGE,"E3.8.1"),sQuery(id+"F0.wireOp",EDGE,"E3.8.2"),sQuery(id+"F0.wireOp",EDGE,"E3.8.3"),sQuery(id+"F0.wireOp",EDGE,"E3.9.1"),sQuery(id+"F0.wireOp",EDGE,"E3.9.2"),sQuery(id+"F0.wireOp",EDGE,"E3.9.3"),sQuery(id+"F0.wireOp",EDGE,"E3.10.1"),sQuery(id+"F0.wireOp",EDGE,"E3.10.2"),sQuery(id+"F0.wireOp",EDGE,"E3.10.3"),sQuery(id+"F0.wireOp",EDGE,"E3.11.1"),sQuery(id+"F0.wireOp",EDGE,"E3.11.2"),sQuery(id+"F0.wireOp",EDGE,"E3.11.3"),sQuery(id+"F0.wireOp",EDGE,"E3.12.1"),sQuery(id+"F0.wireOp",EDGE,"E3.12.2"),sQuery(id+"F0.wireOp",EDGE,"E3.12.3")])],"isStart":false})],"blendedInto":[makeQuery(id+"F1.opExtrude","CAP_FACE",FACE,{"disambiguationData":[OSD([sQuery(id+"F0.wireOp",EDGE,"E0"),sQuery(id+"F0.wireOp",EDGE,"E1"),subQ0,sQuery(id+"F0.wireOp",EDGE,"E2.left"),subQ1,sQuery(id+"F0.wireOp",EDGE,"E3.1.1"),sQuery(id+"F0.wireOp",EDGE,"E3.1.2"),sQuery(id+"F0.wireOp",EDGE,"E3.1.3"),sQuery(id+"F0.wireOp",EDGE,"E3.2.1"),sQuery(id+"F0.wireOp",EDGE,"E3.2.2"),sQuery(id+"F0.wireOp",EDGE,"E3.2.3"),sQuery(id+"F0.wireOp",EDGE,"E3.3.1"),sQuery(id+"F0.wireOp",EDGE,"E3.3.2"),sQuery(id+"F0.wireOp",EDGE,"E3.3.3"),sQuery(id+"F0.wireOp",EDGE,"E3.4.1"),sQuery(id+"F0.wireOp",EDGE,"E3.4.2"),sQuery(id+"F0.wireOp",EDGE,"E3.4.3"),sQuery(id+"F0.wireOp",EDGE,"E3.5.1"),sQuery(id+"F0.wireOp",EDGE,"E3.5.2"),sQuery(id+"F0.wireOp",EDGE,"E3.5.3"),sQuery(id+"F0.wireOp",EDGE,"E3.6.1"),sQuery(id+"F0.wireOp",EDGE,"E3.6.2"),sQuery(id+"F0.wireOp",EDGE,"E3.6.3"),sQuery(id+"F0.wireOp",EDGE,"E3.7.1"),sQuery(id+"F0.wireOp",EDGE,"E3.7.2"),sQuery(id+"F0.wireOp",EDGE,"E3.7.3"),sQuery(id+"F0.wireOp",EDGE,"E3.8.1"),sQuery(id+"F0.wireOp",EDGE,"E3.8.2"),sQuery(id+"F0.wireOp",EDGE,"E3.8.3"),sQuery(id+"F0.wireOp",EDGE,"E3.9.1"),sQuery(id+"F0.wireOp",EDGE,"E3.9.2"),sQuery(id+"F0.wireOp",EDGE,"E3.9.3"),sQuery(id+"F0.wireOp",EDGE,"E3.10.1"),sQuery(id+"F0.wireOp",EDGE,"E3.10.2"),sQuery(id+"F0.wireOp",EDGE,"E3.10.3"),sQuery(id+"F0.wireOp",EDGE,"E3.11.1"),sQuery(id+"F0.wireOp",EDGE,"E3.11.2"),sQuery(id+"F0.wireOp",EDGE,"E3.11.3"),sQuery(id+"F0.wireOp",EDGE,"E3.12.1"),sQuery(id+"F0.wireOp",EDGE,"E3.12.2"),sQuery(id+"F0.wireOp",EDGE,"E3.12.3")])],"isStart":false})]}),makeQuery(id+"F1.opExtrude","CAP_EDGE",EDGE,{"disambiguationData":[OSD([subQ0])],"isStart":false})],"blendedInto":[]});}
            var Q11;
            {var subQ0=sQuery(id+"F0.wireOp",EDGE,"E2.bottom");var subQ1=sQuery(id+"F0.wireOp",EDGE,"E2.left");Q11=makeQuery(id+"F4.opChamfer","BLEND_EDGE",EDGE,{"blendedFrom":[makeQuery(id+"F3.opChamfer","BLEND_EDGE",EDGE,{"blendedFrom":[makeQuery(id+"F1.opExtrude","SWEPT_EDGE",EDGE,{"disambiguationData":[OSD([subQ0,subQ1])]}),makeQuery(id+"F1.opExtrude","CAP_FACE",FACE,{"disambiguationData":[OSD([sQuery(id+"F0.wireOp",EDGE,"E0"),sQuery(id+"F0.wireOp",EDGE,"E1"),subQ0,subQ1,sQuery(id+"F0.wireOp",EDGE,"E2.right"),sQuery(id+"F0.wireOp",EDGE,"E3.1.1"),sQuery(id+"F0.wireOp",EDGE,"E3.1.2"),sQuery(id+"F0.wireOp",EDGE,"E3.1.3"),sQuery(id+"F0.wireOp",EDGE,"E3.2.1"),sQuery(id+"F0.wireOp",EDGE,"E3.2.2"),sQuery(id+"F0.wireOp",EDGE,"E3.2.3"),sQuery(id+"F0.wireOp",EDGE,"E3.3.1"),sQuery(id+"F0.wireOp",EDGE,"E3.3.2"),sQuery(id+"F0.wireOp",EDGE,"E3.3.3"),sQuery(id+"F0.wireOp",EDGE,"E3.4.1"),sQuery(id+"F0.wireOp",EDGE,"E3.4.2"),sQuery(id+"F0.wireOp",EDGE,"E3.4.3"),sQuery(id+"F0.wireOp",EDGE,"E3.5.1"),sQuery(id+"F0.wireOp",EDGE,"E3.5.2"),sQuery(id+"F0.wireOp",EDGE,"E3.5.3"),sQuery(id+"F0.wireOp",EDGE,"E3.6.1"),sQuery(id+"F0.wireOp",EDGE,"E3.6.2"),sQuery(id+"F0.wireOp",EDGE,"E3.6.3"),sQuery(id+"F0.wireOp",EDGE,"E3.7.1"),sQuery(id+"F0.wireOp",EDGE,"E3.7.2"),sQuery(id+"F0.wireOp",EDGE,"E3.7.3"),sQuery(id+"F0.wireOp",EDGE,"E3.8.1"),sQuery(id+"F0.wireOp",EDGE,"E3.8.2"),sQuery(id+"F0.wireOp",EDGE,"E3.8.3"),sQuery(id+"F0.wireOp",EDGE,"E3.9.1"),sQuery(id+"F0.wireOp",EDGE,"E3.9.2"),sQuery(id+"F0.wireOp",EDGE,"E3.9.3"),sQuery(id+"F0.wireOp",EDGE,"E3.10.1"),sQuery(id+"F0.wireOp",EDGE,"E3.10.2"),sQuery(id+"F0.wireOp",EDGE,"E3.10.3"),sQuery(id+"F0.wireOp",EDGE,"E3.11.1"),sQuery(id+"F0.wireOp",EDGE,"E3.11.2"),sQuery(id+"F0.wireOp",EDGE,"E3.11.3"),sQuery(id+"F0.wireOp",EDGE,"E3.12.1"),sQuery(id+"F0.wireOp",EDGE,"E3.12.2"),sQuery(id+"F0.wireOp",EDGE,"E3.12.3")])],"isStart":false})],"blendedInto":[makeQuery(id+"F1.opExtrude","CAP_FACE",FACE,{"disambiguationData":[OSD([sQuery(id+"F0.wireOp",EDGE,"E0"),sQuery(id+"F0.wireOp",EDGE,"E1"),subQ0,subQ1,sQuery(id+"F0.wireOp",EDGE,"E2.right"),sQuery(id+"F0.wireOp",EDGE,"E3.1.1"),sQuery(id+"F0.wireOp",EDGE,"E3.1.2"),sQuery(id+"F0.wireOp",EDGE,"E3.1.3"),sQuery(id+"F0.wireOp",EDGE,"E3.2.1"),sQuery(id+"F0.wireOp",EDGE,"E3.2.2"),sQuery(id+"F0.wireOp",EDGE,"E3.2.3"),sQuery(id+"F0.wireOp",EDGE,"E3.3.1"),sQuery(id+"F0.wireOp",EDGE,"E3.3.2"),sQuery(id+"F0.wireOp",EDGE,"E3.3.3"),sQuery(id+"F0.wireOp",EDGE,"E3.4.1"),sQuery(id+"F0.wireOp",EDGE,"E3.4.2"),sQuery(id+"F0.wireOp",EDGE,"E3.4.3"),sQuery(id+"F0.wireOp",EDGE,"E3.5.1"),sQuery(id+"F0.wireOp",EDGE,"E3.5.2"),sQuery(id+"F0.wireOp",EDGE,"E3.5.3"),sQuery(id+"F0.wireOp",EDGE,"E3.6.1"),sQuery(id+"F0.wireOp",EDGE,"E3.6.2"),sQuery(id+"F0.wireOp",EDGE,"E3.6.3"),sQuery(id+"F0.wireOp",EDGE,"E3.7.1"),sQuery(id+"F0.wireOp",EDGE,"E3.7.2"),sQuery(id+"F0.wireOp",EDGE,"E3.7.3"),sQuery(id+"F0.wireOp",EDGE,"E3.8.1"),sQuery(id+"F0.wireOp",EDGE,"E3.8.2"),sQuery(id+"F0.wireOp",EDGE,"E3.8.3"),sQuery(id+"F0.wireOp",EDGE,"E3.9.1"),sQuery(id+"F0.wireOp",EDGE,"E3.9.2"),sQuery(id+"F0.wireOp",EDGE,"E3.9.3"),sQuery(id+"F0.wireOp",EDGE,"E3.10.1"),sQuery(id+"F0.wireOp",EDGE,"E3.10.2"),sQuery(id+"F0.wireOp",EDGE,"E3.10.3"),sQuery(id+"F0.wireOp",EDGE,"E3.11.1"),sQuery(id+"F0.wireOp",EDGE,"E3.11.2"),sQuery(id+"F0.wireOp",EDGE,"E3.11.3"),sQuery(id+"F0.wireOp",EDGE,"E3.12.1"),sQuery(id+"F0.wireOp",EDGE,"E3.12.2"),sQuery(id+"F0.wireOp",EDGE,"E3.12.3")])],"isStart":false})]}),makeQuery(id+"F1.opExtrude","CAP_EDGE",EDGE,{"disambiguationData":[OSD([subQ0])],"isStart":false})],"blendedInto":[]});}
            var Q12;
            {var subQ0=sQuery(id+"F0.wireOp",EDGE,"E3.12.2");Q12=makeQuery(id+"F3.opChamfer","BLEND_EDGE",EDGE,{"blendedFrom":[makeQuery(id+"F1.opExtrude","SWEPT_EDGE",EDGE,{"disambiguationData":[OSD([subQ0,sQuery(id+"F0.wireOp",EDGE,"E3.12.3")])]}),makeQuery(id+"F1.opExtrude","SWEPT_FACE",FACE,{"disambiguationData":[OSD([subQ0])]})],"blendedInto":[makeQuery(id+"F1.opExtrude","SWEPT_FACE",FACE,{"disambiguationData":[OSD([subQ0])]})]});}
            var Q13;
            {var subQ0=sQuery(id+"F0.wireOp",EDGE,"E3.12.2");Q13=makeQuery(id+"F3.opChamfer","BLEND_EDGE",EDGE,{"blendedFrom":[makeQuery(id+"F1.opExtrude","SWEPT_EDGE",EDGE,{"disambiguationData":[OSD([sQuery(id+"F0.wireOp",EDGE,"E3.12.1"),subQ0])]}),makeQuery(id+"F1.opExtrude","SWEPT_FACE",FACE,{"disambiguationData":[OSD([subQ0])]})],"blendedInto":[makeQuery(id+"F1.opExtrude","SWEPT_FACE",FACE,{"disambiguationData":[OSD([subQ0])]})]});}
            var Q14;
            {var subQ0=sQuery(id+"F0.wireOp",EDGE,"E3.12.2");var subQ1=sQuery(id+"F0.wireOp",EDGE,"E3.12.3");Q14=makeQuery(id+"F4.opChamfer","BLEND_EDGE",EDGE,{"blendedFrom":[makeQuery(id+"F3.opChamfer","BLEND_EDGE",EDGE,{"blendedFrom":[makeQuery(id+"F1.opExtrude","SWEPT_EDGE",EDGE,{"disambiguationData":[OSD([subQ0,subQ1])]}),makeQuery(id+"F1.opExtrude","CAP_FACE",FACE,{"disambiguationData":[OSD([sQuery(id+"F0.wireOp",EDGE,"E0"),sQuery(id+"F0.wireOp",EDGE,"E1"),sQuery(id+"F0.wireOp",EDGE,"E2.bottom"),sQuery(id+"F0.wireOp",EDGE,"E2.left"),sQuery(id+"F0.wireOp",EDGE,"E2.right"),sQuery(id+"F0.wireOp",EDGE,"E3.1.1"),sQuery(id+"F0.wireOp",EDGE,"E3.1.2"),sQuery(id+"F0.wireOp",EDGE,"E3.1.3"),sQuery(id+"F0.wireOp",EDGE,"E3.2.1"),sQuery(id+"F0.wireOp",EDGE,"E3.2.2"),sQuery(id+"F0.wireOp",EDGE,"E3.2.3"),sQuery(id+"F0.wireOp",EDGE,"E3.3.1"),sQuery(id+"F0.wireOp",EDGE,"E3.3.2"),sQuery(id+"F0.wireOp",EDGE,"E3.3.3"),sQuery(id+"F0.wireOp",EDGE,"E3.4.1"),sQuery(id+"F0.wireOp",EDGE,"E3.4.2"),sQuery(id+"F0.wireOp",EDGE,"E3.4.3"),sQuery(id+"F0.wireOp",EDGE,"E3.5.1"),sQuery(id+"F0.wireOp",EDGE,"E3.5.2"),sQuery(id+"F0.wireOp",EDGE,"E3.5.3"),sQuery(id+"F0.wireOp",EDGE,"E3.6.1"),sQuery(id+"F0.wireOp",EDGE,"E3.6.2"),sQuery(id+"F0.wireOp",EDGE,"E3.6.3"),sQuery(id+"F0.wireOp",EDGE,"E3.7.1"),sQuery(id+"F0.wireOp",EDGE,"E3.7.2"),sQuery(id+"F0.wireOp",EDGE,"E3.7.3"),sQuery(id+"F0.wireOp",EDGE,"E3.8.1"),sQuery(id+"F0.wireOp",EDGE,"E3.8.2"),sQuery(id+"F0.wireOp",EDGE,"E3.8.3"),sQuery(id+"F0.wireOp",EDGE,"E3.9.1"),sQuery(id+"F0.wireOp",EDGE,"E3.9.2"),sQuery(id+"F0.wireOp",EDGE,"E3.9.3"),sQuery(id+"F0.wireOp",EDGE,"E3.10.1"),sQuery(id+"F0.wireOp",EDGE,"E3.10.2"),sQuery(id+"F0.wireOp",EDGE,"E3.10.3"),sQuery(id+"F0.wireOp",EDGE,"E3.11.1"),sQuery(id+"F0.wireOp",EDGE,"E3.11.2"),sQuery(id+"F0.wireOp",EDGE,"E3.11.3"),sQuery(id+"F0.wireOp",EDGE,"E3.12.1"),subQ0,subQ1])],"isStart":false})],"blendedInto":[makeQuery(id+"F1.opExtrude","CAP_FACE",FACE,{"disambiguationData":[OSD([sQuery(id+"F0.wireOp",EDGE,"E0"),sQuery(id+"F0.wireOp",EDGE,"E1"),sQuery(id+"F0.wireOp",EDGE,"E2.bottom"),sQuery(id+"F0.wireOp",EDGE,"E2.left"),sQuery(id+"F0.wireOp",EDGE,"E2.right"),sQuery(id+"F0.wireOp",EDGE,"E3.1.1"),sQuery(id+"F0.wireOp",EDGE,"E3.1.2"),sQuery(id+"F0.wireOp",EDGE,"E3.1.3"),sQuery(id+"F0.wireOp",EDGE,"E3.2.1"),sQuery(id+"F0.wireOp",EDGE,"E3.2.2"),sQuery(id+"F0.wireOp",EDGE,"E3.2.3"),sQuery(id+"F0.wireOp",EDGE,"E3.3.1"),sQuery(id+"F0.wireOp",EDGE,"E3.3.2"),sQuery(id+"F0.wireOp",EDGE,"E3.3.3"),sQuery(id+"F0.wireOp",EDGE,"E3.4.1"),sQuery(id+"F0.wireOp",EDGE,"E3.4.2"),sQuery(id+"F0.wireOp",EDGE,"E3.4.3"),sQuery(id+"F0.wireOp",EDGE,"E3.5.1"),sQuery(id+"F0.wireOp",EDGE,"E3.5.2"),sQuery(id+"F0.wireOp",EDGE,"E3.5.3"),sQuery(id+"F0.wireOp",EDGE,"E3.6.1"),sQuery(id+"F0.wireOp",EDGE,"E3.6.2"),sQuery(id+"F0.wireOp",EDGE,"E3.6.3"),sQuery(id+"F0.wireOp",EDGE,"E3.7.1"),sQuery(id+"F0.wireOp",EDGE,"E3.7.2"),sQuery(id+"F0.wireOp",EDGE,"E3.7.3"),sQuery(id+"F0.wireOp",EDGE,"E3.8.1"),sQuery(id+"F0.wireOp",EDGE,"E3.8.2"),sQuery(id+"F0.wireOp",EDGE,"E3.8.3"),sQuery(id+"F0.wireOp",EDGE,"E3.9.1"),sQuery(id+"F0.wireOp",EDGE,"E3.9.2"),sQuery(id+"F0.wireOp",EDGE,"E3.9.3"),sQuery(id+"F0.wireOp",EDGE,"E3.10.1"),sQuery(id+"F0.wireOp",EDGE,"E3.10.2"),sQuery(id+"F0.wireOp",EDGE,"E3.10.3"),sQuery(id+"F0.wireOp",EDGE,"E3.11.1"),sQuery(id+"F0.wireOp",EDGE,"E3.11.2"),sQuery(id+"F0.wireOp",EDGE,"E3.11.3"),sQuery(id+"F0.wireOp",EDGE,"E3.12.1"),subQ0,subQ1])],"isStart":false})]}),makeQuery(id+"F1.opExtrude","CAP_EDGE",EDGE,{"disambiguationData":[OSD([subQ0])],"isStart":false})],"blendedInto":[]});}
            var Q15;
            {var subQ0=sQuery(id+"F0.wireOp",EDGE,"E3.12.2");var subQ1=sQuery(id+"F0.wireOp",EDGE,"E3.12.1");Q15=makeQuery(id+"F4.opChamfer","BLEND_EDGE",EDGE,{"blendedFrom":[makeQuery(id+"F3.opChamfer","BLEND_EDGE",EDGE,{"blendedFrom":[makeQuery(id+"F1.opExtrude","SWEPT_EDGE",EDGE,{"disambiguationData":[OSD([subQ1,subQ0])]}),makeQuery(id+"F1.opExtrude","CAP_FACE",FACE,{"disambiguationData":[OSD([sQuery(id+"F0.wireOp",EDGE,"E0"),sQuery(id+"F0.wireOp",EDGE,"E1"),sQuery(id+"F0.wireOp",EDGE,"E2.bottom"),sQuery(id+"F0.wireOp",EDGE,"E2.left"),sQuery(id+"F0.wireOp",EDGE,"E2.right"),sQuery(id+"F0.wireOp",EDGE,"E3.1.1"),sQuery(id+"F0.wireOp",EDGE,"E3.1.2"),sQuery(id+"F0.wireOp",EDGE,"E3.1.3"),sQuery(id+"F0.wireOp",EDGE,"E3.2.1"),sQuery(id+"F0.wireOp",EDGE,"E3.2.2"),sQuery(id+"F0.wireOp",EDGE,"E3.2.3"),sQuery(id+"F0.wireOp",EDGE,"E3.3.1"),sQuery(id+"F0.wireOp",EDGE,"E3.3.2"),sQuery(id+"F0.wireOp",EDGE,"E3.3.3"),sQuery(id+"F0.wireOp",EDGE,"E3.4.1"),sQuery(id+"F0.wireOp",EDGE,"E3.4.2"),sQuery(id+"F0.wireOp",EDGE,"E3.4.3"),sQuery(id+"F0.wireOp",EDGE,"E3.5.1"),sQuery(id+"F0.wireOp",EDGE,"E3.5.2"),sQuery(id+"F0.wireOp",EDGE,"E3.5.3"),sQuery(id+"F0.wireOp",EDGE,"E3.6.1"),sQuery(id+"F0.wireOp",EDGE,"E3.6.2"),sQuery(id+"F0.wireOp",EDGE,"E3.6.3"),sQuery(id+"F0.wireOp",EDGE,"E3.7.1"),sQuery(id+"F0.wireOp",EDGE,"E3.7.2"),sQuery(id+"F0.wireOp",EDGE,"E3.7.3"),sQuery(id+"F0.wireOp",EDGE,"E3.8.1"),sQuery(id+"F0.wireOp",EDGE,"E3.8.2"),sQuery(id+"F0.wireOp",EDGE,"E3.8.3"),sQuery(id+"F0.wireOp",EDGE,"E3.9.1"),sQuery(id+"F0.wireOp",EDGE,"E3.9.2"),sQuery(id+"F0.wireOp",EDGE,"E3.9.3"),sQuery(id+"F0.wireOp",EDGE,"E3.10.1"),sQuery(id+"F0.wireOp",EDGE,"E3.10.2"),sQuery(id+"F0.wireOp",EDGE,"E3.10.3"),sQuery(id+"F0.wireOp",EDGE,"E3.11.1"),sQuery(id+"F0.wireOp",EDGE,"E3.11.2"),sQuery(id+"F0.wireOp",EDGE,"E3.11.3"),subQ1,subQ0,sQuery(id+"F0.wireOp",EDGE,"E3.12.3")])],"isStart":false})],"blendedInto":[makeQuery(id+"F1.opExtrude","CAP_FACE",FACE,{"disambiguationData":[OSD([sQuery(id+"F0.wireOp",EDGE,"E0"),sQuery(id+"F0.wireOp",EDGE,"E1"),sQuery(id+"F0.wireOp",EDGE,"E2.bottom"),sQuery(id+"F0.wireOp",EDGE,"E2.left"),sQuery(id+"F0.wireOp",EDGE,"E2.right"),sQuery(id+"F0.wireOp",EDGE,"E3.1.1"),sQuery(id+"F0.wireOp",EDGE,"E3.1.2"),sQuery(id+"F0.wireOp",EDGE,"E3.1.3"),sQuery(id+"F0.wireOp",EDGE,"E3.2.1"),sQuery(id+"F0.wireOp",EDGE,"E3.2.2"),sQuery(id+"F0.wireOp",EDGE,"E3.2.3"),sQuery(id+"F0.wireOp",EDGE,"E3.3.1"),sQuery(id+"F0.wireOp",EDGE,"E3.3.2"),sQuery(id+"F0.wireOp",EDGE,"E3.3.3"),sQuery(id+"F0.wireOp",EDGE,"E3.4.1"),sQuery(id+"F0.wireOp",EDGE,"E3.4.2"),sQuery(id+"F0.wireOp",EDGE,"E3.4.3"),sQuery(id+"F0.wireOp",EDGE,"E3.5.1"),sQuery(id+"F0.wireOp",EDGE,"E3.5.2"),sQuery(id+"F0.wireOp",EDGE,"E3.5.3"),sQuery(id+"F0.wireOp",EDGE,"E3.6.1"),sQuery(id+"F0.wireOp",EDGE,"E3.6.2"),sQuery(id+"F0.wireOp",EDGE,"E3.6.3"),sQuery(id+"F0.wireOp",EDGE,"E3.7.1"),sQuery(id+"F0.wireOp",EDGE,"E3.7.2"),sQuery(id+"F0.wireOp",EDGE,"E3.7.3"),sQuery(id+"F0.wireOp",EDGE,"E3.8.1"),sQuery(id+"F0.wireOp",EDGE,"E3.8.2"),sQuery(id+"F0.wireOp",EDGE,"E3.8.3"),sQuery(id+"F0.wireOp",EDGE,"E3.9.1"),sQuery(id+"F0.wireOp",EDGE,"E3.9.2"),sQuery(id+"F0.wireOp",EDGE,"E3.9.3"),sQuery(id+"F0.wireOp",EDGE,"E3.10.1"),sQuery(id+"F0.wireOp",EDGE,"E3.10.2"),sQuery(id+"F0.wireOp",EDGE,"E3.10.3"),sQuery(id+"F0.wireOp",EDGE,"E3.11.1"),sQuery(id+"F0.wireOp",EDGE,"E3.11.2"),sQuery(id+"F0.wireOp",EDGE,"E3.11.3"),subQ1,subQ0,sQuery(id+"F0.wireOp",EDGE,"E3.12.3")])],"isStart":false})]}),makeQuery(id+"F1.opExtrude","CAP_EDGE",EDGE,{"disambiguationData":[OSD([subQ0])],"isStart":false})],"blendedInto":[]});}
            var Q16;
            {var subQ0=sQuery(id+"F0.wireOp",EDGE,"E3.11.2");Q16=makeQuery(id+"F3.opChamfer","BLEND_EDGE",EDGE,{"blendedFrom":[makeQuery(id+"F1.opExtrude","SWEPT_EDGE",EDGE,{"disambiguationData":[OSD([sQuery(id+"F0.wireOp",EDGE,"E3.11.1"),subQ0])]}),makeQuery(id+"F1.opExtrude","SWEPT_FACE",FACE,{"disambiguationData":[OSD([subQ0])]})],"blendedInto":[makeQuery(id+"F1.opExtrude","SWEPT_FACE",FACE,{"disambiguationData":[OSD([subQ0])]})]});}
            var Q17;
            {var subQ0=sQuery(id+"F0.wireOp",EDGE,"E3.11.2");Q17=makeQuery(id+"F3.opChamfer","BLEND_EDGE",EDGE,{"blendedFrom":[makeQuery(id+"F1.opExtrude","SWEPT_EDGE",EDGE,{"disambiguationData":[OSD([subQ0,sQuery(id+"F0.wireOp",EDGE,"E3.11.3")])]}),makeQuery(id+"F1.opExtrude","SWEPT_FACE",FACE,{"disambiguationData":[OSD([subQ0])]})],"blendedInto":[makeQuery(id+"F1.opExtrude","SWEPT_FACE",FACE,{"disambiguationData":[OSD([subQ0])]})]});}
            var Q18;
            {var subQ0=sQuery(id+"F0.wireOp",EDGE,"E3.11.2");var subQ1=sQuery(id+"F0.wireOp",EDGE,"E3.11.1");Q18=makeQuery(id+"F4.opChamfer","BLEND_EDGE",EDGE,{"blendedFrom":[makeQuery(id+"F3.opChamfer","BLEND_EDGE",EDGE,{"blendedFrom":[makeQuery(id+"F1.opExtrude","SWEPT_EDGE",EDGE,{"disambiguationData":[OSD([subQ1,subQ0])]}),makeQuery(id+"F1.opExtrude","CAP_FACE",FACE,{"disambiguationData":[OSD([sQuery(id+"F0.wireOp",EDGE,"E0"),sQuery(id+"F0.wireOp",EDGE,"E1"),sQuery(id+"F0.wireOp",EDGE,"E2.bottom"),sQuery(id+"F0.wireOp",EDGE,"E2.left"),sQuery(id+"F0.wireOp",EDGE,"E2.right"),sQuery(id+"F0.wireOp",EDGE,"E3.1.1"),sQuery(id+"F0.wireOp",EDGE,"E3.1.2"),sQuery(id+"F0.wireOp",EDGE,"E3.1.3"),sQuery(id+"F0.wireOp",EDGE,"E3.2.1"),sQuery(id+"F0.wireOp",EDGE,"E3.2.2"),sQuery(id+"F0.wireOp",EDGE,"E3.2.3"),sQuery(id+"F0.wireOp",EDGE,"E3.3.1"),sQuery(id+"F0.wireOp",EDGE,"E3.3.2"),sQuery(id+"F0.wireOp",EDGE,"E3.3.3"),sQuery(id+"F0.wireOp",EDGE,"E3.4.1"),sQuery(id+"F0.wireOp",EDGE,"E3.4.2"),sQuery(id+"F0.wireOp",EDGE,"E3.4.3"),sQuery(id+"F0.wireOp",EDGE,"E3.5.1"),sQuery(id+"F0.wireOp",EDGE,"E3.5.2"),sQuery(id+"F0.wireOp",EDGE,"E3.5.3"),sQuery(id+"F0.wireOp",EDGE,"E3.6.1"),sQuery(id+"F0.wireOp",EDGE,"E3.6.2"),sQuery(id+"F0.wireOp",EDGE,"E3.6.3"),sQuery(id+"F0.wireOp",EDGE,"E3.7.1"),sQuery(id+"F0.wireOp",EDGE,"E3.7.2"),sQuery(id+"F0.wireOp",EDGE,"E3.7.3"),sQuery(id+"F0.wireOp",EDGE,"E3.8.1"),sQuery(id+"F0.wireOp",EDGE,"E3.8.2"),sQuery(id+"F0.wireOp",EDGE,"E3.8.3"),sQuery(id+"F0.wireOp",EDGE,"E3.9.1"),sQuery(id+"F0.wireOp",EDGE,"E3.9.2"),sQuery(id+"F0.wireOp",EDGE,"E3.9.3"),sQuery(id+"F0.wireOp",EDGE,"E3.10.1"),sQuery(id+"F0.wireOp",EDGE,"E3.10.2"),sQuery(id+"F0.wireOp",EDGE,"E3.10.3"),subQ1,subQ0,sQuery(id+"F0.wireOp",EDGE,"E3.11.3"),sQuery(id+"F0.wireOp",EDGE,"E3.12.1"),sQuery(id+"F0.wireOp",EDGE,"E3.12.2"),sQuery(id+"F0.wireOp",EDGE,"E3.12.3")])],"isStart":false})],"blendedInto":[makeQuery(id+"F1.opExtrude","CAP_FACE",FACE,{"disambiguationData":[OSD([sQuery(id+"F0.wireOp",EDGE,"E0"),sQuery(id+"F0.wireOp",EDGE,"E1"),sQuery(id+"F0.wireOp",EDGE,"E2.bottom"),sQuery(id+"F0.wireOp",EDGE,"E2.left"),sQuery(id+"F0.wireOp",EDGE,"E2.right"),sQuery(id+"F0.wireOp",EDGE,"E3.1.1"),sQuery(id+"F0.wireOp",EDGE,"E3.1.2"),sQuery(id+"F0.wireOp",EDGE,"E3.1.3"),sQuery(id+"F0.wireOp",EDGE,"E3.2.1"),sQuery(id+"F0.wireOp",EDGE,"E3.2.2"),sQuery(id+"F0.wireOp",EDGE,"E3.2.3"),sQuery(id+"F0.wireOp",EDGE,"E3.3.1"),sQuery(id+"F0.wireOp",EDGE,"E3.3.2"),sQuery(id+"F0.wireOp",EDGE,"E3.3.3"),sQuery(id+"F0.wireOp",EDGE,"E3.4.1"),sQuery(id+"F0.wireOp",EDGE,"E3.4.2"),sQuery(id+"F0.wireOp",EDGE,"E3.4.3"),sQuery(id+"F0.wireOp",EDGE,"E3.5.1"),sQuery(id+"F0.wireOp",EDGE,"E3.5.2"),sQuery(id+"F0.wireOp",EDGE,"E3.5.3"),sQuery(id+"F0.wireOp",EDGE,"E3.6.1"),sQuery(id+"F0.wireOp",EDGE,"E3.6.2"),sQuery(id+"F0.wireOp",EDGE,"E3.6.3"),sQuery(id+"F0.wireOp",EDGE,"E3.7.1"),sQuery(id+"F0.wireOp",EDGE,"E3.7.2"),sQuery(id+"F0.wireOp",EDGE,"E3.7.3"),sQuery(id+"F0.wireOp",EDGE,"E3.8.1"),sQuery(id+"F0.wireOp",EDGE,"E3.8.2"),sQuery(id+"F0.wireOp",EDGE,"E3.8.3"),sQuery(id+"F0.wireOp",EDGE,"E3.9.1"),sQuery(id+"F0.wireOp",EDGE,"E3.9.2"),sQuery(id+"F0.wireOp",EDGE,"E3.9.3"),sQuery(id+"F0.wireOp",EDGE,"E3.10.1"),sQuery(id+"F0.wireOp",EDGE,"E3.10.2"),sQuery(id+"F0.wireOp",EDGE,"E3.10.3"),subQ1,subQ0,sQuery(id+"F0.wireOp",EDGE,"E3.11.3"),sQuery(id+"F0.wireOp",EDGE,"E3.12.1"),sQuery(id+"F0.wireOp",EDGE,"E3.12.2"),sQuery(id+"F0.wireOp",EDGE,"E3.12.3")])],"isStart":false})]}),makeQuery(id+"F1.opExtrude","CAP_EDGE",EDGE,{"disambiguationData":[OSD([subQ0])],"isStart":false})],"blendedInto":[]});}
            var Q19;
            {var subQ0=sQuery(id+"F0.wireOp",EDGE,"E3.11.2");var subQ1=sQuery(id+"F0.wireOp",EDGE,"E3.11.3");Q19=makeQuery(id+"F4.opChamfer","BLEND_EDGE",EDGE,{"blendedFrom":[makeQuery(id+"F3.opChamfer","BLEND_EDGE",EDGE,{"blendedFrom":[makeQuery(id+"F1.opExtrude","SWEPT_EDGE",EDGE,{"disambiguationData":[OSD([subQ0,subQ1])]}),makeQuery(id+"F1.opExtrude","CAP_FACE",FACE,{"disambiguationData":[OSD([sQuery(id+"F0.wireOp",EDGE,"E0"),sQuery(id+"F0.wireOp",EDGE,"E1"),sQuery(id+"F0.wireOp",EDGE,"E2.bottom"),sQuery(id+"F0.wireOp",EDGE,"E2.left"),sQuery(id+"F0.wireOp",EDGE,"E2.right"),sQuery(id+"F0.wireOp",EDGE,"E3.1.1"),sQuery(id+"F0.wireOp",EDGE,"E3.1.2"),sQuery(id+"F0.wireOp",EDGE,"E3.1.3"),sQuery(id+"F0.wireOp",EDGE,"E3.2.1"),sQuery(id+"F0.wireOp",EDGE,"E3.2.2"),sQuery(id+"F0.wireOp",EDGE,"E3.2.3"),sQuery(id+"F0.wireOp",EDGE,"E3.3.1"),sQuery(id+"F0.wireOp",EDGE,"E3.3.2"),sQuery(id+"F0.wireOp",EDGE,"E3.3.3"),sQuery(id+"F0.wireOp",EDGE,"E3.4.1"),sQuery(id+"F0.wireOp",EDGE,"E3.4.2"),sQuery(id+"F0.wireOp",EDGE,"E3.4.3"),sQuery(id+"F0.wireOp",EDGE,"E3.5.1"),sQuery(id+"F0.wireOp",EDGE,"E3.5.2"),sQuery(id+"F0.wireOp",EDGE,"E3.5.3"),sQuery(id+"F0.wireOp",EDGE,"E3.6.1"),sQuery(id+"F0.wireOp",EDGE,"E3.6.2"),sQuery(id+"F0.wireOp",EDGE,"E3.6.3"),sQuery(id+"F0.wireOp",EDGE,"E3.7.1"),sQuery(id+"F0.wireOp",EDGE,"E3.7.2"),sQuery(id+"F0.wireOp",EDGE,"E3.7.3"),sQuery(id+"F0.wireOp",EDGE,"E3.8.1"),sQuery(id+"F0.wireOp",EDGE,"E3.8.2"),sQuery(id+"F0.wireOp",EDGE,"E3.8.3"),sQuery(id+"F0.wireOp",EDGE,"E3.9.1"),sQuery(id+"F0.wireOp",EDGE,"E3.9.2"),sQuery(id+"F0.wireOp",EDGE,"E3.9.3"),sQuery(id+"F0.wireOp",EDGE,"E3.10.1"),sQuery(id+"F0.wireOp",EDGE,"E3.10.2"),sQuery(id+"F0.wireOp",EDGE,"E3.10.3"),sQuery(id+"F0.wireOp",EDGE,"E3.11.1"),subQ0,subQ1,sQuery(id+"F0.wireOp",EDGE,"E3.12.1"),sQuery(id+"F0.wireOp",EDGE,"E3.12.2"),sQuery(id+"F0.wireOp",EDGE,"E3.12.3")])],"isStart":false})],"blendedInto":[makeQuery(id+"F1.opExtrude","CAP_FACE",FACE,{"disambiguationData":[OSD([sQuery(id+"F0.wireOp",EDGE,"E0"),sQuery(id+"F0.wireOp",EDGE,"E1"),sQuery(id+"F0.wireOp",EDGE,"E2.bottom"),sQuery(id+"F0.wireOp",EDGE,"E2.left"),sQuery(id+"F0.wireOp",EDGE,"E2.right"),sQuery(id+"F0.wireOp",EDGE,"E3.1.1"),sQuery(id+"F0.wireOp",EDGE,"E3.1.2"),sQuery(id+"F0.wireOp",EDGE,"E3.1.3"),sQuery(id+"F0.wireOp",EDGE,"E3.2.1"),sQuery(id+"F0.wireOp",EDGE,"E3.2.2"),sQuery(id+"F0.wireOp",EDGE,"E3.2.3"),sQuery(id+"F0.wireOp",EDGE,"E3.3.1"),sQuery(id+"F0.wireOp",EDGE,"E3.3.2"),sQuery(id+"F0.wireOp",EDGE,"E3.3.3"),sQuery(id+"F0.wireOp",EDGE,"E3.4.1"),sQuery(id+"F0.wireOp",EDGE,"E3.4.2"),sQuery(id+"F0.wireOp",EDGE,"E3.4.3"),sQuery(id+"F0.wireOp",EDGE,"E3.5.1"),sQuery(id+"F0.wireOp",EDGE,"E3.5.2"),sQuery(id+"F0.wireOp",EDGE,"E3.5.3"),sQuery(id+"F0.wireOp",EDGE,"E3.6.1"),sQuery(id+"F0.wireOp",EDGE,"E3.6.2"),sQuery(id+"F0.wireOp",EDGE,"E3.6.3"),sQuery(id+"F0.wireOp",EDGE,"E3.7.1"),sQuery(id+"F0.wireOp",EDGE,"E3.7.2"),sQuery(id+"F0.wireOp",EDGE,"E3.7.3"),sQuery(id+"F0.wireOp",EDGE,"E3.8.1"),sQuery(id+"F0.wireOp",EDGE,"E3.8.2"),sQuery(id+"F0.wireOp",EDGE,"E3.8.3"),sQuery(id+"F0.wireOp",EDGE,"E3.9.1"),sQuery(id+"F0.wireOp",EDGE,"E3.9.2"),sQuery(id+"F0.wireOp",EDGE,"E3.9.3"),sQuery(id+"F0.wireOp",EDGE,"E3.10.1"),sQuery(id+"F0.wireOp",EDGE,"E3.10.2"),sQuery(id+"F0.wireOp",EDGE,"E3.10.3"),sQuery(id+"F0.wireOp",EDGE,"E3.11.1"),subQ0,subQ1,sQuery(id+"F0.wireOp",EDGE,"E3.12.1"),sQuery(id+"F0.wireOp",EDGE,"E3.12.2"),sQuery(id+"F0.wireOp",EDGE,"E3.12.3")])],"isStart":false})]}),makeQuery(id+"F1.opExtrude","CAP_EDGE",EDGE,{"disambiguationData":[OSD([subQ0])],"isStart":false})],"blendedInto":[]});}
            var Q20;
            {var subQ0=sQuery(id+"F0.wireOp",EDGE,"E3.10.2");Q20=makeQuery(id+"F3.opChamfer","BLEND_EDGE",EDGE,{"blendedFrom":[makeQuery(id+"F1.opExtrude","SWEPT_EDGE",EDGE,{"disambiguationData":[OSD([sQuery(id+"F0.wireOp",EDGE,"E3.10.1"),subQ0])]}),makeQuery(id+"F1.opExtrude","SWEPT_FACE",FACE,{"disambiguationData":[OSD([subQ0])]})],"blendedInto":[makeQuery(id+"F1.opExtrude","SWEPT_FACE",FACE,{"disambiguationData":[OSD([subQ0])]})]});}
            var Q21;
            {var subQ0=sQuery(id+"F0.wireOp",EDGE,"E3.10.2");Q21=makeQuery(id+"F3.opChamfer","BLEND_EDGE",EDGE,{"blendedFrom":[makeQuery(id+"F1.opExtrude","SWEPT_EDGE",EDGE,{"disambiguationData":[OSD([subQ0,sQuery(id+"F0.wireOp",EDGE,"E3.10.3")])]}),makeQuery(id+"F1.opExtrude","SWEPT_FACE",FACE,{"disambiguationData":[OSD([subQ0])]})],"blendedInto":[makeQuery(id+"F1.opExtrude","SWEPT_FACE",FACE,{"disambiguationData":[OSD([subQ0])]})]});}
            var Q22;
            {var subQ0=sQuery(id+"F0.wireOp",EDGE,"E3.10.2");var subQ1=sQuery(id+"F0.wireOp",EDGE,"E3.10.1");Q22=makeQuery(id+"F4.opChamfer","BLEND_EDGE",EDGE,{"blendedFrom":[makeQuery(id+"F3.opChamfer","BLEND_EDGE",EDGE,{"blendedFrom":[makeQuery(id+"F1.opExtrude","SWEPT_EDGE",EDGE,{"disambiguationData":[OSD([subQ1,subQ0])]}),makeQuery(id+"F1.opExtrude","CAP_FACE",FACE,{"disambiguationData":[OSD([sQuery(id+"F0.wireOp",EDGE,"E0"),sQuery(id+"F0.wireOp",EDGE,"E1"),sQuery(id+"F0.wireOp",EDGE,"E2.bottom"),sQuery(id+"F0.wireOp",EDGE,"E2.left"),sQuery(id+"F0.wireOp",EDGE,"E2.right"),sQuery(id+"F0.wireOp",EDGE,"E3.1.1"),sQuery(id+"F0.wireOp",EDGE,"E3.1.2"),sQuery(id+"F0.wireOp",EDGE,"E3.1.3"),sQuery(id+"F0.wireOp",EDGE,"E3.2.1"),sQuery(id+"F0.wireOp",EDGE,"E3.2.2"),sQuery(id+"F0.wireOp",EDGE,"E3.2.3"),sQuery(id+"F0.wireOp",EDGE,"E3.3.1"),sQuery(id+"F0.wireOp",EDGE,"E3.3.2"),sQuery(id+"F0.wireOp",EDGE,"E3.3.3"),sQuery(id+"F0.wireOp",EDGE,"E3.4.1"),sQuery(id+"F0.wireOp",EDGE,"E3.4.2"),sQuery(id+"F0.wireOp",EDGE,"E3.4.3"),sQuery(id+"F0.wireOp",EDGE,"E3.5.1"),sQuery(id+"F0.wireOp",EDGE,"E3.5.2"),sQuery(id+"F0.wireOp",EDGE,"E3.5.3"),sQuery(id+"F0.wireOp",EDGE,"E3.6.1"),sQuery(id+"F0.wireOp",EDGE,"E3.6.2"),sQuery(id+"F0.wireOp",EDGE,"E3.6.3"),sQuery(id+"F0.wireOp",EDGE,"E3.7.1"),sQuery(id+"F0.wireOp",EDGE,"E3.7.2"),sQuery(id+"F0.wireOp",EDGE,"E3.7.3"),sQuery(id+"F0.wireOp",EDGE,"E3.8.1"),sQuery(id+"F0.wireOp",EDGE,"E3.8.2"),sQuery(id+"F0.wireOp",EDGE,"E3.8.3"),sQuery(id+"F0.wireOp",EDGE,"E3.9.1"),sQuery(id+"F0.wireOp",EDGE,"E3.9.2"),sQuery(id+"F0.wireOp",EDGE,"E3.9.3"),subQ1,subQ0,sQuery(id+"F0.wireOp",EDGE,"E3.10.3"),sQuery(id+"F0.wireOp",EDGE,"E3.11.1"),sQuery(id+"F0.wireOp",EDGE,"E3.11.2"),sQuery(id+"F0.wireOp",EDGE,"E3.11.3"),sQuery(id+"F0.wireOp",EDGE,"E3.12.1"),sQuery(id+"F0.wireOp",EDGE,"E3.12.2"),sQuery(id+"F0.wireOp",EDGE,"E3.12.3")])],"isStart":false})],"blendedInto":[makeQuery(id+"F1.opExtrude","CAP_FACE",FACE,{"disambiguationData":[OSD([sQuery(id+"F0.wireOp",EDGE,"E0"),sQuery(id+"F0.wireOp",EDGE,"E1"),sQuery(id+"F0.wireOp",EDGE,"E2.bottom"),sQuery(id+"F0.wireOp",EDGE,"E2.left"),sQuery(id+"F0.wireOp",EDGE,"E2.right"),sQuery(id+"F0.wireOp",EDGE,"E3.1.1"),sQuery(id+"F0.wireOp",EDGE,"E3.1.2"),sQuery(id+"F0.wireOp",EDGE,"E3.1.3"),sQuery(id+"F0.wireOp",EDGE,"E3.2.1"),sQuery(id+"F0.wireOp",EDGE,"E3.2.2"),sQuery(id+"F0.wireOp",EDGE,"E3.2.3"),sQuery(id+"F0.wireOp",EDGE,"E3.3.1"),sQuery(id+"F0.wireOp",EDGE,"E3.3.2"),sQuery(id+"F0.wireOp",EDGE,"E3.3.3"),sQuery(id+"F0.wireOp",EDGE,"E3.4.1"),sQuery(id+"F0.wireOp",EDGE,"E3.4.2"),sQuery(id+"F0.wireOp",EDGE,"E3.4.3"),sQuery(id+"F0.wireOp",EDGE,"E3.5.1"),sQuery(id+"F0.wireOp",EDGE,"E3.5.2"),sQuery(id+"F0.wireOp",EDGE,"E3.5.3"),sQuery(id+"F0.wireOp",EDGE,"E3.6.1"),sQuery(id+"F0.wireOp",EDGE,"E3.6.2"),sQuery(id+"F0.wireOp",EDGE,"E3.6.3"),sQuery(id+"F0.wireOp",EDGE,"E3.7.1"),sQuery(id+"F0.wireOp",EDGE,"E3.7.2"),sQuery(id+"F0.wireOp",EDGE,"E3.7.3"),sQuery(id+"F0.wireOp",EDGE,"E3.8.1"),sQuery(id+"F0.wireOp",EDGE,"E3.8.2"),sQuery(id+"F0.wireOp",EDGE,"E3.8.3"),sQuery(id+"F0.wireOp",EDGE,"E3.9.1"),sQuery(id+"F0.wireOp",EDGE,"E3.9.2"),sQuery(id+"F0.wireOp",EDGE,"E3.9.3"),subQ1,subQ0,sQuery(id+"F0.wireOp",EDGE,"E3.10.3"),sQuery(id+"F0.wireOp",EDGE,"E3.11.1"),sQuery(id+"F0.wireOp",EDGE,"E3.11.2"),sQuery(id+"F0.wireOp",EDGE,"E3.11.3"),sQuery(id+"F0.wireOp",EDGE,"E3.12.1"),sQuery(id+"F0.wireOp",EDGE,"E3.12.2"),sQuery(id+"F0.wireOp",EDGE,"E3.12.3")])],"isStart":false})]}),makeQuery(id+"F1.opExtrude","CAP_EDGE",EDGE,{"disambiguationData":[OSD([subQ0])],"isStart":false})],"blendedInto":[]});}
            var Q23;
            {var subQ0=sQuery(id+"F0.wireOp",EDGE,"E3.10.2");var subQ1=sQuery(id+"F0.wireOp",EDGE,"E3.10.3");Q23=makeQuery(id+"F4.opChamfer","BLEND_EDGE",EDGE,{"blendedFrom":[makeQuery(id+"F3.opChamfer","BLEND_EDGE",EDGE,{"blendedFrom":[makeQuery(id+"F1.opExtrude","SWEPT_EDGE",EDGE,{"disambiguationData":[OSD([subQ0,subQ1])]}),makeQuery(id+"F1.opExtrude","CAP_FACE",FACE,{"disambiguationData":[OSD([sQuery(id+"F0.wireOp",EDGE,"E0"),sQuery(id+"F0.wireOp",EDGE,"E1"),sQuery(id+"F0.wireOp",EDGE,"E2.bottom"),sQuery(id+"F0.wireOp",EDGE,"E2.left"),sQuery(id+"F0.wireOp",EDGE,"E2.right"),sQuery(id+"F0.wireOp",EDGE,"E3.1.1"),sQuery(id+"F0.wireOp",EDGE,"E3.1.2"),sQuery(id+"F0.wireOp",EDGE,"E3.1.3"),sQuery(id+"F0.wireOp",EDGE,"E3.2.1"),sQuery(id+"F0.wireOp",EDGE,"E3.2.2"),sQuery(id+"F0.wireOp",EDGE,"E3.2.3"),sQuery(id+"F0.wireOp",EDGE,"E3.3.1"),sQuery(id+"F0.wireOp",EDGE,"E3.3.2"),sQuery(id+"F0.wireOp",EDGE,"E3.3.3"),sQuery(id+"F0.wireOp",EDGE,"E3.4.1"),sQuery(id+"F0.wireOp",EDGE,"E3.4.2"),sQuery(id+"F0.wireOp",EDGE,"E3.4.3"),sQuery(id+"F0.wireOp",EDGE,"E3.5.1"),sQuery(id+"F0.wireOp",EDGE,"E3.5.2"),sQuery(id+"F0.wireOp",EDGE,"E3.5.3"),sQuery(id+"F0.wireOp",EDGE,"E3.6.1"),sQuery(id+"F0.wireOp",EDGE,"E3.6.2"),sQuery(id+"F0.wireOp",EDGE,"E3.6.3"),sQuery(id+"F0.wireOp",EDGE,"E3.7.1"),sQuery(id+"F0.wireOp",EDGE,"E3.7.2"),sQuery(id+"F0.wireOp",EDGE,"E3.7.3"),sQuery(id+"F0.wireOp",EDGE,"E3.8.1"),sQuery(id+"F0.wireOp",EDGE,"E3.8.2"),sQuery(id+"F0.wireOp",EDGE,"E3.8.3"),sQuery(id+"F0.wireOp",EDGE,"E3.9.1"),sQuery(id+"F0.wireOp",EDGE,"E3.9.2"),sQuery(id+"F0.wireOp",EDGE,"E3.9.3"),sQuery(id+"F0.wireOp",EDGE,"E3.10.1"),subQ0,subQ1,sQuery(id+"F0.wireOp",EDGE,"E3.11.1"),sQuery(id+"F0.wireOp",EDGE,"E3.11.2"),sQuery(id+"F0.wireOp",EDGE,"E3.11.3"),sQuery(id+"F0.wireOp",EDGE,"E3.12.1"),sQuery(id+"F0.wireOp",EDGE,"E3.12.2"),sQuery(id+"F0.wireOp",EDGE,"E3.12.3")])],"isStart":false})],"blendedInto":[makeQuery(id+"F1.opExtrude","CAP_FACE",FACE,{"disambiguationData":[OSD([sQuery(id+"F0.wireOp",EDGE,"E0"),sQuery(id+"F0.wireOp",EDGE,"E1"),sQuery(id+"F0.wireOp",EDGE,"E2.bottom"),sQuery(id+"F0.wireOp",EDGE,"E2.left"),sQuery(id+"F0.wireOp",EDGE,"E2.right"),sQuery(id+"F0.wireOp",EDGE,"E3.1.1"),sQuery(id+"F0.wireOp",EDGE,"E3.1.2"),sQuery(id+"F0.wireOp",EDGE,"E3.1.3"),sQuery(id+"F0.wireOp",EDGE,"E3.2.1"),sQuery(id+"F0.wireOp",EDGE,"E3.2.2"),sQuery(id+"F0.wireOp",EDGE,"E3.2.3"),sQuery(id+"F0.wireOp",EDGE,"E3.3.1"),sQuery(id+"F0.wireOp",EDGE,"E3.3.2"),sQuery(id+"F0.wireOp",EDGE,"E3.3.3"),sQuery(id+"F0.wireOp",EDGE,"E3.4.1"),sQuery(id+"F0.wireOp",EDGE,"E3.4.2"),sQuery(id+"F0.wireOp",EDGE,"E3.4.3"),sQuery(id+"F0.wireOp",EDGE,"E3.5.1"),sQuery(id+"F0.wireOp",EDGE,"E3.5.2"),sQuery(id+"F0.wireOp",EDGE,"E3.5.3"),sQuery(id+"F0.wireOp",EDGE,"E3.6.1"),sQuery(id+"F0.wireOp",EDGE,"E3.6.2"),sQuery(id+"F0.wireOp",EDGE,"E3.6.3"),sQuery(id+"F0.wireOp",EDGE,"E3.7.1"),sQuery(id+"F0.wireOp",EDGE,"E3.7.2"),sQuery(id+"F0.wireOp",EDGE,"E3.7.3"),sQuery(id+"F0.wireOp",EDGE,"E3.8.1"),sQuery(id+"F0.wireOp",EDGE,"E3.8.2"),sQuery(id+"F0.wireOp",EDGE,"E3.8.3"),sQuery(id+"F0.wireOp",EDGE,"E3.9.1"),sQuery(id+"F0.wireOp",EDGE,"E3.9.2"),sQuery(id+"F0.wireOp",EDGE,"E3.9.3"),sQuery(id+"F0.wireOp",EDGE,"E3.10.1"),subQ0,subQ1,sQuery(id+"F0.wireOp",EDGE,"E3.11.1"),sQuery(id+"F0.wireOp",EDGE,"E3.11.2"),sQuery(id+"F0.wireOp",EDGE,"E3.11.3"),sQuery(id+"F0.wireOp",EDGE,"E3.12.1"),sQuery(id+"F0.wireOp",EDGE,"E3.12.2"),sQuery(id+"F0.wireOp",EDGE,"E3.12.3")])],"isStart":false})]}),makeQuery(id+"F1.opExtrude","CAP_EDGE",EDGE,{"disambiguationData":[OSD([subQ0])],"isStart":false})],"blendedInto":[]});}
            var Q24;
            {var subQ0=sQuery(id+"F0.wireOp",EDGE,"E3.3.2");var subQ1=sQuery(id+"F0.wireOp",EDGE,"E3.3.3");Q24=makeQuery(id+"F4.opChamfer","BLEND_EDGE",EDGE,{"blendedFrom":[makeQuery(id+"F3.opChamfer","BLEND_EDGE",EDGE,{"blendedFrom":[makeQuery(id+"F1.opExtrude","SWEPT_EDGE",EDGE,{"disambiguationData":[OSD([subQ0,subQ1])]}),makeQuery(id+"F1.opExtrude","CAP_FACE",FACE,{"disambiguationData":[OSD([sQuery(id+"F0.wireOp",EDGE,"E0"),sQuery(id+"F0.wireOp",EDGE,"E1"),sQuery(id+"F0.wireOp",EDGE,"E2.bottom"),sQuery(id+"F0.wireOp",EDGE,"E2.left"),sQuery(id+"F0.wireOp",EDGE,"E2.right"),sQuery(id+"F0.wireOp",EDGE,"E3.1.1"),sQuery(id+"F0.wireOp",EDGE,"E3.1.2"),sQuery(id+"F0.wireOp",EDGE,"E3.1.3"),sQuery(id+"F0.wireOp",EDGE,"E3.2.1"),sQuery(id+"F0.wireOp",EDGE,"E3.2.2"),sQuery(id+"F0.wireOp",EDGE,"E3.2.3"),sQuery(id+"F0.wireOp",EDGE,"E3.3.1"),subQ0,subQ1,sQuery(id+"F0.wireOp",EDGE,"E3.4.1"),sQuery(id+"F0.wireOp",EDGE,"E3.4.2"),sQuery(id+"F0.wireOp",EDGE,"E3.4.3"),sQuery(id+"F0.wireOp",EDGE,"E3.5.1"),sQuery(id+"F0.wireOp",EDGE,"E3.5.2"),sQuery(id+"F0.wireOp",EDGE,"E3.5.3"),sQuery(id+"F0.wireOp",EDGE,"E3.6.1"),sQuery(id+"F0.wireOp",EDGE,"E3.6.2"),sQuery(id+"F0.wireOp",EDGE,"E3.6.3"),sQuery(id+"F0.wireOp",EDGE,"E3.7.1"),sQuery(id+"F0.wireOp",EDGE,"E3.7.2"),sQuery(id+"F0.wireOp",EDGE,"E3.7.3"),sQuery(id+"F0.wireOp",EDGE,"E3.8.1"),sQuery(id+"F0.wireOp",EDGE,"E3.8.2"),sQuery(id+"F0.wireOp",EDGE,"E3.8.3"),sQuery(id+"F0.wireOp",EDGE,"E3.9.1"),sQuery(id+"F0.wireOp",EDGE,"E3.9.2"),sQuery(id+"F0.wireOp",EDGE,"E3.9.3"),sQuery(id+"F0.wireOp",EDGE,"E3.10.1"),sQuery(id+"F0.wireOp",EDGE,"E3.10.2"),sQuery(id+"F0.wireOp",EDGE,"E3.10.3"),sQuery(id+"F0.wireOp",EDGE,"E3.11.1"),sQuery(id+"F0.wireOp",EDGE,"E3.11.2"),sQuery(id+"F0.wireOp",EDGE,"E3.11.3"),sQuery(id+"F0.wireOp",EDGE,"E3.12.1"),sQuery(id+"F0.wireOp",EDGE,"E3.12.2"),sQuery(id+"F0.wireOp",EDGE,"E3.12.3")])],"isStart":false})],"blendedInto":[makeQuery(id+"F1.opExtrude","CAP_FACE",FACE,{"disambiguationData":[OSD([sQuery(id+"F0.wireOp",EDGE,"E0"),sQuery(id+"F0.wireOp",EDGE,"E1"),sQuery(id+"F0.wireOp",EDGE,"E2.bottom"),sQuery(id+"F0.wireOp",EDGE,"E2.left"),sQuery(id+"F0.wireOp",EDGE,"E2.right"),sQuery(id+"F0.wireOp",EDGE,"E3.1.1"),sQuery(id+"F0.wireOp",EDGE,"E3.1.2"),sQuery(id+"F0.wireOp",EDGE,"E3.1.3"),sQuery(id+"F0.wireOp",EDGE,"E3.2.1"),sQuery(id+"F0.wireOp",EDGE,"E3.2.2"),sQuery(id+"F0.wireOp",EDGE,"E3.2.3"),sQuery(id+"F0.wireOp",EDGE,"E3.3.1"),subQ0,subQ1,sQuery(id+"F0.wireOp",EDGE,"E3.4.1"),sQuery(id+"F0.wireOp",EDGE,"E3.4.2"),sQuery(id+"F0.wireOp",EDGE,"E3.4.3"),sQuery(id+"F0.wireOp",EDGE,"E3.5.1"),sQuery(id+"F0.wireOp",EDGE,"E3.5.2"),sQuery(id+"F0.wireOp",EDGE,"E3.5.3"),sQuery(id+"F0.wireOp",EDGE,"E3.6.1"),sQuery(id+"F0.wireOp",EDGE,"E3.6.2"),sQuery(id+"F0.wireOp",EDGE,"E3.6.3"),sQuery(id+"F0.wireOp",EDGE,"E3.7.1"),sQuery(id+"F0.wireOp",EDGE,"E3.7.2"),sQuery(id+"F0.wireOp",EDGE,"E3.7.3"),sQuery(id+"F0.wireOp",EDGE,"E3.8.1"),sQuery(id+"F0.wireOp",EDGE,"E3.8.2"),sQuery(id+"F0.wireOp",EDGE,"E3.8.3"),sQuery(id+"F0.wireOp",EDGE,"E3.9.1"),sQuery(id+"F0.wireOp",EDGE,"E3.9.2"),sQuery(id+"F0.wireOp",EDGE,"E3.9.3"),sQuery(id+"F0.wireOp",EDGE,"E3.10.1"),sQuery(id+"F0.wireOp",EDGE,"E3.10.2"),sQuery(id+"F0.wireOp",EDGE,"E3.10.3"),sQuery(id+"F0.wireOp",EDGE,"E3.11.1"),sQuery(id+"F0.wireOp",EDGE,"E3.11.2"),sQuery(id+"F0.wireOp",EDGE,"E3.11.3"),sQuery(id+"F0.wireOp",EDGE,"E3.12.1"),sQuery(id+"F0.wireOp",EDGE,"E3.12.2"),sQuery(id+"F0.wireOp",EDGE,"E3.12.3")])],"isStart":false})]}),makeQuery(id+"F1.opExtrude","CAP_EDGE",EDGE,{"disambiguationData":[OSD([subQ0])],"isStart":false})],"blendedInto":[]});}
            var Q25;
            {var subQ0=sQuery(id+"F0.wireOp",EDGE,"E3.3.2");var subQ1=sQuery(id+"F0.wireOp",EDGE,"E3.3.1");Q25=makeQuery(id+"F4.opChamfer","BLEND_EDGE",EDGE,{"blendedFrom":[makeQuery(id+"F3.opChamfer","BLEND_EDGE",EDGE,{"blendedFrom":[makeQuery(id+"F1.opExtrude","SWEPT_EDGE",EDGE,{"disambiguationData":[OSD([subQ1,subQ0])]}),makeQuery(id+"F1.opExtrude","CAP_FACE",FACE,{"disambiguationData":[OSD([sQuery(id+"F0.wireOp",EDGE,"E0"),sQuery(id+"F0.wireOp",EDGE,"E1"),sQuery(id+"F0.wireOp",EDGE,"E2.bottom"),sQuery(id+"F0.wireOp",EDGE,"E2.left"),sQuery(id+"F0.wireOp",EDGE,"E2.right"),sQuery(id+"F0.wireOp",EDGE,"E3.1.1"),sQuery(id+"F0.wireOp",EDGE,"E3.1.2"),sQuery(id+"F0.wireOp",EDGE,"E3.1.3"),sQuery(id+"F0.wireOp",EDGE,"E3.2.1"),sQuery(id+"F0.wireOp",EDGE,"E3.2.2"),sQuery(id+"F0.wireOp",EDGE,"E3.2.3"),subQ1,subQ0,sQuery(id+"F0.wireOp",EDGE,"E3.3.3"),sQuery(id+"F0.wireOp",EDGE,"E3.4.1"),sQuery(id+"F0.wireOp",EDGE,"E3.4.2"),sQuery(id+"F0.wireOp",EDGE,"E3.4.3"),sQuery(id+"F0.wireOp",EDGE,"E3.5.1"),sQuery(id+"F0.wireOp",EDGE,"E3.5.2"),sQuery(id+"F0.wireOp",EDGE,"E3.5.3"),sQuery(id+"F0.wireOp",EDGE,"E3.6.1"),sQuery(id+"F0.wireOp",EDGE,"E3.6.2"),sQuery(id+"F0.wireOp",EDGE,"E3.6.3"),sQuery(id+"F0.wireOp",EDGE,"E3.7.1"),sQuery(id+"F0.wireOp",EDGE,"E3.7.2"),sQuery(id+"F0.wireOp",EDGE,"E3.7.3"),sQuery(id+"F0.wireOp",EDGE,"E3.8.1"),sQuery(id+"F0.wireOp",EDGE,"E3.8.2"),sQuery(id+"F0.wireOp",EDGE,"E3.8.3"),sQuery(id+"F0.wireOp",EDGE,"E3.9.1"),sQuery(id+"F0.wireOp",EDGE,"E3.9.2"),sQuery(id+"F0.wireOp",EDGE,"E3.9.3"),sQuery(id+"F0.wireOp",EDGE,"E3.10.1"),sQuery(id+"F0.wireOp",EDGE,"E3.10.2"),sQuery(id+"F0.wireOp",EDGE,"E3.10.3"),sQuery(id+"F0.wireOp",EDGE,"E3.11.1"),sQuery(id+"F0.wireOp",EDGE,"E3.11.2"),sQuery(id+"F0.wireOp",EDGE,"E3.11.3"),sQuery(id+"F0.wireOp",EDGE,"E3.12.1"),sQuery(id+"F0.wireOp",EDGE,"E3.12.2"),sQuery(id+"F0.wireOp",EDGE,"E3.12.3")])],"isStart":false})],"blendedInto":[makeQuery(id+"F1.opExtrude","CAP_FACE",FACE,{"disambiguationData":[OSD([sQuery(id+"F0.wireOp",EDGE,"E0"),sQuery(id+"F0.wireOp",EDGE,"E1"),sQuery(id+"F0.wireOp",EDGE,"E2.bottom"),sQuery(id+"F0.wireOp",EDGE,"E2.left"),sQuery(id+"F0.wireOp",EDGE,"E2.right"),sQuery(id+"F0.wireOp",EDGE,"E3.1.1"),sQuery(id+"F0.wireOp",EDGE,"E3.1.2"),sQuery(id+"F0.wireOp",EDGE,"E3.1.3"),sQuery(id+"F0.wireOp",EDGE,"E3.2.1"),sQuery(id+"F0.wireOp",EDGE,"E3.2.2"),sQuery(id+"F0.wireOp",EDGE,"E3.2.3"),subQ1,subQ0,sQuery(id+"F0.wireOp",EDGE,"E3.3.3"),sQuery(id+"F0.wireOp",EDGE,"E3.4.1"),sQuery(id+"F0.wireOp",EDGE,"E3.4.2"),sQuery(id+"F0.wireOp",EDGE,"E3.4.3"),sQuery(id+"F0.wireOp",EDGE,"E3.5.1"),sQuery(id+"F0.wireOp",EDGE,"E3.5.2"),sQuery(id+"F0.wireOp",EDGE,"E3.5.3"),sQuery(id+"F0.wireOp",EDGE,"E3.6.1"),sQuery(id+"F0.wireOp",EDGE,"E3.6.2"),sQuery(id+"F0.wireOp",EDGE,"E3.6.3"),sQuery(id+"F0.wireOp",EDGE,"E3.7.1"),sQuery(id+"F0.wireOp",EDGE,"E3.7.2"),sQuery(id+"F0.wireOp",EDGE,"E3.7.3"),sQuery(id+"F0.wireOp",EDGE,"E3.8.1"),sQuery(id+"F0.wireOp",EDGE,"E3.8.2"),sQuery(id+"F0.wireOp",EDGE,"E3.8.3"),sQuery(id+"F0.wireOp",EDGE,"E3.9.1"),sQuery(id+"F0.wireOp",EDGE,"E3.9.2"),sQuery(id+"F0.wireOp",EDGE,"E3.9.3"),sQuery(id+"F0.wireOp",EDGE,"E3.10.1"),sQuery(id+"F0.wireOp",EDGE,"E3.10.2"),sQuery(id+"F0.wireOp",EDGE,"E3.10.3"),sQuery(id+"F0.wireOp",EDGE,"E3.11.1"),sQuery(id+"F0.wireOp",EDGE,"E3.11.2"),sQuery(id+"F0.wireOp",EDGE,"E3.11.3"),sQuery(id+"F0.wireOp",EDGE,"E3.12.1"),sQuery(id+"F0.wireOp",EDGE,"E3.12.2"),sQuery(id+"F0.wireOp",EDGE,"E3.12.3")])],"isStart":false})]}),makeQuery(id+"F1.opExtrude","CAP_EDGE",EDGE,{"disambiguationData":[OSD([subQ0])],"isStart":false})],"blendedInto":[]});}
            var Q26;
            {var subQ0=sQuery(id+"F0.wireOp",EDGE,"E3.3.2");Q26=makeQuery(id+"F3.opChamfer","BLEND_EDGE",EDGE,{"blendedFrom":[makeQuery(id+"F1.opExtrude","SWEPT_EDGE",EDGE,{"disambiguationData":[OSD([subQ0,sQuery(id+"F0.wireOp",EDGE,"E3.3.3")])]}),makeQuery(id+"F1.opExtrude","SWEPT_FACE",FACE,{"disambiguationData":[OSD([subQ0])]})],"blendedInto":[makeQuery(id+"F1.opExtrude","SWEPT_FACE",FACE,{"disambiguationData":[OSD([subQ0])]})]});}
            var Q27;
            {var subQ0=sQuery(id+"F0.wireOp",EDGE,"E3.3.2");Q27=makeQuery(id+"F3.opChamfer","BLEND_EDGE",EDGE,{"blendedFrom":[makeQuery(id+"F1.opExtrude","SWEPT_EDGE",EDGE,{"disambiguationData":[OSD([sQuery(id+"F0.wireOp",EDGE,"E3.3.1"),subQ0])]}),makeQuery(id+"F1.opExtrude","SWEPT_FACE",FACE,{"disambiguationData":[OSD([subQ0])]})],"blendedInto":[makeQuery(id+"F1.opExtrude","SWEPT_FACE",FACE,{"disambiguationData":[OSD([subQ0])]})]});}
            var Q28;
            {var subQ0=sQuery(id+"F0.wireOp",EDGE,"E3.4.2");var subQ1=sQuery(id+"F0.wireOp",EDGE,"E3.4.1");Q28=makeQuery(id+"F4.opChamfer","BLEND_EDGE",EDGE,{"blendedFrom":[makeQuery(id+"F3.opChamfer","BLEND_EDGE",EDGE,{"blendedFrom":[makeQuery(id+"F1.opExtrude","SWEPT_EDGE",EDGE,{"disambiguationData":[OSD([subQ1,subQ0])]}),makeQuery(id+"F1.opExtrude","CAP_FACE",FACE,{"disambiguationData":[OSD([sQuery(id+"F0.wireOp",EDGE,"E0"),sQuery(id+"F0.wireOp",EDGE,"E1"),sQuery(id+"F0.wireOp",EDGE,"E2.bottom"),sQuery(id+"F0.wireOp",EDGE,"E2.left"),sQuery(id+"F0.wireOp",EDGE,"E2.right"),sQuery(id+"F0.wireOp",EDGE,"E3.1.1"),sQuery(id+"F0.wireOp",EDGE,"E3.1.2"),sQuery(id+"F0.wireOp",EDGE,"E3.1.3"),sQuery(id+"F0.wireOp",EDGE,"E3.2.1"),sQuery(id+"F0.wireOp",EDGE,"E3.2.2"),sQuery(id+"F0.wireOp",EDGE,"E3.2.3"),sQuery(id+"F0.wireOp",EDGE,"E3.3.1"),sQuery(id+"F0.wireOp",EDGE,"E3.3.2"),sQuery(id+"F0.wireOp",EDGE,"E3.3.3"),subQ1,subQ0,sQuery(id+"F0.wireOp",EDGE,"E3.4.3"),sQuery(id+"F0.wireOp",EDGE,"E3.5.1"),sQuery(id+"F0.wireOp",EDGE,"E3.5.2"),sQuery(id+"F0.wireOp",EDGE,"E3.5.3"),sQuery(id+"F0.wireOp",EDGE,"E3.6.1"),sQuery(id+"F0.wireOp",EDGE,"E3.6.2"),sQuery(id+"F0.wireOp",EDGE,"E3.6.3"),sQuery(id+"F0.wireOp",EDGE,"E3.7.1"),sQuery(id+"F0.wireOp",EDGE,"E3.7.2"),sQuery(id+"F0.wireOp",EDGE,"E3.7.3"),sQuery(id+"F0.wireOp",EDGE,"E3.8.1"),sQuery(id+"F0.wireOp",EDGE,"E3.8.2"),sQuery(id+"F0.wireOp",EDGE,"E3.8.3"),sQuery(id+"F0.wireOp",EDGE,"E3.9.1"),sQuery(id+"F0.wireOp",EDGE,"E3.9.2"),sQuery(id+"F0.wireOp",EDGE,"E3.9.3"),sQuery(id+"F0.wireOp",EDGE,"E3.10.1"),sQuery(id+"F0.wireOp",EDGE,"E3.10.2"),sQuery(id+"F0.wireOp",EDGE,"E3.10.3"),sQuery(id+"F0.wireOp",EDGE,"E3.11.1"),sQuery(id+"F0.wireOp",EDGE,"E3.11.2"),sQuery(id+"F0.wireOp",EDGE,"E3.11.3"),sQuery(id+"F0.wireOp",EDGE,"E3.12.1"),sQuery(id+"F0.wireOp",EDGE,"E3.12.2"),sQuery(id+"F0.wireOp",EDGE,"E3.12.3")])],"isStart":false})],"blendedInto":[makeQuery(id+"F1.opExtrude","CAP_FACE",FACE,{"disambiguationData":[OSD([sQuery(id+"F0.wireOp",EDGE,"E0"),sQuery(id+"F0.wireOp",EDGE,"E1"),sQuery(id+"F0.wireOp",EDGE,"E2.bottom"),sQuery(id+"F0.wireOp",EDGE,"E2.left"),sQuery(id+"F0.wireOp",EDGE,"E2.right"),sQuery(id+"F0.wireOp",EDGE,"E3.1.1"),sQuery(id+"F0.wireOp",EDGE,"E3.1.2"),sQuery(id+"F0.wireOp",EDGE,"E3.1.3"),sQuery(id+"F0.wireOp",EDGE,"E3.2.1"),sQuery(id+"F0.wireOp",EDGE,"E3.2.2"),sQuery(id+"F0.wireOp",EDGE,"E3.2.3"),sQuery(id+"F0.wireOp",EDGE,"E3.3.1"),sQuery(id+"F0.wireOp",EDGE,"E3.3.2"),sQuery(id+"F0.wireOp",EDGE,"E3.3.3"),subQ1,subQ0,sQuery(id+"F0.wireOp",EDGE,"E3.4.3"),sQuery(id+"F0.wireOp",EDGE,"E3.5.1"),sQuery(id+"F0.wireOp",EDGE,"E3.5.2"),sQuery(id+"F0.wireOp",EDGE,"E3.5.3"),sQuery(id+"F0.wireOp",EDGE,"E3.6.1"),sQuery(id+"F0.wireOp",EDGE,"E3.6.2"),sQuery(id+"F0.wireOp",EDGE,"E3.6.3"),sQuery(id+"F0.wireOp",EDGE,"E3.7.1"),sQuery(id+"F0.wireOp",EDGE,"E3.7.2"),sQuery(id+"F0.wireOp",EDGE,"E3.7.3"),sQuery(id+"F0.wireOp",EDGE,"E3.8.1"),sQuery(id+"F0.wireOp",EDGE,"E3.8.2"),sQuery(id+"F0.wireOp",EDGE,"E3.8.3"),sQuery(id+"F0.wireOp",EDGE,"E3.9.1"),sQuery(id+"F0.wireOp",EDGE,"E3.9.2"),sQuery(id+"F0.wireOp",EDGE,"E3.9.3"),sQuery(id+"F0.wireOp",EDGE,"E3.10.1"),sQuery(id+"F0.wireOp",EDGE,"E3.10.2"),sQuery(id+"F0.wireOp",EDGE,"E3.10.3"),sQuery(id+"F0.wireOp",EDGE,"E3.11.1"),sQuery(id+"F0.wireOp",EDGE,"E3.11.2"),sQuery(id+"F0.wireOp",EDGE,"E3.11.3"),sQuery(id+"F0.wireOp",EDGE,"E3.12.1"),sQuery(id+"F0.wireOp",EDGE,"E3.12.2"),sQuery(id+"F0.wireOp",EDGE,"E3.12.3")])],"isStart":false})]}),makeQuery(id+"F1.opExtrude","CAP_EDGE",EDGE,{"disambiguationData":[OSD([subQ0])],"isStart":false})],"blendedInto":[]});}
            var Q29;
            {var subQ0=sQuery(id+"F0.wireOp",EDGE,"E3.4.2");var subQ1=sQuery(id+"F0.wireOp",EDGE,"E3.4.3");Q29=makeQuery(id+"F4.opChamfer","BLEND_EDGE",EDGE,{"blendedFrom":[makeQuery(id+"F3.opChamfer","BLEND_EDGE",EDGE,{"blendedFrom":[makeQuery(id+"F1.opExtrude","SWEPT_EDGE",EDGE,{"disambiguationData":[OSD([subQ0,subQ1])]}),makeQuery(id+"F1.opExtrude","CAP_FACE",FACE,{"disambiguationData":[OSD([sQuery(id+"F0.wireOp",EDGE,"E0"),sQuery(id+"F0.wireOp",EDGE,"E1"),sQuery(id+"F0.wireOp",EDGE,"E2.bottom"),sQuery(id+"F0.wireOp",EDGE,"E2.left"),sQuery(id+"F0.wireOp",EDGE,"E2.right"),sQuery(id+"F0.wireOp",EDGE,"E3.1.1"),sQuery(id+"F0.wireOp",EDGE,"E3.1.2"),sQuery(id+"F0.wireOp",EDGE,"E3.1.3"),sQuery(id+"F0.wireOp",EDGE,"E3.2.1"),sQuery(id+"F0.wireOp",EDGE,"E3.2.2"),sQuery(id+"F0.wireOp",EDGE,"E3.2.3"),sQuery(id+"F0.wireOp",EDGE,"E3.3.1"),sQuery(id+"F0.wireOp",EDGE,"E3.3.2"),sQuery(id+"F0.wireOp",EDGE,"E3.3.3"),sQuery(id+"F0.wireOp",EDGE,"E3.4.1"),subQ0,subQ1,sQuery(id+"F0.wireOp",EDGE,"E3.5.1"),sQuery(id+"F0.wireOp",EDGE,"E3.5.2"),sQuery(id+"F0.wireOp",EDGE,"E3.5.3"),sQuery(id+"F0.wireOp",EDGE,"E3.6.1"),sQuery(id+"F0.wireOp",EDGE,"E3.6.2"),sQuery(id+"F0.wireOp",EDGE,"E3.6.3"),sQuery(id+"F0.wireOp",EDGE,"E3.7.1"),sQuery(id+"F0.wireOp",EDGE,"E3.7.2"),sQuery(id+"F0.wireOp",EDGE,"E3.7.3"),sQuery(id+"F0.wireOp",EDGE,"E3.8.1"),sQuery(id+"F0.wireOp",EDGE,"E3.8.2"),sQuery(id+"F0.wireOp",EDGE,"E3.8.3"),sQuery(id+"F0.wireOp",EDGE,"E3.9.1"),sQuery(id+"F0.wireOp",EDGE,"E3.9.2"),sQuery(id+"F0.wireOp",EDGE,"E3.9.3"),sQuery(id+"F0.wireOp",EDGE,"E3.10.1"),sQuery(id+"F0.wireOp",EDGE,"E3.10.2"),sQuery(id+"F0.wireOp",EDGE,"E3.10.3"),sQuery(id+"F0.wireOp",EDGE,"E3.11.1"),sQuery(id+"F0.wireOp",EDGE,"E3.11.2"),sQuery(id+"F0.wireOp",EDGE,"E3.11.3"),sQuery(id+"F0.wireOp",EDGE,"E3.12.1"),sQuery(id+"F0.wireOp",EDGE,"E3.12.2"),sQuery(id+"F0.wireOp",EDGE,"E3.12.3")])],"isStart":false})],"blendedInto":[makeQuery(id+"F1.opExtrude","CAP_FACE",FACE,{"disambiguationData":[OSD([sQuery(id+"F0.wireOp",EDGE,"E0"),sQuery(id+"F0.wireOp",EDGE,"E1"),sQuery(id+"F0.wireOp",EDGE,"E2.bottom"),sQuery(id+"F0.wireOp",EDGE,"E2.left"),sQuery(id+"F0.wireOp",EDGE,"E2.right"),sQuery(id+"F0.wireOp",EDGE,"E3.1.1"),sQuery(id+"F0.wireOp",EDGE,"E3.1.2"),sQuery(id+"F0.wireOp",EDGE,"E3.1.3"),sQuery(id+"F0.wireOp",EDGE,"E3.2.1"),sQuery(id+"F0.wireOp",EDGE,"E3.2.2"),sQuery(id+"F0.wireOp",EDGE,"E3.2.3"),sQuery(id+"F0.wireOp",EDGE,"E3.3.1"),sQuery(id+"F0.wireOp",EDGE,"E3.3.2"),sQuery(id+"F0.wireOp",EDGE,"E3.3.3"),sQuery(id+"F0.wireOp",EDGE,"E3.4.1"),subQ0,subQ1,sQuery(id+"F0.wireOp",EDGE,"E3.5.1"),sQuery(id+"F0.wireOp",EDGE,"E3.5.2"),sQuery(id+"F0.wireOp",EDGE,"E3.5.3"),sQuery(id+"F0.wireOp",EDGE,"E3.6.1"),sQuery(id+"F0.wireOp",EDGE,"E3.6.2"),sQuery(id+"F0.wireOp",EDGE,"E3.6.3"),sQuery(id+"F0.wireOp",EDGE,"E3.7.1"),sQuery(id+"F0.wireOp",EDGE,"E3.7.2"),sQuery(id+"F0.wireOp",EDGE,"E3.7.3"),sQuery(id+"F0.wireOp",EDGE,"E3.8.1"),sQuery(id+"F0.wireOp",EDGE,"E3.8.2"),sQuery(id+"F0.wireOp",EDGE,"E3.8.3"),sQuery(id+"F0.wireOp",EDGE,"E3.9.1"),sQuery(id+"F0.wireOp",EDGE,"E3.9.2"),sQuery(id+"F0.wireOp",EDGE,"E3.9.3"),sQuery(id+"F0.wireOp",EDGE,"E3.10.1"),sQuery(id+"F0.wireOp",EDGE,"E3.10.2"),sQuery(id+"F0.wireOp",EDGE,"E3.10.3"),sQuery(id+"F0.wireOp",EDGE,"E3.11.1"),sQuery(id+"F0.wireOp",EDGE,"E3.11.2"),sQuery(id+"F0.wireOp",EDGE,"E3.11.3"),sQuery(id+"F0.wireOp",EDGE,"E3.12.1"),sQuery(id+"F0.wireOp",EDGE,"E3.12.2"),sQuery(id+"F0.wireOp",EDGE,"E3.12.3")])],"isStart":false})]}),makeQuery(id+"F1.opExtrude","CAP_EDGE",EDGE,{"disambiguationData":[OSD([subQ0])],"isStart":false})],"blendedInto":[]});}
            var Q30;
            {var subQ0=sQuery(id+"F0.wireOp",EDGE,"E3.4.2");Q30=makeQuery(id+"F3.opChamfer","BLEND_EDGE",EDGE,{"blendedFrom":[makeQuery(id+"F1.opExtrude","SWEPT_EDGE",EDGE,{"disambiguationData":[OSD([subQ0,sQuery(id+"F0.wireOp",EDGE,"E3.4.3")])]}),makeQuery(id+"F1.opExtrude","SWEPT_FACE",FACE,{"disambiguationData":[OSD([subQ0])]})],"blendedInto":[makeQuery(id+"F1.opExtrude","SWEPT_FACE",FACE,{"disambiguationData":[OSD([subQ0])]})]});}
            var Q31;
            {var subQ0=sQuery(id+"F0.wireOp",EDGE,"E3.4.2");Q31=makeQuery(id+"F3.opChamfer","BLEND_EDGE",EDGE,{"blendedFrom":[makeQuery(id+"F1.opExtrude","SWEPT_EDGE",EDGE,{"disambiguationData":[OSD([sQuery(id+"F0.wireOp",EDGE,"E3.4.1"),subQ0])]}),makeQuery(id+"F1.opExtrude","SWEPT_FACE",FACE,{"disambiguationData":[OSD([subQ0])]})],"blendedInto":[makeQuery(id+"F1.opExtrude","SWEPT_FACE",FACE,{"disambiguationData":[OSD([subQ0])]})]});}
            var Q32;
            {var subQ0=sQuery(id+"F0.wireOp",EDGE,"E3.5.2");var subQ1=sQuery(id+"F0.wireOp",EDGE,"E3.5.3");Q32=makeQuery(id+"F4.opChamfer","BLEND_EDGE",EDGE,{"blendedFrom":[makeQuery(id+"F3.opChamfer","BLEND_EDGE",EDGE,{"blendedFrom":[makeQuery(id+"F1.opExtrude","SWEPT_EDGE",EDGE,{"disambiguationData":[OSD([subQ0,subQ1])]}),makeQuery(id+"F1.opExtrude","CAP_FACE",FACE,{"disambiguationData":[OSD([sQuery(id+"F0.wireOp",EDGE,"E0"),sQuery(id+"F0.wireOp",EDGE,"E1"),sQuery(id+"F0.wireOp",EDGE,"E2.bottom"),sQuery(id+"F0.wireOp",EDGE,"E2.left"),sQuery(id+"F0.wireOp",EDGE,"E2.right"),sQuery(id+"F0.wireOp",EDGE,"E3.1.1"),sQuery(id+"F0.wireOp",EDGE,"E3.1.2"),sQuery(id+"F0.wireOp",EDGE,"E3.1.3"),sQuery(id+"F0.wireOp",EDGE,"E3.2.1"),sQuery(id+"F0.wireOp",EDGE,"E3.2.2"),sQuery(id+"F0.wireOp",EDGE,"E3.2.3"),sQuery(id+"F0.wireOp",EDGE,"E3.3.1"),sQuery(id+"F0.wireOp",EDGE,"E3.3.2"),sQuery(id+"F0.wireOp",EDGE,"E3.3.3"),sQuery(id+"F0.wireOp",EDGE,"E3.4.1"),sQuery(id+"F0.wireOp",EDGE,"E3.4.2"),sQuery(id+"F0.wireOp",EDGE,"E3.4.3"),sQuery(id+"F0.wireOp",EDGE,"E3.5.1"),subQ0,subQ1,sQuery(id+"F0.wireOp",EDGE,"E3.6.1"),sQuery(id+"F0.wireOp",EDGE,"E3.6.2"),sQuery(id+"F0.wireOp",EDGE,"E3.6.3"),sQuery(id+"F0.wireOp",EDGE,"E3.7.1"),sQuery(id+"F0.wireOp",EDGE,"E3.7.2"),sQuery(id+"F0.wireOp",EDGE,"E3.7.3"),sQuery(id+"F0.wireOp",EDGE,"E3.8.1"),sQuery(id+"F0.wireOp",EDGE,"E3.8.2"),sQuery(id+"F0.wireOp",EDGE,"E3.8.3"),sQuery(id+"F0.wireOp",EDGE,"E3.9.1"),sQuery(id+"F0.wireOp",EDGE,"E3.9.2"),sQuery(id+"F0.wireOp",EDGE,"E3.9.3"),sQuery(id+"F0.wireOp",EDGE,"E3.10.1"),sQuery(id+"F0.wireOp",EDGE,"E3.10.2"),sQuery(id+"F0.wireOp",EDGE,"E3.10.3"),sQuery(id+"F0.wireOp",EDGE,"E3.11.1"),sQuery(id+"F0.wireOp",EDGE,"E3.11.2"),sQuery(id+"F0.wireOp",EDGE,"E3.11.3"),sQuery(id+"F0.wireOp",EDGE,"E3.12.1"),sQuery(id+"F0.wireOp",EDGE,"E3.12.2"),sQuery(id+"F0.wireOp",EDGE,"E3.12.3")])],"isStart":false})],"blendedInto":[makeQuery(id+"F1.opExtrude","CAP_FACE",FACE,{"disambiguationData":[OSD([sQuery(id+"F0.wireOp",EDGE,"E0"),sQuery(id+"F0.wireOp",EDGE,"E1"),sQuery(id+"F0.wireOp",EDGE,"E2.bottom"),sQuery(id+"F0.wireOp",EDGE,"E2.left"),sQuery(id+"F0.wireOp",EDGE,"E2.right"),sQuery(id+"F0.wireOp",EDGE,"E3.1.1"),sQuery(id+"F0.wireOp",EDGE,"E3.1.2"),sQuery(id+"F0.wireOp",EDGE,"E3.1.3"),sQuery(id+"F0.wireOp",EDGE,"E3.2.1"),sQuery(id+"F0.wireOp",EDGE,"E3.2.2"),sQuery(id+"F0.wireOp",EDGE,"E3.2.3"),sQuery(id+"F0.wireOp",EDGE,"E3.3.1"),sQuery(id+"F0.wireOp",EDGE,"E3.3.2"),sQuery(id+"F0.wireOp",EDGE,"E3.3.3"),sQuery(id+"F0.wireOp",EDGE,"E3.4.1"),sQuery(id+"F0.wireOp",EDGE,"E3.4.2"),sQuery(id+"F0.wireOp",EDGE,"E3.4.3"),sQuery(id+"F0.wireOp",EDGE,"E3.5.1"),subQ0,subQ1,sQuery(id+"F0.wireOp",EDGE,"E3.6.1"),sQuery(id+"F0.wireOp",EDGE,"E3.6.2"),sQuery(id+"F0.wireOp",EDGE,"E3.6.3"),sQuery(id+"F0.wireOp",EDGE,"E3.7.1"),sQuery(id+"F0.wireOp",EDGE,"E3.7.2"),sQuery(id+"F0.wireOp",EDGE,"E3.7.3"),sQuery(id+"F0.wireOp",EDGE,"E3.8.1"),sQuery(id+"F0.wireOp",EDGE,"E3.8.2"),sQuery(id+"F0.wireOp",EDGE,"E3.8.3"),sQuery(id+"F0.wireOp",EDGE,"E3.9.1"),sQuery(id+"F0.wireOp",EDGE,"E3.9.2"),sQuery(id+"F0.wireOp",EDGE,"E3.9.3"),sQuery(id+"F0.wireOp",EDGE,"E3.10.1"),sQuery(id+"F0.wireOp",EDGE,"E3.10.2"),sQuery(id+"F0.wireOp",EDGE,"E3.10.3"),sQuery(id+"F0.wireOp",EDGE,"E3.11.1"),sQuery(id+"F0.wireOp",EDGE,"E3.11.2"),sQuery(id+"F0.wireOp",EDGE,"E3.11.3"),sQuery(id+"F0.wireOp",EDGE,"E3.12.1"),sQuery(id+"F0.wireOp",EDGE,"E3.12.2"),sQuery(id+"F0.wireOp",EDGE,"E3.12.3")])],"isStart":false})]}),makeQuery(id+"F1.opExtrude","CAP_EDGE",EDGE,{"disambiguationData":[OSD([subQ0])],"isStart":false})],"blendedInto":[]});}
            var Q33;
            {var subQ0=sQuery(id+"F0.wireOp",EDGE,"E3.5.2");Q33=makeQuery(id+"F3.opChamfer","BLEND_EDGE",EDGE,{"blendedFrom":[makeQuery(id+"F1.opExtrude","SWEPT_EDGE",EDGE,{"disambiguationData":[OSD([subQ0,sQuery(id+"F0.wireOp",EDGE,"E3.5.3")])]}),makeQuery(id+"F1.opExtrude","SWEPT_FACE",FACE,{"disambiguationData":[OSD([subQ0])]})],"blendedInto":[makeQuery(id+"F1.opExtrude","SWEPT_FACE",FACE,{"disambiguationData":[OSD([subQ0])]})]});}
            var Q34;
            {var subQ0=sQuery(id+"F0.wireOp",EDGE,"E3.5.2");Q34=makeQuery(id+"F3.opChamfer","BLEND_EDGE",EDGE,{"blendedFrom":[makeQuery(id+"F1.opExtrude","SWEPT_EDGE",EDGE,{"disambiguationData":[OSD([sQuery(id+"F0.wireOp",EDGE,"E3.5.1"),subQ0])]}),makeQuery(id+"F1.opExtrude","SWEPT_FACE",FACE,{"disambiguationData":[OSD([subQ0])]})],"blendedInto":[makeQuery(id+"F1.opExtrude","SWEPT_FACE",FACE,{"disambiguationData":[OSD([subQ0])]})]});}
            var Q35;
            {var subQ0=sQuery(id+"F0.wireOp",EDGE,"E3.5.2");var subQ1=sQuery(id+"F0.wireOp",EDGE,"E3.5.1");Q35=makeQuery(id+"F4.opChamfer","BLEND_EDGE",EDGE,{"blendedFrom":[makeQuery(id+"F3.opChamfer","BLEND_EDGE",EDGE,{"blendedFrom":[makeQuery(id+"F1.opExtrude","SWEPT_EDGE",EDGE,{"disambiguationData":[OSD([subQ1,subQ0])]}),makeQuery(id+"F1.opExtrude","CAP_FACE",FACE,{"disambiguationData":[OSD([sQuery(id+"F0.wireOp",EDGE,"E0"),sQuery(id+"F0.wireOp",EDGE,"E1"),sQuery(id+"F0.wireOp",EDGE,"E2.bottom"),sQuery(id+"F0.wireOp",EDGE,"E2.left"),sQuery(id+"F0.wireOp",EDGE,"E2.right"),sQuery(id+"F0.wireOp",EDGE,"E3.1.1"),sQuery(id+"F0.wireOp",EDGE,"E3.1.2"),sQuery(id+"F0.wireOp",EDGE,"E3.1.3"),sQuery(id+"F0.wireOp",EDGE,"E3.2.1"),sQuery(id+"F0.wireOp",EDGE,"E3.2.2"),sQuery(id+"F0.wireOp",EDGE,"E3.2.3"),sQuery(id+"F0.wireOp",EDGE,"E3.3.1"),sQuery(id+"F0.wireOp",EDGE,"E3.3.2"),sQuery(id+"F0.wireOp",EDGE,"E3.3.3"),sQuery(id+"F0.wireOp",EDGE,"E3.4.1"),sQuery(id+"F0.wireOp",EDGE,"E3.4.2"),sQuery(id+"F0.wireOp",EDGE,"E3.4.3"),subQ1,subQ0,sQuery(id+"F0.wireOp",EDGE,"E3.5.3"),sQuery(id+"F0.wireOp",EDGE,"E3.6.1"),sQuery(id+"F0.wireOp",EDGE,"E3.6.2"),sQuery(id+"F0.wireOp",EDGE,"E3.6.3"),sQuery(id+"F0.wireOp",EDGE,"E3.7.1"),sQuery(id+"F0.wireOp",EDGE,"E3.7.2"),sQuery(id+"F0.wireOp",EDGE,"E3.7.3"),sQuery(id+"F0.wireOp",EDGE,"E3.8.1"),sQuery(id+"F0.wireOp",EDGE,"E3.8.2"),sQuery(id+"F0.wireOp",EDGE,"E3.8.3"),sQuery(id+"F0.wireOp",EDGE,"E3.9.1"),sQuery(id+"F0.wireOp",EDGE,"E3.9.2"),sQuery(id+"F0.wireOp",EDGE,"E3.9.3"),sQuery(id+"F0.wireOp",EDGE,"E3.10.1"),sQuery(id+"F0.wireOp",EDGE,"E3.10.2"),sQuery(id+"F0.wireOp",EDGE,"E3.10.3"),sQuery(id+"F0.wireOp",EDGE,"E3.11.1"),sQuery(id+"F0.wireOp",EDGE,"E3.11.2"),sQuery(id+"F0.wireOp",EDGE,"E3.11.3"),sQuery(id+"F0.wireOp",EDGE,"E3.12.1"),sQuery(id+"F0.wireOp",EDGE,"E3.12.2"),sQuery(id+"F0.wireOp",EDGE,"E3.12.3")])],"isStart":false})],"blendedInto":[makeQuery(id+"F1.opExtrude","CAP_FACE",FACE,{"disambiguationData":[OSD([sQuery(id+"F0.wireOp",EDGE,"E0"),sQuery(id+"F0.wireOp",EDGE,"E1"),sQuery(id+"F0.wireOp",EDGE,"E2.bottom"),sQuery(id+"F0.wireOp",EDGE,"E2.left"),sQuery(id+"F0.wireOp",EDGE,"E2.right"),sQuery(id+"F0.wireOp",EDGE,"E3.1.1"),sQuery(id+"F0.wireOp",EDGE,"E3.1.2"),sQuery(id+"F0.wireOp",EDGE,"E3.1.3"),sQuery(id+"F0.wireOp",EDGE,"E3.2.1"),sQuery(id+"F0.wireOp",EDGE,"E3.2.2"),sQuery(id+"F0.wireOp",EDGE,"E3.2.3"),sQuery(id+"F0.wireOp",EDGE,"E3.3.1"),sQuery(id+"F0.wireOp",EDGE,"E3.3.2"),sQuery(id+"F0.wireOp",EDGE,"E3.3.3"),sQuery(id+"F0.wireOp",EDGE,"E3.4.1"),sQuery(id+"F0.wireOp",EDGE,"E3.4.2"),sQuery(id+"F0.wireOp",EDGE,"E3.4.3"),subQ1,subQ0,sQuery(id+"F0.wireOp",EDGE,"E3.5.3"),sQuery(id+"F0.wireOp",EDGE,"E3.6.1"),sQuery(id+"F0.wireOp",EDGE,"E3.6.2"),sQuery(id+"F0.wireOp",EDGE,"E3.6.3"),sQuery(id+"F0.wireOp",EDGE,"E3.7.1"),sQuery(id+"F0.wireOp",EDGE,"E3.7.2"),sQuery(id+"F0.wireOp",EDGE,"E3.7.3"),sQuery(id+"F0.wireOp",EDGE,"E3.8.1"),sQuery(id+"F0.wireOp",EDGE,"E3.8.2"),sQuery(id+"F0.wireOp",EDGE,"E3.8.3"),sQuery(id+"F0.wireOp",EDGE,"E3.9.1"),sQuery(id+"F0.wireOp",EDGE,"E3.9.2"),sQuery(id+"F0.wireOp",EDGE,"E3.9.3"),sQuery(id+"F0.wireOp",EDGE,"E3.10.1"),sQuery(id+"F0.wireOp",EDGE,"E3.10.2"),sQuery(id+"F0.wireOp",EDGE,"E3.10.3"),sQuery(id+"F0.wireOp",EDGE,"E3.11.1"),sQuery(id+"F0.wireOp",EDGE,"E3.11.2"),sQuery(id+"F0.wireOp",EDGE,"E3.11.3"),sQuery(id+"F0.wireOp",EDGE,"E3.12.1"),sQuery(id+"F0.wireOp",EDGE,"E3.12.2"),sQuery(id+"F0.wireOp",EDGE,"E3.12.3")])],"isStart":false})]}),makeQuery(id+"F1.opExtrude","CAP_EDGE",EDGE,{"disambiguationData":[OSD([subQ0])],"isStart":false})],"blendedInto":[]});}
            var Q36;
            {var subQ0=sQuery(id+"F0.wireOp",EDGE,"E3.6.2");Q36=makeQuery(id+"F3.opChamfer","BLEND_EDGE",EDGE,{"blendedFrom":[makeQuery(id+"F1.opExtrude","SWEPT_EDGE",EDGE,{"disambiguationData":[OSD([subQ0,sQuery(id+"F0.wireOp",EDGE,"E3.6.3")])]}),makeQuery(id+"F1.opExtrude","SWEPT_FACE",FACE,{"disambiguationData":[OSD([subQ0])]})],"blendedInto":[makeQuery(id+"F1.opExtrude","SWEPT_FACE",FACE,{"disambiguationData":[OSD([subQ0])]})]});}
            var Q37;
            {var subQ0=sQuery(id+"F0.wireOp",EDGE,"E3.6.2");Q37=makeQuery(id+"F3.opChamfer","BLEND_EDGE",EDGE,{"blendedFrom":[makeQuery(id+"F1.opExtrude","SWEPT_EDGE",EDGE,{"disambiguationData":[OSD([sQuery(id+"F0.wireOp",EDGE,"E3.6.1"),subQ0])]}),makeQuery(id+"F1.opExtrude","SWEPT_FACE",FACE,{"disambiguationData":[OSD([subQ0])]})],"blendedInto":[makeQuery(id+"F1.opExtrude","SWEPT_FACE",FACE,{"disambiguationData":[OSD([subQ0])]})]});}
            var Q38;
            {var subQ0=sQuery(id+"F0.wireOp",EDGE,"E3.6.2");var subQ1=sQuery(id+"F0.wireOp",EDGE,"E3.6.1");Q38=makeQuery(id+"F4.opChamfer","BLEND_EDGE",EDGE,{"blendedFrom":[makeQuery(id+"F3.opChamfer","BLEND_EDGE",EDGE,{"blendedFrom":[makeQuery(id+"F1.opExtrude","SWEPT_EDGE",EDGE,{"disambiguationData":[OSD([subQ1,subQ0])]}),makeQuery(id+"F1.opExtrude","CAP_FACE",FACE,{"disambiguationData":[OSD([sQuery(id+"F0.wireOp",EDGE,"E0"),sQuery(id+"F0.wireOp",EDGE,"E1"),sQuery(id+"F0.wireOp",EDGE,"E2.bottom"),sQuery(id+"F0.wireOp",EDGE,"E2.left"),sQuery(id+"F0.wireOp",EDGE,"E2.right"),sQuery(id+"F0.wireOp",EDGE,"E3.1.1"),sQuery(id+"F0.wireOp",EDGE,"E3.1.2"),sQuery(id+"F0.wireOp",EDGE,"E3.1.3"),sQuery(id+"F0.wireOp",EDGE,"E3.2.1"),sQuery(id+"F0.wireOp",EDGE,"E3.2.2"),sQuery(id+"F0.wireOp",EDGE,"E3.2.3"),sQuery(id+"F0.wireOp",EDGE,"E3.3.1"),sQuery(id+"F0.wireOp",EDGE,"E3.3.2"),sQuery(id+"F0.wireOp",EDGE,"E3.3.3"),sQuery(id+"F0.wireOp",EDGE,"E3.4.1"),sQuery(id+"F0.wireOp",EDGE,"E3.4.2"),sQuery(id+"F0.wireOp",EDGE,"E3.4.3"),sQuery(id+"F0.wireOp",EDGE,"E3.5.1"),sQuery(id+"F0.wireOp",EDGE,"E3.5.2"),sQuery(id+"F0.wireOp",EDGE,"E3.5.3"),subQ1,subQ0,sQuery(id+"F0.wireOp",EDGE,"E3.6.3"),sQuery(id+"F0.wireOp",EDGE,"E3.7.1"),sQuery(id+"F0.wireOp",EDGE,"E3.7.2"),sQuery(id+"F0.wireOp",EDGE,"E3.7.3"),sQuery(id+"F0.wireOp",EDGE,"E3.8.1"),sQuery(id+"F0.wireOp",EDGE,"E3.8.2"),sQuery(id+"F0.wireOp",EDGE,"E3.8.3"),sQuery(id+"F0.wireOp",EDGE,"E3.9.1"),sQuery(id+"F0.wireOp",EDGE,"E3.9.2"),sQuery(id+"F0.wireOp",EDGE,"E3.9.3"),sQuery(id+"F0.wireOp",EDGE,"E3.10.1"),sQuery(id+"F0.wireOp",EDGE,"E3.10.2"),sQuery(id+"F0.wireOp",EDGE,"E3.10.3"),sQuery(id+"F0.wireOp",EDGE,"E3.11.1"),sQuery(id+"F0.wireOp",EDGE,"E3.11.2"),sQuery(id+"F0.wireOp",EDGE,"E3.11.3"),sQuery(id+"F0.wireOp",EDGE,"E3.12.1"),sQuery(id+"F0.wireOp",EDGE,"E3.12.2"),sQuery(id+"F0.wireOp",EDGE,"E3.12.3")])],"isStart":false})],"blendedInto":[makeQuery(id+"F1.opExtrude","CAP_FACE",FACE,{"disambiguationData":[OSD([sQuery(id+"F0.wireOp",EDGE,"E0"),sQuery(id+"F0.wireOp",EDGE,"E1"),sQuery(id+"F0.wireOp",EDGE,"E2.bottom"),sQuery(id+"F0.wireOp",EDGE,"E2.left"),sQuery(id+"F0.wireOp",EDGE,"E2.right"),sQuery(id+"F0.wireOp",EDGE,"E3.1.1"),sQuery(id+"F0.wireOp",EDGE,"E3.1.2"),sQuery(id+"F0.wireOp",EDGE,"E3.1.3"),sQuery(id+"F0.wireOp",EDGE,"E3.2.1"),sQuery(id+"F0.wireOp",EDGE,"E3.2.2"),sQuery(id+"F0.wireOp",EDGE,"E3.2.3"),sQuery(id+"F0.wireOp",EDGE,"E3.3.1"),sQuery(id+"F0.wireOp",EDGE,"E3.3.2"),sQuery(id+"F0.wireOp",EDGE,"E3.3.3"),sQuery(id+"F0.wireOp",EDGE,"E3.4.1"),sQuery(id+"F0.wireOp",EDGE,"E3.4.2"),sQuery(id+"F0.wireOp",EDGE,"E3.4.3"),sQuery(id+"F0.wireOp",EDGE,"E3.5.1"),sQuery(id+"F0.wireOp",EDGE,"E3.5.2"),sQuery(id+"F0.wireOp",EDGE,"E3.5.3"),subQ1,subQ0,sQuery(id+"F0.wireOp",EDGE,"E3.6.3"),sQuery(id+"F0.wireOp",EDGE,"E3.7.1"),sQuery(id+"F0.wireOp",EDGE,"E3.7.2"),sQuery(id+"F0.wireOp",EDGE,"E3.7.3"),sQuery(id+"F0.wireOp",EDGE,"E3.8.1"),sQuery(id+"F0.wireOp",EDGE,"E3.8.2"),sQuery(id+"F0.wireOp",EDGE,"E3.8.3"),sQuery(id+"F0.wireOp",EDGE,"E3.9.1"),sQuery(id+"F0.wireOp",EDGE,"E3.9.2"),sQuery(id+"F0.wireOp",EDGE,"E3.9.3"),sQuery(id+"F0.wireOp",EDGE,"E3.10.1"),sQuery(id+"F0.wireOp",EDGE,"E3.10.2"),sQuery(id+"F0.wireOp",EDGE,"E3.10.3"),sQuery(id+"F0.wireOp",EDGE,"E3.11.1"),sQuery(id+"F0.wireOp",EDGE,"E3.11.2"),sQuery(id+"F0.wireOp",EDGE,"E3.11.3"),sQuery(id+"F0.wireOp",EDGE,"E3.12.1"),sQuery(id+"F0.wireOp",EDGE,"E3.12.2"),sQuery(id+"F0.wireOp",EDGE,"E3.12.3")])],"isStart":false})]}),makeQuery(id+"F1.opExtrude","CAP_EDGE",EDGE,{"disambiguationData":[OSD([subQ0])],"isStart":false})],"blendedInto":[]});}
            var Q39;
            {var subQ0=sQuery(id+"F0.wireOp",EDGE,"E3.6.2");var subQ1=sQuery(id+"F0.wireOp",EDGE,"E3.6.3");Q39=makeQuery(id+"F4.opChamfer","BLEND_EDGE",EDGE,{"blendedFrom":[makeQuery(id+"F3.opChamfer","BLEND_EDGE",EDGE,{"blendedFrom":[makeQuery(id+"F1.opExtrude","SWEPT_EDGE",EDGE,{"disambiguationData":[OSD([subQ0,subQ1])]}),makeQuery(id+"F1.opExtrude","CAP_FACE",FACE,{"disambiguationData":[OSD([sQuery(id+"F0.wireOp",EDGE,"E0"),sQuery(id+"F0.wireOp",EDGE,"E1"),sQuery(id+"F0.wireOp",EDGE,"E2.bottom"),sQuery(id+"F0.wireOp",EDGE,"E2.left"),sQuery(id+"F0.wireOp",EDGE,"E2.right"),sQuery(id+"F0.wireOp",EDGE,"E3.1.1"),sQuery(id+"F0.wireOp",EDGE,"E3.1.2"),sQuery(id+"F0.wireOp",EDGE,"E3.1.3"),sQuery(id+"F0.wireOp",EDGE,"E3.2.1"),sQuery(id+"F0.wireOp",EDGE,"E3.2.2"),sQuery(id+"F0.wireOp",EDGE,"E3.2.3"),sQuery(id+"F0.wireOp",EDGE,"E3.3.1"),sQuery(id+"F0.wireOp",EDGE,"E3.3.2"),sQuery(id+"F0.wireOp",EDGE,"E3.3.3"),sQuery(id+"F0.wireOp",EDGE,"E3.4.1"),sQuery(id+"F0.wireOp",EDGE,"E3.4.2"),sQuery(id+"F0.wireOp",EDGE,"E3.4.3"),sQuery(id+"F0.wireOp",EDGE,"E3.5.1"),sQuery(id+"F0.wireOp",EDGE,"E3.5.2"),sQuery(id+"F0.wireOp",EDGE,"E3.5.3"),sQuery(id+"F0.wireOp",EDGE,"E3.6.1"),subQ0,subQ1,sQuery(id+"F0.wireOp",EDGE,"E3.7.1"),sQuery(id+"F0.wireOp",EDGE,"E3.7.2"),sQuery(id+"F0.wireOp",EDGE,"E3.7.3"),sQuery(id+"F0.wireOp",EDGE,"E3.8.1"),sQuery(id+"F0.wireOp",EDGE,"E3.8.2"),sQuery(id+"F0.wireOp",EDGE,"E3.8.3"),sQuery(id+"F0.wireOp",EDGE,"E3.9.1"),sQuery(id+"F0.wireOp",EDGE,"E3.9.2"),sQuery(id+"F0.wireOp",EDGE,"E3.9.3"),sQuery(id+"F0.wireOp",EDGE,"E3.10.1"),sQuery(id+"F0.wireOp",EDGE,"E3.10.2"),sQuery(id+"F0.wireOp",EDGE,"E3.10.3"),sQuery(id+"F0.wireOp",EDGE,"E3.11.1"),sQuery(id+"F0.wireOp",EDGE,"E3.11.2"),sQuery(id+"F0.wireOp",EDGE,"E3.11.3"),sQuery(id+"F0.wireOp",EDGE,"E3.12.1"),sQuery(id+"F0.wireOp",EDGE,"E3.12.2"),sQuery(id+"F0.wireOp",EDGE,"E3.12.3")])],"isStart":false})],"blendedInto":[makeQuery(id+"F1.opExtrude","CAP_FACE",FACE,{"disambiguationData":[OSD([sQuery(id+"F0.wireOp",EDGE,"E0"),sQuery(id+"F0.wireOp",EDGE,"E1"),sQuery(id+"F0.wireOp",EDGE,"E2.bottom"),sQuery(id+"F0.wireOp",EDGE,"E2.left"),sQuery(id+"F0.wireOp",EDGE,"E2.right"),sQuery(id+"F0.wireOp",EDGE,"E3.1.1"),sQuery(id+"F0.wireOp",EDGE,"E3.1.2"),sQuery(id+"F0.wireOp",EDGE,"E3.1.3"),sQuery(id+"F0.wireOp",EDGE,"E3.2.1"),sQuery(id+"F0.wireOp",EDGE,"E3.2.2"),sQuery(id+"F0.wireOp",EDGE,"E3.2.3"),sQuery(id+"F0.wireOp",EDGE,"E3.3.1"),sQuery(id+"F0.wireOp",EDGE,"E3.3.2"),sQuery(id+"F0.wireOp",EDGE,"E3.3.3"),sQuery(id+"F0.wireOp",EDGE,"E3.4.1"),sQuery(id+"F0.wireOp",EDGE,"E3.4.2"),sQuery(id+"F0.wireOp",EDGE,"E3.4.3"),sQuery(id+"F0.wireOp",EDGE,"E3.5.1"),sQuery(id+"F0.wireOp",EDGE,"E3.5.2"),sQuery(id+"F0.wireOp",EDGE,"E3.5.3"),sQuery(id+"F0.wireOp",EDGE,"E3.6.1"),subQ0,subQ1,sQuery(id+"F0.wireOp",EDGE,"E3.7.1"),sQuery(id+"F0.wireOp",EDGE,"E3.7.2"),sQuery(id+"F0.wireOp",EDGE,"E3.7.3"),sQuery(id+"F0.wireOp",EDGE,"E3.8.1"),sQuery(id+"F0.wireOp",EDGE,"E3.8.2"),sQuery(id+"F0.wireOp",EDGE,"E3.8.3"),sQuery(id+"F0.wireOp",EDGE,"E3.9.1"),sQuery(id+"F0.wireOp",EDGE,"E3.9.2"),sQuery(id+"F0.wireOp",EDGE,"E3.9.3"),sQuery(id+"F0.wireOp",EDGE,"E3.10.1"),sQuery(id+"F0.wireOp",EDGE,"E3.10.2"),sQuery(id+"F0.wireOp",EDGE,"E3.10.3"),sQuery(id+"F0.wireOp",EDGE,"E3.11.1"),sQuery(id+"F0.wireOp",EDGE,"E3.11.2"),sQuery(id+"F0.wireOp",EDGE,"E3.11.3"),sQuery(id+"F0.wireOp",EDGE,"E3.12.1"),sQuery(id+"F0.wireOp",EDGE,"E3.12.2"),sQuery(id+"F0.wireOp",EDGE,"E3.12.3")])],"isStart":false})]}),makeQuery(id+"F1.opExtrude","CAP_EDGE",EDGE,{"disambiguationData":[OSD([subQ0])],"isStart":false})],"blendedInto":[]});}
            var Q40;
            {var subQ0=sQuery(id+"F0.wireOp",EDGE,"E3.7.2");Q40=makeQuery(id+"F3.opChamfer","BLEND_EDGE",EDGE,{"blendedFrom":[makeQuery(id+"F1.opExtrude","SWEPT_EDGE",EDGE,{"disambiguationData":[OSD([sQuery(id+"F0.wireOp",EDGE,"E3.7.1"),subQ0])]}),makeQuery(id+"F1.opExtrude","SWEPT_FACE",FACE,{"disambiguationData":[OSD([subQ0])]})],"blendedInto":[makeQuery(id+"F1.opExtrude","SWEPT_FACE",FACE,{"disambiguationData":[OSD([subQ0])]})]});}
            var Q41;
            {var subQ0=sQuery(id+"F0.wireOp",EDGE,"E3.7.2");Q41=makeQuery(id+"F3.opChamfer","BLEND_EDGE",EDGE,{"blendedFrom":[makeQuery(id+"F1.opExtrude","SWEPT_EDGE",EDGE,{"disambiguationData":[OSD([subQ0,sQuery(id+"F0.wireOp",EDGE,"E3.7.3")])]}),makeQuery(id+"F1.opExtrude","SWEPT_FACE",FACE,{"disambiguationData":[OSD([subQ0])]})],"blendedInto":[makeQuery(id+"F1.opExtrude","SWEPT_FACE",FACE,{"disambiguationData":[OSD([subQ0])]})]});}
            var Q42;
            {var subQ0=sQuery(id+"F0.wireOp",EDGE,"E3.7.2");var subQ1=sQuery(id+"F0.wireOp",EDGE,"E3.7.3");Q42=makeQuery(id+"F4.opChamfer","BLEND_EDGE",EDGE,{"blendedFrom":[makeQuery(id+"F3.opChamfer","BLEND_EDGE",EDGE,{"blendedFrom":[makeQuery(id+"F1.opExtrude","SWEPT_EDGE",EDGE,{"disambiguationData":[OSD([subQ0,subQ1])]}),makeQuery(id+"F1.opExtrude","CAP_FACE",FACE,{"disambiguationData":[OSD([sQuery(id+"F0.wireOp",EDGE,"E0"),sQuery(id+"F0.wireOp",EDGE,"E1"),sQuery(id+"F0.wireOp",EDGE,"E2.bottom"),sQuery(id+"F0.wireOp",EDGE,"E2.left"),sQuery(id+"F0.wireOp",EDGE,"E2.right"),sQuery(id+"F0.wireOp",EDGE,"E3.1.1"),sQuery(id+"F0.wireOp",EDGE,"E3.1.2"),sQuery(id+"F0.wireOp",EDGE,"E3.1.3"),sQuery(id+"F0.wireOp",EDGE,"E3.2.1"),sQuery(id+"F0.wireOp",EDGE,"E3.2.2"),sQuery(id+"F0.wireOp",EDGE,"E3.2.3"),sQuery(id+"F0.wireOp",EDGE,"E3.3.1"),sQuery(id+"F0.wireOp",EDGE,"E3.3.2"),sQuery(id+"F0.wireOp",EDGE,"E3.3.3"),sQuery(id+"F0.wireOp",EDGE,"E3.4.1"),sQuery(id+"F0.wireOp",EDGE,"E3.4.2"),sQuery(id+"F0.wireOp",EDGE,"E3.4.3"),sQuery(id+"F0.wireOp",EDGE,"E3.5.1"),sQuery(id+"F0.wireOp",EDGE,"E3.5.2"),sQuery(id+"F0.wireOp",EDGE,"E3.5.3"),sQuery(id+"F0.wireOp",EDGE,"E3.6.1"),sQuery(id+"F0.wireOp",EDGE,"E3.6.2"),sQuery(id+"F0.wireOp",EDGE,"E3.6.3"),sQuery(id+"F0.wireOp",EDGE,"E3.7.1"),subQ0,subQ1,sQuery(id+"F0.wireOp",EDGE,"E3.8.1"),sQuery(id+"F0.wireOp",EDGE,"E3.8.2"),sQuery(id+"F0.wireOp",EDGE,"E3.8.3"),sQuery(id+"F0.wireOp",EDGE,"E3.9.1"),sQuery(id+"F0.wireOp",EDGE,"E3.9.2"),sQuery(id+"F0.wireOp",EDGE,"E3.9.3"),sQuery(id+"F0.wireOp",EDGE,"E3.10.1"),sQuery(id+"F0.wireOp",EDGE,"E3.10.2"),sQuery(id+"F0.wireOp",EDGE,"E3.10.3"),sQuery(id+"F0.wireOp",EDGE,"E3.11.1"),sQuery(id+"F0.wireOp",EDGE,"E3.11.2"),sQuery(id+"F0.wireOp",EDGE,"E3.11.3"),sQuery(id+"F0.wireOp",EDGE,"E3.12.1"),sQuery(id+"F0.wireOp",EDGE,"E3.12.2"),sQuery(id+"F0.wireOp",EDGE,"E3.12.3")])],"isStart":false})],"blendedInto":[makeQuery(id+"F1.opExtrude","CAP_FACE",FACE,{"disambiguationData":[OSD([sQuery(id+"F0.wireOp",EDGE,"E0"),sQuery(id+"F0.wireOp",EDGE,"E1"),sQuery(id+"F0.wireOp",EDGE,"E2.bottom"),sQuery(id+"F0.wireOp",EDGE,"E2.left"),sQuery(id+"F0.wireOp",EDGE,"E2.right"),sQuery(id+"F0.wireOp",EDGE,"E3.1.1"),sQuery(id+"F0.wireOp",EDGE,"E3.1.2"),sQuery(id+"F0.wireOp",EDGE,"E3.1.3"),sQuery(id+"F0.wireOp",EDGE,"E3.2.1"),sQuery(id+"F0.wireOp",EDGE,"E3.2.2"),sQuery(id+"F0.wireOp",EDGE,"E3.2.3"),sQuery(id+"F0.wireOp",EDGE,"E3.3.1"),sQuery(id+"F0.wireOp",EDGE,"E3.3.2"),sQuery(id+"F0.wireOp",EDGE,"E3.3.3"),sQuery(id+"F0.wireOp",EDGE,"E3.4.1"),sQuery(id+"F0.wireOp",EDGE,"E3.4.2"),sQuery(id+"F0.wireOp",EDGE,"E3.4.3"),sQuery(id+"F0.wireOp",EDGE,"E3.5.1"),sQuery(id+"F0.wireOp",EDGE,"E3.5.2"),sQuery(id+"F0.wireOp",EDGE,"E3.5.3"),sQuery(id+"F0.wireOp",EDGE,"E3.6.1"),sQuery(id+"F0.wireOp",EDGE,"E3.6.2"),sQuery(id+"F0.wireOp",EDGE,"E3.6.3"),sQuery(id+"F0.wireOp",EDGE,"E3.7.1"),subQ0,subQ1,sQuery(id+"F0.wireOp",EDGE,"E3.8.1"),sQuery(id+"F0.wireOp",EDGE,"E3.8.2"),sQuery(id+"F0.wireOp",EDGE,"E3.8.3"),sQuery(id+"F0.wireOp",EDGE,"E3.9.1"),sQuery(id+"F0.wireOp",EDGE,"E3.9.2"),sQuery(id+"F0.wireOp",EDGE,"E3.9.3"),sQuery(id+"F0.wireOp",EDGE,"E3.10.1"),sQuery(id+"F0.wireOp",EDGE,"E3.10.2"),sQuery(id+"F0.wireOp",EDGE,"E3.10.3"),sQuery(id+"F0.wireOp",EDGE,"E3.11.1"),sQuery(id+"F0.wireOp",EDGE,"E3.11.2"),sQuery(id+"F0.wireOp",EDGE,"E3.11.3"),sQuery(id+"F0.wireOp",EDGE,"E3.12.1"),sQuery(id+"F0.wireOp",EDGE,"E3.12.2"),sQuery(id+"F0.wireOp",EDGE,"E3.12.3")])],"isStart":false})]}),makeQuery(id+"F1.opExtrude","CAP_EDGE",EDGE,{"disambiguationData":[OSD([subQ0])],"isStart":false})],"blendedInto":[]});}
            var Q43;
            {var subQ0=sQuery(id+"F0.wireOp",EDGE,"E3.7.2");var subQ1=sQuery(id+"F0.wireOp",EDGE,"E3.7.1");Q43=makeQuery(id+"F4.opChamfer","BLEND_EDGE",EDGE,{"blendedFrom":[makeQuery(id+"F3.opChamfer","BLEND_EDGE",EDGE,{"blendedFrom":[makeQuery(id+"F1.opExtrude","SWEPT_EDGE",EDGE,{"disambiguationData":[OSD([subQ1,subQ0])]}),makeQuery(id+"F1.opExtrude","CAP_FACE",FACE,{"disambiguationData":[OSD([sQuery(id+"F0.wireOp",EDGE,"E0"),sQuery(id+"F0.wireOp",EDGE,"E1"),sQuery(id+"F0.wireOp",EDGE,"E2.bottom"),sQuery(id+"F0.wireOp",EDGE,"E2.left"),sQuery(id+"F0.wireOp",EDGE,"E2.right"),sQuery(id+"F0.wireOp",EDGE,"E3.1.1"),sQuery(id+"F0.wireOp",EDGE,"E3.1.2"),sQuery(id+"F0.wireOp",EDGE,"E3.1.3"),sQuery(id+"F0.wireOp",EDGE,"E3.2.1"),sQuery(id+"F0.wireOp",EDGE,"E3.2.2"),sQuery(id+"F0.wireOp",EDGE,"E3.2.3"),sQuery(id+"F0.wireOp",EDGE,"E3.3.1"),sQuery(id+"F0.wireOp",EDGE,"E3.3.2"),sQuery(id+"F0.wireOp",EDGE,"E3.3.3"),sQuery(id+"F0.wireOp",EDGE,"E3.4.1"),sQuery(id+"F0.wireOp",EDGE,"E3.4.2"),sQuery(id+"F0.wireOp",EDGE,"E3.4.3"),sQuery(id+"F0.wireOp",EDGE,"E3.5.1"),sQuery(id+"F0.wireOp",EDGE,"E3.5.2"),sQuery(id+"F0.wireOp",EDGE,"E3.5.3"),sQuery(id+"F0.wireOp",EDGE,"E3.6.1"),sQuery(id+"F0.wireOp",EDGE,"E3.6.2"),sQuery(id+"F0.wireOp",EDGE,"E3.6.3"),subQ1,subQ0,sQuery(id+"F0.wireOp",EDGE,"E3.7.3"),sQuery(id+"F0.wireOp",EDGE,"E3.8.1"),sQuery(id+"F0.wireOp",EDGE,"E3.8.2"),sQuery(id+"F0.wireOp",EDGE,"E3.8.3"),sQuery(id+"F0.wireOp",EDGE,"E3.9.1"),sQuery(id+"F0.wireOp",EDGE,"E3.9.2"),sQuery(id+"F0.wireOp",EDGE,"E3.9.3"),sQuery(id+"F0.wireOp",EDGE,"E3.10.1"),sQuery(id+"F0.wireOp",EDGE,"E3.10.2"),sQuery(id+"F0.wireOp",EDGE,"E3.10.3"),sQuery(id+"F0.wireOp",EDGE,"E3.11.1"),sQuery(id+"F0.wireOp",EDGE,"E3.11.2"),sQuery(id+"F0.wireOp",EDGE,"E3.11.3"),sQuery(id+"F0.wireOp",EDGE,"E3.12.1"),sQuery(id+"F0.wireOp",EDGE,"E3.12.2"),sQuery(id+"F0.wireOp",EDGE,"E3.12.3")])],"isStart":false})],"blendedInto":[makeQuery(id+"F1.opExtrude","CAP_FACE",FACE,{"disambiguationData":[OSD([sQuery(id+"F0.wireOp",EDGE,"E0"),sQuery(id+"F0.wireOp",EDGE,"E1"),sQuery(id+"F0.wireOp",EDGE,"E2.bottom"),sQuery(id+"F0.wireOp",EDGE,"E2.left"),sQuery(id+"F0.wireOp",EDGE,"E2.right"),sQuery(id+"F0.wireOp",EDGE,"E3.1.1"),sQuery(id+"F0.wireOp",EDGE,"E3.1.2"),sQuery(id+"F0.wireOp",EDGE,"E3.1.3"),sQuery(id+"F0.wireOp",EDGE,"E3.2.1"),sQuery(id+"F0.wireOp",EDGE,"E3.2.2"),sQuery(id+"F0.wireOp",EDGE,"E3.2.3"),sQuery(id+"F0.wireOp",EDGE,"E3.3.1"),sQuery(id+"F0.wireOp",EDGE,"E3.3.2"),sQuery(id+"F0.wireOp",EDGE,"E3.3.3"),sQuery(id+"F0.wireOp",EDGE,"E3.4.1"),sQuery(id+"F0.wireOp",EDGE,"E3.4.2"),sQuery(id+"F0.wireOp",EDGE,"E3.4.3"),sQuery(id+"F0.wireOp",EDGE,"E3.5.1"),sQuery(id+"F0.wireOp",EDGE,"E3.5.2"),sQuery(id+"F0.wireOp",EDGE,"E3.5.3"),sQuery(id+"F0.wireOp",EDGE,"E3.6.1"),sQuery(id+"F0.wireOp",EDGE,"E3.6.2"),sQuery(id+"F0.wireOp",EDGE,"E3.6.3"),subQ1,subQ0,sQuery(id+"F0.wireOp",EDGE,"E3.7.3"),sQuery(id+"F0.wireOp",EDGE,"E3.8.1"),sQuery(id+"F0.wireOp",EDGE,"E3.8.2"),sQuery(id+"F0.wireOp",EDGE,"E3.8.3"),sQuery(id+"F0.wireOp",EDGE,"E3.9.1"),sQuery(id+"F0.wireOp",EDGE,"E3.9.2"),sQuery(id+"F0.wireOp",EDGE,"E3.9.3"),sQuery(id+"F0.wireOp",EDGE,"E3.10.1"),sQuery(id+"F0.wireOp",EDGE,"E3.10.2"),sQuery(id+"F0.wireOp",EDGE,"E3.10.3"),sQuery(id+"F0.wireOp",EDGE,"E3.11.1"),sQuery(id+"F0.wireOp",EDGE,"E3.11.2"),sQuery(id+"F0.wireOp",EDGE,"E3.11.3"),sQuery(id+"F0.wireOp",EDGE,"E3.12.1"),sQuery(id+"F0.wireOp",EDGE,"E3.12.2"),sQuery(id+"F0.wireOp",EDGE,"E3.12.3")])],"isStart":false})]}),makeQuery(id+"F1.opExtrude","CAP_EDGE",EDGE,{"disambiguationData":[OSD([subQ0])],"isStart":false})],"blendedInto":[]});}
            var Q44;
            {var subQ0=sQuery(id+"F0.wireOp",EDGE,"E3.8.2");Q44=makeQuery(id+"F3.opChamfer","BLEND_EDGE",EDGE,{"blendedFrom":[makeQuery(id+"F1.opExtrude","SWEPT_EDGE",EDGE,{"disambiguationData":[OSD([sQuery(id+"F0.wireOp",EDGE,"E3.8.1"),subQ0])]}),makeQuery(id+"F1.opExtrude","SWEPT_FACE",FACE,{"disambiguationData":[OSD([subQ0])]})],"blendedInto":[makeQuery(id+"F1.opExtrude","SWEPT_FACE",FACE,{"disambiguationData":[OSD([subQ0])]})]});}
            var Q45;
            {var subQ0=sQuery(id+"F0.wireOp",EDGE,"E3.8.2");Q45=makeQuery(id+"F3.opChamfer","BLEND_EDGE",EDGE,{"blendedFrom":[makeQuery(id+"F1.opExtrude","SWEPT_EDGE",EDGE,{"disambiguationData":[OSD([subQ0,sQuery(id+"F0.wireOp",EDGE,"E3.8.3")])]}),makeQuery(id+"F1.opExtrude","SWEPT_FACE",FACE,{"disambiguationData":[OSD([subQ0])]})],"blendedInto":[makeQuery(id+"F1.opExtrude","SWEPT_FACE",FACE,{"disambiguationData":[OSD([subQ0])]})]});}
            var Q46;
            {var subQ0=sQuery(id+"F0.wireOp",EDGE,"E3.8.2");var subQ1=sQuery(id+"F0.wireOp",EDGE,"E3.8.3");Q46=makeQuery(id+"F4.opChamfer","BLEND_EDGE",EDGE,{"blendedFrom":[makeQuery(id+"F3.opChamfer","BLEND_EDGE",EDGE,{"blendedFrom":[makeQuery(id+"F1.opExtrude","SWEPT_EDGE",EDGE,{"disambiguationData":[OSD([subQ0,subQ1])]}),makeQuery(id+"F1.opExtrude","CAP_FACE",FACE,{"disambiguationData":[OSD([sQuery(id+"F0.wireOp",EDGE,"E0"),sQuery(id+"F0.wireOp",EDGE,"E1"),sQuery(id+"F0.wireOp",EDGE,"E2.bottom"),sQuery(id+"F0.wireOp",EDGE,"E2.left"),sQuery(id+"F0.wireOp",EDGE,"E2.right"),sQuery(id+"F0.wireOp",EDGE,"E3.1.1"),sQuery(id+"F0.wireOp",EDGE,"E3.1.2"),sQuery(id+"F0.wireOp",EDGE,"E3.1.3"),sQuery(id+"F0.wireOp",EDGE,"E3.2.1"),sQuery(id+"F0.wireOp",EDGE,"E3.2.2"),sQuery(id+"F0.wireOp",EDGE,"E3.2.3"),sQuery(id+"F0.wireOp",EDGE,"E3.3.1"),sQuery(id+"F0.wireOp",EDGE,"E3.3.2"),sQuery(id+"F0.wireOp",EDGE,"E3.3.3"),sQuery(id+"F0.wireOp",EDGE,"E3.4.1"),sQuery(id+"F0.wireOp",EDGE,"E3.4.2"),sQuery(id+"F0.wireOp",EDGE,"E3.4.3"),sQuery(id+"F0.wireOp",EDGE,"E3.5.1"),sQuery(id+"F0.wireOp",EDGE,"E3.5.2"),sQuery(id+"F0.wireOp",EDGE,"E3.5.3"),sQuery(id+"F0.wireOp",EDGE,"E3.6.1"),sQuery(id+"F0.wireOp",EDGE,"E3.6.2"),sQuery(id+"F0.wireOp",EDGE,"E3.6.3"),sQuery(id+"F0.wireOp",EDGE,"E3.7.1"),sQuery(id+"F0.wireOp",EDGE,"E3.7.2"),sQuery(id+"F0.wireOp",EDGE,"E3.7.3"),sQuery(id+"F0.wireOp",EDGE,"E3.8.1"),subQ0,subQ1,sQuery(id+"F0.wireOp",EDGE,"E3.9.1"),sQuery(id+"F0.wireOp",EDGE,"E3.9.2"),sQuery(id+"F0.wireOp",EDGE,"E3.9.3"),sQuery(id+"F0.wireOp",EDGE,"E3.10.1"),sQuery(id+"F0.wireOp",EDGE,"E3.10.2"),sQuery(id+"F0.wireOp",EDGE,"E3.10.3"),sQuery(id+"F0.wireOp",EDGE,"E3.11.1"),sQuery(id+"F0.wireOp",EDGE,"E3.11.2"),sQuery(id+"F0.wireOp",EDGE,"E3.11.3"),sQuery(id+"F0.wireOp",EDGE,"E3.12.1"),sQuery(id+"F0.wireOp",EDGE,"E3.12.2"),sQuery(id+"F0.wireOp",EDGE,"E3.12.3")])],"isStart":false})],"blendedInto":[makeQuery(id+"F1.opExtrude","CAP_FACE",FACE,{"disambiguationData":[OSD([sQuery(id+"F0.wireOp",EDGE,"E0"),sQuery(id+"F0.wireOp",EDGE,"E1"),sQuery(id+"F0.wireOp",EDGE,"E2.bottom"),sQuery(id+"F0.wireOp",EDGE,"E2.left"),sQuery(id+"F0.wireOp",EDGE,"E2.right"),sQuery(id+"F0.wireOp",EDGE,"E3.1.1"),sQuery(id+"F0.wireOp",EDGE,"E3.1.2"),sQuery(id+"F0.wireOp",EDGE,"E3.1.3"),sQuery(id+"F0.wireOp",EDGE,"E3.2.1"),sQuery(id+"F0.wireOp",EDGE,"E3.2.2"),sQuery(id+"F0.wireOp",EDGE,"E3.2.3"),sQuery(id+"F0.wireOp",EDGE,"E3.3.1"),sQuery(id+"F0.wireOp",EDGE,"E3.3.2"),sQuery(id+"F0.wireOp",EDGE,"E3.3.3"),sQuery(id+"F0.wireOp",EDGE,"E3.4.1"),sQuery(id+"F0.wireOp",EDGE,"E3.4.2"),sQuery(id+"F0.wireOp",EDGE,"E3.4.3"),sQuery(id+"F0.wireOp",EDGE,"E3.5.1"),sQuery(id+"F0.wireOp",EDGE,"E3.5.2"),sQuery(id+"F0.wireOp",EDGE,"E3.5.3"),sQuery(id+"F0.wireOp",EDGE,"E3.6.1"),sQuery(id+"F0.wireOp",EDGE,"E3.6.2"),sQuery(id+"F0.wireOp",EDGE,"E3.6.3"),sQuery(id+"F0.wireOp",EDGE,"E3.7.1"),sQuery(id+"F0.wireOp",EDGE,"E3.7.2"),sQuery(id+"F0.wireOp",EDGE,"E3.7.3"),sQuery(id+"F0.wireOp",EDGE,"E3.8.1"),subQ0,subQ1,sQuery(id+"F0.wireOp",EDGE,"E3.9.1"),sQuery(id+"F0.wireOp",EDGE,"E3.9.2"),sQuery(id+"F0.wireOp",EDGE,"E3.9.3"),sQuery(id+"F0.wireOp",EDGE,"E3.10.1"),sQuery(id+"F0.wireOp",EDGE,"E3.10.2"),sQuery(id+"F0.wireOp",EDGE,"E3.10.3"),sQuery(id+"F0.wireOp",EDGE,"E3.11.1"),sQuery(id+"F0.wireOp",EDGE,"E3.11.2"),sQuery(id+"F0.wireOp",EDGE,"E3.11.3"),sQuery(id+"F0.wireOp",EDGE,"E3.12.1"),sQuery(id+"F0.wireOp",EDGE,"E3.12.2"),sQuery(id+"F0.wireOp",EDGE,"E3.12.3")])],"isStart":false})]}),makeQuery(id+"F1.opExtrude","CAP_EDGE",EDGE,{"disambiguationData":[OSD([subQ0])],"isStart":false})],"blendedInto":[]});}
            var Q47;
            {var subQ0=sQuery(id+"F0.wireOp",EDGE,"E3.8.2");var subQ1=sQuery(id+"F0.wireOp",EDGE,"E3.8.1");Q47=makeQuery(id+"F4.opChamfer","BLEND_EDGE",EDGE,{"blendedFrom":[makeQuery(id+"F3.opChamfer","BLEND_EDGE",EDGE,{"blendedFrom":[makeQuery(id+"F1.opExtrude","SWEPT_EDGE",EDGE,{"disambiguationData":[OSD([subQ1,subQ0])]}),makeQuery(id+"F1.opExtrude","CAP_FACE",FACE,{"disambiguationData":[OSD([sQuery(id+"F0.wireOp",EDGE,"E0"),sQuery(id+"F0.wireOp",EDGE,"E1"),sQuery(id+"F0.wireOp",EDGE,"E2.bottom"),sQuery(id+"F0.wireOp",EDGE,"E2.left"),sQuery(id+"F0.wireOp",EDGE,"E2.right"),sQuery(id+"F0.wireOp",EDGE,"E3.1.1"),sQuery(id+"F0.wireOp",EDGE,"E3.1.2"),sQuery(id+"F0.wireOp",EDGE,"E3.1.3"),sQuery(id+"F0.wireOp",EDGE,"E3.2.1"),sQuery(id+"F0.wireOp",EDGE,"E3.2.2"),sQuery(id+"F0.wireOp",EDGE,"E3.2.3"),sQuery(id+"F0.wireOp",EDGE,"E3.3.1"),sQuery(id+"F0.wireOp",EDGE,"E3.3.2"),sQuery(id+"F0.wireOp",EDGE,"E3.3.3"),sQuery(id+"F0.wireOp",EDGE,"E3.4.1"),sQuery(id+"F0.wireOp",EDGE,"E3.4.2"),sQuery(id+"F0.wireOp",EDGE,"E3.4.3"),sQuery(id+"F0.wireOp",EDGE,"E3.5.1"),sQuery(id+"F0.wireOp",EDGE,"E3.5.2"),sQuery(id+"F0.wireOp",EDGE,"E3.5.3"),sQuery(id+"F0.wireOp",EDGE,"E3.6.1"),sQuery(id+"F0.wireOp",EDGE,"E3.6.2"),sQuery(id+"F0.wireOp",EDGE,"E3.6.3"),sQuery(id+"F0.wireOp",EDGE,"E3.7.1"),sQuery(id+"F0.wireOp",EDGE,"E3.7.2"),sQuery(id+"F0.wireOp",EDGE,"E3.7.3"),subQ1,subQ0,sQuery(id+"F0.wireOp",EDGE,"E3.8.3"),sQuery(id+"F0.wireOp",EDGE,"E3.9.1"),sQuery(id+"F0.wireOp",EDGE,"E3.9.2"),sQuery(id+"F0.wireOp",EDGE,"E3.9.3"),sQuery(id+"F0.wireOp",EDGE,"E3.10.1"),sQuery(id+"F0.wireOp",EDGE,"E3.10.2"),sQuery(id+"F0.wireOp",EDGE,"E3.10.3"),sQuery(id+"F0.wireOp",EDGE,"E3.11.1"),sQuery(id+"F0.wireOp",EDGE,"E3.11.2"),sQuery(id+"F0.wireOp",EDGE,"E3.11.3"),sQuery(id+"F0.wireOp",EDGE,"E3.12.1"),sQuery(id+"F0.wireOp",EDGE,"E3.12.2"),sQuery(id+"F0.wireOp",EDGE,"E3.12.3")])],"isStart":false})],"blendedInto":[makeQuery(id+"F1.opExtrude","CAP_FACE",FACE,{"disambiguationData":[OSD([sQuery(id+"F0.wireOp",EDGE,"E0"),sQuery(id+"F0.wireOp",EDGE,"E1"),sQuery(id+"F0.wireOp",EDGE,"E2.bottom"),sQuery(id+"F0.wireOp",EDGE,"E2.left"),sQuery(id+"F0.wireOp",EDGE,"E2.right"),sQuery(id+"F0.wireOp",EDGE,"E3.1.1"),sQuery(id+"F0.wireOp",EDGE,"E3.1.2"),sQuery(id+"F0.wireOp",EDGE,"E3.1.3"),sQuery(id+"F0.wireOp",EDGE,"E3.2.1"),sQuery(id+"F0.wireOp",EDGE,"E3.2.2"),sQuery(id+"F0.wireOp",EDGE,"E3.2.3"),sQuery(id+"F0.wireOp",EDGE,"E3.3.1"),sQuery(id+"F0.wireOp",EDGE,"E3.3.2"),sQuery(id+"F0.wireOp",EDGE,"E3.3.3"),sQuery(id+"F0.wireOp",EDGE,"E3.4.1"),sQuery(id+"F0.wireOp",EDGE,"E3.4.2"),sQuery(id+"F0.wireOp",EDGE,"E3.4.3"),sQuery(id+"F0.wireOp",EDGE,"E3.5.1"),sQuery(id+"F0.wireOp",EDGE,"E3.5.2"),sQuery(id+"F0.wireOp",EDGE,"E3.5.3"),sQuery(id+"F0.wireOp",EDGE,"E3.6.1"),sQuery(id+"F0.wireOp",EDGE,"E3.6.2"),sQuery(id+"F0.wireOp",EDGE,"E3.6.3"),sQuery(id+"F0.wireOp",EDGE,"E3.7.1"),sQuery(id+"F0.wireOp",EDGE,"E3.7.2"),sQuery(id+"F0.wireOp",EDGE,"E3.7.3"),subQ1,subQ0,sQuery(id+"F0.wireOp",EDGE,"E3.8.3"),sQuery(id+"F0.wireOp",EDGE,"E3.9.1"),sQuery(id+"F0.wireOp",EDGE,"E3.9.2"),sQuery(id+"F0.wireOp",EDGE,"E3.9.3"),sQuery(id+"F0.wireOp",EDGE,"E3.10.1"),sQuery(id+"F0.wireOp",EDGE,"E3.10.2"),sQuery(id+"F0.wireOp",EDGE,"E3.10.3"),sQuery(id+"F0.wireOp",EDGE,"E3.11.1"),sQuery(id+"F0.wireOp",EDGE,"E3.11.2"),sQuery(id+"F0.wireOp",EDGE,"E3.11.3"),sQuery(id+"F0.wireOp",EDGE,"E3.12.1"),sQuery(id+"F0.wireOp",EDGE,"E3.12.2"),sQuery(id+"F0.wireOp",EDGE,"E3.12.3")])],"isStart":false})]}),makeQuery(id+"F1.opExtrude","CAP_EDGE",EDGE,{"disambiguationData":[OSD([subQ0])],"isStart":false})],"blendedInto":[]});}
            var Q48;
            {var subQ0=sQuery(id+"F0.wireOp",EDGE,"E3.9.2");var subQ1=sQuery(id+"F0.wireOp",EDGE,"E3.9.3");Q48=makeQuery(id+"F4.opChamfer","BLEND_EDGE",EDGE,{"blendedFrom":[makeQuery(id+"F3.opChamfer","BLEND_EDGE",EDGE,{"blendedFrom":[makeQuery(id+"F1.opExtrude","SWEPT_EDGE",EDGE,{"disambiguationData":[OSD([subQ0,subQ1])]}),makeQuery(id+"F1.opExtrude","CAP_FACE",FACE,{"disambiguationData":[OSD([sQuery(id+"F0.wireOp",EDGE,"E0"),sQuery(id+"F0.wireOp",EDGE,"E1"),sQuery(id+"F0.wireOp",EDGE,"E2.bottom"),sQuery(id+"F0.wireOp",EDGE,"E2.left"),sQuery(id+"F0.wireOp",EDGE,"E2.right"),sQuery(id+"F0.wireOp",EDGE,"E3.1.1"),sQuery(id+"F0.wireOp",EDGE,"E3.1.2"),sQuery(id+"F0.wireOp",EDGE,"E3.1.3"),sQuery(id+"F0.wireOp",EDGE,"E3.2.1"),sQuery(id+"F0.wireOp",EDGE,"E3.2.2"),sQuery(id+"F0.wireOp",EDGE,"E3.2.3"),sQuery(id+"F0.wireOp",EDGE,"E3.3.1"),sQuery(id+"F0.wireOp",EDGE,"E3.3.2"),sQuery(id+"F0.wireOp",EDGE,"E3.3.3"),sQuery(id+"F0.wireOp",EDGE,"E3.4.1"),sQuery(id+"F0.wireOp",EDGE,"E3.4.2"),sQuery(id+"F0.wireOp",EDGE,"E3.4.3"),sQuery(id+"F0.wireOp",EDGE,"E3.5.1"),sQuery(id+"F0.wireOp",EDGE,"E3.5.2"),sQuery(id+"F0.wireOp",EDGE,"E3.5.3"),sQuery(id+"F0.wireOp",EDGE,"E3.6.1"),sQuery(id+"F0.wireOp",EDGE,"E3.6.2"),sQuery(id+"F0.wireOp",EDGE,"E3.6.3"),sQuery(id+"F0.wireOp",EDGE,"E3.7.1"),sQuery(id+"F0.wireOp",EDGE,"E3.7.2"),sQuery(id+"F0.wireOp",EDGE,"E3.7.3"),sQuery(id+"F0.wireOp",EDGE,"E3.8.1"),sQuery(id+"F0.wireOp",EDGE,"E3.8.2"),sQuery(id+"F0.wireOp",EDGE,"E3.8.3"),sQuery(id+"F0.wireOp",EDGE,"E3.9.1"),subQ0,subQ1,sQuery(id+"F0.wireOp",EDGE,"E3.10.1"),sQuery(id+"F0.wireOp",EDGE,"E3.10.2"),sQuery(id+"F0.wireOp",EDGE,"E3.10.3"),sQuery(id+"F0.wireOp",EDGE,"E3.11.1"),sQuery(id+"F0.wireOp",EDGE,"E3.11.2"),sQuery(id+"F0.wireOp",EDGE,"E3.11.3"),sQuery(id+"F0.wireOp",EDGE,"E3.12.1"),sQuery(id+"F0.wireOp",EDGE,"E3.12.2"),sQuery(id+"F0.wireOp",EDGE,"E3.12.3")])],"isStart":false})],"blendedInto":[makeQuery(id+"F1.opExtrude","CAP_FACE",FACE,{"disambiguationData":[OSD([sQuery(id+"F0.wireOp",EDGE,"E0"),sQuery(id+"F0.wireOp",EDGE,"E1"),sQuery(id+"F0.wireOp",EDGE,"E2.bottom"),sQuery(id+"F0.wireOp",EDGE,"E2.left"),sQuery(id+"F0.wireOp",EDGE,"E2.right"),sQuery(id+"F0.wireOp",EDGE,"E3.1.1"),sQuery(id+"F0.wireOp",EDGE,"E3.1.2"),sQuery(id+"F0.wireOp",EDGE,"E3.1.3"),sQuery(id+"F0.wireOp",EDGE,"E3.2.1"),sQuery(id+"F0.wireOp",EDGE,"E3.2.2"),sQuery(id+"F0.wireOp",EDGE,"E3.2.3"),sQuery(id+"F0.wireOp",EDGE,"E3.3.1"),sQuery(id+"F0.wireOp",EDGE,"E3.3.2"),sQuery(id+"F0.wireOp",EDGE,"E3.3.3"),sQuery(id+"F0.wireOp",EDGE,"E3.4.1"),sQuery(id+"F0.wireOp",EDGE,"E3.4.2"),sQuery(id+"F0.wireOp",EDGE,"E3.4.3"),sQuery(id+"F0.wireOp",EDGE,"E3.5.1"),sQuery(id+"F0.wireOp",EDGE,"E3.5.2"),sQuery(id+"F0.wireOp",EDGE,"E3.5.3"),sQuery(id+"F0.wireOp",EDGE,"E3.6.1"),sQuery(id+"F0.wireOp",EDGE,"E3.6.2"),sQuery(id+"F0.wireOp",EDGE,"E3.6.3"),sQuery(id+"F0.wireOp",EDGE,"E3.7.1"),sQuery(id+"F0.wireOp",EDGE,"E3.7.2"),sQuery(id+"F0.wireOp",EDGE,"E3.7.3"),sQuery(id+"F0.wireOp",EDGE,"E3.8.1"),sQuery(id+"F0.wireOp",EDGE,"E3.8.2"),sQuery(id+"F0.wireOp",EDGE,"E3.8.3"),sQuery(id+"F0.wireOp",EDGE,"E3.9.1"),subQ0,subQ1,sQuery(id+"F0.wireOp",EDGE,"E3.10.1"),sQuery(id+"F0.wireOp",EDGE,"E3.10.2"),sQuery(id+"F0.wireOp",EDGE,"E3.10.3"),sQuery(id+"F0.wireOp",EDGE,"E3.11.1"),sQuery(id+"F0.wireOp",EDGE,"E3.11.2"),sQuery(id+"F0.wireOp",EDGE,"E3.11.3"),sQuery(id+"F0.wireOp",EDGE,"E3.12.1"),sQuery(id+"F0.wireOp",EDGE,"E3.12.2"),sQuery(id+"F0.wireOp",EDGE,"E3.12.3")])],"isStart":false})]}),makeQuery(id+"F1.opExtrude","CAP_EDGE",EDGE,{"disambiguationData":[OSD([subQ0])],"isStart":false})],"blendedInto":[]});}
            var Q49;
            {var subQ0=sQuery(id+"F0.wireOp",EDGE,"E3.9.2");var subQ1=sQuery(id+"F0.wireOp",EDGE,"E3.9.1");Q49=makeQuery(id+"F4.opChamfer","BLEND_EDGE",EDGE,{"blendedFrom":[makeQuery(id+"F3.opChamfer","BLEND_EDGE",EDGE,{"blendedFrom":[makeQuery(id+"F1.opExtrude","SWEPT_EDGE",EDGE,{"disambiguationData":[OSD([subQ1,subQ0])]}),makeQuery(id+"F1.opExtrude","CAP_FACE",FACE,{"disambiguationData":[OSD([sQuery(id+"F0.wireOp",EDGE,"E0"),sQuery(id+"F0.wireOp",EDGE,"E1"),sQuery(id+"F0.wireOp",EDGE,"E2.bottom"),sQuery(id+"F0.wireOp",EDGE,"E2.left"),sQuery(id+"F0.wireOp",EDGE,"E2.right"),sQuery(id+"F0.wireOp",EDGE,"E3.1.1"),sQuery(id+"F0.wireOp",EDGE,"E3.1.2"),sQuery(id+"F0.wireOp",EDGE,"E3.1.3"),sQuery(id+"F0.wireOp",EDGE,"E3.2.1"),sQuery(id+"F0.wireOp",EDGE,"E3.2.2"),sQuery(id+"F0.wireOp",EDGE,"E3.2.3"),sQuery(id+"F0.wireOp",EDGE,"E3.3.1"),sQuery(id+"F0.wireOp",EDGE,"E3.3.2"),sQuery(id+"F0.wireOp",EDGE,"E3.3.3"),sQuery(id+"F0.wireOp",EDGE,"E3.4.1"),sQuery(id+"F0.wireOp",EDGE,"E3.4.2"),sQuery(id+"F0.wireOp",EDGE,"E3.4.3"),sQuery(id+"F0.wireOp",EDGE,"E3.5.1"),sQuery(id+"F0.wireOp",EDGE,"E3.5.2"),sQuery(id+"F0.wireOp",EDGE,"E3.5.3"),sQuery(id+"F0.wireOp",EDGE,"E3.6.1"),sQuery(id+"F0.wireOp",EDGE,"E3.6.2"),sQuery(id+"F0.wireOp",EDGE,"E3.6.3"),sQuery(id+"F0.wireOp",EDGE,"E3.7.1"),sQuery(id+"F0.wireOp",EDGE,"E3.7.2"),sQuery(id+"F0.wireOp",EDGE,"E3.7.3"),sQuery(id+"F0.wireOp",EDGE,"E3.8.1"),sQuery(id+"F0.wireOp",EDGE,"E3.8.2"),sQuery(id+"F0.wireOp",EDGE,"E3.8.3"),subQ1,subQ0,sQuery(id+"F0.wireOp",EDGE,"E3.9.3"),sQuery(id+"F0.wireOp",EDGE,"E3.10.1"),sQuery(id+"F0.wireOp",EDGE,"E3.10.2"),sQuery(id+"F0.wireOp",EDGE,"E3.10.3"),sQuery(id+"F0.wireOp",EDGE,"E3.11.1"),sQuery(id+"F0.wireOp",EDGE,"E3.11.2"),sQuery(id+"F0.wireOp",EDGE,"E3.11.3"),sQuery(id+"F0.wireOp",EDGE,"E3.12.1"),sQuery(id+"F0.wireOp",EDGE,"E3.12.2"),sQuery(id+"F0.wireOp",EDGE,"E3.12.3")])],"isStart":false})],"blendedInto":[makeQuery(id+"F1.opExtrude","CAP_FACE",FACE,{"disambiguationData":[OSD([sQuery(id+"F0.wireOp",EDGE,"E0"),sQuery(id+"F0.wireOp",EDGE,"E1"),sQuery(id+"F0.wireOp",EDGE,"E2.bottom"),sQuery(id+"F0.wireOp",EDGE,"E2.left"),sQuery(id+"F0.wireOp",EDGE,"E2.right"),sQuery(id+"F0.wireOp",EDGE,"E3.1.1"),sQuery(id+"F0.wireOp",EDGE,"E3.1.2"),sQuery(id+"F0.wireOp",EDGE,"E3.1.3"),sQuery(id+"F0.wireOp",EDGE,"E3.2.1"),sQuery(id+"F0.wireOp",EDGE,"E3.2.2"),sQuery(id+"F0.wireOp",EDGE,"E3.2.3"),sQuery(id+"F0.wireOp",EDGE,"E3.3.1"),sQuery(id+"F0.wireOp",EDGE,"E3.3.2"),sQuery(id+"F0.wireOp",EDGE,"E3.3.3"),sQuery(id+"F0.wireOp",EDGE,"E3.4.1"),sQuery(id+"F0.wireOp",EDGE,"E3.4.2"),sQuery(id+"F0.wireOp",EDGE,"E3.4.3"),sQuery(id+"F0.wireOp",EDGE,"E3.5.1"),sQuery(id+"F0.wireOp",EDGE,"E3.5.2"),sQuery(id+"F0.wireOp",EDGE,"E3.5.3"),sQuery(id+"F0.wireOp",EDGE,"E3.6.1"),sQuery(id+"F0.wireOp",EDGE,"E3.6.2"),sQuery(id+"F0.wireOp",EDGE,"E3.6.3"),sQuery(id+"F0.wireOp",EDGE,"E3.7.1"),sQuery(id+"F0.wireOp",EDGE,"E3.7.2"),sQuery(id+"F0.wireOp",EDGE,"E3.7.3"),sQuery(id+"F0.wireOp",EDGE,"E3.8.1"),sQuery(id+"F0.wireOp",EDGE,"E3.8.2"),sQuery(id+"F0.wireOp",EDGE,"E3.8.3"),subQ1,subQ0,sQuery(id+"F0.wireOp",EDGE,"E3.9.3"),sQuery(id+"F0.wireOp",EDGE,"E3.10.1"),sQuery(id+"F0.wireOp",EDGE,"E3.10.2"),sQuery(id+"F0.wireOp",EDGE,"E3.10.3"),sQuery(id+"F0.wireOp",EDGE,"E3.11.1"),sQuery(id+"F0.wireOp",EDGE,"E3.11.2"),sQuery(id+"F0.wireOp",EDGE,"E3.11.3"),sQuery(id+"F0.wireOp",EDGE,"E3.12.1"),sQuery(id+"F0.wireOp",EDGE,"E3.12.2"),sQuery(id+"F0.wireOp",EDGE,"E3.12.3")])],"isStart":false})]}),makeQuery(id+"F1.opExtrude","CAP_EDGE",EDGE,{"disambiguationData":[OSD([subQ0])],"isStart":false})],"blendedInto":[]});}
            var Q50;
            {var subQ0=sQuery(id+"F0.wireOp",EDGE,"E3.9.2");Q50=makeQuery(id+"F3.opChamfer","BLEND_EDGE",EDGE,{"blendedFrom":[makeQuery(id+"F1.opExtrude","SWEPT_EDGE",EDGE,{"disambiguationData":[OSD([subQ0,sQuery(id+"F0.wireOp",EDGE,"E3.9.3")])]}),makeQuery(id+"F1.opExtrude","SWEPT_FACE",FACE,{"disambiguationData":[OSD([subQ0])]})],"blendedInto":[makeQuery(id+"F1.opExtrude","SWEPT_FACE",FACE,{"disambiguationData":[OSD([subQ0])]})]});}
            var Q51;
            {var subQ0=sQuery(id+"F0.wireOp",EDGE,"E3.9.2");Q51=makeQuery(id+"F3.opChamfer","BLEND_EDGE",EDGE,{"blendedFrom":[makeQuery(id+"F1.opExtrude","SWEPT_EDGE",EDGE,{"disambiguationData":[OSD([sQuery(id+"F0.wireOp",EDGE,"E3.9.1"),subQ0])]}),makeQuery(id+"F1.opExtrude","SWEPT_FACE",FACE,{"disambiguationData":[OSD([subQ0])]})],"blendedInto":[makeQuery(id+"F1.opExtrude","SWEPT_FACE",FACE,{"disambiguationData":[OSD([subQ0])]})]});}
            var Q52;
            {var subQ0=sQuery(id+"F0.wireOp",EDGE,"E3.11.2");var subQ1=sQuery(id+"F0.wireOp",EDGE,"E3.11.3");Q52=makeQuery(id+"F4.opChamfer","BLEND_EDGE",EDGE,{"blendedFrom":[makeQuery(id+"F3.opChamfer","BLEND_EDGE",EDGE,{"blendedFrom":[makeQuery(id+"F1.opExtrude","SWEPT_EDGE",EDGE,{"disambiguationData":[OSD([subQ0,subQ1])]}),makeQuery(id+"F1.opExtrude","CAP_FACE",FACE,{"disambiguationData":[OSD([sQuery(id+"F0.wireOp",EDGE,"E0"),sQuery(id+"F0.wireOp",EDGE,"E1"),sQuery(id+"F0.wireOp",EDGE,"E2.bottom"),sQuery(id+"F0.wireOp",EDGE,"E2.left"),sQuery(id+"F0.wireOp",EDGE,"E2.right"),sQuery(id+"F0.wireOp",EDGE,"E3.1.1"),sQuery(id+"F0.wireOp",EDGE,"E3.1.2"),sQuery(id+"F0.wireOp",EDGE,"E3.1.3"),sQuery(id+"F0.wireOp",EDGE,"E3.2.1"),sQuery(id+"F0.wireOp",EDGE,"E3.2.2"),sQuery(id+"F0.wireOp",EDGE,"E3.2.3"),sQuery(id+"F0.wireOp",EDGE,"E3.3.1"),sQuery(id+"F0.wireOp",EDGE,"E3.3.2"),sQuery(id+"F0.wireOp",EDGE,"E3.3.3"),sQuery(id+"F0.wireOp",EDGE,"E3.4.1"),sQuery(id+"F0.wireOp",EDGE,"E3.4.2"),sQuery(id+"F0.wireOp",EDGE,"E3.4.3"),sQuery(id+"F0.wireOp",EDGE,"E3.5.1"),sQuery(id+"F0.wireOp",EDGE,"E3.5.2"),sQuery(id+"F0.wireOp",EDGE,"E3.5.3"),sQuery(id+"F0.wireOp",EDGE,"E3.6.1"),sQuery(id+"F0.wireOp",EDGE,"E3.6.2"),sQuery(id+"F0.wireOp",EDGE,"E3.6.3"),sQuery(id+"F0.wireOp",EDGE,"E3.7.1"),sQuery(id+"F0.wireOp",EDGE,"E3.7.2"),sQuery(id+"F0.wireOp",EDGE,"E3.7.3"),sQuery(id+"F0.wireOp",EDGE,"E3.8.1"),sQuery(id+"F0.wireOp",EDGE,"E3.8.2"),sQuery(id+"F0.wireOp",EDGE,"E3.8.3"),sQuery(id+"F0.wireOp",EDGE,"E3.9.1"),sQuery(id+"F0.wireOp",EDGE,"E3.9.2"),sQuery(id+"F0.wireOp",EDGE,"E3.9.3"),sQuery(id+"F0.wireOp",EDGE,"E3.10.1"),sQuery(id+"F0.wireOp",EDGE,"E3.10.2"),sQuery(id+"F0.wireOp",EDGE,"E3.10.3"),sQuery(id+"F0.wireOp",EDGE,"E3.11.1"),subQ0,subQ1,sQuery(id+"F0.wireOp",EDGE,"E3.12.1"),sQuery(id+"F0.wireOp",EDGE,"E3.12.2"),sQuery(id+"F0.wireOp",EDGE,"E3.12.3")])],"isStart":true})],"blendedInto":[makeQuery(id+"F1.opExtrude","CAP_FACE",FACE,{"disambiguationData":[OSD([sQuery(id+"F0.wireOp",EDGE,"E0"),sQuery(id+"F0.wireOp",EDGE,"E1"),sQuery(id+"F0.wireOp",EDGE,"E2.bottom"),sQuery(id+"F0.wireOp",EDGE,"E2.left"),sQuery(id+"F0.wireOp",EDGE,"E2.right"),sQuery(id+"F0.wireOp",EDGE,"E3.1.1"),sQuery(id+"F0.wireOp",EDGE,"E3.1.2"),sQuery(id+"F0.wireOp",EDGE,"E3.1.3"),sQuery(id+"F0.wireOp",EDGE,"E3.2.1"),sQuery(id+"F0.wireOp",EDGE,"E3.2.2"),sQuery(id+"F0.wireOp",EDGE,"E3.2.3"),sQuery(id+"F0.wireOp",EDGE,"E3.3.1"),sQuery(id+"F0.wireOp",EDGE,"E3.3.2"),sQuery(id+"F0.wireOp",EDGE,"E3.3.3"),sQuery(id+"F0.wireOp",EDGE,"E3.4.1"),sQuery(id+"F0.wireOp",EDGE,"E3.4.2"),sQuery(id+"F0.wireOp",EDGE,"E3.4.3"),sQuery(id+"F0.wireOp",EDGE,"E3.5.1"),sQuery(id+"F0.wireOp",EDGE,"E3.5.2"),sQuery(id+"F0.wireOp",EDGE,"E3.5.3"),sQuery(id+"F0.wireOp",EDGE,"E3.6.1"),sQuery(id+"F0.wireOp",EDGE,"E3.6.2"),sQuery(id+"F0.wireOp",EDGE,"E3.6.3"),sQuery(id+"F0.wireOp",EDGE,"E3.7.1"),sQuery(id+"F0.wireOp",EDGE,"E3.7.2"),sQuery(id+"F0.wireOp",EDGE,"E3.7.3"),sQuery(id+"F0.wireOp",EDGE,"E3.8.1"),sQuery(id+"F0.wireOp",EDGE,"E3.8.2"),sQuery(id+"F0.wireOp",EDGE,"E3.8.3"),sQuery(id+"F0.wireOp",EDGE,"E3.9.1"),sQuery(id+"F0.wireOp",EDGE,"E3.9.2"),sQuery(id+"F0.wireOp",EDGE,"E3.9.3"),sQuery(id+"F0.wireOp",EDGE,"E3.10.1"),sQuery(id+"F0.wireOp",EDGE,"E3.10.2"),sQuery(id+"F0.wireOp",EDGE,"E3.10.3"),sQuery(id+"F0.wireOp",EDGE,"E3.11.1"),subQ0,subQ1,sQuery(id+"F0.wireOp",EDGE,"E3.12.1"),sQuery(id+"F0.wireOp",EDGE,"E3.12.2"),sQuery(id+"F0.wireOp",EDGE,"E3.12.3")])],"isStart":true})]}),makeQuery(id+"F1.opExtrude","CAP_EDGE",EDGE,{"disambiguationData":[OSD([subQ0])],"isStart":true})],"blendedInto":[]});}
            var Q53;
            {var subQ0=sQuery(id+"F0.wireOp",EDGE,"E3.11.2");var subQ1=sQuery(id+"F0.wireOp",EDGE,"E3.11.1");Q53=makeQuery(id+"F4.opChamfer","BLEND_EDGE",EDGE,{"blendedFrom":[makeQuery(id+"F3.opChamfer","BLEND_EDGE",EDGE,{"blendedFrom":[makeQuery(id+"F1.opExtrude","SWEPT_EDGE",EDGE,{"disambiguationData":[OSD([subQ1,subQ0])]}),makeQuery(id+"F1.opExtrude","CAP_FACE",FACE,{"disambiguationData":[OSD([sQuery(id+"F0.wireOp",EDGE,"E0"),sQuery(id+"F0.wireOp",EDGE,"E1"),sQuery(id+"F0.wireOp",EDGE,"E2.bottom"),sQuery(id+"F0.wireOp",EDGE,"E2.left"),sQuery(id+"F0.wireOp",EDGE,"E2.right"),sQuery(id+"F0.wireOp",EDGE,"E3.1.1"),sQuery(id+"F0.wireOp",EDGE,"E3.1.2"),sQuery(id+"F0.wireOp",EDGE,"E3.1.3"),sQuery(id+"F0.wireOp",EDGE,"E3.2.1"),sQuery(id+"F0.wireOp",EDGE,"E3.2.2"),sQuery(id+"F0.wireOp",EDGE,"E3.2.3"),sQuery(id+"F0.wireOp",EDGE,"E3.3.1"),sQuery(id+"F0.wireOp",EDGE,"E3.3.2"),sQuery(id+"F0.wireOp",EDGE,"E3.3.3"),sQuery(id+"F0.wireOp",EDGE,"E3.4.1"),sQuery(id+"F0.wireOp",EDGE,"E3.4.2"),sQuery(id+"F0.wireOp",EDGE,"E3.4.3"),sQuery(id+"F0.wireOp",EDGE,"E3.5.1"),sQuery(id+"F0.wireOp",EDGE,"E3.5.2"),sQuery(id+"F0.wireOp",EDGE,"E3.5.3"),sQuery(id+"F0.wireOp",EDGE,"E3.6.1"),sQuery(id+"F0.wireOp",EDGE,"E3.6.2"),sQuery(id+"F0.wireOp",EDGE,"E3.6.3"),sQuery(id+"F0.wireOp",EDGE,"E3.7.1"),sQuery(id+"F0.wireOp",EDGE,"E3.7.2"),sQuery(id+"F0.wireOp",EDGE,"E3.7.3"),sQuery(id+"F0.wireOp",EDGE,"E3.8.1"),sQuery(id+"F0.wireOp",EDGE,"E3.8.2"),sQuery(id+"F0.wireOp",EDGE,"E3.8.3"),sQuery(id+"F0.wireOp",EDGE,"E3.9.1"),sQuery(id+"F0.wireOp",EDGE,"E3.9.2"),sQuery(id+"F0.wireOp",EDGE,"E3.9.3"),sQuery(id+"F0.wireOp",EDGE,"E3.10.1"),sQuery(id+"F0.wireOp",EDGE,"E3.10.2"),sQuery(id+"F0.wireOp",EDGE,"E3.10.3"),subQ1,subQ0,sQuery(id+"F0.wireOp",EDGE,"E3.11.3"),sQuery(id+"F0.wireOp",EDGE,"E3.12.1"),sQuery(id+"F0.wireOp",EDGE,"E3.12.2"),sQuery(id+"F0.wireOp",EDGE,"E3.12.3")])],"isStart":true})],"blendedInto":[makeQuery(id+"F1.opExtrude","CAP_FACE",FACE,{"disambiguationData":[OSD([sQuery(id+"F0.wireOp",EDGE,"E0"),sQuery(id+"F0.wireOp",EDGE,"E1"),sQuery(id+"F0.wireOp",EDGE,"E2.bottom"),sQuery(id+"F0.wireOp",EDGE,"E2.left"),sQuery(id+"F0.wireOp",EDGE,"E2.right"),sQuery(id+"F0.wireOp",EDGE,"E3.1.1"),sQuery(id+"F0.wireOp",EDGE,"E3.1.2"),sQuery(id+"F0.wireOp",EDGE,"E3.1.3"),sQuery(id+"F0.wireOp",EDGE,"E3.2.1"),sQuery(id+"F0.wireOp",EDGE,"E3.2.2"),sQuery(id+"F0.wireOp",EDGE,"E3.2.3"),sQuery(id+"F0.wireOp",EDGE,"E3.3.1"),sQuery(id+"F0.wireOp",EDGE,"E3.3.2"),sQuery(id+"F0.wireOp",EDGE,"E3.3.3"),sQuery(id+"F0.wireOp",EDGE,"E3.4.1"),sQuery(id+"F0.wireOp",EDGE,"E3.4.2"),sQuery(id+"F0.wireOp",EDGE,"E3.4.3"),sQuery(id+"F0.wireOp",EDGE,"E3.5.1"),sQuery(id+"F0.wireOp",EDGE,"E3.5.2"),sQuery(id+"F0.wireOp",EDGE,"E3.5.3"),sQuery(id+"F0.wireOp",EDGE,"E3.6.1"),sQuery(id+"F0.wireOp",EDGE,"E3.6.2"),sQuery(id+"F0.wireOp",EDGE,"E3.6.3"),sQuery(id+"F0.wireOp",EDGE,"E3.7.1"),sQuery(id+"F0.wireOp",EDGE,"E3.7.2"),sQuery(id+"F0.wireOp",EDGE,"E3.7.3"),sQuery(id+"F0.wireOp",EDGE,"E3.8.1"),sQuery(id+"F0.wireOp",EDGE,"E3.8.2"),sQuery(id+"F0.wireOp",EDGE,"E3.8.3"),sQuery(id+"F0.wireOp",EDGE,"E3.9.1"),sQuery(id+"F0.wireOp",EDGE,"E3.9.2"),sQuery(id+"F0.wireOp",EDGE,"E3.9.3"),sQuery(id+"F0.wireOp",EDGE,"E3.10.1"),sQuery(id+"F0.wireOp",EDGE,"E3.10.2"),sQuery(id+"F0.wireOp",EDGE,"E3.10.3"),subQ1,subQ0,sQuery(id+"F0.wireOp",EDGE,"E3.11.3"),sQuery(id+"F0.wireOp",EDGE,"E3.12.1"),sQuery(id+"F0.wireOp",EDGE,"E3.12.2"),sQuery(id+"F0.wireOp",EDGE,"E3.12.3")])],"isStart":true})]}),makeQuery(id+"F1.opExtrude","CAP_EDGE",EDGE,{"disambiguationData":[OSD([subQ0])],"isStart":true})],"blendedInto":[]});}
            var Q54;
            {var subQ0=sQuery(id+"F0.wireOp",EDGE,"E3.10.2");var subQ1=sQuery(id+"F0.wireOp",EDGE,"E3.10.3");Q54=makeQuery(id+"F4.opChamfer","BLEND_EDGE",EDGE,{"blendedFrom":[makeQuery(id+"F3.opChamfer","BLEND_EDGE",EDGE,{"blendedFrom":[makeQuery(id+"F1.opExtrude","SWEPT_EDGE",EDGE,{"disambiguationData":[OSD([subQ0,subQ1])]}),makeQuery(id+"F1.opExtrude","CAP_FACE",FACE,{"disambiguationData":[OSD([sQuery(id+"F0.wireOp",EDGE,"E0"),sQuery(id+"F0.wireOp",EDGE,"E1"),sQuery(id+"F0.wireOp",EDGE,"E2.bottom"),sQuery(id+"F0.wireOp",EDGE,"E2.left"),sQuery(id+"F0.wireOp",EDGE,"E2.right"),sQuery(id+"F0.wireOp",EDGE,"E3.1.1"),sQuery(id+"F0.wireOp",EDGE,"E3.1.2"),sQuery(id+"F0.wireOp",EDGE,"E3.1.3"),sQuery(id+"F0.wireOp",EDGE,"E3.2.1"),sQuery(id+"F0.wireOp",EDGE,"E3.2.2"),sQuery(id+"F0.wireOp",EDGE,"E3.2.3"),sQuery(id+"F0.wireOp",EDGE,"E3.3.1"),sQuery(id+"F0.wireOp",EDGE,"E3.3.2"),sQuery(id+"F0.wireOp",EDGE,"E3.3.3"),sQuery(id+"F0.wireOp",EDGE,"E3.4.1"),sQuery(id+"F0.wireOp",EDGE,"E3.4.2"),sQuery(id+"F0.wireOp",EDGE,"E3.4.3"),sQuery(id+"F0.wireOp",EDGE,"E3.5.1"),sQuery(id+"F0.wireOp",EDGE,"E3.5.2"),sQuery(id+"F0.wireOp",EDGE,"E3.5.3"),sQuery(id+"F0.wireOp",EDGE,"E3.6.1"),sQuery(id+"F0.wireOp",EDGE,"E3.6.2"),sQuery(id+"F0.wireOp",EDGE,"E3.6.3"),sQuery(id+"F0.wireOp",EDGE,"E3.7.1"),sQuery(id+"F0.wireOp",EDGE,"E3.7.2"),sQuery(id+"F0.wireOp",EDGE,"E3.7.3"),sQuery(id+"F0.wireOp",EDGE,"E3.8.1"),sQuery(id+"F0.wireOp",EDGE,"E3.8.2"),sQuery(id+"F0.wireOp",EDGE,"E3.8.3"),sQuery(id+"F0.wireOp",EDGE,"E3.9.1"),sQuery(id+"F0.wireOp",EDGE,"E3.9.2"),sQuery(id+"F0.wireOp",EDGE,"E3.9.3"),sQuery(id+"F0.wireOp",EDGE,"E3.10.1"),subQ0,subQ1,sQuery(id+"F0.wireOp",EDGE,"E3.11.1"),sQuery(id+"F0.wireOp",EDGE,"E3.11.2"),sQuery(id+"F0.wireOp",EDGE,"E3.11.3"),sQuery(id+"F0.wireOp",EDGE,"E3.12.1"),sQuery(id+"F0.wireOp",EDGE,"E3.12.2"),sQuery(id+"F0.wireOp",EDGE,"E3.12.3")])],"isStart":true})],"blendedInto":[makeQuery(id+"F1.opExtrude","CAP_FACE",FACE,{"disambiguationData":[OSD([sQuery(id+"F0.wireOp",EDGE,"E0"),sQuery(id+"F0.wireOp",EDGE,"E1"),sQuery(id+"F0.wireOp",EDGE,"E2.bottom"),sQuery(id+"F0.wireOp",EDGE,"E2.left"),sQuery(id+"F0.wireOp",EDGE,"E2.right"),sQuery(id+"F0.wireOp",EDGE,"E3.1.1"),sQuery(id+"F0.wireOp",EDGE,"E3.1.2"),sQuery(id+"F0.wireOp",EDGE,"E3.1.3"),sQuery(id+"F0.wireOp",EDGE,"E3.2.1"),sQuery(id+"F0.wireOp",EDGE,"E3.2.2"),sQuery(id+"F0.wireOp",EDGE,"E3.2.3"),sQuery(id+"F0.wireOp",EDGE,"E3.3.1"),sQuery(id+"F0.wireOp",EDGE,"E3.3.2"),sQuery(id+"F0.wireOp",EDGE,"E3.3.3"),sQuery(id+"F0.wireOp",EDGE,"E3.4.1"),sQuery(id+"F0.wireOp",EDGE,"E3.4.2"),sQuery(id+"F0.wireOp",EDGE,"E3.4.3"),sQuery(id+"F0.wireOp",EDGE,"E3.5.1"),sQuery(id+"F0.wireOp",EDGE,"E3.5.2"),sQuery(id+"F0.wireOp",EDGE,"E3.5.3"),sQuery(id+"F0.wireOp",EDGE,"E3.6.1"),sQuery(id+"F0.wireOp",EDGE,"E3.6.2"),sQuery(id+"F0.wireOp",EDGE,"E3.6.3"),sQuery(id+"F0.wireOp",EDGE,"E3.7.1"),sQuery(id+"F0.wireOp",EDGE,"E3.7.2"),sQuery(id+"F0.wireOp",EDGE,"E3.7.3"),sQuery(id+"F0.wireOp",EDGE,"E3.8.1"),sQuery(id+"F0.wireOp",EDGE,"E3.8.2"),sQuery(id+"F0.wireOp",EDGE,"E3.8.3"),sQuery(id+"F0.wireOp",EDGE,"E3.9.1"),sQuery(id+"F0.wireOp",EDGE,"E3.9.2"),sQuery(id+"F0.wireOp",EDGE,"E3.9.3"),sQuery(id+"F0.wireOp",EDGE,"E3.10.1"),subQ0,subQ1,sQuery(id+"F0.wireOp",EDGE,"E3.11.1"),sQuery(id+"F0.wireOp",EDGE,"E3.11.2"),sQuery(id+"F0.wireOp",EDGE,"E3.11.3"),sQuery(id+"F0.wireOp",EDGE,"E3.12.1"),sQuery(id+"F0.wireOp",EDGE,"E3.12.2"),sQuery(id+"F0.wireOp",EDGE,"E3.12.3")])],"isStart":true})]}),makeQuery(id+"F1.opExtrude","CAP_EDGE",EDGE,{"disambiguationData":[OSD([subQ0])],"isStart":true})],"blendedInto":[]});}
            var Q55;
            {var subQ0=sQuery(id+"F0.wireOp",EDGE,"E3.10.2");var subQ1=sQuery(id+"F0.wireOp",EDGE,"E3.10.1");Q55=makeQuery(id+"F4.opChamfer","BLEND_EDGE",EDGE,{"blendedFrom":[makeQuery(id+"F3.opChamfer","BLEND_EDGE",EDGE,{"blendedFrom":[makeQuery(id+"F1.opExtrude","SWEPT_EDGE",EDGE,{"disambiguationData":[OSD([subQ1,subQ0])]}),makeQuery(id+"F1.opExtrude","CAP_FACE",FACE,{"disambiguationData":[OSD([sQuery(id+"F0.wireOp",EDGE,"E0"),sQuery(id+"F0.wireOp",EDGE,"E1"),sQuery(id+"F0.wireOp",EDGE,"E2.bottom"),sQuery(id+"F0.wireOp",EDGE,"E2.left"),sQuery(id+"F0.wireOp",EDGE,"E2.right"),sQuery(id+"F0.wireOp",EDGE,"E3.1.1"),sQuery(id+"F0.wireOp",EDGE,"E3.1.2"),sQuery(id+"F0.wireOp",EDGE,"E3.1.3"),sQuery(id+"F0.wireOp",EDGE,"E3.2.1"),sQuery(id+"F0.wireOp",EDGE,"E3.2.2"),sQuery(id+"F0.wireOp",EDGE,"E3.2.3"),sQuery(id+"F0.wireOp",EDGE,"E3.3.1"),sQuery(id+"F0.wireOp",EDGE,"E3.3.2"),sQuery(id+"F0.wireOp",EDGE,"E3.3.3"),sQuery(id+"F0.wireOp",EDGE,"E3.4.1"),sQuery(id+"F0.wireOp",EDGE,"E3.4.2"),sQuery(id+"F0.wireOp",EDGE,"E3.4.3"),sQuery(id+"F0.wireOp",EDGE,"E3.5.1"),sQuery(id+"F0.wireOp",EDGE,"E3.5.2"),sQuery(id+"F0.wireOp",EDGE,"E3.5.3"),sQuery(id+"F0.wireOp",EDGE,"E3.6.1"),sQuery(id+"F0.wireOp",EDGE,"E3.6.2"),sQuery(id+"F0.wireOp",EDGE,"E3.6.3"),sQuery(id+"F0.wireOp",EDGE,"E3.7.1"),sQuery(id+"F0.wireOp",EDGE,"E3.7.2"),sQuery(id+"F0.wireOp",EDGE,"E3.7.3"),sQuery(id+"F0.wireOp",EDGE,"E3.8.1"),sQuery(id+"F0.wireOp",EDGE,"E3.8.2"),sQuery(id+"F0.wireOp",EDGE,"E3.8.3"),sQuery(id+"F0.wireOp",EDGE,"E3.9.1"),sQuery(id+"F0.wireOp",EDGE,"E3.9.2"),sQuery(id+"F0.wireOp",EDGE,"E3.9.3"),subQ1,subQ0,sQuery(id+"F0.wireOp",EDGE,"E3.10.3"),sQuery(id+"F0.wireOp",EDGE,"E3.11.1"),sQuery(id+"F0.wireOp",EDGE,"E3.11.2"),sQuery(id+"F0.wireOp",EDGE,"E3.11.3"),sQuery(id+"F0.wireOp",EDGE,"E3.12.1"),sQuery(id+"F0.wireOp",EDGE,"E3.12.2"),sQuery(id+"F0.wireOp",EDGE,"E3.12.3")])],"isStart":true})],"blendedInto":[makeQuery(id+"F1.opExtrude","CAP_FACE",FACE,{"disambiguationData":[OSD([sQuery(id+"F0.wireOp",EDGE,"E0"),sQuery(id+"F0.wireOp",EDGE,"E1"),sQuery(id+"F0.wireOp",EDGE,"E2.bottom"),sQuery(id+"F0.wireOp",EDGE,"E2.left"),sQuery(id+"F0.wireOp",EDGE,"E2.right"),sQuery(id+"F0.wireOp",EDGE,"E3.1.1"),sQuery(id+"F0.wireOp",EDGE,"E3.1.2"),sQuery(id+"F0.wireOp",EDGE,"E3.1.3"),sQuery(id+"F0.wireOp",EDGE,"E3.2.1"),sQuery(id+"F0.wireOp",EDGE,"E3.2.2"),sQuery(id+"F0.wireOp",EDGE,"E3.2.3"),sQuery(id+"F0.wireOp",EDGE,"E3.3.1"),sQuery(id+"F0.wireOp",EDGE,"E3.3.2"),sQuery(id+"F0.wireOp",EDGE,"E3.3.3"),sQuery(id+"F0.wireOp",EDGE,"E3.4.1"),sQuery(id+"F0.wireOp",EDGE,"E3.4.2"),sQuery(id+"F0.wireOp",EDGE,"E3.4.3"),sQuery(id+"F0.wireOp",EDGE,"E3.5.1"),sQuery(id+"F0.wireOp",EDGE,"E3.5.2"),sQuery(id+"F0.wireOp",EDGE,"E3.5.3"),sQuery(id+"F0.wireOp",EDGE,"E3.6.1"),sQuery(id+"F0.wireOp",EDGE,"E3.6.2"),sQuery(id+"F0.wireOp",EDGE,"E3.6.3"),sQuery(id+"F0.wireOp",EDGE,"E3.7.1"),sQuery(id+"F0.wireOp",EDGE,"E3.7.2"),sQuery(id+"F0.wireOp",EDGE,"E3.7.3"),sQuery(id+"F0.wireOp",EDGE,"E3.8.1"),sQuery(id+"F0.wireOp",EDGE,"E3.8.2"),sQuery(id+"F0.wireOp",EDGE,"E3.8.3"),sQuery(id+"F0.wireOp",EDGE,"E3.9.1"),sQuery(id+"F0.wireOp",EDGE,"E3.9.2"),sQuery(id+"F0.wireOp",EDGE,"E3.9.3"),subQ1,subQ0,sQuery(id+"F0.wireOp",EDGE,"E3.10.3"),sQuery(id+"F0.wireOp",EDGE,"E3.11.1"),sQuery(id+"F0.wireOp",EDGE,"E3.11.2"),sQuery(id+"F0.wireOp",EDGE,"E3.11.3"),sQuery(id+"F0.wireOp",EDGE,"E3.12.1"),sQuery(id+"F0.wireOp",EDGE,"E3.12.2"),sQuery(id+"F0.wireOp",EDGE,"E3.12.3")])],"isStart":true})]}),makeQuery(id+"F1.opExtrude","CAP_EDGE",EDGE,{"disambiguationData":[OSD([subQ0])],"isStart":true})],"blendedInto":[]});}
            var Q56;
            {var subQ0=sQuery(id+"F0.wireOp",EDGE,"E3.12.2");var subQ1=sQuery(id+"F0.wireOp",EDGE,"E3.12.3");Q56=makeQuery(id+"F4.opChamfer","BLEND_EDGE",EDGE,{"blendedFrom":[makeQuery(id+"F3.opChamfer","BLEND_EDGE",EDGE,{"blendedFrom":[makeQuery(id+"F1.opExtrude","SWEPT_EDGE",EDGE,{"disambiguationData":[OSD([subQ0,subQ1])]}),makeQuery(id+"F1.opExtrude","CAP_FACE",FACE,{"disambiguationData":[OSD([sQuery(id+"F0.wireOp",EDGE,"E0"),sQuery(id+"F0.wireOp",EDGE,"E1"),sQuery(id+"F0.wireOp",EDGE,"E2.bottom"),sQuery(id+"F0.wireOp",EDGE,"E2.left"),sQuery(id+"F0.wireOp",EDGE,"E2.right"),sQuery(id+"F0.wireOp",EDGE,"E3.1.1"),sQuery(id+"F0.wireOp",EDGE,"E3.1.2"),sQuery(id+"F0.wireOp",EDGE,"E3.1.3"),sQuery(id+"F0.wireOp",EDGE,"E3.2.1"),sQuery(id+"F0.wireOp",EDGE,"E3.2.2"),sQuery(id+"F0.wireOp",EDGE,"E3.2.3"),sQuery(id+"F0.wireOp",EDGE,"E3.3.1"),sQuery(id+"F0.wireOp",EDGE,"E3.3.2"),sQuery(id+"F0.wireOp",EDGE,"E3.3.3"),sQuery(id+"F0.wireOp",EDGE,"E3.4.1"),sQuery(id+"F0.wireOp",EDGE,"E3.4.2"),sQuery(id+"F0.wireOp",EDGE,"E3.4.3"),sQuery(id+"F0.wireOp",EDGE,"E3.5.1"),sQuery(id+"F0.wireOp",EDGE,"E3.5.2"),sQuery(id+"F0.wireOp",EDGE,"E3.5.3"),sQuery(id+"F0.wireOp",EDGE,"E3.6.1"),sQuery(id+"F0.wireOp",EDGE,"E3.6.2"),sQuery(id+"F0.wireOp",EDGE,"E3.6.3"),sQuery(id+"F0.wireOp",EDGE,"E3.7.1"),sQuery(id+"F0.wireOp",EDGE,"E3.7.2"),sQuery(id+"F0.wireOp",EDGE,"E3.7.3"),sQuery(id+"F0.wireOp",EDGE,"E3.8.1"),sQuery(id+"F0.wireOp",EDGE,"E3.8.2"),sQuery(id+"F0.wireOp",EDGE,"E3.8.3"),sQuery(id+"F0.wireOp",EDGE,"E3.9.1"),sQuery(id+"F0.wireOp",EDGE,"E3.9.2"),sQuery(id+"F0.wireOp",EDGE,"E3.9.3"),sQuery(id+"F0.wireOp",EDGE,"E3.10.1"),sQuery(id+"F0.wireOp",EDGE,"E3.10.2"),sQuery(id+"F0.wireOp",EDGE,"E3.10.3"),sQuery(id+"F0.wireOp",EDGE,"E3.11.1"),sQuery(id+"F0.wireOp",EDGE,"E3.11.2"),sQuery(id+"F0.wireOp",EDGE,"E3.11.3"),sQuery(id+"F0.wireOp",EDGE,"E3.12.1"),subQ0,subQ1])],"isStart":true})],"blendedInto":[makeQuery(id+"F1.opExtrude","CAP_FACE",FACE,{"disambiguationData":[OSD([sQuery(id+"F0.wireOp",EDGE,"E0"),sQuery(id+"F0.wireOp",EDGE,"E1"),sQuery(id+"F0.wireOp",EDGE,"E2.bottom"),sQuery(id+"F0.wireOp",EDGE,"E2.left"),sQuery(id+"F0.wireOp",EDGE,"E2.right"),sQuery(id+"F0.wireOp",EDGE,"E3.1.1"),sQuery(id+"F0.wireOp",EDGE,"E3.1.2"),sQuery(id+"F0.wireOp",EDGE,"E3.1.3"),sQuery(id+"F0.wireOp",EDGE,"E3.2.1"),sQuery(id+"F0.wireOp",EDGE,"E3.2.2"),sQuery(id+"F0.wireOp",EDGE,"E3.2.3"),sQuery(id+"F0.wireOp",EDGE,"E3.3.1"),sQuery(id+"F0.wireOp",EDGE,"E3.3.2"),sQuery(id+"F0.wireOp",EDGE,"E3.3.3"),sQuery(id+"F0.wireOp",EDGE,"E3.4.1"),sQuery(id+"F0.wireOp",EDGE,"E3.4.2"),sQuery(id+"F0.wireOp",EDGE,"E3.4.3"),sQuery(id+"F0.wireOp",EDGE,"E3.5.1"),sQuery(id+"F0.wireOp",EDGE,"E3.5.2"),sQuery(id+"F0.wireOp",EDGE,"E3.5.3"),sQuery(id+"F0.wireOp",EDGE,"E3.6.1"),sQuery(id+"F0.wireOp",EDGE,"E3.6.2"),sQuery(id+"F0.wireOp",EDGE,"E3.6.3"),sQuery(id+"F0.wireOp",EDGE,"E3.7.1"),sQuery(id+"F0.wireOp",EDGE,"E3.7.2"),sQuery(id+"F0.wireOp",EDGE,"E3.7.3"),sQuery(id+"F0.wireOp",EDGE,"E3.8.1"),sQuery(id+"F0.wireOp",EDGE,"E3.8.2"),sQuery(id+"F0.wireOp",EDGE,"E3.8.3"),sQuery(id+"F0.wireOp",EDGE,"E3.9.1"),sQuery(id+"F0.wireOp",EDGE,"E3.9.2"),sQuery(id+"F0.wireOp",EDGE,"E3.9.3"),sQuery(id+"F0.wireOp",EDGE,"E3.10.1"),sQuery(id+"F0.wireOp",EDGE,"E3.10.2"),sQuery(id+"F0.wireOp",EDGE,"E3.10.3"),sQuery(id+"F0.wireOp",EDGE,"E3.11.1"),sQuery(id+"F0.wireOp",EDGE,"E3.11.2"),sQuery(id+"F0.wireOp",EDGE,"E3.11.3"),sQuery(id+"F0.wireOp",EDGE,"E3.12.1"),subQ0,subQ1])],"isStart":true})]}),makeQuery(id+"F1.opExtrude","CAP_EDGE",EDGE,{"disambiguationData":[OSD([subQ0])],"isStart":true})],"blendedInto":[]});}
            var Q57;
            {var subQ0=sQuery(id+"F0.wireOp",EDGE,"E3.12.2");var subQ1=sQuery(id+"F0.wireOp",EDGE,"E3.12.1");Q57=makeQuery(id+"F4.opChamfer","BLEND_EDGE",EDGE,{"blendedFrom":[makeQuery(id+"F3.opChamfer","BLEND_EDGE",EDGE,{"blendedFrom":[makeQuery(id+"F1.opExtrude","SWEPT_EDGE",EDGE,{"disambiguationData":[OSD([subQ1,subQ0])]}),makeQuery(id+"F1.opExtrude","CAP_FACE",FACE,{"disambiguationData":[OSD([sQuery(id+"F0.wireOp",EDGE,"E0"),sQuery(id+"F0.wireOp",EDGE,"E1"),sQuery(id+"F0.wireOp",EDGE,"E2.bottom"),sQuery(id+"F0.wireOp",EDGE,"E2.left"),sQuery(id+"F0.wireOp",EDGE,"E2.right"),sQuery(id+"F0.wireOp",EDGE,"E3.1.1"),sQuery(id+"F0.wireOp",EDGE,"E3.1.2"),sQuery(id+"F0.wireOp",EDGE,"E3.1.3"),sQuery(id+"F0.wireOp",EDGE,"E3.2.1"),sQuery(id+"F0.wireOp",EDGE,"E3.2.2"),sQuery(id+"F0.wireOp",EDGE,"E3.2.3"),sQuery(id+"F0.wireOp",EDGE,"E3.3.1"),sQuery(id+"F0.wireOp",EDGE,"E3.3.2"),sQuery(id+"F0.wireOp",EDGE,"E3.3.3"),sQuery(id+"F0.wireOp",EDGE,"E3.4.1"),sQuery(id+"F0.wireOp",EDGE,"E3.4.2"),sQuery(id+"F0.wireOp",EDGE,"E3.4.3"),sQuery(id+"F0.wireOp",EDGE,"E3.5.1"),sQuery(id+"F0.wireOp",EDGE,"E3.5.2"),sQuery(id+"F0.wireOp",EDGE,"E3.5.3"),sQuery(id+"F0.wireOp",EDGE,"E3.6.1"),sQuery(id+"F0.wireOp",EDGE,"E3.6.2"),sQuery(id+"F0.wireOp",EDGE,"E3.6.3"),sQuery(id+"F0.wireOp",EDGE,"E3.7.1"),sQuery(id+"F0.wireOp",EDGE,"E3.7.2"),sQuery(id+"F0.wireOp",EDGE,"E3.7.3"),sQuery(id+"F0.wireOp",EDGE,"E3.8.1"),sQuery(id+"F0.wireOp",EDGE,"E3.8.2"),sQuery(id+"F0.wireOp",EDGE,"E3.8.3"),sQuery(id+"F0.wireOp",EDGE,"E3.9.1"),sQuery(id+"F0.wireOp",EDGE,"E3.9.2"),sQuery(id+"F0.wireOp",EDGE,"E3.9.3"),sQuery(id+"F0.wireOp",EDGE,"E3.10.1"),sQuery(id+"F0.wireOp",EDGE,"E3.10.2"),sQuery(id+"F0.wireOp",EDGE,"E3.10.3"),sQuery(id+"F0.wireOp",EDGE,"E3.11.1"),sQuery(id+"F0.wireOp",EDGE,"E3.11.2"),sQuery(id+"F0.wireOp",EDGE,"E3.11.3"),subQ1,subQ0,sQuery(id+"F0.wireOp",EDGE,"E3.12.3")])],"isStart":true})],"blendedInto":[makeQuery(id+"F1.opExtrude","CAP_FACE",FACE,{"disambiguationData":[OSD([sQuery(id+"F0.wireOp",EDGE,"E0"),sQuery(id+"F0.wireOp",EDGE,"E1"),sQuery(id+"F0.wireOp",EDGE,"E2.bottom"),sQuery(id+"F0.wireOp",EDGE,"E2.left"),sQuery(id+"F0.wireOp",EDGE,"E2.right"),sQuery(id+"F0.wireOp",EDGE,"E3.1.1"),sQuery(id+"F0.wireOp",EDGE,"E3.1.2"),sQuery(id+"F0.wireOp",EDGE,"E3.1.3"),sQuery(id+"F0.wireOp",EDGE,"E3.2.1"),sQuery(id+"F0.wireOp",EDGE,"E3.2.2"),sQuery(id+"F0.wireOp",EDGE,"E3.2.3"),sQuery(id+"F0.wireOp",EDGE,"E3.3.1"),sQuery(id+"F0.wireOp",EDGE,"E3.3.2"),sQuery(id+"F0.wireOp",EDGE,"E3.3.3"),sQuery(id+"F0.wireOp",EDGE,"E3.4.1"),sQuery(id+"F0.wireOp",EDGE,"E3.4.2"),sQuery(id+"F0.wireOp",EDGE,"E3.4.3"),sQuery(id+"F0.wireOp",EDGE,"E3.5.1"),sQuery(id+"F0.wireOp",EDGE,"E3.5.2"),sQuery(id+"F0.wireOp",EDGE,"E3.5.3"),sQuery(id+"F0.wireOp",EDGE,"E3.6.1"),sQuery(id+"F0.wireOp",EDGE,"E3.6.2"),sQuery(id+"F0.wireOp",EDGE,"E3.6.3"),sQuery(id+"F0.wireOp",EDGE,"E3.7.1"),sQuery(id+"F0.wireOp",EDGE,"E3.7.2"),sQuery(id+"F0.wireOp",EDGE,"E3.7.3"),sQuery(id+"F0.wireOp",EDGE,"E3.8.1"),sQuery(id+"F0.wireOp",EDGE,"E3.8.2"),sQuery(id+"F0.wireOp",EDGE,"E3.8.3"),sQuery(id+"F0.wireOp",EDGE,"E3.9.1"),sQuery(id+"F0.wireOp",EDGE,"E3.9.2"),sQuery(id+"F0.wireOp",EDGE,"E3.9.3"),sQuery(id+"F0.wireOp",EDGE,"E3.10.1"),sQuery(id+"F0.wireOp",EDGE,"E3.10.2"),sQuery(id+"F0.wireOp",EDGE,"E3.10.3"),sQuery(id+"F0.wireOp",EDGE,"E3.11.1"),sQuery(id+"F0.wireOp",EDGE,"E3.11.2"),sQuery(id+"F0.wireOp",EDGE,"E3.11.3"),subQ1,subQ0,sQuery(id+"F0.wireOp",EDGE,"E3.12.3")])],"isStart":true})]}),makeQuery(id+"F1.opExtrude","CAP_EDGE",EDGE,{"disambiguationData":[OSD([subQ0])],"isStart":true})],"blendedInto":[]});}
            var Q58;
            {var subQ0=sQuery(id+"F0.wireOp",EDGE,"E3.9.2");var subQ1=sQuery(id+"F0.wireOp",EDGE,"E3.9.3");Q58=makeQuery(id+"F4.opChamfer","BLEND_EDGE",EDGE,{"blendedFrom":[makeQuery(id+"F3.opChamfer","BLEND_EDGE",EDGE,{"blendedFrom":[makeQuery(id+"F1.opExtrude","SWEPT_EDGE",EDGE,{"disambiguationData":[OSD([subQ0,subQ1])]}),makeQuery(id+"F1.opExtrude","CAP_FACE",FACE,{"disambiguationData":[OSD([sQuery(id+"F0.wireOp",EDGE,"E0"),sQuery(id+"F0.wireOp",EDGE,"E1"),sQuery(id+"F0.wireOp",EDGE,"E2.bottom"),sQuery(id+"F0.wireOp",EDGE,"E2.left"),sQuery(id+"F0.wireOp",EDGE,"E2.right"),sQuery(id+"F0.wireOp",EDGE,"E3.1.1"),sQuery(id+"F0.wireOp",EDGE,"E3.1.2"),sQuery(id+"F0.wireOp",EDGE,"E3.1.3"),sQuery(id+"F0.wireOp",EDGE,"E3.2.1"),sQuery(id+"F0.wireOp",EDGE,"E3.2.2"),sQuery(id+"F0.wireOp",EDGE,"E3.2.3"),sQuery(id+"F0.wireOp",EDGE,"E3.3.1"),sQuery(id+"F0.wireOp",EDGE,"E3.3.2"),sQuery(id+"F0.wireOp",EDGE,"E3.3.3"),sQuery(id+"F0.wireOp",EDGE,"E3.4.1"),sQuery(id+"F0.wireOp",EDGE,"E3.4.2"),sQuery(id+"F0.wireOp",EDGE,"E3.4.3"),sQuery(id+"F0.wireOp",EDGE,"E3.5.1"),sQuery(id+"F0.wireOp",EDGE,"E3.5.2"),sQuery(id+"F0.wireOp",EDGE,"E3.5.3"),sQuery(id+"F0.wireOp",EDGE,"E3.6.1"),sQuery(id+"F0.wireOp",EDGE,"E3.6.2"),sQuery(id+"F0.wireOp",EDGE,"E3.6.3"),sQuery(id+"F0.wireOp",EDGE,"E3.7.1"),sQuery(id+"F0.wireOp",EDGE,"E3.7.2"),sQuery(id+"F0.wireOp",EDGE,"E3.7.3"),sQuery(id+"F0.wireOp",EDGE,"E3.8.1"),sQuery(id+"F0.wireOp",EDGE,"E3.8.2"),sQuery(id+"F0.wireOp",EDGE,"E3.8.3"),sQuery(id+"F0.wireOp",EDGE,"E3.9.1"),subQ0,subQ1,sQuery(id+"F0.wireOp",EDGE,"E3.10.1"),sQuery(id+"F0.wireOp",EDGE,"E3.10.2"),sQuery(id+"F0.wireOp",EDGE,"E3.10.3"),sQuery(id+"F0.wireOp",EDGE,"E3.11.1"),sQuery(id+"F0.wireOp",EDGE,"E3.11.2"),sQuery(id+"F0.wireOp",EDGE,"E3.11.3"),sQuery(id+"F0.wireOp",EDGE,"E3.12.1"),sQuery(id+"F0.wireOp",EDGE,"E3.12.2"),sQuery(id+"F0.wireOp",EDGE,"E3.12.3")])],"isStart":true})],"blendedInto":[makeQuery(id+"F1.opExtrude","CAP_FACE",FACE,{"disambiguationData":[OSD([sQuery(id+"F0.wireOp",EDGE,"E0"),sQuery(id+"F0.wireOp",EDGE,"E1"),sQuery(id+"F0.wireOp",EDGE,"E2.bottom"),sQuery(id+"F0.wireOp",EDGE,"E2.left"),sQuery(id+"F0.wireOp",EDGE,"E2.right"),sQuery(id+"F0.wireOp",EDGE,"E3.1.1"),sQuery(id+"F0.wireOp",EDGE,"E3.1.2"),sQuery(id+"F0.wireOp",EDGE,"E3.1.3"),sQuery(id+"F0.wireOp",EDGE,"E3.2.1"),sQuery(id+"F0.wireOp",EDGE,"E3.2.2"),sQuery(id+"F0.wireOp",EDGE,"E3.2.3"),sQuery(id+"F0.wireOp",EDGE,"E3.3.1"),sQuery(id+"F0.wireOp",EDGE,"E3.3.2"),sQuery(id+"F0.wireOp",EDGE,"E3.3.3"),sQuery(id+"F0.wireOp",EDGE,"E3.4.1"),sQuery(id+"F0.wireOp",EDGE,"E3.4.2"),sQuery(id+"F0.wireOp",EDGE,"E3.4.3"),sQuery(id+"F0.wireOp",EDGE,"E3.5.1"),sQuery(id+"F0.wireOp",EDGE,"E3.5.2"),sQuery(id+"F0.wireOp",EDGE,"E3.5.3"),sQuery(id+"F0.wireOp",EDGE,"E3.6.1"),sQuery(id+"F0.wireOp",EDGE,"E3.6.2"),sQuery(id+"F0.wireOp",EDGE,"E3.6.3"),sQuery(id+"F0.wireOp",EDGE,"E3.7.1"),sQuery(id+"F0.wireOp",EDGE,"E3.7.2"),sQuery(id+"F0.wireOp",EDGE,"E3.7.3"),sQuery(id+"F0.wireOp",EDGE,"E3.8.1"),sQuery(id+"F0.wireOp",EDGE,"E3.8.2"),sQuery(id+"F0.wireOp",EDGE,"E3.8.3"),sQuery(id+"F0.wireOp",EDGE,"E3.9.1"),subQ0,subQ1,sQuery(id+"F0.wireOp",EDGE,"E3.10.1"),sQuery(id+"F0.wireOp",EDGE,"E3.10.2"),sQuery(id+"F0.wireOp",EDGE,"E3.10.3"),sQuery(id+"F0.wireOp",EDGE,"E3.11.1"),sQuery(id+"F0.wireOp",EDGE,"E3.11.2"),sQuery(id+"F0.wireOp",EDGE,"E3.11.3"),sQuery(id+"F0.wireOp",EDGE,"E3.12.1"),sQuery(id+"F0.wireOp",EDGE,"E3.12.2"),sQuery(id+"F0.wireOp",EDGE,"E3.12.3")])],"isStart":true})]}),makeQuery(id+"F1.opExtrude","CAP_EDGE",EDGE,{"disambiguationData":[OSD([subQ0])],"isStart":true})],"blendedInto":[]});}
            var Q59;
            {var subQ0=sQuery(id+"F0.wireOp",EDGE,"E3.9.2");var subQ1=sQuery(id+"F0.wireOp",EDGE,"E3.9.1");Q59=makeQuery(id+"F4.opChamfer","BLEND_EDGE",EDGE,{"blendedFrom":[makeQuery(id+"F3.opChamfer","BLEND_EDGE",EDGE,{"blendedFrom":[makeQuery(id+"F1.opExtrude","SWEPT_EDGE",EDGE,{"disambiguationData":[OSD([subQ1,subQ0])]}),makeQuery(id+"F1.opExtrude","CAP_FACE",FACE,{"disambiguationData":[OSD([sQuery(id+"F0.wireOp",EDGE,"E0"),sQuery(id+"F0.wireOp",EDGE,"E1"),sQuery(id+"F0.wireOp",EDGE,"E2.bottom"),sQuery(id+"F0.wireOp",EDGE,"E2.left"),sQuery(id+"F0.wireOp",EDGE,"E2.right"),sQuery(id+"F0.wireOp",EDGE,"E3.1.1"),sQuery(id+"F0.wireOp",EDGE,"E3.1.2"),sQuery(id+"F0.wireOp",EDGE,"E3.1.3"),sQuery(id+"F0.wireOp",EDGE,"E3.2.1"),sQuery(id+"F0.wireOp",EDGE,"E3.2.2"),sQuery(id+"F0.wireOp",EDGE,"E3.2.3"),sQuery(id+"F0.wireOp",EDGE,"E3.3.1"),sQuery(id+"F0.wireOp",EDGE,"E3.3.2"),sQuery(id+"F0.wireOp",EDGE,"E3.3.3"),sQuery(id+"F0.wireOp",EDGE,"E3.4.1"),sQuery(id+"F0.wireOp",EDGE,"E3.4.2"),sQuery(id+"F0.wireOp",EDGE,"E3.4.3"),sQuery(id+"F0.wireOp",EDGE,"E3.5.1"),sQuery(id+"F0.wireOp",EDGE,"E3.5.2"),sQuery(id+"F0.wireOp",EDGE,"E3.5.3"),sQuery(id+"F0.wireOp",EDGE,"E3.6.1"),sQuery(id+"F0.wireOp",EDGE,"E3.6.2"),sQuery(id+"F0.wireOp",EDGE,"E3.6.3"),sQuery(id+"F0.wireOp",EDGE,"E3.7.1"),sQuery(id+"F0.wireOp",EDGE,"E3.7.2"),sQuery(id+"F0.wireOp",EDGE,"E3.7.3"),sQuery(id+"F0.wireOp",EDGE,"E3.8.1"),sQuery(id+"F0.wireOp",EDGE,"E3.8.2"),sQuery(id+"F0.wireOp",EDGE,"E3.8.3"),subQ1,subQ0,sQuery(id+"F0.wireOp",EDGE,"E3.9.3"),sQuery(id+"F0.wireOp",EDGE,"E3.10.1"),sQuery(id+"F0.wireOp",EDGE,"E3.10.2"),sQuery(id+"F0.wireOp",EDGE,"E3.10.3"),sQuery(id+"F0.wireOp",EDGE,"E3.11.1"),sQuery(id+"F0.wireOp",EDGE,"E3.11.2"),sQuery(id+"F0.wireOp",EDGE,"E3.11.3"),sQuery(id+"F0.wireOp",EDGE,"E3.12.1"),sQuery(id+"F0.wireOp",EDGE,"E3.12.2"),sQuery(id+"F0.wireOp",EDGE,"E3.12.3")])],"isStart":true})],"blendedInto":[makeQuery(id+"F1.opExtrude","CAP_FACE",FACE,{"disambiguationData":[OSD([sQuery(id+"F0.wireOp",EDGE,"E0"),sQuery(id+"F0.wireOp",EDGE,"E1"),sQuery(id+"F0.wireOp",EDGE,"E2.bottom"),sQuery(id+"F0.wireOp",EDGE,"E2.left"),sQuery(id+"F0.wireOp",EDGE,"E2.right"),sQuery(id+"F0.wireOp",EDGE,"E3.1.1"),sQuery(id+"F0.wireOp",EDGE,"E3.1.2"),sQuery(id+"F0.wireOp",EDGE,"E3.1.3"),sQuery(id+"F0.wireOp",EDGE,"E3.2.1"),sQuery(id+"F0.wireOp",EDGE,"E3.2.2"),sQuery(id+"F0.wireOp",EDGE,"E3.2.3"),sQuery(id+"F0.wireOp",EDGE,"E3.3.1"),sQuery(id+"F0.wireOp",EDGE,"E3.3.2"),sQuery(id+"F0.wireOp",EDGE,"E3.3.3"),sQuery(id+"F0.wireOp",EDGE,"E3.4.1"),sQuery(id+"F0.wireOp",EDGE,"E3.4.2"),sQuery(id+"F0.wireOp",EDGE,"E3.4.3"),sQuery(id+"F0.wireOp",EDGE,"E3.5.1"),sQuery(id+"F0.wireOp",EDGE,"E3.5.2"),sQuery(id+"F0.wireOp",EDGE,"E3.5.3"),sQuery(id+"F0.wireOp",EDGE,"E3.6.1"),sQuery(id+"F0.wireOp",EDGE,"E3.6.2"),sQuery(id+"F0.wireOp",EDGE,"E3.6.3"),sQuery(id+"F0.wireOp",EDGE,"E3.7.1"),sQuery(id+"F0.wireOp",EDGE,"E3.7.2"),sQuery(id+"F0.wireOp",EDGE,"E3.7.3"),sQuery(id+"F0.wireOp",EDGE,"E3.8.1"),sQuery(id+"F0.wireOp",EDGE,"E3.8.2"),sQuery(id+"F0.wireOp",EDGE,"E3.8.3"),subQ1,subQ0,sQuery(id+"F0.wireOp",EDGE,"E3.9.3"),sQuery(id+"F0.wireOp",EDGE,"E3.10.1"),sQuery(id+"F0.wireOp",EDGE,"E3.10.2"),sQuery(id+"F0.wireOp",EDGE,"E3.10.3"),sQuery(id+"F0.wireOp",EDGE,"E3.11.1"),sQuery(id+"F0.wireOp",EDGE,"E3.11.2"),sQuery(id+"F0.wireOp",EDGE,"E3.11.3"),sQuery(id+"F0.wireOp",EDGE,"E3.12.1"),sQuery(id+"F0.wireOp",EDGE,"E3.12.2"),sQuery(id+"F0.wireOp",EDGE,"E3.12.3")])],"isStart":true})]}),makeQuery(id+"F1.opExtrude","CAP_EDGE",EDGE,{"disambiguationData":[OSD([subQ0])],"isStart":true})],"blendedInto":[]});}
            var Q60;
            {var subQ0=sQuery(id+"F0.wireOp",EDGE,"E3.8.2");var subQ1=sQuery(id+"F0.wireOp",EDGE,"E3.8.3");Q60=makeQuery(id+"F4.opChamfer","BLEND_EDGE",EDGE,{"blendedFrom":[makeQuery(id+"F3.opChamfer","BLEND_EDGE",EDGE,{"blendedFrom":[makeQuery(id+"F1.opExtrude","SWEPT_EDGE",EDGE,{"disambiguationData":[OSD([subQ0,subQ1])]}),makeQuery(id+"F1.opExtrude","CAP_FACE",FACE,{"disambiguationData":[OSD([sQuery(id+"F0.wireOp",EDGE,"E0"),sQuery(id+"F0.wireOp",EDGE,"E1"),sQuery(id+"F0.wireOp",EDGE,"E2.bottom"),sQuery(id+"F0.wireOp",EDGE,"E2.left"),sQuery(id+"F0.wireOp",EDGE,"E2.right"),sQuery(id+"F0.wireOp",EDGE,"E3.1.1"),sQuery(id+"F0.wireOp",EDGE,"E3.1.2"),sQuery(id+"F0.wireOp",EDGE,"E3.1.3"),sQuery(id+"F0.wireOp",EDGE,"E3.2.1"),sQuery(id+"F0.wireOp",EDGE,"E3.2.2"),sQuery(id+"F0.wireOp",EDGE,"E3.2.3"),sQuery(id+"F0.wireOp",EDGE,"E3.3.1"),sQuery(id+"F0.wireOp",EDGE,"E3.3.2"),sQuery(id+"F0.wireOp",EDGE,"E3.3.3"),sQuery(id+"F0.wireOp",EDGE,"E3.4.1"),sQuery(id+"F0.wireOp",EDGE,"E3.4.2"),sQuery(id+"F0.wireOp",EDGE,"E3.4.3"),sQuery(id+"F0.wireOp",EDGE,"E3.5.1"),sQuery(id+"F0.wireOp",EDGE,"E3.5.2"),sQuery(id+"F0.wireOp",EDGE,"E3.5.3"),sQuery(id+"F0.wireOp",EDGE,"E3.6.1"),sQuery(id+"F0.wireOp",EDGE,"E3.6.2"),sQuery(id+"F0.wireOp",EDGE,"E3.6.3"),sQuery(id+"F0.wireOp",EDGE,"E3.7.1"),sQuery(id+"F0.wireOp",EDGE,"E3.7.2"),sQuery(id+"F0.wireOp",EDGE,"E3.7.3"),sQuery(id+"F0.wireOp",EDGE,"E3.8.1"),subQ0,subQ1,sQuery(id+"F0.wireOp",EDGE,"E3.9.1"),sQuery(id+"F0.wireOp",EDGE,"E3.9.2"),sQuery(id+"F0.wireOp",EDGE,"E3.9.3"),sQuery(id+"F0.wireOp",EDGE,"E3.10.1"),sQuery(id+"F0.wireOp",EDGE,"E3.10.2"),sQuery(id+"F0.wireOp",EDGE,"E3.10.3"),sQuery(id+"F0.wireOp",EDGE,"E3.11.1"),sQuery(id+"F0.wireOp",EDGE,"E3.11.2"),sQuery(id+"F0.wireOp",EDGE,"E3.11.3"),sQuery(id+"F0.wireOp",EDGE,"E3.12.1"),sQuery(id+"F0.wireOp",EDGE,"E3.12.2"),sQuery(id+"F0.wireOp",EDGE,"E3.12.3")])],"isStart":true})],"blendedInto":[makeQuery(id+"F1.opExtrude","CAP_FACE",FACE,{"disambiguationData":[OSD([sQuery(id+"F0.wireOp",EDGE,"E0"),sQuery(id+"F0.wireOp",EDGE,"E1"),sQuery(id+"F0.wireOp",EDGE,"E2.bottom"),sQuery(id+"F0.wireOp",EDGE,"E2.left"),sQuery(id+"F0.wireOp",EDGE,"E2.right"),sQuery(id+"F0.wireOp",EDGE,"E3.1.1"),sQuery(id+"F0.wireOp",EDGE,"E3.1.2"),sQuery(id+"F0.wireOp",EDGE,"E3.1.3"),sQuery(id+"F0.wireOp",EDGE,"E3.2.1"),sQuery(id+"F0.wireOp",EDGE,"E3.2.2"),sQuery(id+"F0.wireOp",EDGE,"E3.2.3"),sQuery(id+"F0.wireOp",EDGE,"E3.3.1"),sQuery(id+"F0.wireOp",EDGE,"E3.3.2"),sQuery(id+"F0.wireOp",EDGE,"E3.3.3"),sQuery(id+"F0.wireOp",EDGE,"E3.4.1"),sQuery(id+"F0.wireOp",EDGE,"E3.4.2"),sQuery(id+"F0.wireOp",EDGE,"E3.4.3"),sQuery(id+"F0.wireOp",EDGE,"E3.5.1"),sQuery(id+"F0.wireOp",EDGE,"E3.5.2"),sQuery(id+"F0.wireOp",EDGE,"E3.5.3"),sQuery(id+"F0.wireOp",EDGE,"E3.6.1"),sQuery(id+"F0.wireOp",EDGE,"E3.6.2"),sQuery(id+"F0.wireOp",EDGE,"E3.6.3"),sQuery(id+"F0.wireOp",EDGE,"E3.7.1"),sQuery(id+"F0.wireOp",EDGE,"E3.7.2"),sQuery(id+"F0.wireOp",EDGE,"E3.7.3"),sQuery(id+"F0.wireOp",EDGE,"E3.8.1"),subQ0,subQ1,sQuery(id+"F0.wireOp",EDGE,"E3.9.1"),sQuery(id+"F0.wireOp",EDGE,"E3.9.2"),sQuery(id+"F0.wireOp",EDGE,"E3.9.3"),sQuery(id+"F0.wireOp",EDGE,"E3.10.1"),sQuery(id+"F0.wireOp",EDGE,"E3.10.2"),sQuery(id+"F0.wireOp",EDGE,"E3.10.3"),sQuery(id+"F0.wireOp",EDGE,"E3.11.1"),sQuery(id+"F0.wireOp",EDGE,"E3.11.2"),sQuery(id+"F0.wireOp",EDGE,"E3.11.3"),sQuery(id+"F0.wireOp",EDGE,"E3.12.1"),sQuery(id+"F0.wireOp",EDGE,"E3.12.2"),sQuery(id+"F0.wireOp",EDGE,"E3.12.3")])],"isStart":true})]}),makeQuery(id+"F1.opExtrude","CAP_EDGE",EDGE,{"disambiguationData":[OSD([subQ0])],"isStart":true})],"blendedInto":[]});}
            var Q61;
            {var subQ0=sQuery(id+"F0.wireOp",EDGE,"E3.8.2");var subQ1=sQuery(id+"F0.wireOp",EDGE,"E3.8.1");Q61=makeQuery(id+"F4.opChamfer","BLEND_EDGE",EDGE,{"blendedFrom":[makeQuery(id+"F3.opChamfer","BLEND_EDGE",EDGE,{"blendedFrom":[makeQuery(id+"F1.opExtrude","SWEPT_EDGE",EDGE,{"disambiguationData":[OSD([subQ1,subQ0])]}),makeQuery(id+"F1.opExtrude","CAP_FACE",FACE,{"disambiguationData":[OSD([sQuery(id+"F0.wireOp",EDGE,"E0"),sQuery(id+"F0.wireOp",EDGE,"E1"),sQuery(id+"F0.wireOp",EDGE,"E2.bottom"),sQuery(id+"F0.wireOp",EDGE,"E2.left"),sQuery(id+"F0.wireOp",EDGE,"E2.right"),sQuery(id+"F0.wireOp",EDGE,"E3.1.1"),sQuery(id+"F0.wireOp",EDGE,"E3.1.2"),sQuery(id+"F0.wireOp",EDGE,"E3.1.3"),sQuery(id+"F0.wireOp",EDGE,"E3.2.1"),sQuery(id+"F0.wireOp",EDGE,"E3.2.2"),sQuery(id+"F0.wireOp",EDGE,"E3.2.3"),sQuery(id+"F0.wireOp",EDGE,"E3.3.1"),sQuery(id+"F0.wireOp",EDGE,"E3.3.2"),sQuery(id+"F0.wireOp",EDGE,"E3.3.3"),sQuery(id+"F0.wireOp",EDGE,"E3.4.1"),sQuery(id+"F0.wireOp",EDGE,"E3.4.2"),sQuery(id+"F0.wireOp",EDGE,"E3.4.3"),sQuery(id+"F0.wireOp",EDGE,"E3.5.1"),sQuery(id+"F0.wireOp",EDGE,"E3.5.2"),sQuery(id+"F0.wireOp",EDGE,"E3.5.3"),sQuery(id+"F0.wireOp",EDGE,"E3.6.1"),sQuery(id+"F0.wireOp",EDGE,"E3.6.2"),sQuery(id+"F0.wireOp",EDGE,"E3.6.3"),sQuery(id+"F0.wireOp",EDGE,"E3.7.1"),sQuery(id+"F0.wireOp",EDGE,"E3.7.2"),sQuery(id+"F0.wireOp",EDGE,"E3.7.3"),subQ1,subQ0,sQuery(id+"F0.wireOp",EDGE,"E3.8.3"),sQuery(id+"F0.wireOp",EDGE,"E3.9.1"),sQuery(id+"F0.wireOp",EDGE,"E3.9.2"),sQuery(id+"F0.wireOp",EDGE,"E3.9.3"),sQuery(id+"F0.wireOp",EDGE,"E3.10.1"),sQuery(id+"F0.wireOp",EDGE,"E3.10.2"),sQuery(id+"F0.wireOp",EDGE,"E3.10.3"),sQuery(id+"F0.wireOp",EDGE,"E3.11.1"),sQuery(id+"F0.wireOp",EDGE,"E3.11.2"),sQuery(id+"F0.wireOp",EDGE,"E3.11.3"),sQuery(id+"F0.wireOp",EDGE,"E3.12.1"),sQuery(id+"F0.wireOp",EDGE,"E3.12.2"),sQuery(id+"F0.wireOp",EDGE,"E3.12.3")])],"isStart":true})],"blendedInto":[makeQuery(id+"F1.opExtrude","CAP_FACE",FACE,{"disambiguationData":[OSD([sQuery(id+"F0.wireOp",EDGE,"E0"),sQuery(id+"F0.wireOp",EDGE,"E1"),sQuery(id+"F0.wireOp",EDGE,"E2.bottom"),sQuery(id+"F0.wireOp",EDGE,"E2.left"),sQuery(id+"F0.wireOp",EDGE,"E2.right"),sQuery(id+"F0.wireOp",EDGE,"E3.1.1"),sQuery(id+"F0.wireOp",EDGE,"E3.1.2"),sQuery(id+"F0.wireOp",EDGE,"E3.1.3"),sQuery(id+"F0.wireOp",EDGE,"E3.2.1"),sQuery(id+"F0.wireOp",EDGE,"E3.2.2"),sQuery(id+"F0.wireOp",EDGE,"E3.2.3"),sQuery(id+"F0.wireOp",EDGE,"E3.3.1"),sQuery(id+"F0.wireOp",EDGE,"E3.3.2"),sQuery(id+"F0.wireOp",EDGE,"E3.3.3"),sQuery(id+"F0.wireOp",EDGE,"E3.4.1"),sQuery(id+"F0.wireOp",EDGE,"E3.4.2"),sQuery(id+"F0.wireOp",EDGE,"E3.4.3"),sQuery(id+"F0.wireOp",EDGE,"E3.5.1"),sQuery(id+"F0.wireOp",EDGE,"E3.5.2"),sQuery(id+"F0.wireOp",EDGE,"E3.5.3"),sQuery(id+"F0.wireOp",EDGE,"E3.6.1"),sQuery(id+"F0.wireOp",EDGE,"E3.6.2"),sQuery(id+"F0.wireOp",EDGE,"E3.6.3"),sQuery(id+"F0.wireOp",EDGE,"E3.7.1"),sQuery(id+"F0.wireOp",EDGE,"E3.7.2"),sQuery(id+"F0.wireOp",EDGE,"E3.7.3"),subQ1,subQ0,sQuery(id+"F0.wireOp",EDGE,"E3.8.3"),sQuery(id+"F0.wireOp",EDGE,"E3.9.1"),sQuery(id+"F0.wireOp",EDGE,"E3.9.2"),sQuery(id+"F0.wireOp",EDGE,"E3.9.3"),sQuery(id+"F0.wireOp",EDGE,"E3.10.1"),sQuery(id+"F0.wireOp",EDGE,"E3.10.2"),sQuery(id+"F0.wireOp",EDGE,"E3.10.3"),sQuery(id+"F0.wireOp",EDGE,"E3.11.1"),sQuery(id+"F0.wireOp",EDGE,"E3.11.2"),sQuery(id+"F0.wireOp",EDGE,"E3.11.3"),sQuery(id+"F0.wireOp",EDGE,"E3.12.1"),sQuery(id+"F0.wireOp",EDGE,"E3.12.2"),sQuery(id+"F0.wireOp",EDGE,"E3.12.3")])],"isStart":true})]}),makeQuery(id+"F1.opExtrude","CAP_EDGE",EDGE,{"disambiguationData":[OSD([subQ0])],"isStart":true})],"blendedInto":[]});}
            var Q62;
            {var subQ0=sQuery(id+"F0.wireOp",EDGE,"E3.7.2");var subQ1=sQuery(id+"F0.wireOp",EDGE,"E3.7.3");Q62=makeQuery(id+"F4.opChamfer","BLEND_EDGE",EDGE,{"blendedFrom":[makeQuery(id+"F3.opChamfer","BLEND_EDGE",EDGE,{"blendedFrom":[makeQuery(id+"F1.opExtrude","SWEPT_EDGE",EDGE,{"disambiguationData":[OSD([subQ0,subQ1])]}),makeQuery(id+"F1.opExtrude","CAP_FACE",FACE,{"disambiguationData":[OSD([sQuery(id+"F0.wireOp",EDGE,"E0"),sQuery(id+"F0.wireOp",EDGE,"E1"),sQuery(id+"F0.wireOp",EDGE,"E2.bottom"),sQuery(id+"F0.wireOp",EDGE,"E2.left"),sQuery(id+"F0.wireOp",EDGE,"E2.right"),sQuery(id+"F0.wireOp",EDGE,"E3.1.1"),sQuery(id+"F0.wireOp",EDGE,"E3.1.2"),sQuery(id+"F0.wireOp",EDGE,"E3.1.3"),sQuery(id+"F0.wireOp",EDGE,"E3.2.1"),sQuery(id+"F0.wireOp",EDGE,"E3.2.2"),sQuery(id+"F0.wireOp",EDGE,"E3.2.3"),sQuery(id+"F0.wireOp",EDGE,"E3.3.1"),sQuery(id+"F0.wireOp",EDGE,"E3.3.2"),sQuery(id+"F0.wireOp",EDGE,"E3.3.3"),sQuery(id+"F0.wireOp",EDGE,"E3.4.1"),sQuery(id+"F0.wireOp",EDGE,"E3.4.2"),sQuery(id+"F0.wireOp",EDGE,"E3.4.3"),sQuery(id+"F0.wireOp",EDGE,"E3.5.1"),sQuery(id+"F0.wireOp",EDGE,"E3.5.2"),sQuery(id+"F0.wireOp",EDGE,"E3.5.3"),sQuery(id+"F0.wireOp",EDGE,"E3.6.1"),sQuery(id+"F0.wireOp",EDGE,"E3.6.2"),sQuery(id+"F0.wireOp",EDGE,"E3.6.3"),sQuery(id+"F0.wireOp",EDGE,"E3.7.1"),subQ0,subQ1,sQuery(id+"F0.wireOp",EDGE,"E3.8.1"),sQuery(id+"F0.wireOp",EDGE,"E3.8.2"),sQuery(id+"F0.wireOp",EDGE,"E3.8.3"),sQuery(id+"F0.wireOp",EDGE,"E3.9.1"),sQuery(id+"F0.wireOp",EDGE,"E3.9.2"),sQuery(id+"F0.wireOp",EDGE,"E3.9.3"),sQuery(id+"F0.wireOp",EDGE,"E3.10.1"),sQuery(id+"F0.wireOp",EDGE,"E3.10.2"),sQuery(id+"F0.wireOp",EDGE,"E3.10.3"),sQuery(id+"F0.wireOp",EDGE,"E3.11.1"),sQuery(id+"F0.wireOp",EDGE,"E3.11.2"),sQuery(id+"F0.wireOp",EDGE,"E3.11.3"),sQuery(id+"F0.wireOp",EDGE,"E3.12.1"),sQuery(id+"F0.wireOp",EDGE,"E3.12.2"),sQuery(id+"F0.wireOp",EDGE,"E3.12.3")])],"isStart":true})],"blendedInto":[makeQuery(id+"F1.opExtrude","CAP_FACE",FACE,{"disambiguationData":[OSD([sQuery(id+"F0.wireOp",EDGE,"E0"),sQuery(id+"F0.wireOp",EDGE,"E1"),sQuery(id+"F0.wireOp",EDGE,"E2.bottom"),sQuery(id+"F0.wireOp",EDGE,"E2.left"),sQuery(id+"F0.wireOp",EDGE,"E2.right"),sQuery(id+"F0.wireOp",EDGE,"E3.1.1"),sQuery(id+"F0.wireOp",EDGE,"E3.1.2"),sQuery(id+"F0.wireOp",EDGE,"E3.1.3"),sQuery(id+"F0.wireOp",EDGE,"E3.2.1"),sQuery(id+"F0.wireOp",EDGE,"E3.2.2"),sQuery(id+"F0.wireOp",EDGE,"E3.2.3"),sQuery(id+"F0.wireOp",EDGE,"E3.3.1"),sQuery(id+"F0.wireOp",EDGE,"E3.3.2"),sQuery(id+"F0.wireOp",EDGE,"E3.3.3"),sQuery(id+"F0.wireOp",EDGE,"E3.4.1"),sQuery(id+"F0.wireOp",EDGE,"E3.4.2"),sQuery(id+"F0.wireOp",EDGE,"E3.4.3"),sQuery(id+"F0.wireOp",EDGE,"E3.5.1"),sQuery(id+"F0.wireOp",EDGE,"E3.5.2"),sQuery(id+"F0.wireOp",EDGE,"E3.5.3"),sQuery(id+"F0.wireOp",EDGE,"E3.6.1"),sQuery(id+"F0.wireOp",EDGE,"E3.6.2"),sQuery(id+"F0.wireOp",EDGE,"E3.6.3"),sQuery(id+"F0.wireOp",EDGE,"E3.7.1"),subQ0,subQ1,sQuery(id+"F0.wireOp",EDGE,"E3.8.1"),sQuery(id+"F0.wireOp",EDGE,"E3.8.2"),sQuery(id+"F0.wireOp",EDGE,"E3.8.3"),sQuery(id+"F0.wireOp",EDGE,"E3.9.1"),sQuery(id+"F0.wireOp",EDGE,"E3.9.2"),sQuery(id+"F0.wireOp",EDGE,"E3.9.3"),sQuery(id+"F0.wireOp",EDGE,"E3.10.1"),sQuery(id+"F0.wireOp",EDGE,"E3.10.2"),sQuery(id+"F0.wireOp",EDGE,"E3.10.3"),sQuery(id+"F0.wireOp",EDGE,"E3.11.1"),sQuery(id+"F0.wireOp",EDGE,"E3.11.2"),sQuery(id+"F0.wireOp",EDGE,"E3.11.3"),sQuery(id+"F0.wireOp",EDGE,"E3.12.1"),sQuery(id+"F0.wireOp",EDGE,"E3.12.2"),sQuery(id+"F0.wireOp",EDGE,"E3.12.3")])],"isStart":true})]}),makeQuery(id+"F1.opExtrude","CAP_EDGE",EDGE,{"disambiguationData":[OSD([subQ0])],"isStart":true})],"blendedInto":[]});}
            var Q63;
            {var subQ0=sQuery(id+"F0.wireOp",EDGE,"E3.7.2");var subQ1=sQuery(id+"F0.wireOp",EDGE,"E3.7.1");Q63=makeQuery(id+"F4.opChamfer","BLEND_EDGE",EDGE,{"blendedFrom":[makeQuery(id+"F3.opChamfer","BLEND_EDGE",EDGE,{"blendedFrom":[makeQuery(id+"F1.opExtrude","SWEPT_EDGE",EDGE,{"disambiguationData":[OSD([subQ1,subQ0])]}),makeQuery(id+"F1.opExtrude","CAP_FACE",FACE,{"disambiguationData":[OSD([sQuery(id+"F0.wireOp",EDGE,"E0"),sQuery(id+"F0.wireOp",EDGE,"E1"),sQuery(id+"F0.wireOp",EDGE,"E2.bottom"),sQuery(id+"F0.wireOp",EDGE,"E2.left"),sQuery(id+"F0.wireOp",EDGE,"E2.right"),sQuery(id+"F0.wireOp",EDGE,"E3.1.1"),sQuery(id+"F0.wireOp",EDGE,"E3.1.2"),sQuery(id+"F0.wireOp",EDGE,"E3.1.3"),sQuery(id+"F0.wireOp",EDGE,"E3.2.1"),sQuery(id+"F0.wireOp",EDGE,"E3.2.2"),sQuery(id+"F0.wireOp",EDGE,"E3.2.3"),sQuery(id+"F0.wireOp",EDGE,"E3.3.1"),sQuery(id+"F0.wireOp",EDGE,"E3.3.2"),sQuery(id+"F0.wireOp",EDGE,"E3.3.3"),sQuery(id+"F0.wireOp",EDGE,"E3.4.1"),sQuery(id+"F0.wireOp",EDGE,"E3.4.2"),sQuery(id+"F0.wireOp",EDGE,"E3.4.3"),sQuery(id+"F0.wireOp",EDGE,"E3.5.1"),sQuery(id+"F0.wireOp",EDGE,"E3.5.2"),sQuery(id+"F0.wireOp",EDGE,"E3.5.3"),sQuery(id+"F0.wireOp",EDGE,"E3.6.1"),sQuery(id+"F0.wireOp",EDGE,"E3.6.2"),sQuery(id+"F0.wireOp",EDGE,"E3.6.3"),subQ1,subQ0,sQuery(id+"F0.wireOp",EDGE,"E3.7.3"),sQuery(id+"F0.wireOp",EDGE,"E3.8.1"),sQuery(id+"F0.wireOp",EDGE,"E3.8.2"),sQuery(id+"F0.wireOp",EDGE,"E3.8.3"),sQuery(id+"F0.wireOp",EDGE,"E3.9.1"),sQuery(id+"F0.wireOp",EDGE,"E3.9.2"),sQuery(id+"F0.wireOp",EDGE,"E3.9.3"),sQuery(id+"F0.wireOp",EDGE,"E3.10.1"),sQuery(id+"F0.wireOp",EDGE,"E3.10.2"),sQuery(id+"F0.wireOp",EDGE,"E3.10.3"),sQuery(id+"F0.wireOp",EDGE,"E3.11.1"),sQuery(id+"F0.wireOp",EDGE,"E3.11.2"),sQuery(id+"F0.wireOp",EDGE,"E3.11.3"),sQuery(id+"F0.wireOp",EDGE,"E3.12.1"),sQuery(id+"F0.wireOp",EDGE,"E3.12.2"),sQuery(id+"F0.wireOp",EDGE,"E3.12.3")])],"isStart":true})],"blendedInto":[makeQuery(id+"F1.opExtrude","CAP_FACE",FACE,{"disambiguationData":[OSD([sQuery(id+"F0.wireOp",EDGE,"E0"),sQuery(id+"F0.wireOp",EDGE,"E1"),sQuery(id+"F0.wireOp",EDGE,"E2.bottom"),sQuery(id+"F0.wireOp",EDGE,"E2.left"),sQuery(id+"F0.wireOp",EDGE,"E2.right"),sQuery(id+"F0.wireOp",EDGE,"E3.1.1"),sQuery(id+"F0.wireOp",EDGE,"E3.1.2"),sQuery(id+"F0.wireOp",EDGE,"E3.1.3"),sQuery(id+"F0.wireOp",EDGE,"E3.2.1"),sQuery(id+"F0.wireOp",EDGE,"E3.2.2"),sQuery(id+"F0.wireOp",EDGE,"E3.2.3"),sQuery(id+"F0.wireOp",EDGE,"E3.3.1"),sQuery(id+"F0.wireOp",EDGE,"E3.3.2"),sQuery(id+"F0.wireOp",EDGE,"E3.3.3"),sQuery(id+"F0.wireOp",EDGE,"E3.4.1"),sQuery(id+"F0.wireOp",EDGE,"E3.4.2"),sQuery(id+"F0.wireOp",EDGE,"E3.4.3"),sQuery(id+"F0.wireOp",EDGE,"E3.5.1"),sQuery(id+"F0.wireOp",EDGE,"E3.5.2"),sQuery(id+"F0.wireOp",EDGE,"E3.5.3"),sQuery(id+"F0.wireOp",EDGE,"E3.6.1"),sQuery(id+"F0.wireOp",EDGE,"E3.6.2"),sQuery(id+"F0.wireOp",EDGE,"E3.6.3"),subQ1,subQ0,sQuery(id+"F0.wireOp",EDGE,"E3.7.3"),sQuery(id+"F0.wireOp",EDGE,"E3.8.1"),sQuery(id+"F0.wireOp",EDGE,"E3.8.2"),sQuery(id+"F0.wireOp",EDGE,"E3.8.3"),sQuery(id+"F0.wireOp",EDGE,"E3.9.1"),sQuery(id+"F0.wireOp",EDGE,"E3.9.2"),sQuery(id+"F0.wireOp",EDGE,"E3.9.3"),sQuery(id+"F0.wireOp",EDGE,"E3.10.1"),sQuery(id+"F0.wireOp",EDGE,"E3.10.2"),sQuery(id+"F0.wireOp",EDGE,"E3.10.3"),sQuery(id+"F0.wireOp",EDGE,"E3.11.1"),sQuery(id+"F0.wireOp",EDGE,"E3.11.2"),sQuery(id+"F0.wireOp",EDGE,"E3.11.3"),sQuery(id+"F0.wireOp",EDGE,"E3.12.1"),sQuery(id+"F0.wireOp",EDGE,"E3.12.2"),sQuery(id+"F0.wireOp",EDGE,"E3.12.3")])],"isStart":true})]}),makeQuery(id+"F1.opExtrude","CAP_EDGE",EDGE,{"disambiguationData":[OSD([subQ0])],"isStart":true})],"blendedInto":[]});}
            var Q64;
            {var subQ0=sQuery(id+"F0.wireOp",EDGE,"E3.6.2");var subQ1=sQuery(id+"F0.wireOp",EDGE,"E3.6.3");Q64=makeQuery(id+"F4.opChamfer","BLEND_EDGE",EDGE,{"blendedFrom":[makeQuery(id+"F3.opChamfer","BLEND_EDGE",EDGE,{"blendedFrom":[makeQuery(id+"F1.opExtrude","SWEPT_EDGE",EDGE,{"disambiguationData":[OSD([subQ0,subQ1])]}),makeQuery(id+"F1.opExtrude","CAP_FACE",FACE,{"disambiguationData":[OSD([sQuery(id+"F0.wireOp",EDGE,"E0"),sQuery(id+"F0.wireOp",EDGE,"E1"),sQuery(id+"F0.wireOp",EDGE,"E2.bottom"),sQuery(id+"F0.wireOp",EDGE,"E2.left"),sQuery(id+"F0.wireOp",EDGE,"E2.right"),sQuery(id+"F0.wireOp",EDGE,"E3.1.1"),sQuery(id+"F0.wireOp",EDGE,"E3.1.2"),sQuery(id+"F0.wireOp",EDGE,"E3.1.3"),sQuery(id+"F0.wireOp",EDGE,"E3.2.1"),sQuery(id+"F0.wireOp",EDGE,"E3.2.2"),sQuery(id+"F0.wireOp",EDGE,"E3.2.3"),sQuery(id+"F0.wireOp",EDGE,"E3.3.1"),sQuery(id+"F0.wireOp",EDGE,"E3.3.2"),sQuery(id+"F0.wireOp",EDGE,"E3.3.3"),sQuery(id+"F0.wireOp",EDGE,"E3.4.1"),sQuery(id+"F0.wireOp",EDGE,"E3.4.2"),sQuery(id+"F0.wireOp",EDGE,"E3.4.3"),sQuery(id+"F0.wireOp",EDGE,"E3.5.1"),sQuery(id+"F0.wireOp",EDGE,"E3.5.2"),sQuery(id+"F0.wireOp",EDGE,"E3.5.3"),sQuery(id+"F0.wireOp",EDGE,"E3.6.1"),subQ0,subQ1,sQuery(id+"F0.wireOp",EDGE,"E3.7.1"),sQuery(id+"F0.wireOp",EDGE,"E3.7.2"),sQuery(id+"F0.wireOp",EDGE,"E3.7.3"),sQuery(id+"F0.wireOp",EDGE,"E3.8.1"),sQuery(id+"F0.wireOp",EDGE,"E3.8.2"),sQuery(id+"F0.wireOp",EDGE,"E3.8.3"),sQuery(id+"F0.wireOp",EDGE,"E3.9.1"),sQuery(id+"F0.wireOp",EDGE,"E3.9.2"),sQuery(id+"F0.wireOp",EDGE,"E3.9.3"),sQuery(id+"F0.wireOp",EDGE,"E3.10.1"),sQuery(id+"F0.wireOp",EDGE,"E3.10.2"),sQuery(id+"F0.wireOp",EDGE,"E3.10.3"),sQuery(id+"F0.wireOp",EDGE,"E3.11.1"),sQuery(id+"F0.wireOp",EDGE,"E3.11.2"),sQuery(id+"F0.wireOp",EDGE,"E3.11.3"),sQuery(id+"F0.wireOp",EDGE,"E3.12.1"),sQuery(id+"F0.wireOp",EDGE,"E3.12.2"),sQuery(id+"F0.wireOp",EDGE,"E3.12.3")])],"isStart":true})],"blendedInto":[makeQuery(id+"F1.opExtrude","CAP_FACE",FACE,{"disambiguationData":[OSD([sQuery(id+"F0.wireOp",EDGE,"E0"),sQuery(id+"F0.wireOp",EDGE,"E1"),sQuery(id+"F0.wireOp",EDGE,"E2.bottom"),sQuery(id+"F0.wireOp",EDGE,"E2.left"),sQuery(id+"F0.wireOp",EDGE,"E2.right"),sQuery(id+"F0.wireOp",EDGE,"E3.1.1"),sQuery(id+"F0.wireOp",EDGE,"E3.1.2"),sQuery(id+"F0.wireOp",EDGE,"E3.1.3"),sQuery(id+"F0.wireOp",EDGE,"E3.2.1"),sQuery(id+"F0.wireOp",EDGE,"E3.2.2"),sQuery(id+"F0.wireOp",EDGE,"E3.2.3"),sQuery(id+"F0.wireOp",EDGE,"E3.3.1"),sQuery(id+"F0.wireOp",EDGE,"E3.3.2"),sQuery(id+"F0.wireOp",EDGE,"E3.3.3"),sQuery(id+"F0.wireOp",EDGE,"E3.4.1"),sQuery(id+"F0.wireOp",EDGE,"E3.4.2"),sQuery(id+"F0.wireOp",EDGE,"E3.4.3"),sQuery(id+"F0.wireOp",EDGE,"E3.5.1"),sQuery(id+"F0.wireOp",EDGE,"E3.5.2"),sQuery(id+"F0.wireOp",EDGE,"E3.5.3"),sQuery(id+"F0.wireOp",EDGE,"E3.6.1"),subQ0,subQ1,sQuery(id+"F0.wireOp",EDGE,"E3.7.1"),sQuery(id+"F0.wireOp",EDGE,"E3.7.2"),sQuery(id+"F0.wireOp",EDGE,"E3.7.3"),sQuery(id+"F0.wireOp",EDGE,"E3.8.1"),sQuery(id+"F0.wireOp",EDGE,"E3.8.2"),sQuery(id+"F0.wireOp",EDGE,"E3.8.3"),sQuery(id+"F0.wireOp",EDGE,"E3.9.1"),sQuery(id+"F0.wireOp",EDGE,"E3.9.2"),sQuery(id+"F0.wireOp",EDGE,"E3.9.3"),sQuery(id+"F0.wireOp",EDGE,"E3.10.1"),sQuery(id+"F0.wireOp",EDGE,"E3.10.2"),sQuery(id+"F0.wireOp",EDGE,"E3.10.3"),sQuery(id+"F0.wireOp",EDGE,"E3.11.1"),sQuery(id+"F0.wireOp",EDGE,"E3.11.2"),sQuery(id+"F0.wireOp",EDGE,"E3.11.3"),sQuery(id+"F0.wireOp",EDGE,"E3.12.1"),sQuery(id+"F0.wireOp",EDGE,"E3.12.2"),sQuery(id+"F0.wireOp",EDGE,"E3.12.3")])],"isStart":true})]}),makeQuery(id+"F1.opExtrude","CAP_EDGE",EDGE,{"disambiguationData":[OSD([subQ0])],"isStart":true})],"blendedInto":[]});}
            var Q65;
            {var subQ0=sQuery(id+"F0.wireOp",EDGE,"E3.6.2");var subQ1=sQuery(id+"F0.wireOp",EDGE,"E3.6.1");Q65=makeQuery(id+"F4.opChamfer","BLEND_EDGE",EDGE,{"blendedFrom":[makeQuery(id+"F3.opChamfer","BLEND_EDGE",EDGE,{"blendedFrom":[makeQuery(id+"F1.opExtrude","SWEPT_EDGE",EDGE,{"disambiguationData":[OSD([subQ1,subQ0])]}),makeQuery(id+"F1.opExtrude","CAP_FACE",FACE,{"disambiguationData":[OSD([sQuery(id+"F0.wireOp",EDGE,"E0"),sQuery(id+"F0.wireOp",EDGE,"E1"),sQuery(id+"F0.wireOp",EDGE,"E2.bottom"),sQuery(id+"F0.wireOp",EDGE,"E2.left"),sQuery(id+"F0.wireOp",EDGE,"E2.right"),sQuery(id+"F0.wireOp",EDGE,"E3.1.1"),sQuery(id+"F0.wireOp",EDGE,"E3.1.2"),sQuery(id+"F0.wireOp",EDGE,"E3.1.3"),sQuery(id+"F0.wireOp",EDGE,"E3.2.1"),sQuery(id+"F0.wireOp",EDGE,"E3.2.2"),sQuery(id+"F0.wireOp",EDGE,"E3.2.3"),sQuery(id+"F0.wireOp",EDGE,"E3.3.1"),sQuery(id+"F0.wireOp",EDGE,"E3.3.2"),sQuery(id+"F0.wireOp",EDGE,"E3.3.3"),sQuery(id+"F0.wireOp",EDGE,"E3.4.1"),sQuery(id+"F0.wireOp",EDGE,"E3.4.2"),sQuery(id+"F0.wireOp",EDGE,"E3.4.3"),sQuery(id+"F0.wireOp",EDGE,"E3.5.1"),sQuery(id+"F0.wireOp",EDGE,"E3.5.2"),sQuery(id+"F0.wireOp",EDGE,"E3.5.3"),subQ1,subQ0,sQuery(id+"F0.wireOp",EDGE,"E3.6.3"),sQuery(id+"F0.wireOp",EDGE,"E3.7.1"),sQuery(id+"F0.wireOp",EDGE,"E3.7.2"),sQuery(id+"F0.wireOp",EDGE,"E3.7.3"),sQuery(id+"F0.wireOp",EDGE,"E3.8.1"),sQuery(id+"F0.wireOp",EDGE,"E3.8.2"),sQuery(id+"F0.wireOp",EDGE,"E3.8.3"),sQuery(id+"F0.wireOp",EDGE,"E3.9.1"),sQuery(id+"F0.wireOp",EDGE,"E3.9.2"),sQuery(id+"F0.wireOp",EDGE,"E3.9.3"),sQuery(id+"F0.wireOp",EDGE,"E3.10.1"),sQuery(id+"F0.wireOp",EDGE,"E3.10.2"),sQuery(id+"F0.wireOp",EDGE,"E3.10.3"),sQuery(id+"F0.wireOp",EDGE,"E3.11.1"),sQuery(id+"F0.wireOp",EDGE,"E3.11.2"),sQuery(id+"F0.wireOp",EDGE,"E3.11.3"),sQuery(id+"F0.wireOp",EDGE,"E3.12.1"),sQuery(id+"F0.wireOp",EDGE,"E3.12.2"),sQuery(id+"F0.wireOp",EDGE,"E3.12.3")])],"isStart":true})],"blendedInto":[makeQuery(id+"F1.opExtrude","CAP_FACE",FACE,{"disambiguationData":[OSD([sQuery(id+"F0.wireOp",EDGE,"E0"),sQuery(id+"F0.wireOp",EDGE,"E1"),sQuery(id+"F0.wireOp",EDGE,"E2.bottom"),sQuery(id+"F0.wireOp",EDGE,"E2.left"),sQuery(id+"F0.wireOp",EDGE,"E2.right"),sQuery(id+"F0.wireOp",EDGE,"E3.1.1"),sQuery(id+"F0.wireOp",EDGE,"E3.1.2"),sQuery(id+"F0.wireOp",EDGE,"E3.1.3"),sQuery(id+"F0.wireOp",EDGE,"E3.2.1"),sQuery(id+"F0.wireOp",EDGE,"E3.2.2"),sQuery(id+"F0.wireOp",EDGE,"E3.2.3"),sQuery(id+"F0.wireOp",EDGE,"E3.3.1"),sQuery(id+"F0.wireOp",EDGE,"E3.3.2"),sQuery(id+"F0.wireOp",EDGE,"E3.3.3"),sQuery(id+"F0.wireOp",EDGE,"E3.4.1"),sQuery(id+"F0.wireOp",EDGE,"E3.4.2"),sQuery(id+"F0.wireOp",EDGE,"E3.4.3"),sQuery(id+"F0.wireOp",EDGE,"E3.5.1"),sQuery(id+"F0.wireOp",EDGE,"E3.5.2"),sQuery(id+"F0.wireOp",EDGE,"E3.5.3"),subQ1,subQ0,sQuery(id+"F0.wireOp",EDGE,"E3.6.3"),sQuery(id+"F0.wireOp",EDGE,"E3.7.1"),sQuery(id+"F0.wireOp",EDGE,"E3.7.2"),sQuery(id+"F0.wireOp",EDGE,"E3.7.3"),sQuery(id+"F0.wireOp",EDGE,"E3.8.1"),sQuery(id+"F0.wireOp",EDGE,"E3.8.2"),sQuery(id+"F0.wireOp",EDGE,"E3.8.3"),sQuery(id+"F0.wireOp",EDGE,"E3.9.1"),sQuery(id+"F0.wireOp",EDGE,"E3.9.2"),sQuery(id+"F0.wireOp",EDGE,"E3.9.3"),sQuery(id+"F0.wireOp",EDGE,"E3.10.1"),sQuery(id+"F0.wireOp",EDGE,"E3.10.2"),sQuery(id+"F0.wireOp",EDGE,"E3.10.3"),sQuery(id+"F0.wireOp",EDGE,"E3.11.1"),sQuery(id+"F0.wireOp",EDGE,"E3.11.2"),sQuery(id+"F0.wireOp",EDGE,"E3.11.3"),sQuery(id+"F0.wireOp",EDGE,"E3.12.1"),sQuery(id+"F0.wireOp",EDGE,"E3.12.2"),sQuery(id+"F0.wireOp",EDGE,"E3.12.3")])],"isStart":true})]}),makeQuery(id+"F1.opExtrude","CAP_EDGE",EDGE,{"disambiguationData":[OSD([subQ0])],"isStart":true})],"blendedInto":[]});}
            var Q66;
            {var subQ0=sQuery(id+"F0.wireOp",EDGE,"E3.5.2");var subQ1=sQuery(id+"F0.wireOp",EDGE,"E3.5.1");Q66=makeQuery(id+"F4.opChamfer","BLEND_EDGE",EDGE,{"blendedFrom":[makeQuery(id+"F3.opChamfer","BLEND_EDGE",EDGE,{"blendedFrom":[makeQuery(id+"F1.opExtrude","SWEPT_EDGE",EDGE,{"disambiguationData":[OSD([subQ1,subQ0])]}),makeQuery(id+"F1.opExtrude","CAP_FACE",FACE,{"disambiguationData":[OSD([sQuery(id+"F0.wireOp",EDGE,"E0"),sQuery(id+"F0.wireOp",EDGE,"E1"),sQuery(id+"F0.wireOp",EDGE,"E2.bottom"),sQuery(id+"F0.wireOp",EDGE,"E2.left"),sQuery(id+"F0.wireOp",EDGE,"E2.right"),sQuery(id+"F0.wireOp",EDGE,"E3.1.1"),sQuery(id+"F0.wireOp",EDGE,"E3.1.2"),sQuery(id+"F0.wireOp",EDGE,"E3.1.3"),sQuery(id+"F0.wireOp",EDGE,"E3.2.1"),sQuery(id+"F0.wireOp",EDGE,"E3.2.2"),sQuery(id+"F0.wireOp",EDGE,"E3.2.3"),sQuery(id+"F0.wireOp",EDGE,"E3.3.1"),sQuery(id+"F0.wireOp",EDGE,"E3.3.2"),sQuery(id+"F0.wireOp",EDGE,"E3.3.3"),sQuery(id+"F0.wireOp",EDGE,"E3.4.1"),sQuery(id+"F0.wireOp",EDGE,"E3.4.2"),sQuery(id+"F0.wireOp",EDGE,"E3.4.3"),subQ1,subQ0,sQuery(id+"F0.wireOp",EDGE,"E3.5.3"),sQuery(id+"F0.wireOp",EDGE,"E3.6.1"),sQuery(id+"F0.wireOp",EDGE,"E3.6.2"),sQuery(id+"F0.wireOp",EDGE,"E3.6.3"),sQuery(id+"F0.wireOp",EDGE,"E3.7.1"),sQuery(id+"F0.wireOp",EDGE,"E3.7.2"),sQuery(id+"F0.wireOp",EDGE,"E3.7.3"),sQuery(id+"F0.wireOp",EDGE,"E3.8.1"),sQuery(id+"F0.wireOp",EDGE,"E3.8.2"),sQuery(id+"F0.wireOp",EDGE,"E3.8.3"),sQuery(id+"F0.wireOp",EDGE,"E3.9.1"),sQuery(id+"F0.wireOp",EDGE,"E3.9.2"),sQuery(id+"F0.wireOp",EDGE,"E3.9.3"),sQuery(id+"F0.wireOp",EDGE,"E3.10.1"),sQuery(id+"F0.wireOp",EDGE,"E3.10.2"),sQuery(id+"F0.wireOp",EDGE,"E3.10.3"),sQuery(id+"F0.wireOp",EDGE,"E3.11.1"),sQuery(id+"F0.wireOp",EDGE,"E3.11.2"),sQuery(id+"F0.wireOp",EDGE,"E3.11.3"),sQuery(id+"F0.wireOp",EDGE,"E3.12.1"),sQuery(id+"F0.wireOp",EDGE,"E3.12.2"),sQuery(id+"F0.wireOp",EDGE,"E3.12.3")])],"isStart":true})],"blendedInto":[makeQuery(id+"F1.opExtrude","CAP_FACE",FACE,{"disambiguationData":[OSD([sQuery(id+"F0.wireOp",EDGE,"E0"),sQuery(id+"F0.wireOp",EDGE,"E1"),sQuery(id+"F0.wireOp",EDGE,"E2.bottom"),sQuery(id+"F0.wireOp",EDGE,"E2.left"),sQuery(id+"F0.wireOp",EDGE,"E2.right"),sQuery(id+"F0.wireOp",EDGE,"E3.1.1"),sQuery(id+"F0.wireOp",EDGE,"E3.1.2"),sQuery(id+"F0.wireOp",EDGE,"E3.1.3"),sQuery(id+"F0.wireOp",EDGE,"E3.2.1"),sQuery(id+"F0.wireOp",EDGE,"E3.2.2"),sQuery(id+"F0.wireOp",EDGE,"E3.2.3"),sQuery(id+"F0.wireOp",EDGE,"E3.3.1"),sQuery(id+"F0.wireOp",EDGE,"E3.3.2"),sQuery(id+"F0.wireOp",EDGE,"E3.3.3"),sQuery(id+"F0.wireOp",EDGE,"E3.4.1"),sQuery(id+"F0.wireOp",EDGE,"E3.4.2"),sQuery(id+"F0.wireOp",EDGE,"E3.4.3"),subQ1,subQ0,sQuery(id+"F0.wireOp",EDGE,"E3.5.3"),sQuery(id+"F0.wireOp",EDGE,"E3.6.1"),sQuery(id+"F0.wireOp",EDGE,"E3.6.2"),sQuery(id+"F0.wireOp",EDGE,"E3.6.3"),sQuery(id+"F0.wireOp",EDGE,"E3.7.1"),sQuery(id+"F0.wireOp",EDGE,"E3.7.2"),sQuery(id+"F0.wireOp",EDGE,"E3.7.3"),sQuery(id+"F0.wireOp",EDGE,"E3.8.1"),sQuery(id+"F0.wireOp",EDGE,"E3.8.2"),sQuery(id+"F0.wireOp",EDGE,"E3.8.3"),sQuery(id+"F0.wireOp",EDGE,"E3.9.1"),sQuery(id+"F0.wireOp",EDGE,"E3.9.2"),sQuery(id+"F0.wireOp",EDGE,"E3.9.3"),sQuery(id+"F0.wireOp",EDGE,"E3.10.1"),sQuery(id+"F0.wireOp",EDGE,"E3.10.2"),sQuery(id+"F0.wireOp",EDGE,"E3.10.3"),sQuery(id+"F0.wireOp",EDGE,"E3.11.1"),sQuery(id+"F0.wireOp",EDGE,"E3.11.2"),sQuery(id+"F0.wireOp",EDGE,"E3.11.3"),sQuery(id+"F0.wireOp",EDGE,"E3.12.1"),sQuery(id+"F0.wireOp",EDGE,"E3.12.2"),sQuery(id+"F0.wireOp",EDGE,"E3.12.3")])],"isStart":true})]}),makeQuery(id+"F1.opExtrude","CAP_EDGE",EDGE,{"disambiguationData":[OSD([subQ0])],"isStart":true})],"blendedInto":[]});}
            var Q67;
            {var subQ0=sQuery(id+"F0.wireOp",EDGE,"E3.5.2");var subQ1=sQuery(id+"F0.wireOp",EDGE,"E3.5.3");Q67=makeQuery(id+"F4.opChamfer","BLEND_EDGE",EDGE,{"blendedFrom":[makeQuery(id+"F3.opChamfer","BLEND_EDGE",EDGE,{"blendedFrom":[makeQuery(id+"F1.opExtrude","SWEPT_EDGE",EDGE,{"disambiguationData":[OSD([subQ0,subQ1])]}),makeQuery(id+"F1.opExtrude","CAP_FACE",FACE,{"disambiguationData":[OSD([sQuery(id+"F0.wireOp",EDGE,"E0"),sQuery(id+"F0.wireOp",EDGE,"E1"),sQuery(id+"F0.wireOp",EDGE,"E2.bottom"),sQuery(id+"F0.wireOp",EDGE,"E2.left"),sQuery(id+"F0.wireOp",EDGE,"E2.right"),sQuery(id+"F0.wireOp",EDGE,"E3.1.1"),sQuery(id+"F0.wireOp",EDGE,"E3.1.2"),sQuery(id+"F0.wireOp",EDGE,"E3.1.3"),sQuery(id+"F0.wireOp",EDGE,"E3.2.1"),sQuery(id+"F0.wireOp",EDGE,"E3.2.2"),sQuery(id+"F0.wireOp",EDGE,"E3.2.3"),sQuery(id+"F0.wireOp",EDGE,"E3.3.1"),sQuery(id+"F0.wireOp",EDGE,"E3.3.2"),sQuery(id+"F0.wireOp",EDGE,"E3.3.3"),sQuery(id+"F0.wireOp",EDGE,"E3.4.1"),sQuery(id+"F0.wireOp",EDGE,"E3.4.2"),sQuery(id+"F0.wireOp",EDGE,"E3.4.3"),sQuery(id+"F0.wireOp",EDGE,"E3.5.1"),subQ0,subQ1,sQuery(id+"F0.wireOp",EDGE,"E3.6.1"),sQuery(id+"F0.wireOp",EDGE,"E3.6.2"),sQuery(id+"F0.wireOp",EDGE,"E3.6.3"),sQuery(id+"F0.wireOp",EDGE,"E3.7.1"),sQuery(id+"F0.wireOp",EDGE,"E3.7.2"),sQuery(id+"F0.wireOp",EDGE,"E3.7.3"),sQuery(id+"F0.wireOp",EDGE,"E3.8.1"),sQuery(id+"F0.wireOp",EDGE,"E3.8.2"),sQuery(id+"F0.wireOp",EDGE,"E3.8.3"),sQuery(id+"F0.wireOp",EDGE,"E3.9.1"),sQuery(id+"F0.wireOp",EDGE,"E3.9.2"),sQuery(id+"F0.wireOp",EDGE,"E3.9.3"),sQuery(id+"F0.wireOp",EDGE,"E3.10.1"),sQuery(id+"F0.wireOp",EDGE,"E3.10.2"),sQuery(id+"F0.wireOp",EDGE,"E3.10.3"),sQuery(id+"F0.wireOp",EDGE,"E3.11.1"),sQuery(id+"F0.wireOp",EDGE,"E3.11.2"),sQuery(id+"F0.wireOp",EDGE,"E3.11.3"),sQuery(id+"F0.wireOp",EDGE,"E3.12.1"),sQuery(id+"F0.wireOp",EDGE,"E3.12.2"),sQuery(id+"F0.wireOp",EDGE,"E3.12.3")])],"isStart":true})],"blendedInto":[makeQuery(id+"F1.opExtrude","CAP_FACE",FACE,{"disambiguationData":[OSD([sQuery(id+"F0.wireOp",EDGE,"E0"),sQuery(id+"F0.wireOp",EDGE,"E1"),sQuery(id+"F0.wireOp",EDGE,"E2.bottom"),sQuery(id+"F0.wireOp",EDGE,"E2.left"),sQuery(id+"F0.wireOp",EDGE,"E2.right"),sQuery(id+"F0.wireOp",EDGE,"E3.1.1"),sQuery(id+"F0.wireOp",EDGE,"E3.1.2"),sQuery(id+"F0.wireOp",EDGE,"E3.1.3"),sQuery(id+"F0.wireOp",EDGE,"E3.2.1"),sQuery(id+"F0.wireOp",EDGE,"E3.2.2"),sQuery(id+"F0.wireOp",EDGE,"E3.2.3"),sQuery(id+"F0.wireOp",EDGE,"E3.3.1"),sQuery(id+"F0.wireOp",EDGE,"E3.3.2"),sQuery(id+"F0.wireOp",EDGE,"E3.3.3"),sQuery(id+"F0.wireOp",EDGE,"E3.4.1"),sQuery(id+"F0.wireOp",EDGE,"E3.4.2"),sQuery(id+"F0.wireOp",EDGE,"E3.4.3"),sQuery(id+"F0.wireOp",EDGE,"E3.5.1"),subQ0,subQ1,sQuery(id+"F0.wireOp",EDGE,"E3.6.1"),sQuery(id+"F0.wireOp",EDGE,"E3.6.2"),sQuery(id+"F0.wireOp",EDGE,"E3.6.3"),sQuery(id+"F0.wireOp",EDGE,"E3.7.1"),sQuery(id+"F0.wireOp",EDGE,"E3.7.2"),sQuery(id+"F0.wireOp",EDGE,"E3.7.3"),sQuery(id+"F0.wireOp",EDGE,"E3.8.1"),sQuery(id+"F0.wireOp",EDGE,"E3.8.2"),sQuery(id+"F0.wireOp",EDGE,"E3.8.3"),sQuery(id+"F0.wireOp",EDGE,"E3.9.1"),sQuery(id+"F0.wireOp",EDGE,"E3.9.2"),sQuery(id+"F0.wireOp",EDGE,"E3.9.3"),sQuery(id+"F0.wireOp",EDGE,"E3.10.1"),sQuery(id+"F0.wireOp",EDGE,"E3.10.2"),sQuery(id+"F0.wireOp",EDGE,"E3.10.3"),sQuery(id+"F0.wireOp",EDGE,"E3.11.1"),sQuery(id+"F0.wireOp",EDGE,"E3.11.2"),sQuery(id+"F0.wireOp",EDGE,"E3.11.3"),sQuery(id+"F0.wireOp",EDGE,"E3.12.1"),sQuery(id+"F0.wireOp",EDGE,"E3.12.2"),sQuery(id+"F0.wireOp",EDGE,"E3.12.3")])],"isStart":true})]}),makeQuery(id+"F1.opExtrude","CAP_EDGE",EDGE,{"disambiguationData":[OSD([subQ0])],"isStart":true})],"blendedInto":[]});}
            var Q68;
            {var subQ0=sQuery(id+"F0.wireOp",EDGE,"E3.4.2");var subQ1=sQuery(id+"F0.wireOp",EDGE,"E3.4.3");Q68=makeQuery(id+"F4.opChamfer","BLEND_EDGE",EDGE,{"blendedFrom":[makeQuery(id+"F3.opChamfer","BLEND_EDGE",EDGE,{"blendedFrom":[makeQuery(id+"F1.opExtrude","SWEPT_EDGE",EDGE,{"disambiguationData":[OSD([subQ0,subQ1])]}),makeQuery(id+"F1.opExtrude","CAP_FACE",FACE,{"disambiguationData":[OSD([sQuery(id+"F0.wireOp",EDGE,"E0"),sQuery(id+"F0.wireOp",EDGE,"E1"),sQuery(id+"F0.wireOp",EDGE,"E2.bottom"),sQuery(id+"F0.wireOp",EDGE,"E2.left"),sQuery(id+"F0.wireOp",EDGE,"E2.right"),sQuery(id+"F0.wireOp",EDGE,"E3.1.1"),sQuery(id+"F0.wireOp",EDGE,"E3.1.2"),sQuery(id+"F0.wireOp",EDGE,"E3.1.3"),sQuery(id+"F0.wireOp",EDGE,"E3.2.1"),sQuery(id+"F0.wireOp",EDGE,"E3.2.2"),sQuery(id+"F0.wireOp",EDGE,"E3.2.3"),sQuery(id+"F0.wireOp",EDGE,"E3.3.1"),sQuery(id+"F0.wireOp",EDGE,"E3.3.2"),sQuery(id+"F0.wireOp",EDGE,"E3.3.3"),sQuery(id+"F0.wireOp",EDGE,"E3.4.1"),subQ0,subQ1,sQuery(id+"F0.wireOp",EDGE,"E3.5.1"),sQuery(id+"F0.wireOp",EDGE,"E3.5.2"),sQuery(id+"F0.wireOp",EDGE,"E3.5.3"),sQuery(id+"F0.wireOp",EDGE,"E3.6.1"),sQuery(id+"F0.wireOp",EDGE,"E3.6.2"),sQuery(id+"F0.wireOp",EDGE,"E3.6.3"),sQuery(id+"F0.wireOp",EDGE,"E3.7.1"),sQuery(id+"F0.wireOp",EDGE,"E3.7.2"),sQuery(id+"F0.wireOp",EDGE,"E3.7.3"),sQuery(id+"F0.wireOp",EDGE,"E3.8.1"),sQuery(id+"F0.wireOp",EDGE,"E3.8.2"),sQuery(id+"F0.wireOp",EDGE,"E3.8.3"),sQuery(id+"F0.wireOp",EDGE,"E3.9.1"),sQuery(id+"F0.wireOp",EDGE,"E3.9.2"),sQuery(id+"F0.wireOp",EDGE,"E3.9.3"),sQuery(id+"F0.wireOp",EDGE,"E3.10.1"),sQuery(id+"F0.wireOp",EDGE,"E3.10.2"),sQuery(id+"F0.wireOp",EDGE,"E3.10.3"),sQuery(id+"F0.wireOp",EDGE,"E3.11.1"),sQuery(id+"F0.wireOp",EDGE,"E3.11.2"),sQuery(id+"F0.wireOp",EDGE,"E3.11.3"),sQuery(id+"F0.wireOp",EDGE,"E3.12.1"),sQuery(id+"F0.wireOp",EDGE,"E3.12.2"),sQuery(id+"F0.wireOp",EDGE,"E3.12.3")])],"isStart":true})],"blendedInto":[makeQuery(id+"F1.opExtrude","CAP_FACE",FACE,{"disambiguationData":[OSD([sQuery(id+"F0.wireOp",EDGE,"E0"),sQuery(id+"F0.wireOp",EDGE,"E1"),sQuery(id+"F0.wireOp",EDGE,"E2.bottom"),sQuery(id+"F0.wireOp",EDGE,"E2.left"),sQuery(id+"F0.wireOp",EDGE,"E2.right"),sQuery(id+"F0.wireOp",EDGE,"E3.1.1"),sQuery(id+"F0.wireOp",EDGE,"E3.1.2"),sQuery(id+"F0.wireOp",EDGE,"E3.1.3"),sQuery(id+"F0.wireOp",EDGE,"E3.2.1"),sQuery(id+"F0.wireOp",EDGE,"E3.2.2"),sQuery(id+"F0.wireOp",EDGE,"E3.2.3"),sQuery(id+"F0.wireOp",EDGE,"E3.3.1"),sQuery(id+"F0.wireOp",EDGE,"E3.3.2"),sQuery(id+"F0.wireOp",EDGE,"E3.3.3"),sQuery(id+"F0.wireOp",EDGE,"E3.4.1"),subQ0,subQ1,sQuery(id+"F0.wireOp",EDGE,"E3.5.1"),sQuery(id+"F0.wireOp",EDGE,"E3.5.2"),sQuery(id+"F0.wireOp",EDGE,"E3.5.3"),sQuery(id+"F0.wireOp",EDGE,"E3.6.1"),sQuery(id+"F0.wireOp",EDGE,"E3.6.2"),sQuery(id+"F0.wireOp",EDGE,"E3.6.3"),sQuery(id+"F0.wireOp",EDGE,"E3.7.1"),sQuery(id+"F0.wireOp",EDGE,"E3.7.2"),sQuery(id+"F0.wireOp",EDGE,"E3.7.3"),sQuery(id+"F0.wireOp",EDGE,"E3.8.1"),sQuery(id+"F0.wireOp",EDGE,"E3.8.2"),sQuery(id+"F0.wireOp",EDGE,"E3.8.3"),sQuery(id+"F0.wireOp",EDGE,"E3.9.1"),sQuery(id+"F0.wireOp",EDGE,"E3.9.2"),sQuery(id+"F0.wireOp",EDGE,"E3.9.3"),sQuery(id+"F0.wireOp",EDGE,"E3.10.1"),sQuery(id+"F0.wireOp",EDGE,"E3.10.2"),sQuery(id+"F0.wireOp",EDGE,"E3.10.3"),sQuery(id+"F0.wireOp",EDGE,"E3.11.1"),sQuery(id+"F0.wireOp",EDGE,"E3.11.2"),sQuery(id+"F0.wireOp",EDGE,"E3.11.3"),sQuery(id+"F0.wireOp",EDGE,"E3.12.1"),sQuery(id+"F0.wireOp",EDGE,"E3.12.2"),sQuery(id+"F0.wireOp",EDGE,"E3.12.3")])],"isStart":true})]}),makeQuery(id+"F1.opExtrude","CAP_EDGE",EDGE,{"disambiguationData":[OSD([subQ0])],"isStart":true})],"blendedInto":[]});}
            var Q69;
            {var subQ0=sQuery(id+"F0.wireOp",EDGE,"E3.4.2");var subQ1=sQuery(id+"F0.wireOp",EDGE,"E3.4.1");Q69=makeQuery(id+"F4.opChamfer","BLEND_EDGE",EDGE,{"blendedFrom":[makeQuery(id+"F3.opChamfer","BLEND_EDGE",EDGE,{"blendedFrom":[makeQuery(id+"F1.opExtrude","SWEPT_EDGE",EDGE,{"disambiguationData":[OSD([subQ1,subQ0])]}),makeQuery(id+"F1.opExtrude","CAP_FACE",FACE,{"disambiguationData":[OSD([sQuery(id+"F0.wireOp",EDGE,"E0"),sQuery(id+"F0.wireOp",EDGE,"E1"),sQuery(id+"F0.wireOp",EDGE,"E2.bottom"),sQuery(id+"F0.wireOp",EDGE,"E2.left"),sQuery(id+"F0.wireOp",EDGE,"E2.right"),sQuery(id+"F0.wireOp",EDGE,"E3.1.1"),sQuery(id+"F0.wireOp",EDGE,"E3.1.2"),sQuery(id+"F0.wireOp",EDGE,"E3.1.3"),sQuery(id+"F0.wireOp",EDGE,"E3.2.1"),sQuery(id+"F0.wireOp",EDGE,"E3.2.2"),sQuery(id+"F0.wireOp",EDGE,"E3.2.3"),sQuery(id+"F0.wireOp",EDGE,"E3.3.1"),sQuery(id+"F0.wireOp",EDGE,"E3.3.2"),sQuery(id+"F0.wireOp",EDGE,"E3.3.3"),subQ1,subQ0,sQuery(id+"F0.wireOp",EDGE,"E3.4.3"),sQuery(id+"F0.wireOp",EDGE,"E3.5.1"),sQuery(id+"F0.wireOp",EDGE,"E3.5.2"),sQuery(id+"F0.wireOp",EDGE,"E3.5.3"),sQuery(id+"F0.wireOp",EDGE,"E3.6.1"),sQuery(id+"F0.wireOp",EDGE,"E3.6.2"),sQuery(id+"F0.wireOp",EDGE,"E3.6.3"),sQuery(id+"F0.wireOp",EDGE,"E3.7.1"),sQuery(id+"F0.wireOp",EDGE,"E3.7.2"),sQuery(id+"F0.wireOp",EDGE,"E3.7.3"),sQuery(id+"F0.wireOp",EDGE,"E3.8.1"),sQuery(id+"F0.wireOp",EDGE,"E3.8.2"),sQuery(id+"F0.wireOp",EDGE,"E3.8.3"),sQuery(id+"F0.wireOp",EDGE,"E3.9.1"),sQuery(id+"F0.wireOp",EDGE,"E3.9.2"),sQuery(id+"F0.wireOp",EDGE,"E3.9.3"),sQuery(id+"F0.wireOp",EDGE,"E3.10.1"),sQuery(id+"F0.wireOp",EDGE,"E3.10.2"),sQuery(id+"F0.wireOp",EDGE,"E3.10.3"),sQuery(id+"F0.wireOp",EDGE,"E3.11.1"),sQuery(id+"F0.wireOp",EDGE,"E3.11.2"),sQuery(id+"F0.wireOp",EDGE,"E3.11.3"),sQuery(id+"F0.wireOp",EDGE,"E3.12.1"),sQuery(id+"F0.wireOp",EDGE,"E3.12.2"),sQuery(id+"F0.wireOp",EDGE,"E3.12.3")])],"isStart":true})],"blendedInto":[makeQuery(id+"F1.opExtrude","CAP_FACE",FACE,{"disambiguationData":[OSD([sQuery(id+"F0.wireOp",EDGE,"E0"),sQuery(id+"F0.wireOp",EDGE,"E1"),sQuery(id+"F0.wireOp",EDGE,"E2.bottom"),sQuery(id+"F0.wireOp",EDGE,"E2.left"),sQuery(id+"F0.wireOp",EDGE,"E2.right"),sQuery(id+"F0.wireOp",EDGE,"E3.1.1"),sQuery(id+"F0.wireOp",EDGE,"E3.1.2"),sQuery(id+"F0.wireOp",EDGE,"E3.1.3"),sQuery(id+"F0.wireOp",EDGE,"E3.2.1"),sQuery(id+"F0.wireOp",EDGE,"E3.2.2"),sQuery(id+"F0.wireOp",EDGE,"E3.2.3"),sQuery(id+"F0.wireOp",EDGE,"E3.3.1"),sQuery(id+"F0.wireOp",EDGE,"E3.3.2"),sQuery(id+"F0.wireOp",EDGE,"E3.3.3"),subQ1,subQ0,sQuery(id+"F0.wireOp",EDGE,"E3.4.3"),sQuery(id+"F0.wireOp",EDGE,"E3.5.1"),sQuery(id+"F0.wireOp",EDGE,"E3.5.2"),sQuery(id+"F0.wireOp",EDGE,"E3.5.3"),sQuery(id+"F0.wireOp",EDGE,"E3.6.1"),sQuery(id+"F0.wireOp",EDGE,"E3.6.2"),sQuery(id+"F0.wireOp",EDGE,"E3.6.3"),sQuery(id+"F0.wireOp",EDGE,"E3.7.1"),sQuery(id+"F0.wireOp",EDGE,"E3.7.2"),sQuery(id+"F0.wireOp",EDGE,"E3.7.3"),sQuery(id+"F0.wireOp",EDGE,"E3.8.1"),sQuery(id+"F0.wireOp",EDGE,"E3.8.2"),sQuery(id+"F0.wireOp",EDGE,"E3.8.3"),sQuery(id+"F0.wireOp",EDGE,"E3.9.1"),sQuery(id+"F0.wireOp",EDGE,"E3.9.2"),sQuery(id+"F0.wireOp",EDGE,"E3.9.3"),sQuery(id+"F0.wireOp",EDGE,"E3.10.1"),sQuery(id+"F0.wireOp",EDGE,"E3.10.2"),sQuery(id+"F0.wireOp",EDGE,"E3.10.3"),sQuery(id+"F0.wireOp",EDGE,"E3.11.1"),sQuery(id+"F0.wireOp",EDGE,"E3.11.2"),sQuery(id+"F0.wireOp",EDGE,"E3.11.3"),sQuery(id+"F0.wireOp",EDGE,"E3.12.1"),sQuery(id+"F0.wireOp",EDGE,"E3.12.2"),sQuery(id+"F0.wireOp",EDGE,"E3.12.3")])],"isStart":true})]}),makeQuery(id+"F1.opExtrude","CAP_EDGE",EDGE,{"disambiguationData":[OSD([subQ0])],"isStart":true})],"blendedInto":[]});}
            var Q70;
            {var subQ0=sQuery(id+"F0.wireOp",EDGE,"E3.3.2");var subQ1=sQuery(id+"F0.wireOp",EDGE,"E3.3.3");Q70=makeQuery(id+"F4.opChamfer","BLEND_EDGE",EDGE,{"blendedFrom":[makeQuery(id+"F3.opChamfer","BLEND_EDGE",EDGE,{"blendedFrom":[makeQuery(id+"F1.opExtrude","SWEPT_EDGE",EDGE,{"disambiguationData":[OSD([subQ0,subQ1])]}),makeQuery(id+"F1.opExtrude","CAP_FACE",FACE,{"disambiguationData":[OSD([sQuery(id+"F0.wireOp",EDGE,"E0"),sQuery(id+"F0.wireOp",EDGE,"E1"),sQuery(id+"F0.wireOp",EDGE,"E2.bottom"),sQuery(id+"F0.wireOp",EDGE,"E2.left"),sQuery(id+"F0.wireOp",EDGE,"E2.right"),sQuery(id+"F0.wireOp",EDGE,"E3.1.1"),sQuery(id+"F0.wireOp",EDGE,"E3.1.2"),sQuery(id+"F0.wireOp",EDGE,"E3.1.3"),sQuery(id+"F0.wireOp",EDGE,"E3.2.1"),sQuery(id+"F0.wireOp",EDGE,"E3.2.2"),sQuery(id+"F0.wireOp",EDGE,"E3.2.3"),sQuery(id+"F0.wireOp",EDGE,"E3.3.1"),subQ0,subQ1,sQuery(id+"F0.wireOp",EDGE,"E3.4.1"),sQuery(id+"F0.wireOp",EDGE,"E3.4.2"),sQuery(id+"F0.wireOp",EDGE,"E3.4.3"),sQuery(id+"F0.wireOp",EDGE,"E3.5.1"),sQuery(id+"F0.wireOp",EDGE,"E3.5.2"),sQuery(id+"F0.wireOp",EDGE,"E3.5.3"),sQuery(id+"F0.wireOp",EDGE,"E3.6.1"),sQuery(id+"F0.wireOp",EDGE,"E3.6.2"),sQuery(id+"F0.wireOp",EDGE,"E3.6.3"),sQuery(id+"F0.wireOp",EDGE,"E3.7.1"),sQuery(id+"F0.wireOp",EDGE,"E3.7.2"),sQuery(id+"F0.wireOp",EDGE,"E3.7.3"),sQuery(id+"F0.wireOp",EDGE,"E3.8.1"),sQuery(id+"F0.wireOp",EDGE,"E3.8.2"),sQuery(id+"F0.wireOp",EDGE,"E3.8.3"),sQuery(id+"F0.wireOp",EDGE,"E3.9.1"),sQuery(id+"F0.wireOp",EDGE,"E3.9.2"),sQuery(id+"F0.wireOp",EDGE,"E3.9.3"),sQuery(id+"F0.wireOp",EDGE,"E3.10.1"),sQuery(id+"F0.wireOp",EDGE,"E3.10.2"),sQuery(id+"F0.wireOp",EDGE,"E3.10.3"),sQuery(id+"F0.wireOp",EDGE,"E3.11.1"),sQuery(id+"F0.wireOp",EDGE,"E3.11.2"),sQuery(id+"F0.wireOp",EDGE,"E3.11.3"),sQuery(id+"F0.wireOp",EDGE,"E3.12.1"),sQuery(id+"F0.wireOp",EDGE,"E3.12.2"),sQuery(id+"F0.wireOp",EDGE,"E3.12.3")])],"isStart":true})],"blendedInto":[makeQuery(id+"F1.opExtrude","CAP_FACE",FACE,{"disambiguationData":[OSD([sQuery(id+"F0.wireOp",EDGE,"E0"),sQuery(id+"F0.wireOp",EDGE,"E1"),sQuery(id+"F0.wireOp",EDGE,"E2.bottom"),sQuery(id+"F0.wireOp",EDGE,"E2.left"),sQuery(id+"F0.wireOp",EDGE,"E2.right"),sQuery(id+"F0.wireOp",EDGE,"E3.1.1"),sQuery(id+"F0.wireOp",EDGE,"E3.1.2"),sQuery(id+"F0.wireOp",EDGE,"E3.1.3"),sQuery(id+"F0.wireOp",EDGE,"E3.2.1"),sQuery(id+"F0.wireOp",EDGE,"E3.2.2"),sQuery(id+"F0.wireOp",EDGE,"E3.2.3"),sQuery(id+"F0.wireOp",EDGE,"E3.3.1"),subQ0,subQ1,sQuery(id+"F0.wireOp",EDGE,"E3.4.1"),sQuery(id+"F0.wireOp",EDGE,"E3.4.2"),sQuery(id+"F0.wireOp",EDGE,"E3.4.3"),sQuery(id+"F0.wireOp",EDGE,"E3.5.1"),sQuery(id+"F0.wireOp",EDGE,"E3.5.2"),sQuery(id+"F0.wireOp",EDGE,"E3.5.3"),sQuery(id+"F0.wireOp",EDGE,"E3.6.1"),sQuery(id+"F0.wireOp",EDGE,"E3.6.2"),sQuery(id+"F0.wireOp",EDGE,"E3.6.3"),sQuery(id+"F0.wireOp",EDGE,"E3.7.1"),sQuery(id+"F0.wireOp",EDGE,"E3.7.2"),sQuery(id+"F0.wireOp",EDGE,"E3.7.3"),sQuery(id+"F0.wireOp",EDGE,"E3.8.1"),sQuery(id+"F0.wireOp",EDGE,"E3.8.2"),sQuery(id+"F0.wireOp",EDGE,"E3.8.3"),sQuery(id+"F0.wireOp",EDGE,"E3.9.1"),sQuery(id+"F0.wireOp",EDGE,"E3.9.2"),sQuery(id+"F0.wireOp",EDGE,"E3.9.3"),sQuery(id+"F0.wireOp",EDGE,"E3.10.1"),sQuery(id+"F0.wireOp",EDGE,"E3.10.2"),sQuery(id+"F0.wireOp",EDGE,"E3.10.3"),sQuery(id+"F0.wireOp",EDGE,"E3.11.1"),sQuery(id+"F0.wireOp",EDGE,"E3.11.2"),sQuery(id+"F0.wireOp",EDGE,"E3.11.3"),sQuery(id+"F0.wireOp",EDGE,"E3.12.1"),sQuery(id+"F0.wireOp",EDGE,"E3.12.2"),sQuery(id+"F0.wireOp",EDGE,"E3.12.3")])],"isStart":true})]}),makeQuery(id+"F1.opExtrude","CAP_EDGE",EDGE,{"disambiguationData":[OSD([subQ0])],"isStart":true})],"blendedInto":[]});}
            var Q71;
            {var subQ0=sQuery(id+"F0.wireOp",EDGE,"E3.3.2");var subQ1=sQuery(id+"F0.wireOp",EDGE,"E3.3.1");Q71=makeQuery(id+"F4.opChamfer","BLEND_EDGE",EDGE,{"blendedFrom":[makeQuery(id+"F3.opChamfer","BLEND_EDGE",EDGE,{"blendedFrom":[makeQuery(id+"F1.opExtrude","SWEPT_EDGE",EDGE,{"disambiguationData":[OSD([subQ1,subQ0])]}),makeQuery(id+"F1.opExtrude","CAP_FACE",FACE,{"disambiguationData":[OSD([sQuery(id+"F0.wireOp",EDGE,"E0"),sQuery(id+"F0.wireOp",EDGE,"E1"),sQuery(id+"F0.wireOp",EDGE,"E2.bottom"),sQuery(id+"F0.wireOp",EDGE,"E2.left"),sQuery(id+"F0.wireOp",EDGE,"E2.right"),sQuery(id+"F0.wireOp",EDGE,"E3.1.1"),sQuery(id+"F0.wireOp",EDGE,"E3.1.2"),sQuery(id+"F0.wireOp",EDGE,"E3.1.3"),sQuery(id+"F0.wireOp",EDGE,"E3.2.1"),sQuery(id+"F0.wireOp",EDGE,"E3.2.2"),sQuery(id+"F0.wireOp",EDGE,"E3.2.3"),subQ1,subQ0,sQuery(id+"F0.wireOp",EDGE,"E3.3.3"),sQuery(id+"F0.wireOp",EDGE,"E3.4.1"),sQuery(id+"F0.wireOp",EDGE,"E3.4.2"),sQuery(id+"F0.wireOp",EDGE,"E3.4.3"),sQuery(id+"F0.wireOp",EDGE,"E3.5.1"),sQuery(id+"F0.wireOp",EDGE,"E3.5.2"),sQuery(id+"F0.wireOp",EDGE,"E3.5.3"),sQuery(id+"F0.wireOp",EDGE,"E3.6.1"),sQuery(id+"F0.wireOp",EDGE,"E3.6.2"),sQuery(id+"F0.wireOp",EDGE,"E3.6.3"),sQuery(id+"F0.wireOp",EDGE,"E3.7.1"),sQuery(id+"F0.wireOp",EDGE,"E3.7.2"),sQuery(id+"F0.wireOp",EDGE,"E3.7.3"),sQuery(id+"F0.wireOp",EDGE,"E3.8.1"),sQuery(id+"F0.wireOp",EDGE,"E3.8.2"),sQuery(id+"F0.wireOp",EDGE,"E3.8.3"),sQuery(id+"F0.wireOp",EDGE,"E3.9.1"),sQuery(id+"F0.wireOp",EDGE,"E3.9.2"),sQuery(id+"F0.wireOp",EDGE,"E3.9.3"),sQuery(id+"F0.wireOp",EDGE,"E3.10.1"),sQuery(id+"F0.wireOp",EDGE,"E3.10.2"),sQuery(id+"F0.wireOp",EDGE,"E3.10.3"),sQuery(id+"F0.wireOp",EDGE,"E3.11.1"),sQuery(id+"F0.wireOp",EDGE,"E3.11.2"),sQuery(id+"F0.wireOp",EDGE,"E3.11.3"),sQuery(id+"F0.wireOp",EDGE,"E3.12.1"),sQuery(id+"F0.wireOp",EDGE,"E3.12.2"),sQuery(id+"F0.wireOp",EDGE,"E3.12.3")])],"isStart":true})],"blendedInto":[makeQuery(id+"F1.opExtrude","CAP_FACE",FACE,{"disambiguationData":[OSD([sQuery(id+"F0.wireOp",EDGE,"E0"),sQuery(id+"F0.wireOp",EDGE,"E1"),sQuery(id+"F0.wireOp",EDGE,"E2.bottom"),sQuery(id+"F0.wireOp",EDGE,"E2.left"),sQuery(id+"F0.wireOp",EDGE,"E2.right"),sQuery(id+"F0.wireOp",EDGE,"E3.1.1"),sQuery(id+"F0.wireOp",EDGE,"E3.1.2"),sQuery(id+"F0.wireOp",EDGE,"E3.1.3"),sQuery(id+"F0.wireOp",EDGE,"E3.2.1"),sQuery(id+"F0.wireOp",EDGE,"E3.2.2"),sQuery(id+"F0.wireOp",EDGE,"E3.2.3"),subQ1,subQ0,sQuery(id+"F0.wireOp",EDGE,"E3.3.3"),sQuery(id+"F0.wireOp",EDGE,"E3.4.1"),sQuery(id+"F0.wireOp",EDGE,"E3.4.2"),sQuery(id+"F0.wireOp",EDGE,"E3.4.3"),sQuery(id+"F0.wireOp",EDGE,"E3.5.1"),sQuery(id+"F0.wireOp",EDGE,"E3.5.2"),sQuery(id+"F0.wireOp",EDGE,"E3.5.3"),sQuery(id+"F0.wireOp",EDGE,"E3.6.1"),sQuery(id+"F0.wireOp",EDGE,"E3.6.2"),sQuery(id+"F0.wireOp",EDGE,"E3.6.3"),sQuery(id+"F0.wireOp",EDGE,"E3.7.1"),sQuery(id+"F0.wireOp",EDGE,"E3.7.2"),sQuery(id+"F0.wireOp",EDGE,"E3.7.3"),sQuery(id+"F0.wireOp",EDGE,"E3.8.1"),sQuery(id+"F0.wireOp",EDGE,"E3.8.2"),sQuery(id+"F0.wireOp",EDGE,"E3.8.3"),sQuery(id+"F0.wireOp",EDGE,"E3.9.1"),sQuery(id+"F0.wireOp",EDGE,"E3.9.2"),sQuery(id+"F0.wireOp",EDGE,"E3.9.3"),sQuery(id+"F0.wireOp",EDGE,"E3.10.1"),sQuery(id+"F0.wireOp",EDGE,"E3.10.2"),sQuery(id+"F0.wireOp",EDGE,"E3.10.3"),sQuery(id+"F0.wireOp",EDGE,"E3.11.1"),sQuery(id+"F0.wireOp",EDGE,"E3.11.2"),sQuery(id+"F0.wireOp",EDGE,"E3.11.3"),sQuery(id+"F0.wireOp",EDGE,"E3.12.1"),sQuery(id+"F0.wireOp",EDGE,"E3.12.2"),sQuery(id+"F0.wireOp",EDGE,"E3.12.3")])],"isStart":true})]}),makeQuery(id+"F1.opExtrude","CAP_EDGE",EDGE,{"disambiguationData":[OSD([subQ0])],"isStart":true})],"blendedInto":[]});}
            var Q72;
            {var subQ0=sQuery(id+"F0.wireOp",EDGE,"E3.2.2");var subQ1=sQuery(id+"F0.wireOp",EDGE,"E3.2.3");Q72=makeQuery(id+"F4.opChamfer","BLEND_EDGE",EDGE,{"blendedFrom":[makeQuery(id+"F3.opChamfer","BLEND_EDGE",EDGE,{"blendedFrom":[makeQuery(id+"F1.opExtrude","SWEPT_EDGE",EDGE,{"disambiguationData":[OSD([subQ0,subQ1])]}),makeQuery(id+"F1.opExtrude","CAP_FACE",FACE,{"disambiguationData":[OSD([sQuery(id+"F0.wireOp",EDGE,"E0"),sQuery(id+"F0.wireOp",EDGE,"E1"),sQuery(id+"F0.wireOp",EDGE,"E2.bottom"),sQuery(id+"F0.wireOp",EDGE,"E2.left"),sQuery(id+"F0.wireOp",EDGE,"E2.right"),sQuery(id+"F0.wireOp",EDGE,"E3.1.1"),sQuery(id+"F0.wireOp",EDGE,"E3.1.2"),sQuery(id+"F0.wireOp",EDGE,"E3.1.3"),sQuery(id+"F0.wireOp",EDGE,"E3.2.1"),subQ0,subQ1,sQuery(id+"F0.wireOp",EDGE,"E3.3.1"),sQuery(id+"F0.wireOp",EDGE,"E3.3.2"),sQuery(id+"F0.wireOp",EDGE,"E3.3.3"),sQuery(id+"F0.wireOp",EDGE,"E3.4.1"),sQuery(id+"F0.wireOp",EDGE,"E3.4.2"),sQuery(id+"F0.wireOp",EDGE,"E3.4.3"),sQuery(id+"F0.wireOp",EDGE,"E3.5.1"),sQuery(id+"F0.wireOp",EDGE,"E3.5.2"),sQuery(id+"F0.wireOp",EDGE,"E3.5.3"),sQuery(id+"F0.wireOp",EDGE,"E3.6.1"),sQuery(id+"F0.wireOp",EDGE,"E3.6.2"),sQuery(id+"F0.wireOp",EDGE,"E3.6.3"),sQuery(id+"F0.wireOp",EDGE,"E3.7.1"),sQuery(id+"F0.wireOp",EDGE,"E3.7.2"),sQuery(id+"F0.wireOp",EDGE,"E3.7.3"),sQuery(id+"F0.wireOp",EDGE,"E3.8.1"),sQuery(id+"F0.wireOp",EDGE,"E3.8.2"),sQuery(id+"F0.wireOp",EDGE,"E3.8.3"),sQuery(id+"F0.wireOp",EDGE,"E3.9.1"),sQuery(id+"F0.wireOp",EDGE,"E3.9.2"),sQuery(id+"F0.wireOp",EDGE,"E3.9.3"),sQuery(id+"F0.wireOp",EDGE,"E3.10.1"),sQuery(id+"F0.wireOp",EDGE,"E3.10.2"),sQuery(id+"F0.wireOp",EDGE,"E3.10.3"),sQuery(id+"F0.wireOp",EDGE,"E3.11.1"),sQuery(id+"F0.wireOp",EDGE,"E3.11.2"),sQuery(id+"F0.wireOp",EDGE,"E3.11.3"),sQuery(id+"F0.wireOp",EDGE,"E3.12.1"),sQuery(id+"F0.wireOp",EDGE,"E3.12.2"),sQuery(id+"F0.wireOp",EDGE,"E3.12.3")])],"isStart":true})],"blendedInto":[makeQuery(id+"F1.opExtrude","CAP_FACE",FACE,{"disambiguationData":[OSD([sQuery(id+"F0.wireOp",EDGE,"E0"),sQuery(id+"F0.wireOp",EDGE,"E1"),sQuery(id+"F0.wireOp",EDGE,"E2.bottom"),sQuery(id+"F0.wireOp",EDGE,"E2.left"),sQuery(id+"F0.wireOp",EDGE,"E2.right"),sQuery(id+"F0.wireOp",EDGE,"E3.1.1"),sQuery(id+"F0.wireOp",EDGE,"E3.1.2"),sQuery(id+"F0.wireOp",EDGE,"E3.1.3"),sQuery(id+"F0.wireOp",EDGE,"E3.2.1"),subQ0,subQ1,sQuery(id+"F0.wireOp",EDGE,"E3.3.1"),sQuery(id+"F0.wireOp",EDGE,"E3.3.2"),sQuery(id+"F0.wireOp",EDGE,"E3.3.3"),sQuery(id+"F0.wireOp",EDGE,"E3.4.1"),sQuery(id+"F0.wireOp",EDGE,"E3.4.2"),sQuery(id+"F0.wireOp",EDGE,"E3.4.3"),sQuery(id+"F0.wireOp",EDGE,"E3.5.1"),sQuery(id+"F0.wireOp",EDGE,"E3.5.2"),sQuery(id+"F0.wireOp",EDGE,"E3.5.3"),sQuery(id+"F0.wireOp",EDGE,"E3.6.1"),sQuery(id+"F0.wireOp",EDGE,"E3.6.2"),sQuery(id+"F0.wireOp",EDGE,"E3.6.3"),sQuery(id+"F0.wireOp",EDGE,"E3.7.1"),sQuery(id+"F0.wireOp",EDGE,"E3.7.2"),sQuery(id+"F0.wireOp",EDGE,"E3.7.3"),sQuery(id+"F0.wireOp",EDGE,"E3.8.1"),sQuery(id+"F0.wireOp",EDGE,"E3.8.2"),sQuery(id+"F0.wireOp",EDGE,"E3.8.3"),sQuery(id+"F0.wireOp",EDGE,"E3.9.1"),sQuery(id+"F0.wireOp",EDGE,"E3.9.2"),sQuery(id+"F0.wireOp",EDGE,"E3.9.3"),sQuery(id+"F0.wireOp",EDGE,"E3.10.1"),sQuery(id+"F0.wireOp",EDGE,"E3.10.2"),sQuery(id+"F0.wireOp",EDGE,"E3.10.3"),sQuery(id+"F0.wireOp",EDGE,"E3.11.1"),sQuery(id+"F0.wireOp",EDGE,"E3.11.2"),sQuery(id+"F0.wireOp",EDGE,"E3.11.3"),sQuery(id+"F0.wireOp",EDGE,"E3.12.1"),sQuery(id+"F0.wireOp",EDGE,"E3.12.2"),sQuery(id+"F0.wireOp",EDGE,"E3.12.3")])],"isStart":true})]}),makeQuery(id+"F1.opExtrude","CAP_EDGE",EDGE,{"disambiguationData":[OSD([subQ0])],"isStart":true})],"blendedInto":[]});}
            var Q73;
            {var subQ0=sQuery(id+"F0.wireOp",EDGE,"E3.2.2");var subQ1=sQuery(id+"F0.wireOp",EDGE,"E3.2.1");Q73=makeQuery(id+"F4.opChamfer","BLEND_EDGE",EDGE,{"blendedFrom":[makeQuery(id+"F3.opChamfer","BLEND_EDGE",EDGE,{"blendedFrom":[makeQuery(id+"F1.opExtrude","SWEPT_EDGE",EDGE,{"disambiguationData":[OSD([subQ1,subQ0])]}),makeQuery(id+"F1.opExtrude","CAP_FACE",FACE,{"disambiguationData":[OSD([sQuery(id+"F0.wireOp",EDGE,"E0"),sQuery(id+"F0.wireOp",EDGE,"E1"),sQuery(id+"F0.wireOp",EDGE,"E2.bottom"),sQuery(id+"F0.wireOp",EDGE,"E2.left"),sQuery(id+"F0.wireOp",EDGE,"E2.right"),sQuery(id+"F0.wireOp",EDGE,"E3.1.1"),sQuery(id+"F0.wireOp",EDGE,"E3.1.2"),sQuery(id+"F0.wireOp",EDGE,"E3.1.3"),subQ1,subQ0,sQuery(id+"F0.wireOp",EDGE,"E3.2.3"),sQuery(id+"F0.wireOp",EDGE,"E3.3.1"),sQuery(id+"F0.wireOp",EDGE,"E3.3.2"),sQuery(id+"F0.wireOp",EDGE,"E3.3.3"),sQuery(id+"F0.wireOp",EDGE,"E3.4.1"),sQuery(id+"F0.wireOp",EDGE,"E3.4.2"),sQuery(id+"F0.wireOp",EDGE,"E3.4.3"),sQuery(id+"F0.wireOp",EDGE,"E3.5.1"),sQuery(id+"F0.wireOp",EDGE,"E3.5.2"),sQuery(id+"F0.wireOp",EDGE,"E3.5.3"),sQuery(id+"F0.wireOp",EDGE,"E3.6.1"),sQuery(id+"F0.wireOp",EDGE,"E3.6.2"),sQuery(id+"F0.wireOp",EDGE,"E3.6.3"),sQuery(id+"F0.wireOp",EDGE,"E3.7.1"),sQuery(id+"F0.wireOp",EDGE,"E3.7.2"),sQuery(id+"F0.wireOp",EDGE,"E3.7.3"),sQuery(id+"F0.wireOp",EDGE,"E3.8.1"),sQuery(id+"F0.wireOp",EDGE,"E3.8.2"),sQuery(id+"F0.wireOp",EDGE,"E3.8.3"),sQuery(id+"F0.wireOp",EDGE,"E3.9.1"),sQuery(id+"F0.wireOp",EDGE,"E3.9.2"),sQuery(id+"F0.wireOp",EDGE,"E3.9.3"),sQuery(id+"F0.wireOp",EDGE,"E3.10.1"),sQuery(id+"F0.wireOp",EDGE,"E3.10.2"),sQuery(id+"F0.wireOp",EDGE,"E3.10.3"),sQuery(id+"F0.wireOp",EDGE,"E3.11.1"),sQuery(id+"F0.wireOp",EDGE,"E3.11.2"),sQuery(id+"F0.wireOp",EDGE,"E3.11.3"),sQuery(id+"F0.wireOp",EDGE,"E3.12.1"),sQuery(id+"F0.wireOp",EDGE,"E3.12.2"),sQuery(id+"F0.wireOp",EDGE,"E3.12.3")])],"isStart":true})],"blendedInto":[makeQuery(id+"F1.opExtrude","CAP_FACE",FACE,{"disambiguationData":[OSD([sQuery(id+"F0.wireOp",EDGE,"E0"),sQuery(id+"F0.wireOp",EDGE,"E1"),sQuery(id+"F0.wireOp",EDGE,"E2.bottom"),sQuery(id+"F0.wireOp",EDGE,"E2.left"),sQuery(id+"F0.wireOp",EDGE,"E2.right"),sQuery(id+"F0.wireOp",EDGE,"E3.1.1"),sQuery(id+"F0.wireOp",EDGE,"E3.1.2"),sQuery(id+"F0.wireOp",EDGE,"E3.1.3"),subQ1,subQ0,sQuery(id+"F0.wireOp",EDGE,"E3.2.3"),sQuery(id+"F0.wireOp",EDGE,"E3.3.1"),sQuery(id+"F0.wireOp",EDGE,"E3.3.2"),sQuery(id+"F0.wireOp",EDGE,"E3.3.3"),sQuery(id+"F0.wireOp",EDGE,"E3.4.1"),sQuery(id+"F0.wireOp",EDGE,"E3.4.2"),sQuery(id+"F0.wireOp",EDGE,"E3.4.3"),sQuery(id+"F0.wireOp",EDGE,"E3.5.1"),sQuery(id+"F0.wireOp",EDGE,"E3.5.2"),sQuery(id+"F0.wireOp",EDGE,"E3.5.3"),sQuery(id+"F0.wireOp",EDGE,"E3.6.1"),sQuery(id+"F0.wireOp",EDGE,"E3.6.2"),sQuery(id+"F0.wireOp",EDGE,"E3.6.3"),sQuery(id+"F0.wireOp",EDGE,"E3.7.1"),sQuery(id+"F0.wireOp",EDGE,"E3.7.2"),sQuery(id+"F0.wireOp",EDGE,"E3.7.3"),sQuery(id+"F0.wireOp",EDGE,"E3.8.1"),sQuery(id+"F0.wireOp",EDGE,"E3.8.2"),sQuery(id+"F0.wireOp",EDGE,"E3.8.3"),sQuery(id+"F0.wireOp",EDGE,"E3.9.1"),sQuery(id+"F0.wireOp",EDGE,"E3.9.2"),sQuery(id+"F0.wireOp",EDGE,"E3.9.3"),sQuery(id+"F0.wireOp",EDGE,"E3.10.1"),sQuery(id+"F0.wireOp",EDGE,"E3.10.2"),sQuery(id+"F0.wireOp",EDGE,"E3.10.3"),sQuery(id+"F0.wireOp",EDGE,"E3.11.1"),sQuery(id+"F0.wireOp",EDGE,"E3.11.2"),sQuery(id+"F0.wireOp",EDGE,"E3.11.3"),sQuery(id+"F0.wireOp",EDGE,"E3.12.1"),sQuery(id+"F0.wireOp",EDGE,"E3.12.2"),sQuery(id+"F0.wireOp",EDGE,"E3.12.3")])],"isStart":true})]}),makeQuery(id+"F1.opExtrude","CAP_EDGE",EDGE,{"disambiguationData":[OSD([subQ0])],"isStart":true})],"blendedInto":[]});}
            var Q74;
            {var subQ0=sQuery(id+"F0.wireOp",EDGE,"E3.1.2");var subQ1=sQuery(id+"F0.wireOp",EDGE,"E3.1.3");Q74=makeQuery(id+"F4.opChamfer","BLEND_EDGE",EDGE,{"blendedFrom":[makeQuery(id+"F3.opChamfer","BLEND_EDGE",EDGE,{"blendedFrom":[makeQuery(id+"F1.opExtrude","SWEPT_EDGE",EDGE,{"disambiguationData":[OSD([subQ0,subQ1])]}),makeQuery(id+"F1.opExtrude","CAP_FACE",FACE,{"disambiguationData":[OSD([sQuery(id+"F0.wireOp",EDGE,"E0"),sQuery(id+"F0.wireOp",EDGE,"E1"),sQuery(id+"F0.wireOp",EDGE,"E2.bottom"),sQuery(id+"F0.wireOp",EDGE,"E2.left"),sQuery(id+"F0.wireOp",EDGE,"E2.right"),sQuery(id+"F0.wireOp",EDGE,"E3.1.1"),subQ0,subQ1,sQuery(id+"F0.wireOp",EDGE,"E3.2.1"),sQuery(id+"F0.wireOp",EDGE,"E3.2.2"),sQuery(id+"F0.wireOp",EDGE,"E3.2.3"),sQuery(id+"F0.wireOp",EDGE,"E3.3.1"),sQuery(id+"F0.wireOp",EDGE,"E3.3.2"),sQuery(id+"F0.wireOp",EDGE,"E3.3.3"),sQuery(id+"F0.wireOp",EDGE,"E3.4.1"),sQuery(id+"F0.wireOp",EDGE,"E3.4.2"),sQuery(id+"F0.wireOp",EDGE,"E3.4.3"),sQuery(id+"F0.wireOp",EDGE,"E3.5.1"),sQuery(id+"F0.wireOp",EDGE,"E3.5.2"),sQuery(id+"F0.wireOp",EDGE,"E3.5.3"),sQuery(id+"F0.wireOp",EDGE,"E3.6.1"),sQuery(id+"F0.wireOp",EDGE,"E3.6.2"),sQuery(id+"F0.wireOp",EDGE,"E3.6.3"),sQuery(id+"F0.wireOp",EDGE,"E3.7.1"),sQuery(id+"F0.wireOp",EDGE,"E3.7.2"),sQuery(id+"F0.wireOp",EDGE,"E3.7.3"),sQuery(id+"F0.wireOp",EDGE,"E3.8.1"),sQuery(id+"F0.wireOp",EDGE,"E3.8.2"),sQuery(id+"F0.wireOp",EDGE,"E3.8.3"),sQuery(id+"F0.wireOp",EDGE,"E3.9.1"),sQuery(id+"F0.wireOp",EDGE,"E3.9.2"),sQuery(id+"F0.wireOp",EDGE,"E3.9.3"),sQuery(id+"F0.wireOp",EDGE,"E3.10.1"),sQuery(id+"F0.wireOp",EDGE,"E3.10.2"),sQuery(id+"F0.wireOp",EDGE,"E3.10.3"),sQuery(id+"F0.wireOp",EDGE,"E3.11.1"),sQuery(id+"F0.wireOp",EDGE,"E3.11.2"),sQuery(id+"F0.wireOp",EDGE,"E3.11.3"),sQuery(id+"F0.wireOp",EDGE,"E3.12.1"),sQuery(id+"F0.wireOp",EDGE,"E3.12.2"),sQuery(id+"F0.wireOp",EDGE,"E3.12.3")])],"isStart":true})],"blendedInto":[makeQuery(id+"F1.opExtrude","CAP_FACE",FACE,{"disambiguationData":[OSD([sQuery(id+"F0.wireOp",EDGE,"E0"),sQuery(id+"F0.wireOp",EDGE,"E1"),sQuery(id+"F0.wireOp",EDGE,"E2.bottom"),sQuery(id+"F0.wireOp",EDGE,"E2.left"),sQuery(id+"F0.wireOp",EDGE,"E2.right"),sQuery(id+"F0.wireOp",EDGE,"E3.1.1"),subQ0,subQ1,sQuery(id+"F0.wireOp",EDGE,"E3.2.1"),sQuery(id+"F0.wireOp",EDGE,"E3.2.2"),sQuery(id+"F0.wireOp",EDGE,"E3.2.3"),sQuery(id+"F0.wireOp",EDGE,"E3.3.1"),sQuery(id+"F0.wireOp",EDGE,"E3.3.2"),sQuery(id+"F0.wireOp",EDGE,"E3.3.3"),sQuery(id+"F0.wireOp",EDGE,"E3.4.1"),sQuery(id+"F0.wireOp",EDGE,"E3.4.2"),sQuery(id+"F0.wireOp",EDGE,"E3.4.3"),sQuery(id+"F0.wireOp",EDGE,"E3.5.1"),sQuery(id+"F0.wireOp",EDGE,"E3.5.2"),sQuery(id+"F0.wireOp",EDGE,"E3.5.3"),sQuery(id+"F0.wireOp",EDGE,"E3.6.1"),sQuery(id+"F0.wireOp",EDGE,"E3.6.2"),sQuery(id+"F0.wireOp",EDGE,"E3.6.3"),sQuery(id+"F0.wireOp",EDGE,"E3.7.1"),sQuery(id+"F0.wireOp",EDGE,"E3.7.2"),sQuery(id+"F0.wireOp",EDGE,"E3.7.3"),sQuery(id+"F0.wireOp",EDGE,"E3.8.1"),sQuery(id+"F0.wireOp",EDGE,"E3.8.2"),sQuery(id+"F0.wireOp",EDGE,"E3.8.3"),sQuery(id+"F0.wireOp",EDGE,"E3.9.1"),sQuery(id+"F0.wireOp",EDGE,"E3.9.2"),sQuery(id+"F0.wireOp",EDGE,"E3.9.3"),sQuery(id+"F0.wireOp",EDGE,"E3.10.1"),sQuery(id+"F0.wireOp",EDGE,"E3.10.2"),sQuery(id+"F0.wireOp",EDGE,"E3.10.3"),sQuery(id+"F0.wireOp",EDGE,"E3.11.1"),sQuery(id+"F0.wireOp",EDGE,"E3.11.2"),sQuery(id+"F0.wireOp",EDGE,"E3.11.3"),sQuery(id+"F0.wireOp",EDGE,"E3.12.1"),sQuery(id+"F0.wireOp",EDGE,"E3.12.2"),sQuery(id+"F0.wireOp",EDGE,"E3.12.3")])],"isStart":true})]}),makeQuery(id+"F1.opExtrude","CAP_EDGE",EDGE,{"disambiguationData":[OSD([subQ0])],"isStart":true})],"blendedInto":[]});}
            var Q75;
            {var subQ0=sQuery(id+"F0.wireOp",EDGE,"E3.1.2");var subQ1=sQuery(id+"F0.wireOp",EDGE,"E3.1.1");Q75=makeQuery(id+"F4.opChamfer","BLEND_EDGE",EDGE,{"blendedFrom":[makeQuery(id+"F3.opChamfer","BLEND_EDGE",EDGE,{"blendedFrom":[makeQuery(id+"F1.opExtrude","SWEPT_EDGE",EDGE,{"disambiguationData":[OSD([subQ1,subQ0])]}),makeQuery(id+"F1.opExtrude","CAP_FACE",FACE,{"disambiguationData":[OSD([sQuery(id+"F0.wireOp",EDGE,"E0"),sQuery(id+"F0.wireOp",EDGE,"E1"),sQuery(id+"F0.wireOp",EDGE,"E2.bottom"),sQuery(id+"F0.wireOp",EDGE,"E2.left"),sQuery(id+"F0.wireOp",EDGE,"E2.right"),subQ1,subQ0,sQuery(id+"F0.wireOp",EDGE,"E3.1.3"),sQuery(id+"F0.wireOp",EDGE,"E3.2.1"),sQuery(id+"F0.wireOp",EDGE,"E3.2.2"),sQuery(id+"F0.wireOp",EDGE,"E3.2.3"),sQuery(id+"F0.wireOp",EDGE,"E3.3.1"),sQuery(id+"F0.wireOp",EDGE,"E3.3.2"),sQuery(id+"F0.wireOp",EDGE,"E3.3.3"),sQuery(id+"F0.wireOp",EDGE,"E3.4.1"),sQuery(id+"F0.wireOp",EDGE,"E3.4.2"),sQuery(id+"F0.wireOp",EDGE,"E3.4.3"),sQuery(id+"F0.wireOp",EDGE,"E3.5.1"),sQuery(id+"F0.wireOp",EDGE,"E3.5.2"),sQuery(id+"F0.wireOp",EDGE,"E3.5.3"),sQuery(id+"F0.wireOp",EDGE,"E3.6.1"),sQuery(id+"F0.wireOp",EDGE,"E3.6.2"),sQuery(id+"F0.wireOp",EDGE,"E3.6.3"),sQuery(id+"F0.wireOp",EDGE,"E3.7.1"),sQuery(id+"F0.wireOp",EDGE,"E3.7.2"),sQuery(id+"F0.wireOp",EDGE,"E3.7.3"),sQuery(id+"F0.wireOp",EDGE,"E3.8.1"),sQuery(id+"F0.wireOp",EDGE,"E3.8.2"),sQuery(id+"F0.wireOp",EDGE,"E3.8.3"),sQuery(id+"F0.wireOp",EDGE,"E3.9.1"),sQuery(id+"F0.wireOp",EDGE,"E3.9.2"),sQuery(id+"F0.wireOp",EDGE,"E3.9.3"),sQuery(id+"F0.wireOp",EDGE,"E3.10.1"),sQuery(id+"F0.wireOp",EDGE,"E3.10.2"),sQuery(id+"F0.wireOp",EDGE,"E3.10.3"),sQuery(id+"F0.wireOp",EDGE,"E3.11.1"),sQuery(id+"F0.wireOp",EDGE,"E3.11.2"),sQuery(id+"F0.wireOp",EDGE,"E3.11.3"),sQuery(id+"F0.wireOp",EDGE,"E3.12.1"),sQuery(id+"F0.wireOp",EDGE,"E3.12.2"),sQuery(id+"F0.wireOp",EDGE,"E3.12.3")])],"isStart":true})],"blendedInto":[makeQuery(id+"F1.opExtrude","CAP_FACE",FACE,{"disambiguationData":[OSD([sQuery(id+"F0.wireOp",EDGE,"E0"),sQuery(id+"F0.wireOp",EDGE,"E1"),sQuery(id+"F0.wireOp",EDGE,"E2.bottom"),sQuery(id+"F0.wireOp",EDGE,"E2.left"),sQuery(id+"F0.wireOp",EDGE,"E2.right"),subQ1,subQ0,sQuery(id+"F0.wireOp",EDGE,"E3.1.3"),sQuery(id+"F0.wireOp",EDGE,"E3.2.1"),sQuery(id+"F0.wireOp",EDGE,"E3.2.2"),sQuery(id+"F0.wireOp",EDGE,"E3.2.3"),sQuery(id+"F0.wireOp",EDGE,"E3.3.1"),sQuery(id+"F0.wireOp",EDGE,"E3.3.2"),sQuery(id+"F0.wireOp",EDGE,"E3.3.3"),sQuery(id+"F0.wireOp",EDGE,"E3.4.1"),sQuery(id+"F0.wireOp",EDGE,"E3.4.2"),sQuery(id+"F0.wireOp",EDGE,"E3.4.3"),sQuery(id+"F0.wireOp",EDGE,"E3.5.1"),sQuery(id+"F0.wireOp",EDGE,"E3.5.2"),sQuery(id+"F0.wireOp",EDGE,"E3.5.3"),sQuery(id+"F0.wireOp",EDGE,"E3.6.1"),sQuery(id+"F0.wireOp",EDGE,"E3.6.2"),sQuery(id+"F0.wireOp",EDGE,"E3.6.3"),sQuery(id+"F0.wireOp",EDGE,"E3.7.1"),sQuery(id+"F0.wireOp",EDGE,"E3.7.2"),sQuery(id+"F0.wireOp",EDGE,"E3.7.3"),sQuery(id+"F0.wireOp",EDGE,"E3.8.1"),sQuery(id+"F0.wireOp",EDGE,"E3.8.2"),sQuery(id+"F0.wireOp",EDGE,"E3.8.3"),sQuery(id+"F0.wireOp",EDGE,"E3.9.1"),sQuery(id+"F0.wireOp",EDGE,"E3.9.2"),sQuery(id+"F0.wireOp",EDGE,"E3.9.3"),sQuery(id+"F0.wireOp",EDGE,"E3.10.1"),sQuery(id+"F0.wireOp",EDGE,"E3.10.2"),sQuery(id+"F0.wireOp",EDGE,"E3.10.3"),sQuery(id+"F0.wireOp",EDGE,"E3.11.1"),sQuery(id+"F0.wireOp",EDGE,"E3.11.2"),sQuery(id+"F0.wireOp",EDGE,"E3.11.3"),sQuery(id+"F0.wireOp",EDGE,"E3.12.1"),sQuery(id+"F0.wireOp",EDGE,"E3.12.2"),sQuery(id+"F0.wireOp",EDGE,"E3.12.3")])],"isStart":true})]}),makeQuery(id+"F1.opExtrude","CAP_EDGE",EDGE,{"disambiguationData":[OSD([subQ0])],"isStart":true})],"blendedInto":[]});}
            var Q76;
            {var subQ0=sQuery(id+"F0.wireOp",EDGE,"E2.bottom");var subQ1=sQuery(id+"F0.wireOp",EDGE,"E2.right");Q76=makeQuery(id+"F4.opChamfer","BLEND_EDGE",EDGE,{"blendedFrom":[makeQuery(id+"F3.opChamfer","BLEND_EDGE",EDGE,{"blendedFrom":[makeQuery(id+"F1.opExtrude","SWEPT_EDGE",EDGE,{"disambiguationData":[OSD([subQ0,subQ1])]}),makeQuery(id+"F1.opExtrude","CAP_FACE",FACE,{"disambiguationData":[OSD([sQuery(id+"F0.wireOp",EDGE,"E0"),sQuery(id+"F0.wireOp",EDGE,"E1"),subQ0,sQuery(id+"F0.wireOp",EDGE,"E2.left"),subQ1,sQuery(id+"F0.wireOp",EDGE,"E3.1.1"),sQuery(id+"F0.wireOp",EDGE,"E3.1.2"),sQuery(id+"F0.wireOp",EDGE,"E3.1.3"),sQuery(id+"F0.wireOp",EDGE,"E3.2.1"),sQuery(id+"F0.wireOp",EDGE,"E3.2.2"),sQuery(id+"F0.wireOp",EDGE,"E3.2.3"),sQuery(id+"F0.wireOp",EDGE,"E3.3.1"),sQuery(id+"F0.wireOp",EDGE,"E3.3.2"),sQuery(id+"F0.wireOp",EDGE,"E3.3.3"),sQuery(id+"F0.wireOp",EDGE,"E3.4.1"),sQuery(id+"F0.wireOp",EDGE,"E3.4.2"),sQuery(id+"F0.wireOp",EDGE,"E3.4.3"),sQuery(id+"F0.wireOp",EDGE,"E3.5.1"),sQuery(id+"F0.wireOp",EDGE,"E3.5.2"),sQuery(id+"F0.wireOp",EDGE,"E3.5.3"),sQuery(id+"F0.wireOp",EDGE,"E3.6.1"),sQuery(id+"F0.wireOp",EDGE,"E3.6.2"),sQuery(id+"F0.wireOp",EDGE,"E3.6.3"),sQuery(id+"F0.wireOp",EDGE,"E3.7.1"),sQuery(id+"F0.wireOp",EDGE,"E3.7.2"),sQuery(id+"F0.wireOp",EDGE,"E3.7.3"),sQuery(id+"F0.wireOp",EDGE,"E3.8.1"),sQuery(id+"F0.wireOp",EDGE,"E3.8.2"),sQuery(id+"F0.wireOp",EDGE,"E3.8.3"),sQuery(id+"F0.wireOp",EDGE,"E3.9.1"),sQuery(id+"F0.wireOp",EDGE,"E3.9.2"),sQuery(id+"F0.wireOp",EDGE,"E3.9.3"),sQuery(id+"F0.wireOp",EDGE,"E3.10.1"),sQuery(id+"F0.wireOp",EDGE,"E3.10.2"),sQuery(id+"F0.wireOp",EDGE,"E3.10.3"),sQuery(id+"F0.wireOp",EDGE,"E3.11.1"),sQuery(id+"F0.wireOp",EDGE,"E3.11.2"),sQuery(id+"F0.wireOp",EDGE,"E3.11.3"),sQuery(id+"F0.wireOp",EDGE,"E3.12.1"),sQuery(id+"F0.wireOp",EDGE,"E3.12.2"),sQuery(id+"F0.wireOp",EDGE,"E3.12.3")])],"isStart":true})],"blendedInto":[makeQuery(id+"F1.opExtrude","CAP_FACE",FACE,{"disambiguationData":[OSD([sQuery(id+"F0.wireOp",EDGE,"E0"),sQuery(id+"F0.wireOp",EDGE,"E1"),subQ0,sQuery(id+"F0.wireOp",EDGE,"E2.left"),subQ1,sQuery(id+"F0.wireOp",EDGE,"E3.1.1"),sQuery(id+"F0.wireOp",EDGE,"E3.1.2"),sQuery(id+"F0.wireOp",EDGE,"E3.1.3"),sQuery(id+"F0.wireOp",EDGE,"E3.2.1"),sQuery(id+"F0.wireOp",EDGE,"E3.2.2"),sQuery(id+"F0.wireOp",EDGE,"E3.2.3"),sQuery(id+"F0.wireOp",EDGE,"E3.3.1"),sQuery(id+"F0.wireOp",EDGE,"E3.3.2"),sQuery(id+"F0.wireOp",EDGE,"E3.3.3"),sQuery(id+"F0.wireOp",EDGE,"E3.4.1"),sQuery(id+"F0.wireOp",EDGE,"E3.4.2"),sQuery(id+"F0.wireOp",EDGE,"E3.4.3"),sQuery(id+"F0.wireOp",EDGE,"E3.5.1"),sQuery(id+"F0.wireOp",EDGE,"E3.5.2"),sQuery(id+"F0.wireOp",EDGE,"E3.5.3"),sQuery(id+"F0.wireOp",EDGE,"E3.6.1"),sQuery(id+"F0.wireOp",EDGE,"E3.6.2"),sQuery(id+"F0.wireOp",EDGE,"E3.6.3"),sQuery(id+"F0.wireOp",EDGE,"E3.7.1"),sQuery(id+"F0.wireOp",EDGE,"E3.7.2"),sQuery(id+"F0.wireOp",EDGE,"E3.7.3"),sQuery(id+"F0.wireOp",EDGE,"E3.8.1"),sQuery(id+"F0.wireOp",EDGE,"E3.8.2"),sQuery(id+"F0.wireOp",EDGE,"E3.8.3"),sQuery(id+"F0.wireOp",EDGE,"E3.9.1"),sQuery(id+"F0.wireOp",EDGE,"E3.9.2"),sQuery(id+"F0.wireOp",EDGE,"E3.9.3"),sQuery(id+"F0.wireOp",EDGE,"E3.10.1"),sQuery(id+"F0.wireOp",EDGE,"E3.10.2"),sQuery(id+"F0.wireOp",EDGE,"E3.10.3"),sQuery(id+"F0.wireOp",EDGE,"E3.11.1"),sQuery(id+"F0.wireOp",EDGE,"E3.11.2"),sQuery(id+"F0.wireOp",EDGE,"E3.11.3"),sQuery(id+"F0.wireOp",EDGE,"E3.12.1"),sQuery(id+"F0.wireOp",EDGE,"E3.12.2"),sQuery(id+"F0.wireOp",EDGE,"E3.12.3")])],"isStart":true})]}),makeQuery(id+"F1.opExtrude","CAP_EDGE",EDGE,{"disambiguationData":[OSD([subQ0])],"isStart":true})],"blendedInto":[]});}
            var Q77;
            {var subQ0=sQuery(id+"F0.wireOp",EDGE,"E2.bottom");var subQ1=sQuery(id+"F0.wireOp",EDGE,"E2.left");Q77=makeQuery(id+"F4.opChamfer","BLEND_EDGE",EDGE,{"blendedFrom":[makeQuery(id+"F3.opChamfer","BLEND_EDGE",EDGE,{"blendedFrom":[makeQuery(id+"F1.opExtrude","SWEPT_EDGE",EDGE,{"disambiguationData":[OSD([subQ0,subQ1])]}),makeQuery(id+"F1.opExtrude","CAP_FACE",FACE,{"disambiguationData":[OSD([sQuery(id+"F0.wireOp",EDGE,"E0"),sQuery(id+"F0.wireOp",EDGE,"E1"),subQ0,subQ1,sQuery(id+"F0.wireOp",EDGE,"E2.right"),sQuery(id+"F0.wireOp",EDGE,"E3.1.1"),sQuery(id+"F0.wireOp",EDGE,"E3.1.2"),sQuery(id+"F0.wireOp",EDGE,"E3.1.3"),sQuery(id+"F0.wireOp",EDGE,"E3.2.1"),sQuery(id+"F0.wireOp",EDGE,"E3.2.2"),sQuery(id+"F0.wireOp",EDGE,"E3.2.3"),sQuery(id+"F0.wireOp",EDGE,"E3.3.1"),sQuery(id+"F0.wireOp",EDGE,"E3.3.2"),sQuery(id+"F0.wireOp",EDGE,"E3.3.3"),sQuery(id+"F0.wireOp",EDGE,"E3.4.1"),sQuery(id+"F0.wireOp",EDGE,"E3.4.2"),sQuery(id+"F0.wireOp",EDGE,"E3.4.3"),sQuery(id+"F0.wireOp",EDGE,"E3.5.1"),sQuery(id+"F0.wireOp",EDGE,"E3.5.2"),sQuery(id+"F0.wireOp",EDGE,"E3.5.3"),sQuery(id+"F0.wireOp",EDGE,"E3.6.1"),sQuery(id+"F0.wireOp",EDGE,"E3.6.2"),sQuery(id+"F0.wireOp",EDGE,"E3.6.3"),sQuery(id+"F0.wireOp",EDGE,"E3.7.1"),sQuery(id+"F0.wireOp",EDGE,"E3.7.2"),sQuery(id+"F0.wireOp",EDGE,"E3.7.3"),sQuery(id+"F0.wireOp",EDGE,"E3.8.1"),sQuery(id+"F0.wireOp",EDGE,"E3.8.2"),sQuery(id+"F0.wireOp",EDGE,"E3.8.3"),sQuery(id+"F0.wireOp",EDGE,"E3.9.1"),sQuery(id+"F0.wireOp",EDGE,"E3.9.2"),sQuery(id+"F0.wireOp",EDGE,"E3.9.3"),sQuery(id+"F0.wireOp",EDGE,"E3.10.1"),sQuery(id+"F0.wireOp",EDGE,"E3.10.2"),sQuery(id+"F0.wireOp",EDGE,"E3.10.3"),sQuery(id+"F0.wireOp",EDGE,"E3.11.1"),sQuery(id+"F0.wireOp",EDGE,"E3.11.2"),sQuery(id+"F0.wireOp",EDGE,"E3.11.3"),sQuery(id+"F0.wireOp",EDGE,"E3.12.1"),sQuery(id+"F0.wireOp",EDGE,"E3.12.2"),sQuery(id+"F0.wireOp",EDGE,"E3.12.3")])],"isStart":true})],"blendedInto":[makeQuery(id+"F1.opExtrude","CAP_FACE",FACE,{"disambiguationData":[OSD([sQuery(id+"F0.wireOp",EDGE,"E0"),sQuery(id+"F0.wireOp",EDGE,"E1"),subQ0,subQ1,sQuery(id+"F0.wireOp",EDGE,"E2.right"),sQuery(id+"F0.wireOp",EDGE,"E3.1.1"),sQuery(id+"F0.wireOp",EDGE,"E3.1.2"),sQuery(id+"F0.wireOp",EDGE,"E3.1.3"),sQuery(id+"F0.wireOp",EDGE,"E3.2.1"),sQuery(id+"F0.wireOp",EDGE,"E3.2.2"),sQuery(id+"F0.wireOp",EDGE,"E3.2.3"),sQuery(id+"F0.wireOp",EDGE,"E3.3.1"),sQuery(id+"F0.wireOp",EDGE,"E3.3.2"),sQuery(id+"F0.wireOp",EDGE,"E3.3.3"),sQuery(id+"F0.wireOp",EDGE,"E3.4.1"),sQuery(id+"F0.wireOp",EDGE,"E3.4.2"),sQuery(id+"F0.wireOp",EDGE,"E3.4.3"),sQuery(id+"F0.wireOp",EDGE,"E3.5.1"),sQuery(id+"F0.wireOp",EDGE,"E3.5.2"),sQuery(id+"F0.wireOp",EDGE,"E3.5.3"),sQuery(id+"F0.wireOp",EDGE,"E3.6.1"),sQuery(id+"F0.wireOp",EDGE,"E3.6.2"),sQuery(id+"F0.wireOp",EDGE,"E3.6.3"),sQuery(id+"F0.wireOp",EDGE,"E3.7.1"),sQuery(id+"F0.wireOp",EDGE,"E3.7.2"),sQuery(id+"F0.wireOp",EDGE,"E3.7.3"),sQuery(id+"F0.wireOp",EDGE,"E3.8.1"),sQuery(id+"F0.wireOp",EDGE,"E3.8.2"),sQuery(id+"F0.wireOp",EDGE,"E3.8.3"),sQuery(id+"F0.wireOp",EDGE,"E3.9.1"),sQuery(id+"F0.wireOp",EDGE,"E3.9.2"),sQuery(id+"F0.wireOp",EDGE,"E3.9.3"),sQuery(id+"F0.wireOp",EDGE,"E3.10.1"),sQuery(id+"F0.wireOp",EDGE,"E3.10.2"),sQuery(id+"F0.wireOp",EDGE,"E3.10.3"),sQuery(id+"F0.wireOp",EDGE,"E3.11.1"),sQuery(id+"F0.wireOp",EDGE,"E3.11.2"),sQuery(id+"F0.wireOp",EDGE,"E3.11.3"),sQuery(id+"F0.wireOp",EDGE,"E3.12.1"),sQuery(id+"F0.wireOp",EDGE,"E3.12.2"),sQuery(id+"F0.wireOp",EDGE,"E3.12.3")])],"isStart":true})]}),makeQuery(id+"F1.opExtrude","CAP_EDGE",EDGE,{"disambiguationData":[OSD([subQ0])],"isStart":true})],"blendedInto":[]});}
            chamfer(context, id + "F12", {"entities" : qUnion([Q0, Q1, Q2, Q3, Q4, Q5, Q6, Q7, Q8, Q9, Q10, Q11, Q12, Q13, Q14, Q15, Q16, Q17, Q18, Q19, Q20, Q21, Q22, Q23, Q24, Q25, Q26, Q27, Q28, Q29, Q30, Q31, Q32, Q33, Q34, Q35, Q36, Q37, Q38, Q39, Q40, Q41, Q42, Q43, Q44, Q45, Q46, Q47, Q48, Q49, Q50, Q51, Q52, Q53, Q54, Q55, Q56, Q57, Q58, Q59, Q60, Q61, Q62, Q63, Q64, Q65, Q66, Q67, Q68, Q69, Q70, Q71, Q72, Q73, Q74, Q75, Q76, Q77]), "width" : 0.64 * mm, "tangentPropagation" : true});
        }
    });
